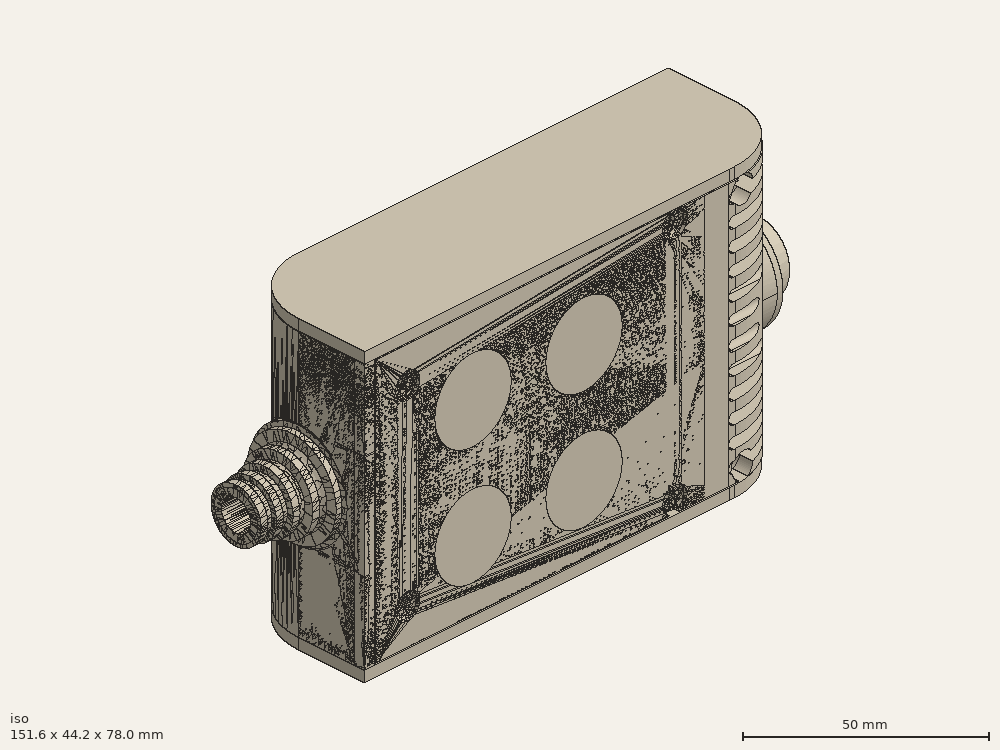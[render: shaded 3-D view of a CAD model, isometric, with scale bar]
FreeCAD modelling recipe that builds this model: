
FCSTD DOCUMENT  (FreeCAD 0.19R0.19.2)
Label: enclosure_197FCStd
License: All rights reserved
LicenseURL: http://en.wikipedia.org/wiki/All_rights_reserved
objects: Part::Revolution×152, Part::MultiFuse×146, Part::Feature×146, Sketcher::SketchObject×84, Part::Cut×70, Part::Cylinder×70, Part::Extrusion×67, Part::Fillet×58, Part::Box×36, App::MeasureDistance×4, PartDesign::Body×2, Image::ImagePlane×1
note: 831 computed .brp shape members not serialized (recipe doc carries the construction recipe); baked Part::Feature solids carry a one-line shape summary decoded from their .brp

FEATURE [Sketcher::SketchObject] Sketch  label="topSketch"
  FullyConstrained = true
  sketch-geometry (20):
    g0: LineSegment StartX=5.21097e-06 StartY=3 StartZ=0 EndX=5.21097e-06 EndY=19 EndZ=0
    g1: ArcOfCircle CenterX=19 CenterY=19 CenterZ=0 NormalX=0 NormalY=0 NormalZ=1 AngleXU=0 Radius=19 StartAngle=1.5708 EndAngle=3.14159
    g2: ArcOfCircle CenterX=19 CenterY=19 CenterZ=0 NormalX=0 NormalY=0 NormalZ=1 AngleXU=0 Radius=16 StartAngle=1.5708 EndAngle=3.14159
    g3: LineSegment StartX=114 StartY=35 StartZ=0 EndX=19 EndY=35 EndZ=0
    g4: LineSegment StartX=5.21097e-06 StartY=3 StartZ=0 EndX=5.21097e-06 EndY=0 EndZ=0
    g5: LineSegment StartX=3 StartY=0 StartZ=0 EndX=5.21097e-06 EndY=0 EndZ=0
    g6: LineSegment StartX=3 StartY=19 StartZ=0 EndX=3 EndY=0 EndZ=0
    g7: LineSegment StartX=19 StartY=38 StartZ=0 EndX=124 EndY=38 EndZ=0
    g8: Circle CenterX=119 CenterY=35 CenterZ=0 NormalX=0 NormalY=0 NormalZ=1 AngleXU=0 Radius=1
    g9: Circle CenterX=121 CenterY=35 CenterZ=0 NormalX=0 NormalY=0 NormalZ=1 AngleXU=0 Radius=1
    g10: Circle CenterX=121 CenterY=33 CenterZ=0 NormalX=0 NormalY=0 NormalZ=1 AngleXU=0 Radius=1
    g11: BSplineCurve PolesCount=3 KnotsCount=2 Degree=2 IsPeriodic=0
    g12: GeomPoint X=119 Y=35 Z=0
    g13: GeomPoint X=121 Y=33 Z=0
    g14: LineSegment StartX=119 StartY=35 StartZ=0 EndX=114 EndY=35 EndZ=0
    g15: ArcOfCircle CenterX=105 CenterY=19 CenterZ=0 NormalX=0 NormalY=0 NormalZ=1 AngleXU=0 Radius=19 StartAngle=5.7297 EndAngle=6.28319
    g16: ArcOfCircle CenterX=105 CenterY=19 CenterZ=0 NormalX=0 NormalY=0 NormalZ=1 AngleXU=0 Radius=16 StartAngle=5.60905 EndAngle=6.28319
    g17: LineSegment StartX=121 StartY=33 StartZ=0 EndX=121 EndY=19 EndZ=0
    g18: LineSegment StartX=124 StartY=38 StartZ=0 EndX=124 EndY=19 EndZ=0
    g19: LineSegment StartX=117.5 StartY=9.01251 StartZ=0 EndX=121.163 EndY=9.0125 EndZ=0
  constraints (46):
    c: Vertical(g0)
    c: Block(g0)
    c: Coincident(g1,g0)
    c: Block(g1)
    c: Coincident(g2,g1)
    c: Block(g2)
    c: Coincident(g3,g2)
    c: Horizontal(g3)
    c: Tangent(g3,g2)
    c: Coincident(g4,g0)
    c: Distance(g4) = 3
    c: Vertical(g4)
    c: Coincident(g5,g4)
    c: Horizontal(g5)
    c: Coincident(g6,g2)
    c: Coincident(g6,g5)
    c: Vertical(g6)
    c: Horizontal(g7)
    c: Distance(g7) = 105
    c: Coincident(g7,g1)
    c: Block(g3)
    c: Weight(g8) = 1
    c: Equal(g8,g9)
    c: Equal(g8,g10)
    c: InternalAlignment(g8,g11)
    c: InternalAlignment(g9,g11)
    c: InternalAlignment(g10,g11)
    c: InternalAlignment(g12,g11)
    c: InternalAlignment(g13,g11)
    c: Block(g11)
    c: Coincident(g14,g11)
    c: Coincident(g14,g3)
    c: Horizontal(g14)
    c: Block(g15)
    c: Coincident(g16,g15)
    c: Block(g16)
    c: Coincident(g17,g11)
    c: Coincident(g17,g16)
    c: Vertical(g17)
    c: Distance(g17) = 14
    c: Coincident(g18,g7)
    c: Coincident(g18,g15)
    c: Vertical(g18)
    c: Distance(g18) = 19
    c: Coincident(g19,g16)
    c: Coincident(g19,g15)
FEATURE [Sketcher::SketchObject] Sketch001  label="bottomSketch"
  FullyConstrained = true
  sketch-geometry (32):
    g0: LineSegment StartX=3.3 StartY=-6.03275e-07 StartZ=0 EndX=98 EndY=-6.03275e-07 EndZ=0
    g1: ArcOfCircle CenterX=98 CenterY=19 CenterZ=0 NormalX=0 NormalY=0 NormalZ=1 AngleXU=0 Radius=19 StartAngle=4.71239 EndAngle=5.71103
    g2: LineSegment StartX=6.3 StartY=8 StartZ=0 EndX=3.3 EndY=8 EndZ=0
    g3: LineSegment StartX=3.3 StartY=8 StartZ=0 EndX=3.3 EndY=-6.03275e-07 EndZ=0
    g4: ArcOfCircle CenterX=8.3 CenterY=5 CenterZ=0 NormalX=0 NormalY=0 NormalZ=1 AngleXU=0 Radius=2 StartAngle=3.14159 EndAngle=4.71239
    g5: LineSegment StartX=6.3 StartY=8 StartZ=0 EndX=6.3 EndY=5 EndZ=0
    g6: ArcOfCircle CenterX=98 CenterY=19 CenterZ=0 NormalX=0 NormalY=0 NormalZ=1 AngleXU=0 Radius=12.7 StartAngle=4.71239 EndAngle=6.28319
    g7: LineSegment StartX=94.7 StartY=3 StartZ=0 EndX=8.3 EndY=3 EndZ=0
    g8-g12: Circle x5 (B-spline internal-alignment scaffolding for g13; pole/knot coordinates omitted)
    g13: BSplineCurve PolesCount=5 KnotsCount=3 Degree=3 IsPeriodic=0
    g14: GeomPoint X=98 Y=6.3 Z=0
    g15: GeomPoint X=96.3938 Y=4.71946 Z=0
    g16: GeomPoint X=94.7 Y=3 Z=0
    g17-g23: Circle x7 (B-spline internal-alignment scaffolding for g24; pole/knot coordinates omitted)
    g24: BSplineCurve PolesCount=7 KnotsCount=5 Degree=3 IsPeriodic=0
    g25-g29: GeomPoint x5 (B-spline internal-alignment scaffolding for g24; pole/knot coordinates omitted)
    g30: ArcOfCircle CenterX=98 CenterY=19 CenterZ=0 NormalX=0 NormalY=0 NormalZ=1 AngleXU=0 Radius=15.7 StartAngle=5.81226 EndAngle=6.28319
    g31: LineSegment StartX=110.7 StartY=19 StartZ=0 EndX=113.7 EndY=19 EndZ=0
  constraints (41):
    c: Horizontal(g0)
    c: Coincident(g1,g0)
    c: Block(g1)
    c: Horizontal(g2)
    c: Distance(g2) = 3
    c: Coincident(g3,g2)
    c: Vertical(g3)
    c: Coincident(g3,g0)
    c: Block(g4)
    c: Block(g2)
    c: Coincident(g5,g2)
    c: Coincident(g5,g4)
    c: Vertical(g5)
    c: Coincident(g6,g1)
    c: Block(g6)
    c: Coincident(g7,g4)
    c: Horizontal(g7)
    c: Block(g0)
    c: Block(g7)
    c: Block(g3)
    c: Coincident(g13,g6)
    c: Weight(g8) = 1
    c: Equal(g8, g9-g12) x4
    c: Coincident(g13,g7)
    c: InternalAlignment(g8-g12 -> g13) x5
    c: InternalAlignment(g14,g13)
    c: InternalAlignment(g15,g13)
    c: InternalAlignment(g16,g13)
    c: Block(g13)
    c: Weight(g17) = 1
    c: Equal(g17, g18-g23) x6
    c: Coincident(g24,g1)
    c: InternalAlignment(g17-g23 -> g24) x7
    c: InternalAlignment(g25-g29 -> g24) x5
    c: Block(g24)
    c: Coincident(g30,g24)
    c: Coincident(g31,g6)
    c: Coincident(g31,g30)
    c: Horizontal(g31)
    c: Block(g31)
    c: Block(g30)
FEATURE [Part::Extrusion] Extrude  label="top"
  Base = -> Sketch
  Dir = (0,0,1)
  DirMode = 2
  FaceMakerClass = Part::FaceMakerBullseye
  LengthFwd = 72
  LengthRev = 0
  Solid = true
  Symmetric = false
FEATURE [Part::Extrusion] Extrude001  label="bottom"
  Base = -> Sketch001
  Dir = (0,0,1)
  DirMode = 2
  FaceMakerClass = Part::FaceMakerBullseye
  LengthFwd = 71.4
  LengthRev = 0
  Placement = pos=(0,0,0.3) rot=(0,0,1;0rad)
  Solid = true
  Symmetric = false
FEATURE [Sketcher::SketchObject] Sketch002  label="topSketch001"
  FullyConstrained = true
  sketch-geometry (8):
    g0: ArcOfCircle CenterX=19 CenterY=19.0975 CenterZ=0 NormalX=0 NormalY=0 NormalZ=1 AngleXU=0 Radius=18.9025 StartAngle=1.5708 EndAngle=3.14674
    g1: LineSegment StartX=0.0977805 StartY=19.0003 StartZ=0 EndX=0.0977805 EndY=0.000251602 EndZ=0
    g2: LineSegment StartX=19 StartY=38 StartZ=0 EndX=124 EndY=38 EndZ=0
    g3: LineSegment StartX=0.0977805 StartY=0.000251602 StartZ=0 EndX=105.098 EndY=0.000251602 EndZ=0
    g4: LineSegment StartX=124 StartY=38 StartZ=0 EndX=125.616 EndY=38 EndZ=0
    g5: LineSegment StartX=105.098 StartY=0.000251602 StartZ=0 EndX=106.713 EndY=0.000251602 EndZ=0
    g6: ArcOfCircle CenterX=106.616 CenterY=19 CenterZ=0 NormalX=0 NormalY=0 NormalZ=1 AngleXU=0 Radius=19 StartAngle=4.71754 EndAngle=6.28319
    g7: LineSegment StartX=125.616 StartY=38 StartZ=0 EndX=125.616 EndY=19 EndZ=0
  constraints (21):
    c: Block(g0)
    c: Coincident(g1,g0)
    c: Vertical(g1)
    c: Horizontal(g2)
    c: Distance(g2) = 105
    c: Coincident(g2,g0)
    c: Distance(g1) = 19
    c: Coincident(g3,g1)
    c: Horizontal(g3)
    c: Distance(g3) = 105
    c: Coincident(g4,g2)
    c: Horizontal(g4)
    c: Distance(g4) = 1.61553
    c: Horizontal(g5)
    c: Equal(g4,g5) = 1.61553
    c: Coincident(g5,g3)
    c: Block(g6)
    c: Coincident(g6,g5)
    c: Coincident(g7,g4)
    c: Coincident(g7,g6)
    c: Vertical(g7)
FEATURE [Part::Extrusion] Extrude002  label="sideA"
  Base = -> Sketch002
  Dir = (0,0,1)
  DirMode = 2
  FaceMakerClass = Part::FaceMakerBullseye
  LengthFwd = 3
  LengthRev = 0
  Placement = pos=(0,0,-3) rot=(0,0,1;0rad)
  Solid = true
  Symmetric = false
FEATURE [Sketcher::SketchObject] Sketch003  label="topSketch002"
  FullyConstrained = true
  sketch-geometry (6):
    g0: LineSegment StartX=19 StartY=38 StartZ=0 EndX=117 EndY=38 EndZ=0
    g1: ArcOfCircle CenterX=19 CenterY=19 CenterZ=0 NormalX=0 NormalY=0 NormalZ=1 AngleXU=0 Radius=19 StartAngle=1.5708 EndAngle=3.14159
    g2: LineSegment StartX=117 StartY=38 StartZ=0 EndX=117 EndY=19 EndZ=0
    g3: LineSegment StartX=98 StartY=1.0161e-12 StartZ=0 EndX=5.22862e-06 EndY=1.0161e-12 EndZ=0
    g4: LineSegment StartX=5.22862e-06 StartY=19 StartZ=0 EndX=5.22862e-06 EndY=1.0161e-12 EndZ=0
    g5: ArcOfCircle CenterX=98 CenterY=19 CenterZ=0 NormalX=0 NormalY=0 NormalZ=1 AngleXU=0 Radius=19 StartAngle=4.71239 EndAngle=6.28319
  constraints (16):
    c: Horizontal(g0)
    c: Distance(g0) = 98
    c: Coincident(g1,g0)
    c: Block(g1)
    c: Coincident(g2,g0)
    c: Vertical(g2)
    c: Distance(g2) = 19
    c: Horizontal(g3)
    c: Coincident(g4,g1)
    c: Vertical(g4)
    c: Coincident(g3,g4)
    c: Block(g3)
    c: Coincident(g5,g2)
    c: Coincident(g5,g3)
    c: Block(g0)
    c: Block(g5)
FEATURE [Sketcher::SketchObject] Sketch004
  FullyConstrained = true
  MapMode = 3
  Placement = pos=(0,0,0) rot=(1,0,0;1.5708rad)
  Support = -> [Extrude]
  sketch-geometry (8):
    g0: Circle CenterX=80.351 CenterY=-67.6202 CenterZ=0 NormalX=0 NormalY=0 NormalZ=1 AngleXU=0 Radius=2
    g1: Circle CenterX=80.351 CenterY=-67.6202 CenterZ=0 NormalX=0 NormalY=0 NormalZ=1 AngleXU=0 Radius=3
    g2: Circle CenterX=80.351 CenterY=-4.92017 CenterZ=0 NormalX=0 NormalY=0 NormalZ=1 AngleXU=0 Radius=2
    g3: Circle CenterX=80.351 CenterY=-4.92017 CenterZ=0 NormalX=0 NormalY=0 NormalZ=1 AngleXU=0 Radius=3
    g4: Circle CenterX=23.851 CenterY=-4.92017 CenterZ=0 NormalX=0 NormalY=0 NormalZ=1 AngleXU=0 Radius=2
    g5: Circle CenterX=23.851 CenterY=-4.92017 CenterZ=0 NormalX=0 NormalY=0 NormalZ=1 AngleXU=0 Radius=3
    g6: Circle CenterX=23.851 CenterY=-67.6202 CenterZ=0 NormalX=0 NormalY=0 NormalZ=1 AngleXU=0 Radius=2
    g7: Circle CenterX=23.851 CenterY=-67.6202 CenterZ=0 NormalX=0 NormalY=0 NormalZ=1 AngleXU=0 Radius=3
  constraints (8):
    c: Block(g3)
    c: Block(g2)
    c: Block(g1)
    c: Block(g0)
    c: Block(g6)
    c: Block(g7)
    c: Block(g4)
    c: Block(g5)
FEATURE [Part::Extrusion] Extrude004
  Base = -> Sketch004
  Dir = (0,-1,2e-16)
  DirMode = 2
  FaceMakerClass = Part::FaceMakerBullseye
  LengthFwd = 6
  LengthRev = 0
  Placement = pos=(0,9,0) rot=(0,0,1;0rad)
  Solid = true
  Symmetric = false
FEATURE [Sketcher::SketchObject] Sketch005
  FullyConstrained = true
  MapMode = 3
  Placement = pos=(0,0,0) rot=(1,0,0;1.5708rad)
  Support = -> [Extrude]
  sketch-geometry (8):
    g0: Circle CenterX=80.351 CenterY=-67.6202 CenterZ=0 NormalX=0 NormalY=0 NormalZ=1 AngleXU=0 Radius=3
    g1: Circle CenterX=80.351 CenterY=-4.92017 CenterZ=0 NormalX=0 NormalY=0 NormalZ=1 AngleXU=0 Radius=3
    g2: Circle CenterX=23.851 CenterY=-4.92017 CenterZ=0 NormalX=0 NormalY=0 NormalZ=1 AngleXU=0 Radius=3
    g3: Circle CenterX=23.851 CenterY=-67.6202 CenterZ=0 NormalX=0 NormalY=0 NormalZ=1 AngleXU=0 Radius=3
    g4: Circle CenterX=23.851 CenterY=-67.6202 CenterZ=0 NormalX=0 NormalY=0 NormalZ=1 AngleXU=0 Radius=5
    g5: Circle CenterX=80.351 CenterY=-67.6202 CenterZ=0 NormalX=0 NormalY=0 NormalZ=1 AngleXU=0 Radius=5
    g6: Circle CenterX=23.851 CenterY=-4.92017 CenterZ=0 NormalX=0 NormalY=0 NormalZ=1 AngleXU=0 Radius=5
    g7: Circle CenterX=80.351 CenterY=-4.92017 CenterZ=0 NormalX=0 NormalY=0 NormalZ=1 AngleXU=0 Radius=5
  constraints (8):
    c: Block(g1)
    c: Block(g0)
    c: Block(g3)
    c: Block(g2)
    c: Block(g5)
    c: Block(g4)
    c: Block(g6)
    c: Block(g7)
FEATURE [Part::Extrusion] Extrude005
  Base = -> Sketch005
  Dir = (0,-1,2e-16)
  DirMode = 2
  FaceMakerClass = Part::FaceMakerBullseye
  LengthFwd = 2
  LengthRev = 0
  Solid = true
  Symmetric = false
FEATURE [Sketcher::SketchObject] Sketch006
  FullyConstrained = true
  MapMode = 3
  Placement = pos=(0,0,0) rot=(1,0,0;1.5708rad)
  sketch-geometry (8):
    g0: Circle CenterX=80.351 CenterY=-67.6202 CenterZ=0 NormalX=0 NormalY=0 NormalZ=1 AngleXU=0 Radius=3
    g1: Circle CenterX=80.351 CenterY=-4.92017 CenterZ=0 NormalX=0 NormalY=0 NormalZ=1 AngleXU=0 Radius=3
    g2: Circle CenterX=23.851 CenterY=-4.92017 CenterZ=0 NormalX=0 NormalY=0 NormalZ=1 AngleXU=0 Radius=3
    g3: Circle CenterX=23.851 CenterY=-67.6202 CenterZ=0 NormalX=0 NormalY=0 NormalZ=1 AngleXU=0 Radius=3
    g4: Circle CenterX=23.851 CenterY=-67.6202 CenterZ=0 NormalX=0 NormalY=0 NormalZ=1 AngleXU=0 Radius=5
    g5: Circle CenterX=80.351 CenterY=-67.6202 CenterZ=0 NormalX=0 NormalY=0 NormalZ=1 AngleXU=0 Radius=5
    g6: Circle CenterX=23.851 CenterY=-4.92017 CenterZ=0 NormalX=0 NormalY=0 NormalZ=1 AngleXU=0 Radius=5
    g7: Circle CenterX=80.351 CenterY=-4.92017 CenterZ=0 NormalX=0 NormalY=0 NormalZ=1 AngleXU=0 Radius=5
  constraints (8):
    c: Block(g1)
    c: Block(g0)
    c: Block(g3)
    c: Block(g2)
    c: Block(g5)
    c: Block(g4)
    c: Block(g6)
    c: Block(g7)
FEATURE [Part::Extrusion] Extrude007
  Base = -> Sketch006
  Dir = (0,-1,2e-16)
  DirMode = 2
  FaceMakerClass = Part::FaceMakerBullseye
  LengthFwd = 2
  LengthRev = 0
  Solid = true
  Symmetric = false
FEATURE [Part::Fillet] Fillet
  Base = -> Extrude007
  Edges = 4 edges r=1.99: [Edge6,Edge12,Edge18,Edge24]
FEATURE [Part::Cut] Cut
  Base = -> Extrude005
  Placement = pos=(0,5,0) rot=(0,0,1;0rad)
  Tool = -> Fillet
FEATURE [Part::MultiFuse] Fusion  label="pCBScrews"
  Placement = pos=(-2.5,0,72.3) rot=(0,0,1;0rad)
  Shapes = -> [Extrude004,Cut]
FEATURE [App::MeasureDistance] Distance  label="Distance: 0.69 mm"
  Distance = 0.685967
  P1 = (24.0138,2.9647,0.3)
  P2 = (23.8901,3,-0.373787)
FEATURE [App::MeasureDistance] Distance001  label="Distance: 0.53 mm"
  Distance = 0.533607
  P1 = (80.2939,3,72.2334)
  P2 = (80.281,2.99661,71.7)
FEATURE [Part::Fillet] Fillet001
  Base = -> Extrude001
  Edges = 1 edges r=2.4: [Edge17]
FEATURE [Part::Fillet] Fillet002  label="bottom001"
  Base = -> Fillet001
  Edges = 1 edges r=2.4: [Edge36]
FEATURE [Part::Fillet] Fillet003  label="top001"
  Base = -> Extrude
  Edges = 1 edges r=2: [Edge1]
FEATURE [Sketcher::SketchObject] Sketch007
  FullyConstrained = true
  sketch-geometry (16):
    g0: LineSegment StartX=4 StartY=0 StartZ=0 EndX=4 EndY=2.4 EndZ=0
    g1: LineSegment StartX=4 StartY=2.4 StartZ=0 EndX=7 EndY=2.4 EndZ=0
    g2: LineSegment StartX=4 StartY=0 StartZ=0 EndX=5.7 EndY=0 EndZ=0
    g3: LineSegment StartX=5.7 StartY=0 StartZ=0 EndX=5.7 EndY=-5.6 EndZ=0
    g4-g8: Circle x5 (B-spline internal-alignment scaffolding for g9; pole/knot coordinates omitted)
    g9: BSplineCurve PolesCount=5 KnotsCount=3 Degree=3 IsPeriodic=0
    g10: GeomPoint X=7 Y=2.4 Z=0
    g11: GeomPoint X=10.4582 Y=-1.55472 Z=0
    g12: GeomPoint X=14 Y=-5.6 Z=0
    g13: LineSegment StartX=14 StartY=-5.6 StartZ=0 EndX=14 EndY=-14.1 EndZ=0
    g14: LineSegment StartX=14 StartY=-14.1 StartZ=0 EndX=6.5 EndY=-14.1 EndZ=0
    g15: LineSegment StartX=5.7 StartY=-5.6 StartZ=0 EndX=6.5 EndY=-14.1 EndZ=0
  constraints (28):
    c: Distance(g0) = 2.4
    c: Vertical(g0)
    c: Block(g0)
    c: Coincident(g1,g0)
    c: Horizontal(g1)
    c: Distance(g1) = 3
    c: Coincident(g2,g0)
    c: Horizontal(g2)
    c: Distance(g2) = 1.7
    c: Coincident(g3,g2)
    c: Vertical(g3)
    c: Distance(g3) = 5.6
    c: Coincident(g9,g1)
    c: Weight(g4) = 1
    c: Equal(g4, g5-g8) x4
    c: InternalAlignment(g4-g8 -> g9) x5
    c: InternalAlignment(g10,g9)
    c: InternalAlignment(g11,g9)
    c: InternalAlignment(g12,g9)
    c: Block(g9)
    c: Coincident(g13,g9)
    c: Vertical(g13)
    c: Distance(g13) = 8.5
    c: Coincident(g14,g13)
    c: Horizontal(g14)
    c: Distance(g14) = 7.5
    c: Coincident(g15,g3)
    c: Coincident(g15,g14)
FEATURE [Part::Feature] Face
  shape: bbox 10 x 16.5 x 2e-07 mm, 1 faces, 0 solids (baked)
FEATURE [Part::Revolution] Revolve  label="plugHousing"
  Angle = 360
  Axis = (0,1,0)
  Base = (0,0,0)
  FaceMakerClass = Part::FaceMakerBullseye
  Placement = pos=(0,0,36.15) rot=(0,0,1;0rad)
  Solid = false
  Source = -> Face
  Symmetric = false
FEATURE [Part::Feature] Face001
  shape: bbox 10 x 16.5 x 2e-07 mm, 1 faces, 0 solids (baked)
FEATURE [Part::Revolution] Revolve001  label="plugHousing001"
  Angle = 360
  Axis = (0,1,0)
  Base = (0,0,0)
  FaceMakerClass = Part::FaceMakerBullseye
  Placement = pos=(0,0,36.15) rot=(0,0,1;0rad)
  Solid = false
  Source = -> Face001
  Symmetric = false
FEATURE [Part::MultiFuse] Fusion001  label="plugHousing002"
  Placement = pos=(0,0,0) rot=(0,0,1;1.5708rad)
  Shapes = -> [Revolve001,Revolve]
FEATURE [Part::Feature] Face002
  shape: bbox 10 x 16.5 x 2e-07 mm, 1 faces, 0 solids (baked)
FEATURE [Part::Revolution] Revolve003  label="plugHousing005"
  Angle = 360
  Axis = (0,1,0)
  Base = (0,0,0)
  FaceMakerClass = Part::FaceMakerBullseye
  Placement = pos=(0,0,36.15) rot=(0,0,1;0rad)
  Solid = false
  Source = -> Face002
  Symmetric = false
FEATURE [Part::Feature] Face003
  shape: bbox 10 x 16.5 x 2e-07 mm, 1 faces, 0 solids (baked)
FEATURE [Part::Revolution] Revolve002  label="plugHousing003"
  Angle = 360
  Axis = (0,1,0)
  Base = (0,0,0)
  FaceMakerClass = Part::FaceMakerBullseye
  Placement = pos=(0,0,36.15) rot=(0,0,1;0rad)
  Solid = false
  Source = -> Face003
  Symmetric = false
FEATURE [Part::MultiFuse] Fusion002  label="plugHousing004"
  Placement = pos=(0,0,0) rot=(0,0,1;1.5708rad)
  Shapes = -> [Revolve002,Revolve003]
FEATURE [Part::MultiFuse] Fusion003  label="plugHousing006"
  Placement = pos=(0,19,0) rot=(0,0,1;3.14159rad)
  Shapes = -> [Fusion002,Fusion001]
FEATURE [Part::Feature] Face004
  shape: bbox 10 x 16.5 x 2e-07 mm, 1 faces, 0 solids (baked)
FEATURE [Part::Revolution] Revolve006  label="plugHousing010"
  Angle = 360
  Axis = (0,1,0)
  Base = (0,0,0)
  FaceMakerClass = Part::FaceMakerBullseye
  Placement = pos=(0,0,36.15) rot=(0,0,1;0rad)
  Solid = false
  Source = -> Face004
  Symmetric = false
FEATURE [Part::Feature] Face005
  shape: bbox 10 x 16.5 x 2e-07 mm, 1 faces, 0 solids (baked)
FEATURE [Part::Revolution] Revolve007  label="plugHousing011"
  Angle = 360
  Axis = (0,1,0)
  Base = (0,0,0)
  FaceMakerClass = Part::FaceMakerBullseye
  Placement = pos=(0,0,36.15) rot=(0,0,1;0rad)
  Solid = false
  Source = -> Face005
  Symmetric = false
FEATURE [Part::Feature] Face006
  shape: bbox 10 x 16.5 x 2e-07 mm, 1 faces, 0 solids (baked)
FEATURE [Part::Revolution] Revolve004  label="plugHousing007"
  Angle = 360
  Axis = (0,1,0)
  Base = (0,0,0)
  FaceMakerClass = Part::FaceMakerBullseye
  Placement = pos=(0,0,36.15) rot=(0,0,1;0rad)
  Solid = false
  Source = -> Face006
  Symmetric = false
FEATURE [Part::MultiFuse] Fusion004  label="plugHousing009"
  Placement = pos=(0,0,0) rot=(0,0,1;1.5708rad)
  Shapes = -> [Revolve004,Revolve007]
FEATURE [Part::Feature] Face007
  shape: bbox 10 x 16.5 x 2e-07 mm, 1 faces, 0 solids (baked)
FEATURE [Part::Revolution] Revolve005  label="plugHousing008"
  Angle = 360
  Axis = (0,1,0)
  Base = (0,0,0)
  FaceMakerClass = Part::FaceMakerBullseye
  Placement = pos=(0,0,36.15) rot=(0,0,1;0rad)
  Solid = false
  Source = -> Face007
  Symmetric = false
FEATURE [Part::MultiFuse] Fusion005  label="plugHousing012"
  Placement = pos=(0,0,0) rot=(0,0,1;1.5708rad)
  Shapes = -> [Revolve006,Revolve005]
FEATURE [Part::MultiFuse] Fusion006  label="plugHousing013"
  Placement = pos=(0,19,0) rot=(0,0,1;3.14159rad)
  Shapes = -> [Fusion005,Fusion004]
FEATURE [Part::MultiFuse] Fusion007  label="plugHousing014"
  Placement = pos=(122.621,0,-0.15) rot=(0,0,1;0rad)
  Shapes = -> [Fusion003,Fusion006]
FEATURE [Part::Cylinder] Cylinder002
  Angle = 360
  AttacherType = Attacher::AttachEngine3D
  Height = 20
  Placement = pos=(0,0,36.15) rot=(0,0,1;0rad)
  Radius = 4
FEATURE [Part::Cylinder] Cylinder003
  Angle = 360
  AttacherType = Attacher::AttachEngine3D
  Height = 10
  Placement = pos=(0,0,36.15) rot=(0,0,1;0rad)
  Radius = 4
FEATURE [Part::MultiFuse] Fusion009  label="removeToCreateHoleForPlugHousing"
  Placement = pos=(70,19,36.15) rot=(0,1,0;1.5708rad)
  Shapes = -> [Cylinder002,Cylinder003]
FEATURE [Part::Cylinder] Cylinder004
  Angle = 360
  AttacherType = Attacher::AttachEngine3D
  Height = 20
  Placement = pos=(0,0,36.15) rot=(0,0,1;0rad)
  Radius = 4
FEATURE [Part::Cylinder] Cylinder005
  Angle = 360
  AttacherType = Attacher::AttachEngine3D
  Height = 10
  Placement = pos=(0,0,36.15) rot=(0,0,1;0rad)
  Radius = 4
FEATURE [Part::MultiFuse] Fusion010  label="removeToCreateHoleForPlugHousing001"
  Placement = pos=(70,19,36.15) rot=(0,1,0;1.5708rad)
  Shapes = -> [Cylinder004,Cylinder005]
FEATURE [Part::Cut] Cut001
  Base = -> Fillet003
  Tool = -> Fusion010
FEATURE [Part::Cut] Cut002  label="Bottom"
  Base = -> Fillet002
  Tool = -> Fusion009
FEATURE [Part::Feature] Face008
  shape: bbox 10 x 16.5 x 2e-07 mm, 1 faces, 0 solids (baked)
FEATURE [Part::Revolution] Revolve011  label="plugHousing021"
  Angle = 360
  Axis = (0,1,0)
  Base = (0,0,0)
  FaceMakerClass = Part::FaceMakerBullseye
  Placement = pos=(0,0,36.15) rot=(0,0,1;0rad)
  Solid = false
  Source = -> Face008
  Symmetric = false
FEATURE [Part::Feature] Face009
  shape: bbox 10 x 16.5 x 2e-07 mm, 1 faces, 0 solids (baked)
FEATURE [Part::Revolution] Revolve012  label="plugHousing022"
  Angle = 360
  Axis = (0,1,0)
  Base = (0,0,0)
  FaceMakerClass = Part::FaceMakerBullseye
  Placement = pos=(0,0,36.15) rot=(0,0,1;0rad)
  Solid = false
  Source = -> Face009
  Symmetric = false
FEATURE [Part::Feature] Face010 .. Face013  x4 (patterned run collapsed; names and placements below)
  shape: bbox 10 x 16.5 x 2e-07 mm, 1 faces, 0 solids (baked)
FEATURE [Part::Revolution] Revolve015  label="plugHousing027"
  Angle = 360
  Axis = (0,1,0)
  Base = (0,0,0)
  FaceMakerClass = Part::FaceMakerBullseye
  Placement = pos=(0,0,36.15) rot=(0,0,1;0rad)
  Solid = false
  Source = -> Face013
  Symmetric = false
FEATURE [Part::Feature] Face014
  shape: bbox 10 x 16.5 x 2e-07 mm, 1 faces, 0 solids (baked)
FEATURE [Part::Feature] Face015
  shape: bbox 10 x 16.5 x 2e-07 mm, 1 faces, 0 solids (baked)
FEATURE [Part::Feature] Face016
  shape: bbox 10 x 16.5 x 2e-07 mm, 1 faces, 0 solids (baked)
FEATURE [Part::Revolution] Revolve019  label="plugHousing033"
  Angle = 360
  Axis = (0,1,0)
  Base = (0,0,0)
  FaceMakerClass = Part::FaceMakerBullseye
  Placement = pos=(0,0,36.15) rot=(0,0,1;0rad)
  Solid = false
  Source = -> Face016
  Symmetric = false
FEATURE [Part::Feature] Face017
  shape: bbox 10 x 16.5 x 2e-07 mm, 1 faces, 0 solids (baked)
FEATURE [Part::Revolution] Revolve020  label="plugHousing034"
  Angle = 360
  Axis = (0,1,0)
  Base = (0,0,0)
  FaceMakerClass = Part::FaceMakerBullseye
  Placement = pos=(0,0,36.15) rot=(0,0,1;0rad)
  Solid = false
  Source = -> Face017
  Symmetric = false
FEATURE [Part::Feature] Face018
  shape: bbox 10 x 16.5 x 2e-07 mm, 1 faces, 0 solids (baked)
FEATURE [Part::Revolution] Revolve016  label="plugHousing030"
  Angle = 360
  Axis = (0,1,0)
  Base = (0,0,0)
  FaceMakerClass = Part::FaceMakerBullseye
  Placement = pos=(0,0,36.15) rot=(0,0,1;0rad)
  Solid = false
  Source = -> Face018
  Symmetric = false
FEATURE [Part::MultiFuse] Fusion020  label="plugHousing038"
  Placement = pos=(0,0,0) rot=(0,0,1;1.5708rad)
  Shapes = -> [Revolve016,Revolve020]
FEATURE [Part::Feature] Face019
  shape: bbox 10 x 16.5 x 2e-07 mm, 1 faces, 0 solids (baked)
FEATURE [Part::Feature] Face020
  shape: bbox 10 x 16.5 x 2e-07 mm, 1 faces, 0 solids (baked)
FEATURE [Part::Revolution] Revolve017  label="plugHousing031"
  Angle = 360
  Axis = (0,1,0)
  Base = (0,0,0)
  FaceMakerClass = Part::FaceMakerBullseye
  Placement = pos=(0,0,36.15) rot=(0,0,1;0rad)
  Solid = false
  Source = -> Face020
  Symmetric = false
FEATURE [Part::MultiFuse] Fusion021  label="plugHousing039"
  Placement = pos=(0,0,0) rot=(0,0,1;1.5708rad)
  Shapes = -> [Revolve019,Revolve017]
FEATURE [Part::MultiFuse] Fusion023  label="plugHousing041"
  Placement = pos=(0,19,0) rot=(0,0,1;3.14159rad)
  Shapes = -> [Fusion021,Fusion020]
FEATURE [Part::Revolution] Revolve022  label="plugHousing043"
  Angle = 360
  Axis = (0,1,0)
  Base = (0,0,0)
  FaceMakerClass = Part::FaceMakerBullseye
  Placement = pos=(0,0,36.15) rot=(0,0,1;0rad)
  Solid = false
  Source = -> Face019
  Symmetric = false
FEATURE [Part::Feature] Face021
  shape: bbox 10 x 16.5 x 2e-07 mm, 1 faces, 0 solids (baked)
FEATURE [Part::Revolution] Revolve023  label="plugHousing044"
  Angle = 360
  Axis = (0,1,0)
  Base = (0,0,0)
  FaceMakerClass = Part::FaceMakerBullseye
  Placement = pos=(0,0,36.15) rot=(0,0,1;0rad)
  Solid = false
  Source = -> Face021
  Symmetric = false
FEATURE [Part::Feature] Face022
  shape: bbox 10 x 16.5 x 2e-07 mm, 1 faces, 0 solids (baked)
FEATURE [Part::Revolution] Revolve018  label="plugHousing032"
  Angle = 360
  Axis = (0,1,0)
  Base = (0,0,0)
  FaceMakerClass = Part::FaceMakerBullseye
  Placement = pos=(0,0,36.15) rot=(0,0,1;0rad)
  Solid = false
  Source = -> Face022
  Symmetric = false
FEATURE [Part::MultiFuse] Fusion022  label="plugHousing040"
  Placement = pos=(0,0,0) rot=(0,0,1;1.5708rad)
  Shapes = -> [Revolve018,Revolve023]
FEATURE [Part::Feature] Face023
  shape: bbox 10 x 16.5 x 2e-07 mm, 1 faces, 0 solids (baked)
FEATURE [Part::Revolution] Revolve021  label="plugHousing035"
  Angle = 360
  Axis = (0,1,0)
  Base = (0,0,0)
  FaceMakerClass = Part::FaceMakerBullseye
  Placement = pos=(0,0,36.15) rot=(0,0,1;0rad)
  Solid = false
  Source = -> Face023
  Symmetric = false
FEATURE [Part::MultiFuse] Fusion018  label="plugHousing036"
  Placement = pos=(0,0,0) rot=(0,0,1;1.5708rad)
  Shapes = -> [Revolve022,Revolve021]
FEATURE [Part::MultiFuse] Fusion019  label="plugHousing037"
  Placement = pos=(0,19,0) rot=(0,0,1;3.14159rad)
  Shapes = -> [Fusion018,Fusion022]
FEATURE [Part::MultiFuse] Fusion024  label="plugHousing042"
  Placement = pos=(122.621,0,-0.15) rot=(0,0,1;0rad)
  Shapes = -> [Fusion023,Fusion019]
FEATURE [Part::Cylinder] Cylinder006
  Angle = 360
  AttacherType = Attacher::AttachEngine3D
  Height = 20
  Placement = pos=(0,0,36.15) rot=(0,0,1;0rad)
  Radius = 14.3
FEATURE [Part::Cylinder] Cylinder007
  Angle = 360
  AttacherType = Attacher::AttachEngine3D
  Height = 10
  Placement = pos=(0,0,36.15) rot=(0,0,1;0rad)
  Radius = 4
FEATURE [Part::MultiFuse] Fusion026  label="removeToCreteHoleForPlugHousing"
  Placement = pos=(70,19,36) rot=(0,1,0;1.5708rad)
  Shapes = -> [Cylinder006,Cylinder007]
FEATURE [Part::Box] Box001  label="Cube001"
  AttacherType = Attacher::AttachEngine3D
  Height = 28
  Length = 3
  Placement = pos=(110.7,19,22) rot=(0,0,1;0rad)
  Width = 15.7
FEATURE [Part::Cut] Cut003  label="top002"
  Base = -> Cut001
  Tool = -> Fusion007
FEATURE [Part::Revolution] Revolve008  label="plugHousing015"
  Angle = 360
  Axis = (0,1,0)
  Base = (0,0,0)
  FaceMakerClass = Part::FaceMakerBullseye
  Placement = pos=(0,0,36.15) rot=(0,0,1;0rad)
  Solid = false
  Source = -> Face010
  Symmetric = false
FEATURE [Part::MultiFuse] Fusion013  label="plugHousing020"
  Placement = pos=(0,0,0) rot=(0,0,1;1.5708rad)
  Shapes = -> [Revolve008,Revolve012]
FEATURE [Part::Cut] Cut004  label="top003"
  Base = -> Cut003
  Placement = pos=(1,0,0) rot=(0,0,1;0rad)
  Tool = -> Fusion026
FEATURE [Part::Cylinder] Cylinder008
  Angle = 360
  AttacherType = Attacher::AttachEngine3D
  Height = 20
  Placement = pos=(0,0,36.15) rot=(0,0,1;0rad)
  Radius = 10.3
FEATURE [Part::Cylinder] Cylinder009
  Angle = 360
  AttacherType = Attacher::AttachEngine3D
  Height = 10
  Placement = pos=(0,0,36.15) rot=(0,0,1;0rad)
  Radius = 4
FEATURE [Part::MultiFuse] Fusion027  label="removeToCreteHoleForPlugHousing001"
  Placement = pos=(70,19,36) rot=(0,1,0;1.5708rad)
  Shapes = -> [Cylinder008,Cylinder009]
FEATURE [Part::Cut] Cut005  label="plugHousingTab"
  Base = -> Box001
  Tool = -> Fusion027
FEATURE [Part::MultiFuse] Fusion028  label="plugHousing045"
  Shapes = -> [Fusion024,Cut005]
FEATURE [Part::Box] Box002  label="Cube002"
  AttacherType = Attacher::AttachEngine3D
  Height = 28.8
  Length = 3
  Placement = pos=(107.3,28,21.6) rot=(0,0,1;0rad)
  Width = 7
FEATURE [Part::Box] Box003  label="Cube003"
  AttacherType = Attacher::AttachEngine3D
  Height = 3
  Length = 6.4
  Placement = pos=(107.3,28,18.6) rot=(0,0,1;0rad)
  Width = 7
FEATURE [Part::Box] Box004  label="Cube004"
  AttacherType = Attacher::AttachEngine3D
  Height = 3
  Length = 6.4
  Placement = pos=(107.3,28,50.4) rot=(0,0,1;0rad)
  Width = 7
FEATURE [Part::MultiFuse] Fusion029  label="plugHousingBracketHolder"
  Shapes = -> [Box004,Box002,Box003]
FEATURE [Part::Cylinder] Cylinder010
  Angle = 360
  AttacherType = Attacher::AttachEngine3D
  Height = 20
  Placement = pos=(0,0,36.15) rot=(0,0,1;0rad)
  Radius = 14.3
FEATURE [Part::Cylinder] Cylinder011
  Angle = 360
  AttacherType = Attacher::AttachEngine3D
  Height = 10
  Placement = pos=(0,0,36.15) rot=(0,0,1;0rad)
  Radius = 4
FEATURE [Part::MultiFuse] Fusion030  label="removeToCreteHoleForPlugHousing002"
  Placement = pos=(70,19,36) rot=(0,1,0;1.5708rad)
  Shapes = -> [Cylinder010,Cylinder011]
FEATURE [Part::Cut] Cut006  label="plugHousingBracketHolder001"
  Base = -> Fusion029
  Tool = -> Fusion030
FEATURE [Part::Cylinder] Cylinder012
  Angle = 360
  AttacherType = Attacher::AttachEngine3D
  Height = 20
  Placement = pos=(0,0,36.15) rot=(0,0,1;0rad)
  Radius = 7
FEATURE [Part::Cylinder] Cylinder013
  Angle = 360
  AttacherType = Attacher::AttachEngine3D
  Height = 10
  Placement = pos=(0,0,36.15) rot=(0,0,1;0rad)
  Radius = 4
FEATURE [Part::MultiFuse] Fusion032  label="removeToCreteHoleForPlugHousing003"
  Placement = pos=(70,19,36) rot=(0,1,0;1.5708rad)
  Shapes = -> [Cylinder012,Cylinder013]
FEATURE [Part::Cut] Cut007  label="bottom002"
  Base = -> Cut002
  Tool = -> Fusion032
FEATURE [Sketcher::SketchObject] Sketch008
  FullyConstrained = true
  sketch-geometry (54):
    g0: LineSegment StartX=-4.2 StartY=0 StartZ=0 EndX=-6.2 EndY=0 EndZ=0
    g1: LineSegment StartX=-14 StartY=-18 StartZ=0 EndX=-14 EndY=-26.5 EndZ=0
    g2: LineSegment StartX=-4.2 StartY=0 StartZ=0 EndX=-4.2 EndY=-13.4877 EndZ=0
    g3: Circle CenterX=-4.2 CenterY=-13.4877 CenterZ=0 NormalX=0 NormalY=0 NormalZ=1 AngleXU=0 Radius=1
    g4: Circle CenterX=-4.2 CenterY=-26.5 CenterZ=0 NormalX=0 NormalY=0 NormalZ=1 AngleXU=0 Radius=1
    g5: Circle CenterX=-8.2 CenterY=-26.5 CenterZ=0 NormalX=0 NormalY=0 NormalZ=1 AngleXU=0 Radius=1
    g6: BSplineCurve PolesCount=3 KnotsCount=2 Degree=2 IsPeriodic=0
    g7: GeomPoint X=-4.2 Y=-13.4877 Z=0
    g8: GeomPoint X=-8.2 Y=-26.5 Z=0
    g9: LineSegment StartX=-14 StartY=-26.5 StartZ=0 EndX=-8.2 EndY=-26.5 EndZ=0
    g10: LineSegment StartX=-10.15 StartY=-12 StartZ=0 EndX=-10.15 EndY=-14 EndZ=0
    g11: LineSegment StartX=-12.8401 StartY=-16 StartZ=0 EndX=-10.1571 EndY=-16 EndZ=0
    g12: LineSegment StartX=-10.15 StartY=-14 StartZ=0 EndX=-8.70761 EndY=-14 EndZ=0
    g13: LineSegment StartX=-12.8401 StartY=-16 StartZ=0 EndX=-12.8401 EndY=-17.6958 EndZ=0
    g14: LineSegment StartX=-10.15 StartY=-12 StartZ=0 EndX=-7.79258 EndY=-12 EndZ=0
    g15: Circle CenterX=-6.2215 CenterY=-2 CenterZ=0 NormalX=0 NormalY=0 NormalZ=1 AngleXU=0 Radius=1
    g16: Circle CenterX=-6.22762 CenterY=-2.58724 CenterZ=0 NormalX=0 NormalY=0 NormalZ=1 AngleXU=0 Radius=1
    g17: Circle CenterX=-6.32538 CenterY=-4 CenterZ=0 NormalX=0 NormalY=0 NormalZ=1 AngleXU=0 Radius=1
    g18: BSplineCurve PolesCount=3 KnotsCount=2 Degree=2 IsPeriodic=0
    g19: GeomPoint X=-6.2215 Y=-2 Z=0
    g20: GeomPoint X=-6.32538 Y=-4 Z=0
    g21: Circle CenterX=-6.48644 CenterY=-5.99526 CenterZ=0 NormalX=0 NormalY=0 NormalZ=1 AngleXU=0 Radius=1
    g22: Circle CenterX=-6.58486 CenterY=-6.99526 CenterZ=0 NormalX=0 NormalY=0 NormalZ=1 AngleXU=0 Radius=1
    g23: Circle CenterX=-6.77343 CenterY=-8 CenterZ=0 NormalX=0 NormalY=0 NormalZ=1 AngleXU=0 Radius=1
    g24: BSplineCurve PolesCount=3 KnotsCount=2 Degree=2 IsPeriodic=0
    g25: GeomPoint X=-6.48644 Y=-5.99526 Z=0
    g26: GeomPoint X=-6.77343 Y=-8 Z=0
    g27: Circle CenterX=-7.19003 CenterY=-10 CenterZ=0 NormalX=0 NormalY=0 NormalZ=1 AngleXU=0 Radius=1
    g28: Circle CenterX=-7.44407 CenterY=-11.0915 CenterZ=0 NormalX=0 NormalY=0 NormalZ=1 AngleXU=0 Radius=1
    g29: Circle CenterX=-7.79258 CenterY=-12 CenterZ=0 NormalX=0 NormalY=0 NormalZ=1 AngleXU=0 Radius=1
    g30: BSplineCurve PolesCount=3 KnotsCount=2 Degree=2 IsPeriodic=0
    g31: GeomPoint X=-7.19003 Y=-10 Z=0
    g32: GeomPoint X=-7.79258 Y=-12 Z=0
    g33: Circle CenterX=-8.70761 CenterY=-14 CenterZ=0 NormalX=0 NormalY=0 NormalZ=1 AngleXU=0 Radius=1
    g34: Circle CenterX=-9.33087 CenterY=-15.1837 CenterZ=0 NormalX=0 NormalY=0 NormalZ=1 AngleXU=0 Radius=1
    g35: Circle CenterX=-10.1571 CenterY=-16 CenterZ=0 NormalX=0 NormalY=0 NormalZ=1 AngleXU=0 Radius=1
    g36: BSplineCurve PolesCount=3 KnotsCount=2 Degree=2 IsPeriodic=0
    g37: GeomPoint X=-8.70761 Y=-14 Z=0
    g38: GeomPoint X=-10.1571 Y=-16 Z=0
    g39: Circle CenterX=-12.8401 CenterY=-17.6958 CenterZ=0 NormalX=0 NormalY=0 NormalZ=1 AngleXU=0 Radius=1
    g40: Circle CenterX=-13.3521 CenterY=-17.9027 CenterZ=0 NormalX=0 NormalY=0 NormalZ=1 AngleXU=0 Radius=1
    g41: Circle CenterX=-14 CenterY=-18 CenterZ=0 NormalX=0 NormalY=0 NormalZ=1 AngleXU=0 Radius=1
    g42: BSplineCurve PolesCount=3 KnotsCount=2 Degree=2 IsPeriodic=0
    g43: GeomPoint X=-12.8401 Y=-17.6958 Z=0
    g44: GeomPoint X=-14 Y=-18 Z=0
    g45: LineSegment StartX=-6.2 StartY=0 StartZ=0 EndX=-7.2 EndY=0 EndZ=0
    g46: LineSegment StartX=-7.2 StartY=0 StartZ=0 EndX=-7.2 EndY=-2 EndZ=0
    g47: LineSegment StartX=-7.2 StartY=-2 StartZ=0 EndX=-6.2215 EndY=-2 EndZ=0
    g48: LineSegment StartX=-6.32538 StartY=-4 StartZ=0 EndX=-7.65538 EndY=-4 EndZ=0
    g49: LineSegment StartX=-7.65538 StartY=-4 StartZ=0 EndX=-7.65538 EndY=-5.99526 EndZ=0
    g50: LineSegment StartX=-7.65538 StartY=-5.99526 StartZ=0 EndX=-6.48644 EndY=-5.99526 EndZ=0
    g51: LineSegment StartX=-6.77343 StartY=-8 StartZ=0 EndX=-8.43343 EndY=-8 EndZ=0
    g52: LineSegment StartX=-8.43343 StartY=-8 StartZ=0 EndX=-8.43343 EndY=-10 EndZ=0
    g53: LineSegment StartX=-8.43343 StartY=-10 StartZ=0 EndX=-7.19003 EndY=-10 EndZ=0
  constraints (112):
    c: Horizontal(g0)
    c: Distance(g0) = 2
    c: Block(g0)
    c: Vertical(g1)
    c: Coincident(g2,g0)
    c: Vertical(g2)
    c: Block(g2)
    c: Coincident(g6,g2)
    c: Weight(g3) = 1
    c: Equal(g3,g4)
    c: Equal(g3,g5)
    c: InternalAlignment(g3,g6)
    c: InternalAlignment(g4,g6)
    c: InternalAlignment(g5,g6)
    c: InternalAlignment(g7,g6)
    c: InternalAlignment(g8,g6)
    c: Block(g6)
    c: Coincident(g9,g1)
    c: Coincident(g9,g6)
    c: Horizontal(g9)
    c: Vertical(g10)
    c: Block(g10)
    c: Horizontal(g11)
    c: Block(g11)
    c: Coincident(g12,g10)
    c: Horizontal(g12)
    c: Block(g12)
    c: Coincident(g13,g11)
    c: Vertical(g13)
    c: Block(g13)
    c: Coincident(g14,g10)
    c: Horizontal(g14)
    c: Block(g14)
    c: Block(g9)
    c: Block(g1)
    c: Weight(g15) = 1
    c: Equal(g15,g16)
    c: Equal(g15,g17)
    c: InternalAlignment(g15,g18)
    c: InternalAlignment(g16,g18)
    c: InternalAlignment(g17,g18)
    c: InternalAlignment(g19,g18)
    c: InternalAlignment(g20,g18)
    c: Weight(g21) = 1
    c: Equal(g21,g22)
    c: Equal(g21,g23)
    c: InternalAlignment(g21,g24)
    c: InternalAlignment(g22,g24)
    c: InternalAlignment(g23,g24)
    c: InternalAlignment(g25,g24)
    c: InternalAlignment(g26,g24)
    c: Weight(g27) = 1
    c: Equal(g27,g28)
    c: Equal(g27,g29)
    c: Coincident(g30,g14)
    c: InternalAlignment(g27,g30)
    c: InternalAlignment(g28,g30)
    c: InternalAlignment(g29,g30)
    c: InternalAlignment(g31,g30)
    c: InternalAlignment(g32,g30)
    c: Coincident(g36,g12)
    c: Weight(g33) = 1
    c: Equal(g33,g34)
    c: Equal(g33,g35)
    c: Coincident(g36,g11)
    c: InternalAlignment(g33,g36)
    c: InternalAlignment(g34,g36)
    c: InternalAlignment(g35,g36)
    c: InternalAlignment(g37,g36)
    c: InternalAlignment(g38,g36)
    c: Coincident(g42,g13)
    c: Weight(g39) = 1
    c: Equal(g39,g40)
    c: Equal(g39,g41)
    c: Coincident(g42,g1)
    c: InternalAlignment(g39,g42)
    c: InternalAlignment(g40,g42)
    c: InternalAlignment(g41,g42)
    c: InternalAlignment(g43,g42)
    c: InternalAlignment(g44,g42)
    c: Block(g18)
    c: Block(g24)
    c: Block(g30)
    c: Block(g36)
    c: Block(g42)
    c: Horizontal(g45)
    c: Coincident(g45,g0)
    c: Vertical(g46)
    c: Coincident(g46,g45)
    c: Coincident(g47,g46)
    c: Coincident(g47,g18)
    c: Horizontal(g47)
    c: Block(g46)
    c: Coincident(g48,g18)
    c: Horizontal(g48)
    c: Distance(g48) = 1.33
    c: Vertical(g49)
    c: Coincident(g49,g48)
    c: Coincident(g50,g49)
    c: Coincident(g50,g24)
    c: Horizontal(g50)
    c: Tangent(g50,g22)
    c: Horizontal(g51)
    c: Coincident(g51,g24)
    c: Block(g51)
    c: Vertical(g52)
    c: Block(g52)
    c: Coincident(g52,g51)
    c: Coincident(g53,g52)
    c: Coincident(g53,g30)
    c: Horizontal(g53)
    c: Distance(g1) = 8.5
FEATURE [Part::Feature] Face024
  shape: bbox 9.8 x 26.5 x 2e-07 mm, 1 faces, 0 solids (baked)
FEATURE [Part::Revolution] Revolve024
  Angle = 360
  Axis = (0,1,0)
  Base = (0,0,0)
  FaceMakerClass = Part::FaceMakerBullseye
  Placement = pos=(0,0,0) rot=(0,0,1;1.5708rad)
  Solid = false
  Source = -> Face024
  Symmetric = false
FEATURE [Part::Feature] Face025
  shape: bbox 9.8 x 26.5 x 2e-07 mm, 1 faces, 0 solids (baked)
FEATURE [Part::Revolution] Revolve025
  Angle = 360
  Axis = (0,1,0)
  Base = (0,0,0)
  FaceMakerClass = Part::FaceMakerBullseye
  Placement = pos=(0,0,0) rot=(0,0,1;1.5708rad)
  Solid = false
  Source = -> Face025
  Symmetric = false
FEATURE [Part::MultiFuse] Fusion033
  Placement = pos=(-18,19,36) rot=(0,0,1;0rad)
  Shapes = -> [Revolve025,Revolve024]
FEATURE [Part::Cylinder] Cylinder014
  Angle = 360
  AttacherType = Attacher::AttachEngine3D
  Height = 20
  Placement = pos=(0,0,36.15) rot=(0,0,1;0rad)
  Radius = 14.3
FEATURE [Part::Cylinder] Cylinder015
  Angle = 360
  AttacherType = Attacher::AttachEngine3D
  Height = 10
  Placement = pos=(0,0,36.15) rot=(0,0,1;0rad)
  Radius = 4
FEATURE [Part::MultiFuse] Fusion034  label="removeToCreteHoleForPlugHousing004"
  Placement = pos=(-42,19,36) rot=(0,1,0;1.5708rad)
  Shapes = -> [Cylinder014,Cylinder015]
FEATURE [Part::Cut] Cut008  label="top004"
  Base = -> Cut004
  Placement = pos=(-1,0,0) rot=(0,0,1;0rad)
  Tool = -> Fusion034
FEATURE [Part::Box] Box005  label="Cube005"
  AttacherType = Attacher::AttachEngine3D
  Height = 28
  Length = 3
  Placement = pos=(110.7,19,22) rot=(0,0,1;0rad)
  Width = 15.7
FEATURE [Part::Cylinder] Cylinder016
  Angle = 360
  AttacherType = Attacher::AttachEngine3D
  Height = 10
  Placement = pos=(0,0,36.15) rot=(0,0,1;0rad)
  Radius = 4
FEATURE [Part::Cylinder] Cylinder017
  Angle = 360
  AttacherType = Attacher::AttachEngine3D
  Height = 20
  Placement = pos=(0,0,36.15) rot=(0,0,1;0rad)
  Radius = 10.3
FEATURE [Part::MultiFuse] Fusion035  label="removeToCreteHoleForPlugHousing005"
  Placement = pos=(70,19,36) rot=(0,1,0;1.5708rad)
  Shapes = -> [Cylinder017,Cylinder016]
FEATURE [Part::Cut] Cut009  label="plugHousingTab001"
  Base = -> Box005
  Placement = pos=(-107.4,-14,0) rot=(0,0,1;0rad)
  Tool = -> Fusion035
FEATURE [Part::Box] Box006  label="Cube006"
  AttacherType = Attacher::AttachEngine3D
  Height = 28
  Length = 3
  Placement = pos=(110.7,19,22) rot=(0,0,1;0rad)
  Width = 15.7
FEATURE [Part::Cylinder] Cylinder018
  Angle = 360
  AttacherType = Attacher::AttachEngine3D
  Height = 10
  Placement = pos=(0,0,36.15) rot=(0,0,1;0rad)
  Radius = 4
FEATURE [Part::Cylinder] Cylinder019
  Angle = 360
  AttacherType = Attacher::AttachEngine3D
  Height = 20
  Placement = pos=(0,0,36.15) rot=(0,0,1;0rad)
  Radius = 10.3
FEATURE [Part::MultiFuse] Fusion036  label="removeToCreteHoleForPlugHousing006"
  Placement = pos=(70,19,36) rot=(0,1,0;1.5708rad)
  Shapes = -> [Cylinder019,Cylinder018]
FEATURE [Part::Cut] Cut010  label="plugHousingTab002"
  Base = -> Box006
  Placement = pos=(-107.4,-14,0) rot=(0,0,1;0rad)
  Tool = -> Fusion036
FEATURE [Part::MultiFuse] Fusion037
  Placement = pos=(9.6,23,0) rot=(0,0,1;3.14159rad)
  Shapes = -> [Cut009,Cut010]
FEATURE [Part::Box] Box  label="Cube"
  AttacherType = Attacher::AttachEngine3D
  Height = 10
  Length = 3
  Placement = pos=(3.3,4,12) rot=(0,0,1;0rad)
  Width = 10
FEATURE [Part::Fillet] Fillet004
  Base = -> Fusion028
  Edges = 1 edges r=2: [Edge25]
FEATURE [Part::Fillet] Fillet005  label="plugHousing046"
  Base = -> Fillet004
  Edges = 1 edges r=2: [Edge8]
FEATURE [Part::Fillet] Fillet006
  Base = -> Box
  Edges = 1 edges r=2: [Edge11]
FEATURE [Part::Box] Box007  label="Cube007"
  AttacherType = Attacher::AttachEngine3D
  Height = 10
  Length = 3
  Placement = pos=(3.3,4,50) rot=(0,0,1;0rad)
  Width = 10
FEATURE [Part::Fillet] Fillet007
  Base = -> Box007
  Edges = 1 edges r=2: [Edge12]
FEATURE [Part::Box] Box008  label="Cube008"
  AttacherType = Attacher::AttachEngine3D
  Height = 28
  Length = 4
  Placement = pos=(5,0,22) rot=(0,0,1;0rad)
  Width = 10
FEATURE [Part::Fillet] Fillet008
  Base = -> Box008
  Edges = 1 edges r=1: [Edge7]
FEATURE [Part::Fillet] Fillet009
  Base = -> Fillet008
  Edges = 1 edges r=2: [Edge5]
FEATURE [Part::Fillet] Fillet010
  Base = -> Fillet009
  Edges = 1 edges r=2: [Edge2]
FEATURE [Sketcher::SketchObject] Sketch009  label="topSketch003"
  FullyConstrained = true
  sketch-geometry (4):
    g0: LineSegment StartX=16.8446 StartY=31.512 StartZ=0 EndX=16.3251 EndY=34.4666 EndZ=0
    g1: ArcOfCircle CenterX=19 CenterY=19.2524 CenterZ=0 NormalX=0 NormalY=0 NormalZ=1 AngleXU=0 Radius=15.4476 StartAngle=1.74483 EndAngle=2.72717
    g2: ArcOfCircle CenterX=19 CenterY=19.2524 CenterZ=0 NormalX=0 NormalY=0 NormalZ=1 AngleXU=0 Radius=12.4476 StartAngle=1.74483 EndAngle=2.73189
    g3: LineSegment StartX=4.86004 StartY=25.4725 StartZ=0 EndX=7.58253 EndY=24.2107 EndZ=0
  constraints (7):
    c: Block(g0)
    c: Coincident(g1,g0)
    c: Coincident(g2,g0)
    c: Coincident(g3,g1)
    c: Coincident(g3,g2)
    c: Block(g1)
    c: Block(g2)
FEATURE [Part::Extrusion] Extrude008
  Base = -> Sketch009
  Dir = (0,0,1)
  DirMode = 2
  FaceMakerClass = Part::FaceMakerBullseye
  LengthFwd = 10
  LengthRev = 0
  Placement = pos=(0,0,31) rot=(0,0,1;0rad)
  Solid = true
  Symmetric = false
FEATURE [Part::Cylinder] Cylinder020
  Angle = 360
  AttacherType = Attacher::AttachEngine3D
  Height = 20
  Placement = pos=(0,0,36.15) rot=(0,0,1;0rad)
  Radius = 8.2
FEATURE [Part::Cylinder] Cylinder021
  Angle = 360
  AttacherType = Attacher::AttachEngine3D
  Height = 10
  Placement = pos=(0,0,36.15) rot=(0,0,1;0rad)
  Radius = 4
FEATURE [Part::MultiFuse] Fusion038  label="removeToCreteHoleForPlugHousing007"
  Placement = pos=(-42,19,36) rot=(0,1,0;1.5708rad)
  Shapes = -> [Cylinder020,Cylinder021]
FEATURE [Part::Cut] Cut011
  Base = -> Extrude008
  Tool = -> Fusion038
FEATURE [Part::Fillet] Fillet011
  Base = -> Cut011
  Edges = 1 edges r=2: [Edge1]
FEATURE [Part::Fillet] Fillet012
  Base = -> Fillet011
  Edges = 1 edges r=2.5: [Edge1]
FEATURE [Part::Fillet] Fillet013
  Base = -> Fillet012
  Edges = 1 edges r=2.5: [Edge2]
FEATURE [Part::Box] Box010  label="Cube010"
  AttacherType = Attacher::AttachEngine3D
  Height = 16
  Length = 8
  Placement = pos=(12.7,31.52,28) rot=(0,0,1;0rad)
  Width = 4
FEATURE [Sketcher::SketchObject] Sketch010  label="topSketch004"
  FullyConstrained = true
  sketch-geometry (4):
    g0: LineSegment StartX=16.8446 StartY=31.512 StartZ=0 EndX=16.3251 EndY=34.4666 EndZ=0
    g1: ArcOfCircle CenterX=19 CenterY=19.2524 CenterZ=0 NormalX=0 NormalY=0 NormalZ=1 AngleXU=0 Radius=15.4476 StartAngle=1.74483 EndAngle=2.72717
    g2: ArcOfCircle CenterX=19 CenterY=19.2524 CenterZ=0 NormalX=0 NormalY=0 NormalZ=1 AngleXU=0 Radius=12.4476 StartAngle=1.74483 EndAngle=2.73189
    g3: LineSegment StartX=4.86004 StartY=25.4725 StartZ=0 EndX=7.58253 EndY=24.2107 EndZ=0
  constraints (7):
    c: Block(g0)
    c: Coincident(g1,g0)
    c: Coincident(g2,g0)
    c: Coincident(g3,g1)
    c: Coincident(g3,g2)
    c: Block(g1)
    c: Block(g2)
FEATURE [Part::Cylinder] Cylinder022
  Angle = 360
  AttacherType = Attacher::AttachEngine3D
  Height = 10
  Placement = pos=(0,0,36.15) rot=(0,0,1;0rad)
  Radius = 4
FEATURE [Sketcher::SketchObject] Sketch011  label="topSketch005"
  FullyConstrained = true
  sketch-geometry (4):
    g0: LineSegment StartX=16.8446 StartY=31.512 StartZ=0 EndX=16.3251 EndY=34.4666 EndZ=0
    g1: ArcOfCircle CenterX=19 CenterY=19.2524 CenterZ=0 NormalX=0 NormalY=0 NormalZ=1 AngleXU=0 Radius=15.4476 StartAngle=1.74483 EndAngle=2.72717
    g2: ArcOfCircle CenterX=19 CenterY=19.2524 CenterZ=0 NormalX=0 NormalY=0 NormalZ=1 AngleXU=0 Radius=12.4476 StartAngle=1.74483 EndAngle=2.73189
    g3: LineSegment StartX=4.86004 StartY=25.4725 StartZ=0 EndX=7.58253 EndY=24.2107 EndZ=0
  constraints (7):
    c: Block(g0)
    c: Coincident(g1,g0)
    c: Coincident(g2,g0)
    c: Coincident(g3,g1)
    c: Coincident(g3,g2)
    c: Block(g1)
    c: Block(g2)
FEATURE [Part::Extrusion] Extrude010
  Base = -> Sketch011
  Dir = (0,0,1)
  DirMode = 2
  FaceMakerClass = Part::FaceMakerBullseye
  LengthFwd = 10.6
  LengthRev = 0
  Placement = pos=(0,0,31) rot=(0,0,1;0rad)
  Solid = true
  Symmetric = false
FEATURE [Part::Cylinder] Cylinder023
  Angle = 360
  AttacherType = Attacher::AttachEngine3D
  Height = 20
  Placement = pos=(0,0,36.15) rot=(0,0,1;0rad)
  Radius = 8.2
FEATURE [Part::MultiFuse] Fusion039  label="removeToCreteHoleForPlugHousing008"
  Placement = pos=(-42,19,36) rot=(0,1,0;1.5708rad)
  Shapes = -> [Cylinder023,Cylinder022]
FEATURE [Part::Cut] Cut012
  Base = -> Extrude010
  Placement = pos=(0,0,-0.3) rot=(0,0,1;0rad)
  Tool = -> Fusion039
FEATURE [Part::Cut] Cut013
  Base = -> Box010
  Tool = -> Cut012
FEATURE [Part::Fillet] Fillet014
  Base = -> Cut013
  Edges = 1 edges r=0.7: [Edge13]
FEATURE [Part::Fillet] Fillet015
  Base = -> Fillet014
  Edges = 1 edges r=0.7: [Edge13]
FEATURE [Part::Fillet] Fillet016
  Base = -> Fillet015
  Edges = 1 edges r=0.7: [Edge16]
FEATURE [Part::Fillet] Fillet017
  Base = -> Fillet016
  Edges = 1 edges r=0.7: [Edge11]
FEATURE [Part::Fillet] Fillet018
  Base = -> Fillet017
  Edges = 1 edges r=0.7: [Edge10]
FEATURE [Part::Fillet] Fillet019
  Base = -> Fillet018
  Edges = 1 edges r=1.2: [Edge5]
FEATURE [Part::Fillet] Fillet020
  Base = -> Fillet019
  Edges = 1 edges r=1.2: [Edge12]
FEATURE [Part::Fillet] Fillet021
  Base = -> Fillet020
  Edges = 1 edges r=2: [Edge1]
  Placement = pos=(0.3,0,0) rot=(0,0,1;0rad)
FEATURE [Part::MultiFuse] Fusion040  label="top005"
  Shapes = -> [Cut008,Fillet021]
FEATURE [Part::MultiFuse] Fusion041  label="wireHolder"
  Shapes = -> [Fusion033,Fillet013]
FEATURE [Part::MultiFuse] Fusion042
  Shapes = -> [Fillet007,Fusion041]
FEATURE [Part::MultiFuse] Fusion043  label="wireHolder001"
  Shapes = -> [Fusion042,Fillet010]
FEATURE [Part::MultiFuse] Fusion044  label="wireHolder002"
  Shapes = -> [Fillet006,Fusion037,Fusion043]
FEATURE [Part::Feature] Face026
  shape: bbox 11 x 6 x 2e-07 mm, 1 faces, 0 solids (baked)
FEATURE [Part::Revolution] Revolve026
  Angle = 360
  Axis = (0,1,0)
  Base = (0,0,0)
  FaceMakerClass = Part::FaceMakerBullseye
  Placement = pos=(30.3,-1,19.7) rot=(0,0,1;0rad)
  Solid = false
  Source = -> Face026
  Symmetric = false
FEATURE [Sketcher::SketchObject] Sketch013  label="topSketch006"
  FullyConstrained = true
  sketch-geometry (13):
    g0: LineSegment StartX=117 StartY=19 StartZ=0 EndX=117 EndY=38 EndZ=0
    g1: ArcOfCircle CenterX=98 CenterY=19 CenterZ=0 NormalX=0 NormalY=0 NormalZ=1 AngleXU=0 Radius=19 StartAngle=5.7297 EndAngle=6.28319
    g2: LineSegment StartX=0 StartY=3 StartZ=0 EndX=0 EndY=19 EndZ=0
    g3: LineSegment StartX=19 StartY=38 StartZ=0 EndX=117 EndY=38 EndZ=0
    g4: ArcOfCircle CenterX=19 CenterY=19 CenterZ=0 NormalX=0 NormalY=0 NormalZ=1 AngleXU=0 Radius=19 StartAngle=1.5708 EndAngle=3.14159
    g5: ArcOfCircle CenterX=19 CenterY=19 CenterZ=0 NormalX=0 NormalY=0 NormalZ=1 AngleXU=0 Radius=16 StartAngle=1.5708 EndAngle=3.14159
    g6: ArcOfCircle CenterX=98 CenterY=19 CenterZ=0 NormalX=0 NormalY=0 NormalZ=1 AngleXU=0 Radius=16 StartAngle=5.60905 EndAngle=6.28319
    g7: LineSegment StartX=114 StartY=19 StartZ=0 EndX=114 EndY=35 EndZ=0
    g8: LineSegment StartX=110.5 StartY=9.01251 StartZ=0 EndX=114.163 EndY=9.01251 EndZ=0
    g9: LineSegment StartX=114 StartY=35 StartZ=0 EndX=19 EndY=35 EndZ=0
    g10: LineSegment StartX=0 StartY=3 StartZ=0 EndX=0 EndY=0 EndZ=0
    g11: LineSegment StartX=3 StartY=0 StartZ=0 EndX=0 EndY=0 EndZ=0
    g12: LineSegment StartX=3 StartY=19 StartZ=0 EndX=3 EndY=0 EndZ=0
  constraints (33):
    c: Vertical(g0)
    c: Distance(g0) = 19
    c: Block(g0)
    c: Coincident(g1,g0)
    c: Block(g1)
    c: Vertical(g2)
    c: Block(g2)
    c: Coincident(g3,g0)
    c: Horizontal(g3)
    c: Distance(g3) = 98
    c: Coincident(g4,g3)
    c: Coincident(g4,g2)
    c: Block(g4)
    c: Coincident(g5,g4)
    c: Coincident(g6,g1)
    c: Block(g6)
    c: Block(g5)
    c: Coincident(g7,g6)
    c: Vertical(g7)
    c: Coincident(g8,g6)
    c: Coincident(g8,g1)
    c: Coincident(g9,g7)
    c: Coincident(g9,g5)
    c: Horizontal(g9)
    c: Tangent(g9,g5)
    c: Coincident(g10,g2)
    c: Distance(g10) = 3
    c: Vertical(g10)
    c: Coincident(g11,g10)
    c: Horizontal(g11)
    c: Coincident(g12,g5)
    c: Coincident(g12,g11)
    c: Vertical(g12)
FEATURE [Part::Extrusion] Extrude011  label="top006"
  Base = -> Sketch013
  Dir = (0,0,1)
  DirMode = 2
  FaceMakerClass = Part::FaceMakerBullseye
  LengthFwd = 72
  LengthRev = 0
  Solid = true
  Symmetric = false
FEATURE [Sketcher::SketchObject] Sketch014
  FullyConstrained = true
  MapMode = 3
  Placement = pos=(0,0,0) rot=(1,0,0;1.5708rad)
  Support = -> [Extrude011]
  sketch-geometry (8):
    g0: Circle CenterX=80.351 CenterY=-67.6202 CenterZ=0 NormalX=0 NormalY=0 NormalZ=1 AngleXU=0 Radius=2
    g1: Circle CenterX=80.351 CenterY=-67.6202 CenterZ=0 NormalX=0 NormalY=0 NormalZ=1 AngleXU=0 Radius=3
    g2: Circle CenterX=80.351 CenterY=-4.92017 CenterZ=0 NormalX=0 NormalY=0 NormalZ=1 AngleXU=0 Radius=2
    g3: Circle CenterX=80.351 CenterY=-4.92017 CenterZ=0 NormalX=0 NormalY=0 NormalZ=1 AngleXU=0 Radius=3
    g4: Circle CenterX=23.851 CenterY=-4.92017 CenterZ=0 NormalX=0 NormalY=0 NormalZ=1 AngleXU=0 Radius=2
    g5: Circle CenterX=23.851 CenterY=-4.92017 CenterZ=0 NormalX=0 NormalY=0 NormalZ=1 AngleXU=0 Radius=3
    g6: Circle CenterX=23.851 CenterY=-67.6202 CenterZ=0 NormalX=0 NormalY=0 NormalZ=1 AngleXU=0 Radius=2
    g7: Circle CenterX=23.851 CenterY=-67.6202 CenterZ=0 NormalX=0 NormalY=0 NormalZ=1 AngleXU=0 Radius=3
  constraints (8):
    c: Block(g3)
    c: Block(g2)
    c: Block(g1)
    c: Block(g0)
    c: Block(g6)
    c: Block(g7)
    c: Block(g4)
    c: Block(g5)
FEATURE [Part::Feature] Face027
  shape: bbox 11 x 6 x 2e-07 mm, 1 faces, 0 solids (baked)
FEATURE [Part::Revolution] Revolve027
  Angle = 360
  Axis = (0,1,0)
  Base = (0,0,0)
  FaceMakerClass = Part::FaceMakerBullseye
  Placement = pos=(30.3,-1,51.7) rot=(0,0,1;0rad)
  Solid = false
  Source = -> Face027
  Symmetric = false
FEATURE [Part::Feature] Face028
  shape: bbox 11 x 6 x 2e-07 mm, 1 faces, 0 solids (baked)
FEATURE [Part::Revolution] Revolve028
  Angle = 360
  Axis = (0,1,0)
  Base = (0,0,0)
  FaceMakerClass = Part::FaceMakerBullseye
  Placement = pos=(62.3,-1,19.7) rot=(0,0,1;0rad)
  Solid = false
  Source = -> Face028
  Symmetric = false
FEATURE [Part::Feature] Face029
  shape: bbox 11 x 6 x 2e-07 mm, 1 faces, 0 solids (baked)
FEATURE [Part::Revolution] Revolve029
  Angle = 360
  Axis = (0,1,0)
  Base = (0,0,0)
  FaceMakerClass = Part::FaceMakerBullseye
  Placement = pos=(62.3,-1,51.7) rot=(0,0,1;0rad)
  Solid = false
  Source = -> Face029
  Symmetric = false
FEATURE [Part::Feature] Wire
  shape: bbox 11 x 5.2 x 2e-07 mm, 0 faces, 0 solids (baked)
FEATURE [Part::Revolution] Revolve030
  Angle = 360
  Axis = (0,1,0)
  Base = (0,0,0)
  FaceMakerClass = Part::FaceMakerBullseye
  Placement = pos=(30.3,38,19.7) rot=(0,0,1;0rad)
  Solid = true
  Source = -> Wire
  Symmetric = false
FEATURE [Part::Feature] Wire001
  shape: bbox 11 x 5.2 x 2e-07 mm, 0 faces, 0 solids (baked)
FEATURE [Part::Revolution] Revolve031
  Angle = 360
  Axis = (0,1,0)
  Base = (0,0,0)
  FaceMakerClass = Part::FaceMakerBullseye
  Placement = pos=(30.3,38,51.7) rot=(0,0,1;0rad)
  Solid = true
  Source = -> Wire001
  Symmetric = false
FEATURE [Part::Feature] Wire002
  shape: bbox 11 x 5.2 x 2e-07 mm, 0 faces, 0 solids (baked)
FEATURE [Part::Revolution] Revolve032
  Angle = 360
  Axis = (0,1,0)
  Base = (0,0,0)
  FaceMakerClass = Part::FaceMakerBullseye
  Placement = pos=(62.3,38,51.7) rot=(0,0,1;0rad)
  Solid = true
  Source = -> Wire002
  Symmetric = false
FEATURE [Part::Feature] Wire003
  shape: bbox 11 x 5.2 x 2e-07 mm, 0 faces, 0 solids (baked)
FEATURE [Part::Revolution] Revolve033
  Angle = 360
  Axis = (0,1,0)
  Base = (0,0,0)
  FaceMakerClass = Part::FaceMakerBullseye
  Placement = pos=(62.3,38,19.7) rot=(0,0,1;0rad)
  Solid = true
  Source = -> Wire003
  Symmetric = false
FEATURE [Part::MultiFuse] Fusion045  label="altRandScrewHousing"
  Shapes = -> [Revolve029,Revolve027,Revolve028,Revolve026]
FEATURE [Part::MultiFuse] Fusion046  label="fanScrewHousing"
  Shapes = -> [Revolve033,Revolve032,Revolve031,Revolve030]
FEATURE [Sketcher::SketchObject] Sketch015
  FullyConstrained = true
  sketch-geometry (17):
    g0: Circle CenterX=-3.5 CenterY=23.5 CenterZ=0 NormalX=0 NormalY=0 NormalZ=1 AngleXU=0 Radius=1
    g1: Circle CenterX=-1 CenterY=15.25 CenterZ=0 NormalX=0 NormalY=0 NormalZ=1 AngleXU=0 Radius=1
    g2: Circle CenterX=-3.5 CenterY=7 CenterZ=0 NormalX=0 NormalY=0 NormalZ=1 AngleXU=0 Radius=1
    g3: BSplineCurve PolesCount=3 KnotsCount=2 Degree=2 IsPeriodic=0
    g4: GeomPoint X=-3.5 Y=23.5 Z=0
    g5: GeomPoint X=-3.5 Y=7 Z=0
    g6: Circle CenterX=-4.8 CenterY=30.5 CenterZ=0 NormalX=0 NormalY=0 NormalZ=1 AngleXU=0 Radius=1
    g7: Circle CenterX=-3.5 CenterY=30.5 CenterZ=0 NormalX=0 NormalY=0 NormalZ=1 AngleXU=0 Radius=1
    g8: Circle CenterX=-3.5 CenterY=29.2 CenterZ=0 NormalX=0 NormalY=0 NormalZ=1 AngleXU=0 Radius=1
    g9: BSplineCurve PolesCount=3 KnotsCount=2 Degree=2 IsPeriodic=0
    g10: GeomPoint X=-4.8 Y=30.5 Z=0
    g11: GeomPoint X=-3.5 Y=29.2 Z=0
    g12: LineSegment StartX=-3.5 StartY=29.2 StartZ=0 EndX=-3.5 EndY=23.5 EndZ=0
    g13: LineSegment StartX=-4.8 StartY=30.5 StartZ=0 EndX=0 EndY=30.5 EndZ=0
    g14: LineSegment StartX=-3.5 StartY=0.3 StartZ=0 EndX=0 EndY=0.3 EndZ=0
    g15: LineSegment StartX=-3.5 StartY=0.3 StartZ=0 EndX=-3.5 EndY=7 EndZ=0
    g16: LineSegment StartX=0 StartY=0.3 StartZ=0 EndX=0 EndY=30.5 EndZ=0
  constraints (33):
    c: Weight(g0) = 1
    c: Equal(g0,g1)
    c: Equal(g0,g2)
    c: InternalAlignment(g0,g3)
    c: InternalAlignment(g1,g3)
    c: InternalAlignment(g2,g3)
    c: InternalAlignment(g4,g3)
    c: InternalAlignment(g5,g3)
    c: Block(g3)
    c: Weight(g6) = 1
    c: Equal(g6,g7)
    c: Equal(g6,g8)
    c: InternalAlignment(g6,g9)
    c: InternalAlignment(g7,g9)
    c: InternalAlignment(g8,g9)
    c: InternalAlignment(g10,g9)
    c: InternalAlignment(g11,g9)
    c: Block(g9)
    c: Coincident(g12,g9)
    c: Coincident(g12,g3)
    c: Vertical(g12)
    c: Coincident(g13,g9)
    c: Horizontal(g13)
    c: Distance(g13) = 4.8
    c: Horizontal(g14)
    c: Block(g14)
    c: Coincident(g15,g14)
    c: Coincident(g15,g3)
    c: Vertical(g15)
    c: Coincident(g16,g14)
    c: Coincident(g16,g13)
    c: Vertical(g16)
    c: Tangent(g16,g1)
FEATURE [Sketcher::SketchObject] Sketch016
  FullyConstrained = true
  sketch-geometry (16):
    g0: Circle CenterX=-3.5 CenterY=23.5 CenterZ=0 NormalX=0 NormalY=0 NormalZ=1 AngleXU=0 Radius=1
    g1: Circle CenterX=-1 CenterY=15.25 CenterZ=0 NormalX=0 NormalY=0 NormalZ=1 AngleXU=0 Radius=1
    g2: Circle CenterX=-3.5 CenterY=7 CenterZ=0 NormalX=0 NormalY=0 NormalZ=1 AngleXU=0 Radius=1
    g3: BSplineCurve PolesCount=3 KnotsCount=2 Degree=2 IsPeriodic=0
    g4: GeomPoint X=-3.5 Y=23.5 Z=0
    g5: GeomPoint X=-3.5 Y=7 Z=0
    g6: LineSegment StartX=-3.5 StartY=28.2 StartZ=0 EndX=-3.5 EndY=23.5 EndZ=0
    g7: LineSegment StartX=0 StartY=29.5 StartZ=0 EndX=0 EndY=30 EndZ=0
    g8: LineSegment StartX=-3.5 StartY=28.2 StartZ=0 EndX=-3.5 EndY=30 EndZ=0
    g9: LineSegment StartX=0 StartY=30 StartZ=0 EndX=0 EndY=30.5 EndZ=0
    g10: LineSegment StartX=0 StartY=30.5 StartZ=0 EndX=-3.5 EndY=30.5 EndZ=0
    g11: LineSegment StartX=-3.5 StartY=30.5 StartZ=0 EndX=-3.5 EndY=30 EndZ=0
    g12: LineSegment StartX=0 StartY=29.5 StartZ=0 EndX=0 EndY=5 EndZ=0
    g13: LineSegment StartX=-3.5 StartY=0.3 StartZ=0 EndX=-3.5 EndY=7 EndZ=0
    g14: LineSegment StartX=-3.5 StartY=0.3 StartZ=0 EndX=0 EndY=0.3 EndZ=0
    g15: LineSegment StartX=0 StartY=5 StartZ=0 EndX=0 EndY=0.3 EndZ=0
  constraints (39):
    c: Weight(g0) = 1
    c: Equal(g0,g1)
    c: Equal(g0,g2)
    c: InternalAlignment(g0,g3)
    c: InternalAlignment(g1,g3)
    c: InternalAlignment(g2,g3)
    c: InternalAlignment(g4,g3)
    c: InternalAlignment(g5,g3)
    c: Block(g3)
    c: Coincident(g6,g3)
    c: Vertical(g6)
    c: Vertical(g7)
    c: Distance(g7) = 0.5
    c: Coincident(g8,g6)
    c: Vertical(g8)
    c: Block(g6)
    c: Block(g7)
    c: Vertical(g9)
    c: Equal(g7,g9) = 0.5
    c: Block(g9)
    c: Coincident(g9,g7)
    c: Horizontal(g10)
    c: Coincident(g10,g9)
    c: Coincident(g11,g10)
    c: Coincident(g11,g8)
    c: Vertical(g11)
    c: Block(g11)
    c: Coincident(g12,g7)
    c: Vertical(g12)
    c: Coincident(g13,g3)
    c: Vertical(g13)
    c: Distance(g13) = 6.7
    c: Coincident(g14,g13)
    c: Horizontal(g14)
    c: Block(g14)
    c: Coincident(g15,g12)
    c: Coincident(g15,g14)
    c: Vertical(g15)
    c: Block(g15)
FEATURE [Sketcher::SketchObject] Sketch017
  FullyConstrained = true
  sketch-geometry (11):
    g0: LineSegment StartX=-3.5 StartY=1e-16 StartZ=0 EndX=-1.6 EndY=1e-16 EndZ=0
    g1: LineSegment StartX=-1.6 StartY=1e-16 StartZ=0 EndX=-1.6 EndY=1.5 EndZ=0
    g2: LineSegment StartX=-3.5 StartY=1.5 StartZ=0 EndX=-1.6 EndY=1.5 EndZ=0
    g3: LineSegment StartX=-3.5 StartY=1e-16 StartZ=0 EndX=-4.8 EndY=1e-16 EndZ=0
    g4: Circle CenterX=-3.5 CenterY=1.3 CenterZ=0 NormalX=0 NormalY=0 NormalZ=1 AngleXU=0 Radius=1
    g5: Circle CenterX=-3.5 CenterY=1e-16 CenterZ=0 NormalX=0 NormalY=0 NormalZ=1 AngleXU=0 Radius=1
    g6: Circle CenterX=-4.8 CenterY=1e-16 CenterZ=0 NormalX=0 NormalY=0 NormalZ=1 AngleXU=0 Radius=1
    g7: BSplineCurve PolesCount=3 KnotsCount=2 Degree=2 IsPeriodic=0
    g8: GeomPoint X=-3.5 Y=1.3 Z=0
    g9: GeomPoint X=-4.8 Y=1e-16 Z=0
    g10: LineSegment StartX=-3.5 StartY=1.3 StartZ=0 EndX=-3.5 EndY=1.5 EndZ=0
  constraints (24):
    c: Horizontal(g0)
    c: Distance(g0) = 1.9
    c: Block(g0)
    c: Coincident(g1,g0)
    c: Vertical(g1)
    c: Coincident(g2,g1)
    c: Horizontal(g2)
    c: Coincident(g3,g0)
    c: Horizontal(g3)
    c: Distance(g3) = 1.3
    c: Weight(g4) = 1
    c: Equal(g4,g5)
    c: Coincident(g5,g0)
    c: Equal(g4,g6)
    c: Coincident(g7,g3)
    c: InternalAlignment(g4,g7)
    c: InternalAlignment(g5,g7)
    c: InternalAlignment(g6,g7)
    c: InternalAlignment(g8,g7)
    c: InternalAlignment(g9,g7)
    c: Coincident(g10,g7)
    c: Coincident(g10,g2)
    c: Vertical(g10)
    c: Block(g10)
FEATURE [Part::Feature] Face035
  shape: bbox 3.2 x 1.5 x 2e-07 mm, 1 faces, 0 solids (baked)
FEATURE [Part::Revolution] Revolve039  label="backCaseScrewRetainer"
  Angle = 360
  Axis = (0,1,0)
  Base = (0,0,0)
  FaceMakerClass = Part::FaceMakerBullseye
  Placement = pos=(12.5,3,62) rot=(0,0,1;0rad)
  Solid = false
  Source = -> Face035
  Symmetric = false
FEATURE [Part::Feature] Face036
  shape: bbox 3.2 x 1.5 x 2e-07 mm, 1 faces, 0 solids (baked)
FEATURE [Part::Feature] Face039
  shape: bbox 4.8 x 30.2 x 2e-07 mm, 1 faces, 0 solids (baked)
FEATURE [Part::Revolution] Revolve043  label="frontCaseScrewPost002"
  Angle = 360
  Axis = (0,1,0)
  Base = (0,0,0)
  FaceMakerClass = Part::FaceMakerBullseye
  Placement = pos=(89.5,4.5,3.5) rot=(0,0,1;0rad)
  Solid = false
  Source = -> Face039
  Symmetric = false
FEATURE [Part::Feature] Face042
  shape: bbox 4.8 x 30.2 x 2e-07 mm, 1 faces, 0 solids (baked)
FEATURE [Part::Revolution] Revolve046  label="frontCaseScrewPost003"
  Angle = 360
  Axis = (0,1,0)
  Base = (0,0,0)
  FaceMakerClass = Part::FaceMakerBullseye
  Placement = pos=(89.5,4.5,68.5) rot=(0,0,1;0rad)
  Solid = false
  Source = -> Face042
  Symmetric = false
FEATURE [Part::Feature] Face043
  shape: bbox 3.2 x 1.5 x 2e-07 mm, 1 faces, 0 solids (baked)
FEATURE [Part::Revolution] Revolve047  label="frontCaseScrewRetainer002"
  Angle = 360
  Axis = (0,1,0)
  Base = (0,0,0)
  FaceMakerClass = Part::FaceMakerBullseye
  Placement = pos=(89.5,3,68.5) rot=(0,0,1;0rad)
  Solid = false
  Source = -> Face043
  Symmetric = false
FEATURE [Part::Feature] Face044
  shape: bbox 3.2 x 1.5 x 2e-07 mm, 1 faces, 0 solids (baked)
FEATURE [Part::Revolution] Revolve048  label="frontCaseScrewRetainer003"
  Angle = 360
  Axis = (0,1,0)
  Base = (0,0,0)
  FaceMakerClass = Part::FaceMakerBullseye
  Placement = pos=(89.5,3,3.5) rot=(0,0,1;0rad)
  Solid = false
  Source = -> Face044
  Symmetric = false
FEATURE [App::MeasureDistance] Distance002  label="Distance: 1.67 mm"
  Distance = 1.66921
  P1 = (99.2361,4.7524,71.7)
  P2 = (99.2347,6.42161,71.7)
FEATURE [Sketcher::SketchObject] Sketch018
  FullyConstrained = true
  sketch-geometry (7):
    g0: LineSegment StartX=0 StartY=0 StartZ=0 EndX=0 EndY=6 EndZ=0
    g1: Circle CenterX=0 CenterY=0 CenterZ=0 NormalX=0 NormalY=0 NormalZ=1 AngleXU=0 Radius=1
    g2: Circle CenterX=8 CenterY=6 CenterZ=0 NormalX=0 NormalY=0 NormalZ=1 AngleXU=0 Radius=1
    g3: BSplineCurve PolesCount=3 KnotsCount=2 Degree=2 IsPeriodic=0
    g4: GeomPoint X=0 Y=0 Z=0
    g5: GeomPoint X=8 Y=6 Z=0
    g6: LineSegment StartX=0 StartY=6 StartZ=0 EndX=8 EndY=6 EndZ=0
  constraints (14):
    c: Coincident(g0,g-1)
    c: Distance(g0) = 6
    c: Vertical(g0)
    c: Coincident(g3,g0)
    c: Weight(g1) = 1
    c: Equal(g1,g2)
    c: InternalAlignment(g1,g3)
    c: InternalAlignment(g2,g3)
    c: InternalAlignment(g4,g3)
    c: InternalAlignment(g5,g3)
    c: Block(g3)
    c: Coincident(g6,g0)
    c: Coincident(g6,g3)
    c: Horizontal(g6)
FEATURE [Part::Extrusion] Extrude012  label="caseScrewPillarBracket"
  Base = -> Sketch018
  Dir = (0,0,1)
  DirMode = 2
  FaceMakerClass = Part::FaceMakerBullseye
  LengthFwd = 2.4
  LengthRev = 0
  Placement = pos=(15.76,29,8.8) rot=(0,1,0;0rad)
  Solid = true
  Symmetric = false
FEATURE [Sketcher::SketchObject] Sketch019
  FullyConstrained = true
  sketch-geometry (7):
    g0: LineSegment StartX=0 StartY=0 StartZ=0 EndX=0 EndY=6 EndZ=0
    g1: Circle CenterX=0 CenterY=0 CenterZ=0 NormalX=0 NormalY=0 NormalZ=1 AngleXU=0 Radius=1
    g2: Circle CenterX=8 CenterY=6 CenterZ=0 NormalX=0 NormalY=0 NormalZ=1 AngleXU=0 Radius=1
    g3: BSplineCurve PolesCount=3 KnotsCount=2 Degree=2 IsPeriodic=0
    g4: GeomPoint X=0 Y=0 Z=0
    g5: GeomPoint X=8 Y=6 Z=0
    g6: LineSegment StartX=0 StartY=6 StartZ=0 EndX=8 EndY=6 EndZ=0
  constraints (14):
    c: Coincident(g0,g-1)
    c: Distance(g0) = 6
    c: Vertical(g0)
    c: Coincident(g3,g0)
    c: Weight(g1) = 1
    c: Equal(g1,g2)
    c: InternalAlignment(g1,g3)
    c: InternalAlignment(g2,g3)
    c: InternalAlignment(g4,g3)
    c: InternalAlignment(g5,g3)
    c: Block(g3)
    c: Coincident(g6,g0)
    c: Coincident(g6,g3)
    c: Horizontal(g6)
FEATURE [Part::Extrusion] Extrude013  label="caseScrewPillarBracket001"
  Base = -> Sketch019
  Dir = (0,0,1)
  DirMode = 2
  FaceMakerClass = Part::FaceMakerBullseye
  LengthFwd = 2.4
  LengthRev = 0
  Placement = pos=(15.76,29,60.8) rot=(0,0,1;0rad)
  Solid = true
  Symmetric = false
FEATURE [Sketcher::SketchObject] Sketch020
  FullyConstrained = true
  sketch-geometry (7):
    g0: LineSegment StartX=0 StartY=0 StartZ=0 EndX=0 EndY=6 EndZ=0
    g1: Circle CenterX=0 CenterY=0 CenterZ=0 NormalX=0 NormalY=0 NormalZ=1 AngleXU=0 Radius=1
    g2: Circle CenterX=8 CenterY=6 CenterZ=0 NormalX=0 NormalY=0 NormalZ=1 AngleXU=0 Radius=1
    g3: BSplineCurve PolesCount=3 KnotsCount=2 Degree=2 IsPeriodic=0
    g4: GeomPoint X=0 Y=0 Z=0
    g5: GeomPoint X=8 Y=6 Z=0
    g6: LineSegment StartX=0 StartY=6 StartZ=0 EndX=8 EndY=6 EndZ=0
  constraints (14):
    c: Coincident(g0,g-1)
    c: Distance(g0) = 6
    c: Vertical(g0)
    c: Coincident(g3,g0)
    c: Weight(g1) = 1
    c: Equal(g1,g2)
    c: InternalAlignment(g1,g3)
    c: InternalAlignment(g2,g3)
    c: InternalAlignment(g4,g3)
    c: InternalAlignment(g5,g3)
    c: Block(g3)
    c: Coincident(g6,g0)
    c: Coincident(g6,g3)
    c: Horizontal(g6)
FEATURE [Part::Extrusion] Extrude014  label="caseScrewPillarBracket002"
  Base = -> Sketch020
  Dir = (0,0,1)
  DirMode = 2
  FaceMakerClass = Part::FaceMakerBullseye
  LengthFwd = 2.4
  LengthRev = 0
  Placement = pos=(13.7,29,13.26) rot=(0,-1,0;1.5708rad)
  Solid = true
  Symmetric = false
FEATURE [Sketcher::SketchObject] Sketch021
  FullyConstrained = true
  sketch-geometry (7):
    g0: LineSegment StartX=0 StartY=0 StartZ=0 EndX=0 EndY=6 EndZ=0
    g1: Circle CenterX=0 CenterY=0 CenterZ=0 NormalX=0 NormalY=0 NormalZ=1 AngleXU=0 Radius=1
    g2: Circle CenterX=8 CenterY=6 CenterZ=0 NormalX=0 NormalY=0 NormalZ=1 AngleXU=0 Radius=1
    g3: BSplineCurve PolesCount=3 KnotsCount=2 Degree=2 IsPeriodic=0
    g4: GeomPoint X=0 Y=0 Z=0
    g5: GeomPoint X=8 Y=6 Z=0
    g6: LineSegment StartX=0 StartY=6 StartZ=0 EndX=8 EndY=6 EndZ=0
  constraints (14):
    c: Coincident(g0,g-1)
    c: Distance(g0) = 6
    c: Vertical(g0)
    c: Coincident(g3,g0)
    c: Weight(g1) = 1
    c: Equal(g1,g2)
    c: InternalAlignment(g1,g3)
    c: InternalAlignment(g2,g3)
    c: InternalAlignment(g4,g3)
    c: InternalAlignment(g5,g3)
    c: Block(g3)
    c: Coincident(g6,g0)
    c: Coincident(g6,g3)
    c: Horizontal(g6)
FEATURE [Part::Extrusion] Extrude015  label="caseScrewPillarBracket003"
  Base = -> Sketch021
  Dir = (0,0,1)
  DirMode = 2
  FaceMakerClass = Part::FaceMakerBullseye
  LengthFwd = 2.4
  LengthRev = 0
  Placement = pos=(11.3,29,58.74) rot=(0,1,0;1.5708rad)
  Solid = true
  Symmetric = false
FEATURE [Sketcher::SketchObject] Sketch022
  FullyConstrained = true
  sketch-geometry (7):
    g0: LineSegment StartX=0 StartY=0 StartZ=0 EndX=0 EndY=6 EndZ=0
    g1: Circle CenterX=0 CenterY=0 CenterZ=0 NormalX=0 NormalY=0 NormalZ=1 AngleXU=0 Radius=1
    g2: Circle CenterX=8 CenterY=6 CenterZ=0 NormalX=0 NormalY=0 NormalZ=1 AngleXU=0 Radius=1
    g3: BSplineCurve PolesCount=3 KnotsCount=2 Degree=2 IsPeriodic=0
    g4: GeomPoint X=0 Y=0 Z=0
    g5: GeomPoint X=8 Y=6 Z=0
    g6: LineSegment StartX=0 StartY=6 StartZ=0 EndX=8 EndY=6 EndZ=0
  constraints (14):
    c: Coincident(g0,g-1)
    c: Distance(g0) = 6
    c: Vertical(g0)
    c: Coincident(g3,g0)
    c: Weight(g1) = 1
    c: Equal(g1,g2)
    c: InternalAlignment(g1,g3)
    c: InternalAlignment(g2,g3)
    c: InternalAlignment(g4,g3)
    c: InternalAlignment(g5,g3)
    c: Block(g3)
    c: Coincident(g6,g0)
    c: Coincident(g6,g3)
    c: Horizontal(g6)
FEATURE [Part::Extrusion] Extrude016  label="caseScrewPillarBracket004"
  Base = -> Sketch022
  Dir = (0,0,1)
  DirMode = 2
  FaceMakerClass = Part::FaceMakerBullseye
  LengthFwd = 2.4
  LengthRev = 0
  Placement = pos=(88.3,29,65.23) rot=(0,1,0;1.5708rad)
  Solid = true
  Symmetric = false
FEATURE [Sketcher::SketchObject] Sketch023
  FullyConstrained = true
  sketch-geometry (7):
    g0: LineSegment StartX=0 StartY=0 StartZ=0 EndX=0 EndY=6 EndZ=0
    g1: Circle CenterX=0 CenterY=0 CenterZ=0 NormalX=0 NormalY=0 NormalZ=1 AngleXU=0 Radius=1
    g2: Circle CenterX=8 CenterY=6 CenterZ=0 NormalX=0 NormalY=0 NormalZ=1 AngleXU=0 Radius=1
    g3: BSplineCurve PolesCount=3 KnotsCount=2 Degree=2 IsPeriodic=0
    g4: GeomPoint X=0 Y=0 Z=0
    g5: GeomPoint X=8 Y=6 Z=0
    g6: LineSegment StartX=0 StartY=6 StartZ=0 EndX=8 EndY=6 EndZ=0
  constraints (14):
    c: Coincident(g0,g-1)
    c: Distance(g0) = 6
    c: Vertical(g0)
    c: Coincident(g3,g0)
    c: Weight(g1) = 1
    c: Equal(g1,g2)
    c: InternalAlignment(g1,g3)
    c: InternalAlignment(g2,g3)
    c: InternalAlignment(g4,g3)
    c: InternalAlignment(g5,g3)
    c: Block(g3)
    c: Coincident(g6,g0)
    c: Coincident(g6,g3)
    c: Horizontal(g6)
FEATURE [Part::Extrusion] Extrude017  label="caseScrewPillarBracket005"
  Base = -> Sketch023
  Dir = (0,0,1)
  DirMode = 2
  FaceMakerClass = Part::FaceMakerBullseye
  LengthFwd = 2.4
  LengthRev = 0
  Placement = pos=(90.7,29,6.77) rot=(0,-1,0;1.5708rad)
  Solid = true
  Symmetric = false
FEATURE [Sketcher::SketchObject] Sketch024
  FullyConstrained = true
  sketch-geometry (7):
    g0: LineSegment StartX=0 StartY=0 StartZ=0 EndX=0 EndY=6 EndZ=0
    g1: Circle CenterX=0 CenterY=0 CenterZ=0 NormalX=0 NormalY=0 NormalZ=1 AngleXU=0 Radius=1
    g2: Circle CenterX=8 CenterY=6 CenterZ=0 NormalX=0 NormalY=0 NormalZ=1 AngleXU=0 Radius=1
    g3: BSplineCurve PolesCount=3 KnotsCount=2 Degree=2 IsPeriodic=0
    g4: GeomPoint X=0 Y=0 Z=0
    g5: GeomPoint X=8 Y=6 Z=0
    g6: LineSegment StartX=0 StartY=6 StartZ=0 EndX=8 EndY=6 EndZ=0
  constraints (14):
    c: Coincident(g0,g-1)
    c: Distance(g0) = 6
    c: Vertical(g0)
    c: Coincident(g3,g0)
    c: Weight(g1) = 1
    c: Equal(g1,g2)
    c: InternalAlignment(g1,g3)
    c: InternalAlignment(g2,g3)
    c: InternalAlignment(g4,g3)
    c: InternalAlignment(g5,g3)
    c: Block(g3)
    c: Coincident(g6,g0)
    c: Coincident(g6,g3)
    c: Horizontal(g6)
FEATURE [Part::Extrusion] Extrude018  label="caseScrewPillarBracket006"
  Base = -> Sketch024
  Dir = (0,0,1)
  DirMode = 2
  FaceMakerClass = Part::FaceMakerBullseye
  LengthFwd = 2.4
  LengthRev = 0
  Placement = pos=(103.7,29,6.77) rot=(0,-1,0;1.5708rad)
  Solid = true
  Symmetric = false
FEATURE [Sketcher::SketchObject] Sketch025
  FullyConstrained = true
  sketch-geometry (7):
    g0: LineSegment StartX=0 StartY=0 StartZ=0 EndX=0 EndY=6 EndZ=0
    g1: Circle CenterX=0 CenterY=0 CenterZ=0 NormalX=0 NormalY=0 NormalZ=1 AngleXU=0 Radius=1
    g2: Circle CenterX=8 CenterY=6 CenterZ=0 NormalX=0 NormalY=0 NormalZ=1 AngleXU=0 Radius=1
    g3: BSplineCurve PolesCount=3 KnotsCount=2 Degree=2 IsPeriodic=0
    g4: GeomPoint X=0 Y=0 Z=0
    g5: GeomPoint X=8 Y=6 Z=0
    g6: LineSegment StartX=0 StartY=6 StartZ=0 EndX=8 EndY=6 EndZ=0
  constraints (14):
    c: Coincident(g0,g-1)
    c: Distance(g0) = 6
    c: Vertical(g0)
    c: Coincident(g3,g0)
    c: Weight(g1) = 1
    c: Equal(g1,g2)
    c: InternalAlignment(g1,g3)
    c: InternalAlignment(g2,g3)
    c: InternalAlignment(g4,g3)
    c: InternalAlignment(g5,g3)
    c: Block(g3)
    c: Coincident(g6,g0)
    c: Coincident(g6,g3)
    c: Horizontal(g6)
FEATURE [Part::Extrusion] Extrude019  label="caseScrewPillarBracket007"
  Base = -> Sketch025
  Dir = (0,0,1)
  DirMode = 2
  FaceMakerClass = Part::FaceMakerBullseye
  LengthFwd = 2.4
  LengthRev = 0
  Placement = pos=(101.3,29,65.23) rot=(0,1,0;1.5708rad)
  Solid = true
  Symmetric = false
FEATURE [Part::Box] Box011  label="frontCaseScrewPillarBracket"
  AttacherType = Attacher::AttachEngine3D
  Height = 2.4
  Length = 16
  Placement = pos=(87,28,2.3) rot=(0,0,1;0rad)
  Width = 7
FEATURE [Part::Box] Box012  label="frontCaseScrewPillarBracket001"
  AttacherType = Attacher::AttachEngine3D
  Height = 2.4
  Length = 16
  Placement = pos=(87,28,67.3) rot=(0,0,1;0rad)
  Width = 7
FEATURE [Sketcher::SketchObject] Sketch026
  FullyConstrained = true
  sketch-geometry (17):
    g0: Circle CenterX=-3.5 CenterY=23.5 CenterZ=0 NormalX=0 NormalY=0 NormalZ=1 AngleXU=0 Radius=1
    g1: Circle CenterX=-1 CenterY=15.25 CenterZ=0 NormalX=0 NormalY=0 NormalZ=1 AngleXU=0 Radius=1
    g2: Circle CenterX=-3.5 CenterY=7 CenterZ=0 NormalX=0 NormalY=0 NormalZ=1 AngleXU=0 Radius=1
    g3: BSplineCurve PolesCount=3 KnotsCount=2 Degree=2 IsPeriodic=0
    g4: GeomPoint X=-3.5 Y=23.5 Z=0
    g5: GeomPoint X=-3.5 Y=7 Z=0
    g6: Circle CenterX=-4.8 CenterY=30.5 CenterZ=0 NormalX=0 NormalY=0 NormalZ=1 AngleXU=0 Radius=1
    g7: Circle CenterX=-3.5 CenterY=30.5 CenterZ=0 NormalX=0 NormalY=0 NormalZ=1 AngleXU=0 Radius=1
    g8: Circle CenterX=-3.5 CenterY=29.2 CenterZ=0 NormalX=0 NormalY=0 NormalZ=1 AngleXU=0 Radius=1
    g9: BSplineCurve PolesCount=3 KnotsCount=2 Degree=2 IsPeriodic=0
    g10: GeomPoint X=-4.8 Y=30.5 Z=0
    g11: GeomPoint X=-3.5 Y=29.2 Z=0
    g12: LineSegment StartX=-3.5 StartY=29.2 StartZ=0 EndX=-3.5 EndY=23.5 EndZ=0
    g13: LineSegment StartX=-4.8 StartY=30.5 StartZ=0 EndX=0 EndY=30.5 EndZ=0
    g14: LineSegment StartX=-3.5 StartY=5 StartZ=0 EndX=-3.5 EndY=7 EndZ=0
    g15: LineSegment StartX=0 StartY=5 StartZ=0 EndX=0 EndY=30.5 EndZ=0
    g16: LineSegment StartX=-3.5 StartY=5 StartZ=0 EndX=0 EndY=5 EndZ=0
  constraints (33):
    c: Weight(g0) = 1
    c: Equal(g0,g1)
    c: Equal(g0,g2)
    c: InternalAlignment(g0,g3)
    c: InternalAlignment(g1,g3)
    c: InternalAlignment(g2,g3)
    c: InternalAlignment(g4,g3)
    c: InternalAlignment(g5,g3)
    c: Block(g3)
    c: Weight(g6) = 1
    c: Equal(g6,g7)
    c: Equal(g6,g8)
    c: InternalAlignment(g6,g9)
    c: InternalAlignment(g7,g9)
    c: InternalAlignment(g8,g9)
    c: InternalAlignment(g10,g9)
    c: InternalAlignment(g11,g9)
    c: Block(g9)
    c: Coincident(g12,g9)
    c: Coincident(g12,g3)
    c: Vertical(g12)
    c: Coincident(g13,g9)
    c: Horizontal(g13)
    c: Distance(g13) = 4.8
    c: Coincident(g14,g3)
    c: Vertical(g14)
    c: Coincident(g15,g13)
    c: Vertical(g15)
    c: Tangent(g15,g1)
    c: Distance(g14) = 2
    c: Coincident(g16,g14)
    c: Horizontal(g16)
    c: Coincident(g15,g16)
FEATURE [Part::Feature] Face050
  shape: bbox 4.8 x 25.5 x 2e-07 mm, 1 faces, 0 solids (baked)
FEATURE [Part::Revolution] Revolve054  label="moreFrontCaseScrewPost001"
  Angle = 360
  Axis = (0,1,0)
  Base = (0,0,0)
  FaceMakerClass = Part::FaceMakerBullseye
  Placement = pos=(102.5,4.5,3.5) rot=(0,0,1;0rad)
  Solid = false
  Source = -> Face050
  Symmetric = false
FEATURE [Part::Feature] Face051
  shape: bbox 4.8 x 25.5 x 2e-07 mm, 1 faces, 0 solids (baked)
FEATURE [Part::Revolution] Revolve055  label="moreFrontCaseScrewPost002"
  Angle = 360
  Axis = (0,1,0)
  Base = (0,0,0)
  FaceMakerClass = Part::FaceMakerBullseye
  Placement = pos=(102.5,4.5,68.5) rot=(0,0,1;0rad)
  Solid = false
  Source = -> Face051
  Symmetric = false
FEATURE [Sketcher::SketchObject] Sketch027
  FullyConstrained = true
  sketch-geometry (10):
    g0: LineSegment StartX=-1.6 StartY=4.7 StartZ=0 EndX=-1.6 EndY=1.7 EndZ=0
    g1: LineSegment StartX=-3.5 StartY=4.7 StartZ=0 EndX=-1.6 EndY=4.7 EndZ=0
    g2: LineSegment StartX=-1.6 StartY=1.7 StartZ=0 EndX=-1.6 EndY=1.5 EndZ=0
    g3: LineSegment StartX=-1.6 StartY=1.5 StartZ=0 EndX=-5.2 EndY=1.5 EndZ=0
    g4: Circle CenterX=-3.5 CenterY=4.7 CenterZ=0 NormalX=0 NormalY=0 NormalZ=1 AngleXU=0 Radius=1
    g5: Circle CenterX=-3.59627 CenterY=2.99743 CenterZ=0 NormalX=0 NormalY=0 NormalZ=1 AngleXU=0 Radius=1
    g6: Circle CenterX=-5.2 CenterY=1.5 CenterZ=0 NormalX=0 NormalY=0 NormalZ=1 AngleXU=0 Radius=1
    g7: BSplineCurve PolesCount=3 KnotsCount=2 Degree=2 IsPeriodic=0
    g8: GeomPoint X=-3.5 Y=4.7 Z=0
    g9: GeomPoint X=-5.2 Y=1.5 Z=0
  constraints (23):
    c: Vertical(g0)
    c: Distance(g0) = 3
    c: Coincident(g1,g0)
    c: Horizontal(g1)
    c: Block(g0)
    c: Block(g1)
    c: Coincident(g2,g0)
    c: Vertical(g2)
    c: Distance(g2) = 0.2
    c: Coincident(g3,g2)
    c: Horizontal(g3)
    c: Block(g3)
    c: Coincident(g7,g1)
    c: Weight(g4) = 1
    c: Equal(g4,g5)
    c: Equal(g4,g6)
    c: Coincident(g7,g3)
    c: InternalAlignment(g4,g7)
    c: InternalAlignment(g5,g7)
    c: InternalAlignment(g6,g7)
    c: InternalAlignment(g8,g7)
    c: InternalAlignment(g9,g7)
    c: Block(g7)
FEATURE [Sketcher::SketchObject] Sketch028
  FullyConstrained = true
  sketch-geometry (18):
    g0: LineSegment StartX=0 StartY=3e-16 StartZ=0 EndX=0 EndY=1.7 EndZ=0
    g1: LineSegment StartX=-3.5 StartY=0 StartZ=0 EndX=-3.5 EndY=0.9 EndZ=0
    g2: Circle CenterX=-2.7 CenterY=1.7 CenterZ=0 NormalX=0 NormalY=0 NormalZ=1 AngleXU=0 Radius=1
    g3: Circle CenterX=-3.5 CenterY=1.7 CenterZ=0 NormalX=0 NormalY=0 NormalZ=1 AngleXU=0 Radius=1
    g4: Circle CenterX=-3.5 CenterY=0.9 CenterZ=0 NormalX=0 NormalY=0 NormalZ=1 AngleXU=0 Radius=1
    g5: BSplineCurve PolesCount=3 KnotsCount=2 Degree=2 IsPeriodic=0
    g6: GeomPoint X=-2.7 Y=1.7 Z=0
    g7: GeomPoint X=-3.5 Y=0.9 Z=0
    g8: LineSegment StartX=-3.5 StartY=0 StartZ=0 EndX=-3.5 EndY=-7 EndZ=0
    g9: LineSegment StartX=0 StartY=3e-16 StartZ=0 EndX=0 EndY=-7 EndZ=0
    g10: LineSegment StartX=-3.5 StartY=-7 StartZ=0 EndX=0 EndY=-7 EndZ=0
    g11: LineSegment StartX=-2.7 StartY=1.7 StartZ=0 EndX=-1.6 EndY=1.7 EndZ=0
    g12: LineSegment StartX=0 StartY=1.7 StartZ=0 EndX=0 EndY=4.5 EndZ=0
    g13: LineSegment StartX=0 StartY=4.5 StartZ=0 EndX=0 EndY=10.8 EndZ=0
    g14: LineSegment StartX=0 StartY=10.8 StartZ=0 EndX=-2 EndY=10.8 EndZ=0
    g15: LineSegment StartX=-1.6 StartY=4.7 StartZ=0 EndX=-1.6 EndY=1.7 EndZ=0
    g16: LineSegment StartX=-1.6 StartY=4.7 StartZ=0 EndX=-2 EndY=4.7 EndZ=0
    g17: LineSegment StartX=-2 StartY=4.7 StartZ=0 EndX=-2 EndY=10.8 EndZ=0
  constraints (44):
    c: Vertical(g0)
    c: Vertical(g1)
    c: Distance(g1) = 0.9
    c: Block(g0)
    c: Distance(g0) = 1.7
    c: Weight(g2) = 1
    c: Equal(g2,g3)
    c: Equal(g2,g4)
    c: Coincident(g5,g1)
    c: InternalAlignment(g2,g5)
    c: InternalAlignment(g3,g5)
    c: InternalAlignment(g4,g5)
    c: InternalAlignment(g6,g5)
    c: InternalAlignment(g7,g5)
    c: Block(g5)
    c: Coincident(g8,g1)
    c: Vertical(g8)
    c: Distance(g8) = 7
    c: Vertical(g9)
    c: Equal(g8,g9) = 7
    c: Coincident(g9,g0)
    c: Coincident(g10,g8)
    c: Coincident(g10,g9)
    c: Horizontal(g10)
    c: Coincident(g11,g5)
    c: Horizontal(g11)
    c: Coincident(g12,g0)
    c: Vertical(g12)
    c: Distance(g12) = 2.8
    c: Coincident(g13,g12)
    c: Vertical(g13)
    c: Distance(g13) = 6.3
    c: Coincident(g14,g13)
    c: Horizontal(g14)
    c: Distance(g14) = 2
    c: Vertical(g15)
    c: Distance(g15) = 3
    c: Block(g11)
    c: Coincident(g15,g11)
    c: Coincident(g16,g15)
    c: Horizontal(g16)
    c: Coincident(g17,g16)
    c: Coincident(g17,g14)
    c: Vertical(g17)
FEATURE [Part::Revolution] Revolve040  label="backCaseScrewRetainer001"
  Angle = 360
  Axis = (0,1,0)
  Base = (0,0,0)
  FaceMakerClass = Part::FaceMakerBullseye
  Placement = pos=(12.5,3,10) rot=(0,0,1;0rad)
  Solid = false
  Source = -> Face036
  Symmetric = false
FEATURE [Part::Feature] Face055
  shape: bbox 3.5 x 30.2 x 2e-07 mm, 1 faces, 0 solids (baked)
FEATURE [Part::Revolution] Revolve059  label="backCaseScrewPost"
  Angle = 360
  Axis = (0,1,0)
  Base = (0,0,0)
  FaceMakerClass = Part::FaceMakerBullseye
  Placement = pos=(12.5,4.5,10) rot=(0,0,1;0rad)
  Solid = false
  Source = -> Face055
  Symmetric = false
FEATURE [Part::Feature] Face056
  shape: bbox 3.5 x 30.2 x 2e-07 mm, 1 faces, 0 solids (baked)
FEATURE [Part::Revolution] Revolve060  label="backCaseScrewPost001"
  Angle = 360
  Axis = (0,1,0)
  Base = (0,0,0)
  FaceMakerClass = Part::FaceMakerBullseye
  Placement = pos=(12.5,4.5,62) rot=(0,0,1;0rad)
  Solid = false
  Source = -> Face056
  Symmetric = false
FEATURE [Part::Feature] Face057
  shape: bbox 3.5 x 17.8 x 2e-07 mm, 1 faces, 0 solids (baked)
FEATURE [Part::Revolution] Revolve061  label="removeToCreateScrewAndThreadedInsertHole"
  Angle = 360
  Axis = (0,1,0)
  Base = (0,0,0)
  FaceMakerClass = Part::FaceMakerBullseye
  Placement = pos=(12.5,0,10) rot=(0,0,1;0rad)
  Solid = false
  Source = -> Face057
  Symmetric = false
FEATURE [Part::Feature] Face058
  shape: bbox 3.5 x 17.8 x 2e-07 mm, 1 faces, 0 solids (baked)
FEATURE [Part::Revolution] Revolve062  label="removeToCreateScrewAndThreadedInsertHole001"
  Angle = 360
  Axis = (0,1,0)
  Base = (0,0,0)
  FaceMakerClass = Part::FaceMakerBullseye
  Placement = pos=(12.5,0,62) rot=(0,0,1;0rad)
  Solid = false
  Source = -> Face058
  Symmetric = false
FEATURE [Part::Feature] Face059
  shape: bbox 3.5 x 17.8 x 2e-07 mm, 1 faces, 0 solids (baked)
FEATURE [Part::Revolution] Revolve063  label="removeToCreateScrewAndThreadedInsertHole002"
  Angle = 360
  Axis = (0,1,0)
  Base = (0,0,0)
  FaceMakerClass = Part::FaceMakerBullseye
  Placement = pos=(89.5,0,68.5) rot=(0,0,1;0rad)
  Solid = false
  Source = -> Face059
  Symmetric = false
FEATURE [Part::Feature] Face060
  shape: bbox 3.5 x 17.8 x 2e-07 mm, 1 faces, 0 solids (baked)
FEATURE [Part::Revolution] Revolve064  label="removeToCreateScrewAndThreadedInsertHole003"
  Angle = 360
  Axis = (0,1,0)
  Base = (0,0,0)
  FaceMakerClass = Part::FaceMakerBullseye
  Placement = pos=(89.5,0,3.5) rot=(0,0,1;0rad)
  Solid = false
  Source = -> Face060
  Symmetric = false
FEATURE [Part::Feature] Face061
  shape: bbox 3.5 x 17.8 x 2e-07 mm, 1 faces, 0 solids (baked)
FEATURE [Part::Revolution] Revolve065  label="removeToCreateScrewAndThreadedInsertHole004"
  Angle = 360
  Axis = (0,1,0)
  Base = (0,0,0)
  FaceMakerClass = Part::FaceMakerBullseye
  Placement = pos=(102.5,4.7,3.5) rot=(0,0,1;0rad)
  Solid = false
  Source = -> Face061
  Symmetric = false
FEATURE [Part::Feature] Face062
  shape: bbox 3.5 x 17.8 x 2e-07 mm, 1 faces, 0 solids (baked)
FEATURE [Part::Revolution] Revolve066  label="removeToCreateScrewAndThreadedInsertHole005"
  Angle = 360
  Axis = (0,1,0)
  Base = (0,0,0)
  FaceMakerClass = Part::FaceMakerBullseye
  Placement = pos=(102.5,4.7,68.5) rot=(0,0,1;0rad)
  Solid = false
  Source = -> Face062
  Symmetric = false
FEATURE [Part::MultiFuse] Fusion047  label="makeHoles"
  Shapes = -> [Revolve066,Revolve065,Revolve064,Revolve063,Revolve062,Revolve061]
FEATURE [Part::Feature] Face063
  shape: bbox 3.6 x 3.2 x 2e-07 mm, 1 faces, 0 solids (baked)
FEATURE [Part::Revolution] Revolve067  label="moreFrontCaseScrewRetainer002"
  Angle = 360
  Axis = (0,1,0)
  Base = (0,0,0)
  FaceMakerClass = Part::FaceMakerBullseye
  Placement = pos=(102.5,4.5,68.5) rot=(0,0,1;0rad)
  Solid = false
  Source = -> Face063
  Symmetric = false
FEATURE [Part::Feature] Face064
  shape: bbox 3.6 x 3.2 x 2e-07 mm, 1 faces, 0 solids (baked)
FEATURE [Part::Revolution] Revolve068  label="moreFrontCaseScrewRetainer003"
  Angle = 360
  Axis = (0,1,0)
  Base = (0,0,0)
  FaceMakerClass = Part::FaceMakerBullseye
  Placement = pos=(102.5,4.5,3.5) rot=(0,0,1;0rad)
  Solid = false
  Source = -> Face064
  Symmetric = false
FEATURE [Part::Feature] Face065
  shape: bbox 3.5 x 17.8 x 2e-07 mm, 1 faces, 0 solids (baked)
FEATURE [Part::Revolution] Revolve069  label="removeToCreateScrewAndThreadedInsertHole006"
  Angle = 360
  Axis = (0,1,0)
  Base = (0,0,0)
  FaceMakerClass = Part::FaceMakerBullseye
  Placement = pos=(12.5,0,10) rot=(0,0,1;0rad)
  Solid = false
  Source = -> Face065
  Symmetric = false
FEATURE [Part::Feature] Face066
  shape: bbox 3.5 x 17.8 x 2e-07 mm, 1 faces, 0 solids (baked)
FEATURE [Part::Revolution] Revolve070  label="removeToCreateScrewAndThreadedInsertHole007"
  Angle = 360
  Axis = (0,1,0)
  Base = (0,0,0)
  FaceMakerClass = Part::FaceMakerBullseye
  Placement = pos=(12.5,0,62) rot=(0,0,1;0rad)
  Solid = false
  Source = -> Face066
  Symmetric = false
FEATURE [Part::Feature] Face067
  shape: bbox 3.5 x 17.8 x 2e-07 mm, 1 faces, 0 solids (baked)
FEATURE [Part::Revolution] Revolve071  label="removeToCreateScrewAndThreadedInsertHole008"
  Angle = 360
  Axis = (0,1,0)
  Base = (0,0,0)
  FaceMakerClass = Part::FaceMakerBullseye
  Placement = pos=(89.5,0,68.5) rot=(0,0,1;0rad)
  Solid = false
  Source = -> Face067
  Symmetric = false
FEATURE [Part::Feature] Face068
  shape: bbox 3.5 x 17.8 x 2e-07 mm, 1 faces, 0 solids (baked)
FEATURE [Part::Revolution] Revolve072  label="removeToCreateScrewAndThreadedInsertHole009"
  Angle = 360
  Axis = (0,1,0)
  Base = (0,0,0)
  FaceMakerClass = Part::FaceMakerBullseye
  Placement = pos=(89.5,0,3.5) rot=(0,0,1;0rad)
  Solid = false
  Source = -> Face068
  Symmetric = false
FEATURE [Part::Feature] Face069
  shape: bbox 3.5 x 17.8 x 2e-07 mm, 1 faces, 0 solids (baked)
FEATURE [Part::Feature] Face070
  shape: bbox 3.5 x 17.8 x 2e-07 mm, 1 faces, 0 solids (baked)
FEATURE [Part::Revolution] Revolve073  label="removeToCreateScrewAndThreadedInsertHole010"
  Angle = 360
  Axis = (0,1,0)
  Base = (0,0,0)
  FaceMakerClass = Part::FaceMakerBullseye
  Placement = pos=(102.5,4.7,3.5) rot=(0,0,1;0rad)
  Solid = false
  Source = -> Face069
  Symmetric = false
FEATURE [Part::Revolution] Revolve074  label="removeToCreateScrewAndThreadedInsertHole011"
  Angle = 360
  Axis = (0,1,0)
  Base = (0,0,0)
  FaceMakerClass = Part::FaceMakerBullseye
  Placement = pos=(102.5,4.7,68.5) rot=(0,0,1;0rad)
  Solid = false
  Source = -> Face070
  Symmetric = false
FEATURE [Part::MultiFuse] Fusion048  label="makeHoles001"
  Shapes = -> [Revolve074,Revolve073,Revolve072,Revolve071,Revolve070,Revolve069]
FEATURE [Part::MultiFuse] Fusion049  label="caseScrewRetainers"
  Shapes = -> [Revolve067,Revolve068,Revolve048,Revolve047,Revolve039,Revolve040]
FEATURE [Part::Cut] Cut015  label="caseScrewRetainers001"
  Base = -> Fusion049
  Tool = -> Fusion048
FEATURE [Part::MultiFuse] Fusion050  label="casePillars"
  Shapes = -> [Revolve055,Revolve054,Revolve043,Revolve046,Revolve059,Revolve060]
FEATURE [Part::Feature] Face071 .. Face076  x6 (patterned run collapsed; names and placements below)
  shape: bbox 3.5 x 17.8 x 2e-07 mm, 1 faces, 0 solids (baked)
FEATURE [Part::Revolution] Revolve075  label="removeToCreateScrewAndThreadedInsertHole012"
  Angle = 360
  Axis = (0,1,0)
  Base = (0,0,0)
  FaceMakerClass = Part::FaceMakerBullseye
  Placement = pos=(12.5,0,10) rot=(0,0,1;0rad)
  Solid = false
  Source = -> Face071
  Symmetric = false
FEATURE [Part::Revolution] Revolve076  label="removeToCreateScrewAndThreadedInsertHole013"
  Angle = 360
  Axis = (0,1,0)
  Base = (0,0,0)
  FaceMakerClass = Part::FaceMakerBullseye
  Placement = pos=(12.5,0,62) rot=(0,0,1;0rad)
  Solid = false
  Source = -> Face072
  Symmetric = false
FEATURE [Part::Revolution] Revolve077  label="removeToCreateScrewAndThreadedInsertHole014"
  Angle = 360
  Axis = (0,1,0)
  Base = (0,0,0)
  FaceMakerClass = Part::FaceMakerBullseye
  Placement = pos=(89.5,0,68.5) rot=(0,0,1;0rad)
  Solid = false
  Source = -> Face073
  Symmetric = false
FEATURE [Part::Revolution] Revolve078  label="removeToCreateScrewAndThreadedInsertHole015"
  Angle = 360
  Axis = (0,1,0)
  Base = (0,0,0)
  FaceMakerClass = Part::FaceMakerBullseye
  Placement = pos=(89.5,0,3.5) rot=(0,0,1;0rad)
  Solid = false
  Source = -> Face074
  Symmetric = false
FEATURE [Part::Revolution] Revolve079  label="removeToCreateScrewAndThreadedInsertHole016"
  Angle = 360
  Axis = (0,1,0)
  Base = (0,0,0)
  FaceMakerClass = Part::FaceMakerBullseye
  Placement = pos=(102.5,4.7,3.5) rot=(0,0,1;0rad)
  Solid = false
  Source = -> Face075
  Symmetric = false
FEATURE [Part::Revolution] Revolve080  label="removeToCreateScrewAndThreadedInsertHole017"
  Angle = 360
  Axis = (0,1,0)
  Base = (0,0,0)
  FaceMakerClass = Part::FaceMakerBullseye
  Placement = pos=(102.5,4.7,68.5) rot=(0,0,1;0rad)
  Solid = false
  Source = -> Face076
  Symmetric = false
FEATURE [Part::MultiFuse] Fusion051  label="makeHoles002"
  Shapes = -> [Revolve080,Revolve079,Revolve078,Revolve077,Revolve076,Revolve075]
FEATURE [Part::Cut] Cut016  label="caesPillars"
  Base = -> Fusion050
  Tool = -> Fusion051
FEATURE [Part::Revolution] Revolve009  label="plugHousing016"
  Angle = 360
  Axis = (0,1,0)
  Base = (0,0,0)
  FaceMakerClass = Part::FaceMakerBullseye
  Placement = pos=(0,0,36.15) rot=(0,0,1;0rad)
  Solid = false
  Source = -> Face012
  Symmetric = false
FEATURE [Part::MultiFuse] Fusion014  label="plugHousing023"
  Placement = pos=(0,0,0) rot=(0,0,1;1.5708rad)
  Shapes = -> [Revolve011,Revolve009]
FEATURE [Part::Revolution] Revolve010  label="plugHousing017"
  Angle = 360
  Axis = (0,1,0)
  Base = (0,0,0)
  FaceMakerClass = Part::FaceMakerBullseye
  Placement = pos=(0,0,36.15) rot=(0,0,1;0rad)
  Solid = false
  Source = -> Face014
  Symmetric = false
FEATURE [Part::MultiFuse] Fusion015  label="plugHousing024"
  Placement = pos=(0,0,0) rot=(0,0,1;1.5708rad)
  Shapes = -> [Revolve010,Revolve015]
FEATURE [Part::Revolution] Revolve014  label="plugHousing026"
  Angle = 360
  Axis = (0,1,0)
  Base = (0,0,0)
  FaceMakerClass = Part::FaceMakerBullseye
  Placement = pos=(0,0,36.15) rot=(0,0,1;0rad)
  Solid = false
  Source = -> Face011
  Symmetric = false
FEATURE [Part::Revolution] Revolve013  label="plugHousing025"
  Angle = 360
  Axis = (0,1,0)
  Base = (0,0,0)
  FaceMakerClass = Part::FaceMakerBullseye
  Placement = pos=(0,0,36.15) rot=(0,0,1;0rad)
  Solid = false
  Source = -> Face015
  Symmetric = false
FEATURE [Part::MultiFuse] Fusion016  label="plugHousing028"
  Placement = pos=(0,19,0) rot=(0,0,1;3.14159rad)
  Shapes = -> [Fusion014,Fusion013]
FEATURE [Part::MultiFuse] Fusion011  label="plugHousing018"
  Placement = pos=(0,0,0) rot=(0,0,1;1.5708rad)
  Shapes = -> [Revolve014,Revolve013]
FEATURE [Part::MultiFuse] Fusion012  label="plugHousing019"
  Placement = pos=(0,19,0) rot=(0,0,1;3.14159rad)
  Shapes = -> [Fusion011,Fusion015]
FEATURE [Part::MultiFuse] Fusion017  label="plugHousing029"
  Placement = pos=(122.621,0,-0.15) rot=(0,0,1;0rad)
  Shapes = -> [Fusion016,Fusion012]
FEATURE [Part::MultiFuse] Fusion052  label="casePillarRetainers"
  Shapes = -> [Extrude012,Extrude013,Extrude014,Extrude015,Extrude016,Extrude017,Extrude018,Extrude019,Box011,Box012]
FEATURE [Part::Feature] Face077
  shape: bbox 3.5 x 17.8 x 2e-07 mm, 1 faces, 0 solids (baked)
FEATURE [Part::Revolution] Revolve081  label="removeToCreateScrewAndThreadedInsertHole018"
  Angle = 360
  Axis = (0,1,0)
  Base = (0,0,0)
  FaceMakerClass = Part::FaceMakerBullseye
  Placement = pos=(62.3,30.3,19.7) rot=(0,0,1;0rad)
  Solid = false
  Source = -> Face077
  Symmetric = false
FEATURE [Part::Feature] Face078
  shape: bbox 3.5 x 17.8 x 2e-07 mm, 1 faces, 0 solids (baked)
FEATURE [Part::Revolution] Revolve082  label="removeToCreateScrewAndThreadedInsertHole019"
  Angle = 360
  Axis = (0,1,0)
  Base = (0,0,0)
  FaceMakerClass = Part::FaceMakerBullseye
  Placement = pos=(62.3,30.3,51.7) rot=(0,0,1;0rad)
  Solid = false
  Source = -> Face078
  Symmetric = false
FEATURE [Part::Feature] Face079
  shape: bbox 3.5 x 17.8 x 2e-07 mm, 1 faces, 0 solids (baked)
FEATURE [Part::Revolution] Revolve083  label="removeToCreateScrewAndThreadedInsertHole020"
  Angle = 360
  Axis = (0,1,0)
  Base = (0,0,0)
  FaceMakerClass = Part::FaceMakerBullseye
  Placement = pos=(30.3,30.3,19.7) rot=(0,0,1;0rad)
  Solid = false
  Source = -> Face079
  Symmetric = false
FEATURE [Part::Feature] Face080
  shape: bbox 3.5 x 17.8 x 2e-07 mm, 1 faces, 0 solids (baked)
FEATURE [Part::Revolution] Revolve084  label="removeToCreateScrewAndThreadedInsertHole021"
  Angle = 360
  Axis = (0,1,0)
  Base = (0,0,0)
  FaceMakerClass = Part::FaceMakerBullseye
  Placement = pos=(30.3,30.3,51.7) rot=(0,0,1;0rad)
  Solid = false
  Source = -> Face080
  Symmetric = false
FEATURE [Part::MultiFuse] Fusion053  label="createThreadedInsertHolesForFan"
  Shapes = -> [Revolve081,Revolve082,Revolve083,Revolve084]
FEATURE [Part::Cut] Cut017  label="fanScrewHousing001"
  Base = -> Fusion046
  Tool = -> Fusion053
FEATURE [Part::Feature] Face081
  shape: bbox 3.5 x 17.8 x 2e-07 mm, 1 faces, 0 solids (baked)
FEATURE [Part::Revolution] Revolve085  label="removeToCreateScrewAndThreadedInsertHole022"
  Angle = 360
  Axis = (0,1,0)
  Base = (0,0,0)
  FaceMakerClass = Part::FaceMakerBullseye
  Placement = pos=(62.3,30.3,19.7) rot=(0,0,1;0rad)
  Solid = false
  Source = -> Face081
  Symmetric = false
FEATURE [Part::Feature] Face082
  shape: bbox 3.5 x 17.8 x 2e-07 mm, 1 faces, 0 solids (baked)
FEATURE [Part::Revolution] Revolve086  label="removeToCreateScrewAndThreadedInsertHole023"
  Angle = 360
  Axis = (0,1,0)
  Base = (0,0,0)
  FaceMakerClass = Part::FaceMakerBullseye
  Placement = pos=(62.3,30.3,51.7) rot=(0,0,1;0rad)
  Solid = false
  Source = -> Face082
  Symmetric = false
FEATURE [Part::Feature] Face083
  shape: bbox 3.5 x 17.8 x 2e-07 mm, 1 faces, 0 solids (baked)
FEATURE [Part::Revolution] Revolve087  label="removeToCreateScrewAndThreadedInsertHole024"
  Angle = 360
  Axis = (0,1,0)
  Base = (0,0,0)
  FaceMakerClass = Part::FaceMakerBullseye
  Placement = pos=(30.3,30.3,19.7) rot=(0,0,1;0rad)
  Solid = false
  Source = -> Face083
  Symmetric = false
FEATURE [Part::Feature] Face084
  shape: bbox 3.5 x 17.8 x 2e-07 mm, 1 faces, 0 solids (baked)
FEATURE [Part::Revolution] Revolve088  label="removeToCreateScrewAndThreadedInsertHole025"
  Angle = 360
  Axis = (0,1,0)
  Base = (0,0,0)
  FaceMakerClass = Part::FaceMakerBullseye
  Placement = pos=(30.3,30.3,51.7) rot=(0,0,1;0rad)
  Solid = false
  Source = -> Face084
  Symmetric = false
FEATURE [Part::MultiFuse] Fusion054  label="createThreadedInsertHolesForFan001"
  Shapes = -> [Revolve085,Revolve086,Revolve087,Revolve088]
FEATURE [Part::Cut] Cut018  label="top007"
  Base = -> Fusion040
  Tool = -> Fusion054
FEATURE [Sketcher::SketchObject] Sketch029
  FullyConstrained = false
  Placement = pos=(0,0,0) rot=(1,0,0;1.5708rad)
  sketch-geometry (24):
    g0: ArcOfCircle CenterX=-4 CenterY=-10.5 CenterZ=0 NormalX=0 NormalY=0 NormalZ=1 AngleXU=0 Radius=1.5 StartAngle=6e-16 EndAngle=3.14159
    g1: ArcOfCircle CenterX=-34.2 CenterY=-10.5 CenterZ=0 NormalX=0 NormalY=0 NormalZ=1 AngleXU=0 Radius=1.5 StartAngle=0 EndAngle=3.14159
    g2: ArcOfCircle CenterX=-34.2 CenterY=-27.7 CenterZ=0 NormalX=0 NormalY=0 NormalZ=1 AngleXU=0 Radius=1.5 StartAngle=3.14159 EndAngle=6.28319
    g3: ArcOfCircle CenterX=-4 CenterY=-27.7 CenterZ=0 NormalX=0 NormalY=0 NormalZ=1 AngleXU=0 Radius=1.5 StartAngle=3.1416 EndAngle=6.28319
    g4: ArcOfCircle CenterX=-10 CenterY=-4.3 CenterZ=0 NormalX=0 NormalY=0 NormalZ=1 AngleXU=0 Radius=1.5 StartAngle=2e-16 EndAngle=3.14159
    g5: ArcOfCircle CenterX=-16.1 CenterY=-1.8 CenterZ=0 NormalX=0 NormalY=0 NormalZ=1 AngleXU=0 Radius=1.5 StartAngle=5e-16 EndAngle=3.14159
    g6: ArcOfCircle CenterX=-22.1 CenterY=-1.8 CenterZ=0 NormalX=0 NormalY=0 NormalZ=1 AngleXU=0 Radius=1.5 StartAngle=5e-16 EndAngle=3.14159
    g7: ArcOfCircle CenterX=-28.2 CenterY=-4.3 CenterZ=0 NormalX=0 NormalY=0 NormalZ=1 AngleXU=0 Radius=1.5 StartAngle=2e-16 EndAngle=3.14159
    g8: ArcOfCircle CenterX=-10 CenterY=-33.9 CenterZ=0 NormalX=0 NormalY=0 NormalZ=1 AngleXU=0 Radius=1.5 StartAngle=3.14159 EndAngle=6.28319
    g9: ArcOfCircle CenterX=-16.1 CenterY=-36.4 CenterZ=0 NormalX=0 NormalY=0 NormalZ=1 AngleXU=0 Radius=1.5 StartAngle=3.14159 EndAngle=6.28319
    g10: ArcOfCircle CenterX=-22.1 CenterY=-36.4 CenterZ=0 NormalX=0 NormalY=0 NormalZ=1 AngleXU=0 Radius=1.5 StartAngle=3.14159 EndAngle=6.28319
    g11: ArcOfCircle CenterX=-28.2 CenterY=-33.9 CenterZ=0 NormalX=0 NormalY=0 NormalZ=1 AngleXU=0 Radius=1.5 StartAngle=3.14159 EndAngle=6.28319
    g12: LineSegment StartX=-35.7 StartY=-10.5 StartZ=0 EndX=-35.7 EndY=-27.7 EndZ=0
    g13: LineSegment StartX=-32.7 StartY=-10.5 StartZ=0 EndX=-32.7 EndY=-27.7 EndZ=0
    g14: LineSegment StartX=-29.7 StartY=-33.9 StartZ=0 EndX=-29.7 EndY=-4.3 EndZ=0
    g15: LineSegment StartX=-26.7 StartY=-33.9 StartZ=0 EndX=-26.7 EndY=-4.3 EndZ=0
    g16: LineSegment StartX=-2.5 StartY=-10.5 StartZ=0 EndX=-2.5 EndY=-27.7 EndZ=0
    g17: LineSegment StartX=-8.5 StartY=-4.3 StartZ=0 EndX=-8.5 EndY=-33.9 EndZ=0
    g18: LineSegment StartX=-5.5 StartY=-10.5 StartZ=0 EndX=-5.5 EndY=-27.7 EndZ=0
    g19: LineSegment StartX=-11.5 StartY=-4.3 StartZ=0 EndX=-11.5 EndY=-33.9 EndZ=0
    g20: LineSegment StartX=-14.6 StartY=-1.8 StartZ=0 EndX=-14.6 EndY=-36.4 EndZ=0
    g21: LineSegment StartX=-17.6 StartY=-1.8 StartZ=0 EndX=-17.6 EndY=-36.4 EndZ=0
    g22: LineSegment StartX=-20.6 StartY=-36.4 StartZ=0 EndX=-20.6 EndY=-1.8 EndZ=0
    g23: LineSegment StartX=-23.6 StartY=-1.8 StartZ=0 EndX=-23.6 EndY=-36.4 EndZ=0
  constraints (48):
    c: Block(g0)
    c: Block(g1)
    c: Block(g2)
    c: Block(g3)
    c: Block(g4)
    c: Block(g5)
    c: Block(g6)
    c: Block(g7)
    c: Block(g8)
    c: Block(g9)
    c: Block(g10)
    c: Block(g11)
    c: Coincident(g12,g1)
    c: Coincident(g12,g2)
    c: Vertical(g12)
    c: Coincident(g13,g1)
    c: Coincident(g13,g2)
    c: Vertical(g13)
    c: Coincident(g14,g11)
    c: Coincident(g14,g7)
    c: Vertical(g14)
    c: Coincident(g15,g11)
    c: Coincident(g15,g7)
    c: Vertical(g15)
    c: Coincident(g16,g0)
    c: Coincident(g16,g3)
    c: Vertical(g16)
    c: Coincident(g17,g4)
    c: Coincident(g17,g8)
    c: Vertical(g17)
    c: Coincident(g18,g0)
    c: Coincident(g18,g3)
    c: Vertical(g18)
    c: Coincident(g19,g4)
    c: Coincident(g19,g8)
    c: Vertical(g19)
    c: Coincident(g20,g5)
    c: Coincident(g20,g9)
    c: Vertical(g20)
    c: Coincident(g21,g5)
    c: Coincident(g21,g9)
    c: Vertical(g21)
    c: Coincident(g22,g10)
    c: Coincident(g22,g6)
    c: Vertical(g22)
    c: Coincident(g23,g6)
    c: Coincident(g23,g10)
    c: Vertical(g23)
FEATURE [Part::Extrusion] Extrude020  label="removeToCreateFanGrillHoles"
  Base = -> Sketch029
  Dir = (0,-1,6e-16)
  DirMode = 2
  FaceMakerClass = Part::FaceMakerBullseye
  LengthFwd = 10
  LengthRev = 0
  Placement = pos=(65.4,44,54.82) rot=(0,0,1;0rad)
  Solid = true
  Symmetric = false
FEATURE [Part::MultiFuse] Fusion055  label="top008"
  Shapes = -> [Cut017,Cut018]
FEATURE [Part::Cut] Cut019  label="top009"
  Base = -> Fusion055
  Tool = -> Extrude020
FEATURE [App::MeasureDistance] Distance003  label="Distance: 71.95 mm"
  Distance = 71.9513
  P1 = (117,38,72)
  P2 = (117,38,0.0487319)
FEATURE [Sketcher::SketchObject] Sketch030
  FullyConstrained = true
  Placement = pos=(117,19,0) rot=(0.57735,0.57735,0.57735;2.0944rad)
  sketch-geometry (48):
    g0: LineSegment StartX=-49.19 StartY=69.25 StartZ=0 EndX=-49.19 EndY=66.25 EndZ=0
    g1: LineSegment StartX=-49.19 StartY=63.5 StartZ=0 EndX=-49.19 EndY=60.5 EndZ=0
    g2: LineSegment StartX=-49.19 StartY=57.75 StartZ=0 EndX=-49.19 EndY=54.75 EndZ=0
    g3: LineSegment StartX=-49.19 StartY=52 StartZ=0 EndX=-49.19 EndY=49 EndZ=0
    g4: LineSegment StartX=-49.19 StartY=46.25 StartZ=0 EndX=-49.19 EndY=43.25 EndZ=0
    g5: LineSegment StartX=-49.19 StartY=40.5 StartZ=0 EndX=-49.19 EndY=37.5 EndZ=0
    g6: LineSegment StartX=-49.19 StartY=34.5 StartZ=0 EndX=-49.19 EndY=31.5 EndZ=0
    g7: LineSegment StartX=-49.19 StartY=28.75 StartZ=0 EndX=-49.19 EndY=25.75 EndZ=0
    g8: LineSegment StartX=-49.19 StartY=23 StartZ=0 EndX=-49.19 EndY=20 EndZ=0
    g9: LineSegment StartX=-49.19 StartY=17.25 StartZ=0 EndX=-49.19 EndY=14.25 EndZ=0
    g10: LineSegment StartX=-49.19 StartY=11.5 StartZ=0 EndX=-49.19 EndY=8.5 EndZ=0
    g11: LineSegment StartX=-49.19 StartY=5.75 StartZ=0 EndX=-49.19 EndY=2.75 EndZ=0
    g12: ArcOfCircle CenterX=-1.5 CenterY=67.75 CenterZ=0 NormalX=0 NormalY=0 NormalZ=1 AngleXU=0 Radius=1.5 StartAngle=4.71239 EndAngle=7.85398
    g13: ArcOfCircle CenterX=-1.5 CenterY=62 CenterZ=0 NormalX=0 NormalY=0 NormalZ=1 AngleXU=0 Radius=1.5 StartAngle=4.71239 EndAngle=7.85398
    g14: ArcOfCircle CenterX=-1.5 CenterY=56.25 CenterZ=0 NormalX=0 NormalY=0 NormalZ=1 AngleXU=0 Radius=1.5 StartAngle=4.71239 EndAngle=7.85398
    g15: ArcOfCircle CenterX=-11.49 CenterY=50.5 CenterZ=0 NormalX=0 NormalY=0 NormalZ=1 AngleXU=0 Radius=1.5 StartAngle=4.71239 EndAngle=7.85398
    g16: ArcOfCircle CenterX=-16.28 CenterY=44.75 CenterZ=0 NormalX=0 NormalY=0 NormalZ=1 AngleXU=0 Radius=1.5 StartAngle=4.71239 EndAngle=7.85398
    g17: ArcOfCircle CenterX=-18.2337 CenterY=39 CenterZ=0 NormalX=0 NormalY=0 NormalZ=1 AngleXU=0 Radius=1.5 StartAngle=4.71485 EndAngle=7.85398
    g18: ArcOfCircle CenterX=-16.2837 CenterY=27.25 CenterZ=0 NormalX=0 NormalY=0 NormalZ=1 AngleXU=0 Radius=1.5 StartAngle=4.71485 EndAngle=7.85398
    g19: ArcOfCircle CenterX=-18.2337 CenterY=33 CenterZ=0 NormalX=0 NormalY=0 NormalZ=1 AngleXU=0 Radius=1.5 StartAngle=4.71485 EndAngle=7.85398
    g20: ArcOfCircle CenterX=-11.49 CenterY=21.5 CenterZ=0 NormalX=0 NormalY=0 NormalZ=1 AngleXU=0 Radius=1.5 StartAngle=4.71239 EndAngle=7.85398
    g21: ArcOfCircle CenterX=-1.5 CenterY=4.25 CenterZ=0 NormalX=0 NormalY=0 NormalZ=1 AngleXU=0 Radius=1.5 StartAngle=4.71239 EndAngle=7.85398
    g22: ArcOfCircle CenterX=-1.5 CenterY=10 CenterZ=0 NormalX=0 NormalY=0 NormalZ=1 AngleXU=0 Radius=1.5 StartAngle=4.71239 EndAngle=7.85398
    g23: ArcOfCircle CenterX=-1.5 CenterY=15.75 CenterZ=0 NormalX=0 NormalY=0 NormalZ=1 AngleXU=0 Radius=1.5 StartAngle=4.71239 EndAngle=7.85398
    g24: LineSegment StartX=-49.19 StartY=69.25 StartZ=0 EndX=-1.5 EndY=69.25 EndZ=0
    g25: LineSegment StartX=-49.19 StartY=66.25 StartZ=0 EndX=-1.5 EndY=66.25 EndZ=0
    g26: LineSegment StartX=-49.19 StartY=63.5 StartZ=0 EndX=-1.5 EndY=63.5 EndZ=0
    g27: LineSegment StartX=-49.19 StartY=60.5 StartZ=0 EndX=-1.5 EndY=60.5 EndZ=0
    g28: LineSegment StartX=-49.19 StartY=57.75 StartZ=0 EndX=-1.5 EndY=57.75 EndZ=0
    g29: LineSegment StartX=-49.19 StartY=54.75 StartZ=0 EndX=-1.5 EndY=54.75 EndZ=0
    g30: LineSegment StartX=-49.19 StartY=52 StartZ=0 EndX=-11.49 EndY=52 EndZ=0
    g31: LineSegment StartX=-49.19 StartY=49 StartZ=0 EndX=-11.49 EndY=49 EndZ=0
    g32: LineSegment StartX=-49.19 StartY=46.25 StartZ=0 EndX=-16.28 EndY=46.25 EndZ=0
    g33: LineSegment StartX=-49.19 StartY=43.25 StartZ=0 EndX=-16.28 EndY=43.25 EndZ=0
    g34: LineSegment StartX=-49.19 StartY=40.5 StartZ=0 EndX=-18.2337 EndY=40.5 EndZ=0
    g35: LineSegment StartX=-49.19 StartY=37.5 StartZ=0 EndX=-18.23 EndY=37.5 EndZ=0
    g36: LineSegment StartX=-49.19 StartY=34.5 StartZ=0 EndX=-18.2337 EndY=34.5 EndZ=0
    g37: LineSegment StartX=-49.19 StartY=31.5 StartZ=0 EndX=-18.23 EndY=31.5 EndZ=0
    g38: LineSegment StartX=-49.19 StartY=28.75 StartZ=0 EndX=-16.2837 EndY=28.75 EndZ=0
    g39: LineSegment StartX=-49.19 StartY=25.75 StartZ=0 EndX=-16.28 EndY=25.75 EndZ=0
    g40: LineSegment StartX=-49.19 StartY=23 StartZ=0 EndX=-11.49 EndY=23 EndZ=0
    g41: LineSegment StartX=-49.19 StartY=20 StartZ=0 EndX=-11.49 EndY=20 EndZ=0
    g42: LineSegment StartX=-49.19 StartY=17.25 StartZ=0 EndX=-1.5 EndY=17.25 EndZ=0
    g43: LineSegment StartX=-49.19 StartY=14.25 StartZ=0 EndX=-1.5 EndY=14.25 EndZ=0
    g44: LineSegment StartX=-49.19 StartY=11.5 StartZ=0 EndX=-1.5 EndY=11.5 EndZ=0
    g45: LineSegment StartX=-49.19 StartY=8.5 StartZ=0 EndX=-1.5 EndY=8.5 EndZ=0
    g46: LineSegment StartX=-49.19 StartY=5.75 StartZ=0 EndX=-1.5 EndY=5.75 EndZ=0
    g47: LineSegment StartX=-49.19 StartY=2.75 StartZ=0 EndX=-1.5 EndY=2.75 EndZ=0
  constraints (120):
    c: Vertical(g0)
    c: Distance(g0) = 3
    c: Block(g0)
    c: Vertical(g1)
    c: Distance(g1) = 3
    c: Vertical(g2)
    c: Equal(g0,g2) = 3
    c: Block(g2)
    c: Vertical(g3)
    c: Equal(g1,g3) = 3
    c: Vertical(g4)
    c: Equal(g0,g4) = 3
    c: Block(g4)
    c: Vertical(g5)
    c: Equal(g1,g5) = 3
    c: Vertical(g6)
    c: Equal(g0,g6) = 3
    c: Block(g6)
    c: Vertical(g7)
    c: Equal(g1,g7) = 3
    c: Vertical(g8)
    c: Equal(g0,g8) = 3
    c: Block(g8)
    c: Vertical(g9)
    c: Equal(g1,g9) = 3
    c: Vertical(g10)
    c: Equal(g0,g10) = 3
    c: Block(g10)
    c: Vertical(g11)
    c: Equal(g1,g11) = 3
    c: Block(g12)
    c: Block(g13)
    c: Block(g14)
    c: Block(g15)
    c: Block(g16)
    c: Block(g17)
    c: Block(g18)
    c: Block(g19)
    c: Block(g20)
    c: Block(g21)
    c: Block(g22)
    c: Block(g23)
    c: Block(g11)
    c: Block(g9)
    c: Block(g7)
    c: Block(g5)
    c: Block(g3)
    c: Block(g1)
    c: Coincident(g24,g0)
    c: Coincident(g24,g12)
    c: Horizontal(g24)
    c: Coincident(g25,g0)
    c: Coincident(g25,g12)
    c: Horizontal(g25)
    c: Coincident(g26,g1)
    c: Coincident(g26,g13)
    c: Horizontal(g26)
    c: Coincident(g27,g1)
    c: Coincident(g27,g13)
    c: Horizontal(g27)
    c: Coincident(g28,g2)
    c: Coincident(g28,g14)
    c: Horizontal(g28)
    c: Coincident(g29,g2)
    c: Coincident(g29,g14)
    c: Horizontal(g29)
    c: Coincident(g30,g3)
    c: Coincident(g30,g15)
    c: Horizontal(g30)
    c: Coincident(g31,g3)
    c: Coincident(g31,g15)
    c: Horizontal(g31)
    c: Coincident(g32,g4)
    c: Coincident(g32,g16)
    c: Horizontal(g32)
    c: Coincident(g33,g4)
    c: Coincident(g33,g16)
    c: Horizontal(g33)
    c: Coincident(g34,g5)
    c: Coincident(g34,g17)
    c: Horizontal(g34)
    c: Coincident(g35,g5)
    c: Coincident(g35,g17)
    c: Horizontal(g35)
    c: Coincident(g36,g6)
    c: Coincident(g36,g19)
    c: Horizontal(g36)
    c: Coincident(g37,g6)
    c: Coincident(g37,g19)
    c: Horizontal(g37)
    c: Coincident(g38,g7)
    c: Coincident(g38,g18)
    c: Horizontal(g38)
    c: Coincident(g39,g7)
    c: Coincident(g39,g18)
    c: Horizontal(g39)
    c: Coincident(g40,g8)
    c: Coincident(g40,g20)
    c: Horizontal(g40)
    c: Coincident(g41,g8)
    c: Coincident(g41,g20)
    c: Horizontal(g41)
    c: Coincident(g42,g9)
    c: Coincident(g42,g23)
    c: Horizontal(g42)
    c: Coincident(g43,g9)
    c: Coincident(g43,g23)
    c: Horizontal(g43)
    c: Coincident(g44,g10)
    c: Coincident(g44,g22)
    c: Horizontal(g44)
    c: Coincident(g45,g10)
    c: Coincident(g45,g22)
    c: Horizontal(g45)
    c: Coincident(g46,g11)
    c: Coincident(g46,g21)
    c: Horizontal(g46)
    c: Coincident(g47,g11)
    c: Coincident(g47,g21)
    c: Horizontal(g47)
FEATURE [Sketcher::SketchObject] Sketch031
  FullyConstrained = true
  Placement = pos=(117,19,0) rot=(0.57735,0.57735,0.57735;2.0944rad)
  sketch-geometry (24):
    g0: ArcOfCircle CenterX=-49.19 CenterY=67.75 CenterZ=0 NormalX=0 NormalY=0 NormalZ=1 AngleXU=0 Radius=1.5 StartAngle=1.5708 EndAngle=4.71239
    g1: ArcOfCircle CenterX=-49.19 CenterY=62 CenterZ=0 NormalX=0 NormalY=0 NormalZ=1 AngleXU=0 Radius=1.5 StartAngle=1.5708 EndAngle=4.71239
    g2: ArcOfCircle CenterX=-49.19 CenterY=56.25 CenterZ=0 NormalX=0 NormalY=0 NormalZ=1 AngleXU=0 Radius=1.5 StartAngle=1.5708 EndAngle=4.71239
    g3: ArcOfCircle CenterX=-49.19 CenterY=50.5 CenterZ=0 NormalX=0 NormalY=0 NormalZ=1 AngleXU=0 Radius=1.5 StartAngle=1.5708 EndAngle=4.71239
    g4: ArcOfCircle CenterX=-49.19 CenterY=44.75 CenterZ=0 NormalX=0 NormalY=0 NormalZ=1 AngleXU=0 Radius=1.5 StartAngle=1.5708 EndAngle=4.71239
    g5: ArcOfCircle CenterX=-49.19 CenterY=39 CenterZ=0 NormalX=0 NormalY=0 NormalZ=1 AngleXU=0 Radius=1.5 StartAngle=1.5708 EndAngle=4.71239
    g6: ArcOfCircle CenterX=-49.19 CenterY=33 CenterZ=0 NormalX=0 NormalY=0 NormalZ=1 AngleXU=0 Radius=1.5 StartAngle=1.5708 EndAngle=4.71239
    g7: ArcOfCircle CenterX=-49.19 CenterY=27.25 CenterZ=0 NormalX=0 NormalY=0 NormalZ=1 AngleXU=0 Radius=1.5 StartAngle=1.5708 EndAngle=4.71239
    g8: ArcOfCircle CenterX=-49.19 CenterY=21.5 CenterZ=0 NormalX=0 NormalY=0 NormalZ=1 AngleXU=0 Radius=1.5 StartAngle=1.5708 EndAngle=4.71239
    g9: ArcOfCircle CenterX=-49.19 CenterY=15.75 CenterZ=0 NormalX=0 NormalY=0 NormalZ=1 AngleXU=0 Radius=1.5 StartAngle=1.5708 EndAngle=4.71239
    g10: ArcOfCircle CenterX=-49.19 CenterY=10 CenterZ=0 NormalX=0 NormalY=0 NormalZ=1 AngleXU=0 Radius=1.5 StartAngle=1.5708 EndAngle=4.71239
    g11: ArcOfCircle CenterX=-49.19 CenterY=4.25 CenterZ=0 NormalX=0 NormalY=0 NormalZ=1 AngleXU=0 Radius=1.5 StartAngle=1.5708 EndAngle=4.71239
    g12: LineSegment StartX=-49.19 StartY=69.25 StartZ=0 EndX=-49.19 EndY=66.25 EndZ=0
    g13: LineSegment StartX=-49.19 StartY=63.5 StartZ=0 EndX=-49.19 EndY=60.5 EndZ=0
    g14: LineSegment StartX=-49.19 StartY=57.75 StartZ=0 EndX=-49.19 EndY=54.75 EndZ=0
    g15: LineSegment StartX=-49.19 StartY=52 StartZ=0 EndX=-49.19 EndY=49 EndZ=0
    g16: LineSegment StartX=-49.19 StartY=46.25 StartZ=0 EndX=-49.19 EndY=43.25 EndZ=0
    g17: LineSegment StartX=-49.19 StartY=40.5 StartZ=0 EndX=-49.19 EndY=37.5 EndZ=0
    g18: LineSegment StartX=-49.19 StartY=34.5 StartZ=0 EndX=-49.19 EndY=31.5 EndZ=0
    g19: LineSegment StartX=-49.19 StartY=28.75 StartZ=0 EndX=-49.19 EndY=25.75 EndZ=0
    g20: LineSegment StartX=-49.19 StartY=23 StartZ=0 EndX=-49.19 EndY=20 EndZ=0
    g21: LineSegment StartX=-49.19 StartY=17.25 StartZ=0 EndX=-49.19 EndY=14.25 EndZ=0
    g22: LineSegment StartX=-49.19 StartY=11.5 StartZ=0 EndX=-49.19 EndY=8.5 EndZ=0
    g23: LineSegment StartX=-49.19 StartY=5.75 StartZ=0 EndX=-49.19 EndY=2.75 EndZ=0
  constraints (48):
    c: Block(g0)
    c: Block(g1)
    c: Block(g2)
    c: Block(g3)
    c: Block(g4)
    c: Block(g5)
    c: Block(g6)
    c: Block(g7)
    c: Block(g8)
    c: Block(g9)
    c: Block(g10)
    c: Block(g11)
    c: Coincident(g12,g0)
    c: Coincident(g12,g0)
    c: Vertical(g12)
    c: Vertical(g13)
    c: Coincident(g13,g1)
    c: Vertical(g14)
    c: Coincident(g14,g2)
    c: Vertical(g15)
    c: Coincident(g15,g3)
    c: Vertical(g16)
    c: Coincident(g16,g4)
    c: Vertical(g17)
    c: Coincident(g17,g5)
    c: Vertical(g18)
    c: Coincident(g18,g6)
    c: Vertical(g19)
    c: Coincident(g19,g7)
    c: Vertical(g20)
    c: Coincident(g20,g8)
    c: Vertical(g21)
    c: Coincident(g21,g9)
    c: Vertical(g22)
    c: Coincident(g22,g10)
    c: Vertical(g23)
    c: Coincident(g23,g11)
    c: Block(g23)
    c: Block(g22)
    c: Block(g21)
    c: Block(g20)
    c: Block(g13)
    c: Block(g14)
    c: Block(g15)
    c: Block(g16)
    c: Block(g17)
    c: Block(g18)
    c: Block(g19)
FEATURE [Part::Extrusion] Extrude022
  Base = -> Sketch030
  Dir = (1,-2e-16,2e-16)
  DirMode = 2
  FaceMakerClass = Part::FaceMakerBullseye
  LengthFwd = 19
  LengthRev = 0
  Placement = pos=(-19,0,0) rot=(0,0,1;0rad)
  Solid = true
  Symmetric = false
FEATURE [Part::Fillet] Fillet022
  Base = -> Extrude022
  Edges = 24 edges r=1.49: [Edge6,Edge11,Edge18,Edge23,Edge30,Edge35,Edge42,Edge47,Edge54,Edge59,Edge66,Edge71,Edge78,Edge83,Edge90,Edge95,Edge102,Edge107,Edge114,Edge119,Edge126,Edge131,Edge138,Edge143]
FEATURE [Part::Cut] Cut020  label="top010"
  Base = -> Cut019
  Tool = -> Fillet022
FEATURE [Sketcher::SketchObject] Sketch032
  FullyConstrained = true
  Placement = pos=(117,19,0) rot=(0.57735,0.57735,0.57735;2.0944rad)
  sketch-geometry (48):
    g0: LineSegment StartX=-49.19 StartY=69.25 StartZ=0 EndX=-49.19 EndY=66.25 EndZ=0
    g1: LineSegment StartX=-49.19 StartY=63.5 StartZ=0 EndX=-49.19 EndY=60.5 EndZ=0
    g2: LineSegment StartX=-49.19 StartY=57.75 StartZ=0 EndX=-49.19 EndY=54.75 EndZ=0
    g3: LineSegment StartX=-49.19 StartY=52 StartZ=0 EndX=-49.19 EndY=49 EndZ=0
    g4: LineSegment StartX=-49.19 StartY=46.25 StartZ=0 EndX=-49.19 EndY=43.25 EndZ=0
    g5: LineSegment StartX=-49.19 StartY=40.5 StartZ=0 EndX=-49.19 EndY=37.5 EndZ=0
    g6: LineSegment StartX=-49.19 StartY=34.5 StartZ=0 EndX=-49.19 EndY=31.5 EndZ=0
    g7: LineSegment StartX=-49.19 StartY=28.75 StartZ=0 EndX=-49.19 EndY=25.75 EndZ=0
    g8: LineSegment StartX=-49.19 StartY=23 StartZ=0 EndX=-49.19 EndY=20 EndZ=0
    g9: LineSegment StartX=-49.19 StartY=17.25 StartZ=0 EndX=-49.19 EndY=14.25 EndZ=0
    g10: LineSegment StartX=-49.19 StartY=11.5 StartZ=0 EndX=-49.19 EndY=8.5 EndZ=0
    g11: LineSegment StartX=-49.19 StartY=5.75 StartZ=0 EndX=-49.19 EndY=2.75 EndZ=0
    g12: ArcOfCircle CenterX=-1.5 CenterY=67.75 CenterZ=0 NormalX=0 NormalY=0 NormalZ=1 AngleXU=0 Radius=1.5 StartAngle=4.71239 EndAngle=7.85398
    g13: ArcOfCircle CenterX=-1.5 CenterY=62 CenterZ=0 NormalX=0 NormalY=0 NormalZ=1 AngleXU=0 Radius=1.5 StartAngle=4.71239 EndAngle=7.85398
    g14: ArcOfCircle CenterX=-1.5 CenterY=56.25 CenterZ=0 NormalX=0 NormalY=0 NormalZ=1 AngleXU=0 Radius=1.5 StartAngle=4.71239 EndAngle=7.85398
    g15: ArcOfCircle CenterX=-11.49 CenterY=50.5 CenterZ=0 NormalX=0 NormalY=0 NormalZ=1 AngleXU=0 Radius=1.5 StartAngle=4.71239 EndAngle=7.85398
    g16: ArcOfCircle CenterX=-16.28 CenterY=44.75 CenterZ=0 NormalX=0 NormalY=0 NormalZ=1 AngleXU=0 Radius=1.5 StartAngle=4.71239 EndAngle=7.85398
    g17: ArcOfCircle CenterX=-18.2337 CenterY=39 CenterZ=0 NormalX=0 NormalY=0 NormalZ=1 AngleXU=0 Radius=1.5 StartAngle=4.71485 EndAngle=7.85398
    g18: ArcOfCircle CenterX=-16.2837 CenterY=27.25 CenterZ=0 NormalX=0 NormalY=0 NormalZ=1 AngleXU=0 Radius=1.5 StartAngle=4.71485 EndAngle=7.85398
    g19: ArcOfCircle CenterX=-18.2337 CenterY=33 CenterZ=0 NormalX=0 NormalY=0 NormalZ=1 AngleXU=0 Radius=1.5 StartAngle=4.71485 EndAngle=7.85398
    g20: ArcOfCircle CenterX=-11.49 CenterY=21.5 CenterZ=0 NormalX=0 NormalY=0 NormalZ=1 AngleXU=0 Radius=1.5 StartAngle=4.71239 EndAngle=7.85398
    g21: ArcOfCircle CenterX=-1.5 CenterY=4.25 CenterZ=0 NormalX=0 NormalY=0 NormalZ=1 AngleXU=0 Radius=1.5 StartAngle=4.71239 EndAngle=7.85398
    g22: ArcOfCircle CenterX=-1.5 CenterY=10 CenterZ=0 NormalX=0 NormalY=0 NormalZ=1 AngleXU=0 Radius=1.5 StartAngle=4.71239 EndAngle=7.85398
    g23: ArcOfCircle CenterX=-1.5 CenterY=15.75 CenterZ=0 NormalX=0 NormalY=0 NormalZ=1 AngleXU=0 Radius=1.5 StartAngle=4.71239 EndAngle=7.85398
    g24: LineSegment StartX=-49.19 StartY=69.25 StartZ=0 EndX=-1.5 EndY=69.25 EndZ=0
    g25: LineSegment StartX=-49.19 StartY=66.25 StartZ=0 EndX=-1.5 EndY=66.25 EndZ=0
    g26: LineSegment StartX=-49.19 StartY=63.5 StartZ=0 EndX=-1.5 EndY=63.5 EndZ=0
    g27: LineSegment StartX=-49.19 StartY=60.5 StartZ=0 EndX=-1.5 EndY=60.5 EndZ=0
    g28: LineSegment StartX=-49.19 StartY=57.75 StartZ=0 EndX=-1.5 EndY=57.75 EndZ=0
    g29: LineSegment StartX=-49.19 StartY=54.75 StartZ=0 EndX=-1.5 EndY=54.75 EndZ=0
    g30: LineSegment StartX=-49.19 StartY=52 StartZ=0 EndX=-11.49 EndY=52 EndZ=0
    g31: LineSegment StartX=-49.19 StartY=49 StartZ=0 EndX=-11.49 EndY=49 EndZ=0
    g32: LineSegment StartX=-49.19 StartY=46.25 StartZ=0 EndX=-16.28 EndY=46.25 EndZ=0
    g33: LineSegment StartX=-49.19 StartY=43.25 StartZ=0 EndX=-16.28 EndY=43.25 EndZ=0
    g34: LineSegment StartX=-49.19 StartY=40.5 StartZ=0 EndX=-18.2337 EndY=40.5 EndZ=0
    g35: LineSegment StartX=-49.19 StartY=37.5 StartZ=0 EndX=-18.23 EndY=37.5 EndZ=0
    g36: LineSegment StartX=-49.19 StartY=34.5 StartZ=0 EndX=-18.2337 EndY=34.5 EndZ=0
    g37: LineSegment StartX=-49.19 StartY=31.5 StartZ=0 EndX=-18.23 EndY=31.5 EndZ=0
    g38: LineSegment StartX=-49.19 StartY=28.75 StartZ=0 EndX=-16.2837 EndY=28.75 EndZ=0
    g39: LineSegment StartX=-49.19 StartY=25.75 StartZ=0 EndX=-16.28 EndY=25.75 EndZ=0
    g40: LineSegment StartX=-49.19 StartY=23 StartZ=0 EndX=-11.49 EndY=23 EndZ=0
    g41: LineSegment StartX=-49.19 StartY=20 StartZ=0 EndX=-11.49 EndY=20 EndZ=0
    g42: LineSegment StartX=-49.19 StartY=17.25 StartZ=0 EndX=-1.5 EndY=17.25 EndZ=0
    g43: LineSegment StartX=-49.19 StartY=14.25 StartZ=0 EndX=-1.5 EndY=14.25 EndZ=0
    g44: LineSegment StartX=-49.19 StartY=11.5 StartZ=0 EndX=-1.5 EndY=11.5 EndZ=0
    g45: LineSegment StartX=-49.19 StartY=8.5 StartZ=0 EndX=-1.5 EndY=8.5 EndZ=0
    g46: LineSegment StartX=-49.19 StartY=5.75 StartZ=0 EndX=-1.5 EndY=5.75 EndZ=0
    g47: LineSegment StartX=-49.19 StartY=2.75 StartZ=0 EndX=-1.5 EndY=2.75 EndZ=0
  constraints (120):
    c: Vertical(g0)
    c: Distance(g0) = 3
    c: Block(g0)
    c: Vertical(g1)
    c: Distance(g1) = 3
    c: Vertical(g2)
    c: Equal(g0,g2) = 3
    c: Block(g2)
    c: Vertical(g3)
    c: Equal(g1,g3) = 3
    c: Vertical(g4)
    c: Equal(g0,g4) = 3
    c: Block(g4)
    c: Vertical(g5)
    c: Equal(g1,g5) = 3
    c: Vertical(g6)
    c: Equal(g0,g6) = 3
    c: Block(g6)
    c: Vertical(g7)
    c: Equal(g1,g7) = 3
    c: Vertical(g8)
    c: Equal(g0,g8) = 3
    c: Block(g8)
    c: Vertical(g9)
    c: Equal(g1,g9) = 3
    c: Vertical(g10)
    c: Equal(g0,g10) = 3
    c: Block(g10)
    c: Vertical(g11)
    c: Equal(g1,g11) = 3
    c: Block(g12)
    c: Block(g13)
    c: Block(g14)
    c: Block(g15)
    c: Block(g16)
    c: Block(g17)
    c: Block(g18)
    c: Block(g19)
    c: Block(g20)
    c: Block(g21)
    c: Block(g22)
    c: Block(g23)
    c: Block(g11)
    c: Block(g9)
    c: Block(g7)
    c: Block(g5)
    c: Block(g3)
    c: Block(g1)
    c: Coincident(g24,g0)
    c: Coincident(g24,g12)
    c: Horizontal(g24)
    c: Coincident(g25,g0)
    c: Coincident(g25,g12)
    c: Horizontal(g25)
    c: Coincident(g26,g1)
    c: Coincident(g26,g13)
    c: Horizontal(g26)
    c: Coincident(g27,g1)
    c: Coincident(g27,g13)
    c: Horizontal(g27)
    c: Coincident(g28,g2)
    c: Coincident(g28,g14)
    c: Horizontal(g28)
    c: Coincident(g29,g2)
    c: Coincident(g29,g14)
    c: Horizontal(g29)
    c: Coincident(g30,g3)
    c: Coincident(g30,g15)
    c: Horizontal(g30)
    c: Coincident(g31,g3)
    c: Coincident(g31,g15)
    c: Horizontal(g31)
    c: Coincident(g32,g4)
    c: Coincident(g32,g16)
    c: Horizontal(g32)
    c: Coincident(g33,g4)
    c: Coincident(g33,g16)
    c: Horizontal(g33)
    c: Coincident(g34,g5)
    c: Coincident(g34,g17)
    c: Horizontal(g34)
    c: Coincident(g35,g5)
    c: Coincident(g35,g17)
    c: Horizontal(g35)
    c: Coincident(g36,g6)
    c: Coincident(g36,g19)
    c: Horizontal(g36)
    c: Coincident(g37,g6)
    c: Coincident(g37,g19)
    c: Horizontal(g37)
    c: Coincident(g38,g7)
    c: Coincident(g38,g18)
    c: Horizontal(g38)
    c: Coincident(g39,g7)
    c: Coincident(g39,g18)
    c: Horizontal(g39)
    c: Coincident(g40,g8)
    c: Coincident(g40,g20)
    c: Horizontal(g40)
    c: Coincident(g41,g8)
    c: Coincident(g41,g20)
    c: Horizontal(g41)
    c: Coincident(g42,g9)
    c: Coincident(g42,g23)
    c: Horizontal(g42)
    c: Coincident(g43,g9)
    c: Coincident(g43,g23)
    c: Horizontal(g43)
    c: Coincident(g44,g10)
    c: Coincident(g44,g22)
    c: Horizontal(g44)
    c: Coincident(g45,g10)
    c: Coincident(g45,g22)
    c: Horizontal(g45)
    c: Coincident(g46,g11)
    c: Coincident(g46,g21)
    c: Horizontal(g46)
    c: Coincident(g47,g11)
    c: Coincident(g47,g21)
    c: Horizontal(g47)
FEATURE [Part::Extrusion] Extrude023
  Base = -> Sketch032
  Dir = (1,-2e-16,2e-16)
  DirMode = 2
  FaceMakerClass = Part::FaceMakerBullseye
  LengthFwd = 19
  LengthRev = 0
  Placement = pos=(-19,0,0) rot=(0,0,1;0rad)
  Solid = true
  Symmetric = false
FEATURE [Part::Fillet] Fillet023
  Base = -> Extrude023
  Edges = <same value as first occurrence — deduplicated (x6 in doc)>
  Placement = pos=(0,0.05,0) rot=(0,0,1;0rad)
FEATURE [Part::Cut] Cut014  label="bottom003"
  Base = -> Cut007
  Tool = -> Fusion047
FEATURE [Part::Cut] Cut021  label="bottom004"
  Base = -> Cut014
  Tool = -> Fillet023
FEATURE [Sketcher::SketchObject] Sketch033
  FullyConstrained = true
  Placement = pos=(117,19,0) rot=(0.57735,0.57735,0.57735;2.0944rad)
  sketch-geometry (8):
    g0: LineSegment StartX=-49.19 StartY=69.25 StartZ=0 EndX=-49.19 EndY=66.25 EndZ=0
    g1: LineSegment StartX=-49.19 StartY=5.75 StartZ=0 EndX=-49.19 EndY=2.75 EndZ=0
    g2: ArcOfCircle CenterX=-1.5 CenterY=67.75 CenterZ=0 NormalX=0 NormalY=0 NormalZ=1 AngleXU=0 Radius=1.5 StartAngle=4.71239 EndAngle=7.85398
    g3: ArcOfCircle CenterX=-1.5 CenterY=4.25 CenterZ=0 NormalX=0 NormalY=0 NormalZ=1 AngleXU=0 Radius=1.5 StartAngle=4.71239 EndAngle=7.85398
    g4: LineSegment StartX=-49.19 StartY=69.25 StartZ=0 EndX=-1.5 EndY=69.25 EndZ=0
    g5: LineSegment StartX=-49.19 StartY=66.25 StartZ=0 EndX=-1.5 EndY=66.25 EndZ=0
    g6: LineSegment StartX=-49.19 StartY=5.75 StartZ=0 EndX=-1.5 EndY=5.75 EndZ=0
    g7: LineSegment StartX=-49.19 StartY=2.75 StartZ=0 EndX=-1.5 EndY=2.75 EndZ=0
  constraints (19):
    c: Vertical(g0)
    c: Distance(g0) = 3
    c: Block(g0)
    c: Vertical(g1)
    c: Block(g2)
    c: Block(g3)
    c: Block(g1)
    c: Coincident(g4,g0)
    c: Coincident(g4,g2)
    c: Horizontal(g4)
    c: Coincident(g5,g0)
    c: Coincident(g5,g2)
    c: Horizontal(g5)
    c: Coincident(g6,g1)
    c: Coincident(g6,g3)
    c: Horizontal(g6)
    c: Coincident(g7,g1)
    c: Coincident(g7,g3)
    c: Horizontal(g7)
FEATURE [Sketcher::SketchObject] Sketch034
  FullyConstrained = true
  Placement = pos=(117,19,0) rot=(0.57735,0.57735,0.57735;2.0944rad)
  sketch-geometry (8):
    g0: LineSegment StartX=-49.19 StartY=63.5 StartZ=0 EndX=-49.19 EndY=60.5 EndZ=0
    g1: LineSegment StartX=-49.19 StartY=11.5 StartZ=0 EndX=-49.19 EndY=8.5 EndZ=0
    g2: ArcOfCircle CenterX=-1.5 CenterY=62 CenterZ=0 NormalX=0 NormalY=0 NormalZ=1 AngleXU=0 Radius=1.5 StartAngle=4.71239 EndAngle=7.85398
    g3: ArcOfCircle CenterX=-1.5 CenterY=10 CenterZ=0 NormalX=0 NormalY=0 NormalZ=1 AngleXU=0 Radius=1.5 StartAngle=4.71239 EndAngle=7.85398
    g4: LineSegment StartX=-49.19 StartY=63.5 StartZ=0 EndX=-1.5 EndY=63.5 EndZ=0
    g5: LineSegment StartX=-49.19 StartY=60.5 StartZ=0 EndX=-1.5 EndY=60.5 EndZ=0
    g6: LineSegment StartX=-49.19 StartY=11.5 StartZ=0 EndX=-1.5 EndY=11.5 EndZ=0
    g7: LineSegment StartX=-49.19 StartY=8.5 StartZ=0 EndX=-1.5 EndY=8.5 EndZ=0
  constraints (19):
    c: Vertical(g0)
    c: Distance(g0) = 3
    c: Vertical(g1)
    c: Block(g1)
    c: Block(g2)
    c: Block(g3)
    c: Block(g0)
    c: Coincident(g4,g0)
    c: Coincident(g4,g2)
    c: Horizontal(g4)
    c: Coincident(g5,g0)
    c: Coincident(g5,g2)
    c: Horizontal(g5)
    c: Coincident(g6,g1)
    c: Coincident(g6,g3)
    c: Horizontal(g6)
    c: Coincident(g7,g1)
    c: Coincident(g7,g3)
    c: Horizontal(g7)
FEATURE [Part::Extrusion] Extrude024
  Base = -> Sketch033
  Dir = (1,0,0)
  DirMode = 2
  FaceMakerClass = Part::FaceMakerBullseye
  LengthFwd = 10
  LengthRev = 0
  Solid = true
  Symmetric = false
FEATURE [Part::Extrusion] Extrude025
  Base = -> Sketch034
  Dir = (1,0,0)
  DirMode = 2
  FaceMakerClass = Part::FaceMakerBullseye
  LengthFwd = 10
  LengthRev = 0
  Solid = true
  Symmetric = false
FEATURE [Part::Fillet] Fillet024  label="removeFromtMoreFrontCaseScrewRetainers"
  Base = -> Extrude024
  Edges = 4 edges r=1.49: [Edge6,Edge11,Edge18,Edge23]
  Placement = pos=(-11,0,0) rot=(0,0,1;0rad)
FEATURE [Part::Fillet] Fillet025  label="removeFromtMoreFrontCaseScrewRetainers001"
  Base = -> Extrude025
  Edges = 4 edges r=1.49: [Edge6,Edge11,Edge18,Edge23]
  Placement = pos=(-19,0,0) rot=(0,0,1;0rad)
FEATURE [Part::Cut] Cut022
  Base = -> Cut015
  Tool = -> Fillet025
FEATURE [Part::Cut] Cut023  label="screwRetainers"
  Base = -> Cut022
  Tool = -> Fillet024
FEATURE [Part::MultiFuse] Fusion056  label="bottom005"
  Shapes = -> [Fusion044,Cut021]
FEATURE [Part::MultiFuse] Fusion057  label="casePillars001"
  Shapes = -> [Cut016,Fusion052]
FEATURE [Part::MultiFuse] Fusion058  label="bottom006"
  Shapes = -> [Fusion056,Cut023]
FEATURE [Part::MultiFuse] Fusion059  label="bottom007"
  Shapes = -> [Fusion058,Fillet005]
FEATURE [Part::MultiFuse] Fusion060  label="bottom008"
  Shapes = -> [Fusion059,Fusion]
FEATURE [Part::MultiFuse] Fusion061  label="top011"
  Shapes = -> [Cut006,Cut020]
FEATURE [Part::MultiFuse] Fusion062  label="top012"
  Shapes = -> [Fusion057,Fusion061]
FEATURE [Sketcher::SketchObject] Sketch035  label="topSketch007"
  FullyConstrained = true
  sketch-geometry (6):
    g0: LineSegment StartX=19 StartY=38 StartZ=0 EndX=117 EndY=38 EndZ=0
    g1: ArcOfCircle CenterX=19 CenterY=19 CenterZ=0 NormalX=0 NormalY=0 NormalZ=1 AngleXU=0 Radius=19 StartAngle=1.5708 EndAngle=3.14159
    g2: LineSegment StartX=117 StartY=38 StartZ=0 EndX=117 EndY=19 EndZ=0
    g3: LineSegment StartX=98 StartY=1.0161e-12 StartZ=0 EndX=5.22862e-06 EndY=1.0161e-12 EndZ=0
    g4: LineSegment StartX=5.22862e-06 StartY=19 StartZ=0 EndX=5.22862e-06 EndY=1.0161e-12 EndZ=0
    g5: ArcOfCircle CenterX=98 CenterY=19 CenterZ=0 NormalX=0 NormalY=0 NormalZ=1 AngleXU=0 Radius=19 StartAngle=4.71239 EndAngle=6.28319
  constraints (16):
    c: Horizontal(g0)
    c: Distance(g0) = 98
    c: Coincident(g1,g0)
    c: Block(g1)
    c: Coincident(g2,g0)
    c: Vertical(g2)
    c: Distance(g2) = 19
    c: Horizontal(g3)
    c: Coincident(g4,g1)
    c: Vertical(g4)
    c: Coincident(g3,g4)
    c: Block(g3)
    c: Coincident(g5,g2)
    c: Coincident(g5,g3)
    c: Block(g0)
    c: Block(g5)
FEATURE [Part::Extrusion] Extrude026  label="sideA001"
  Base = -> Sketch035
  Dir = (0,0,1)
  DirMode = 2
  FaceMakerClass = Part::FaceMakerBullseye
  LengthFwd = 3
  LengthRev = 0
  Placement = pos=(0,0,-2.7) rot=(0,0,1;0rad)
  Solid = true
  Symmetric = false
FEATURE [Sketcher::SketchObject] Sketch036  label="topSketch008"
  FullyConstrained = true
  sketch-geometry (6):
    g0: LineSegment StartX=19 StartY=38 StartZ=0 EndX=117 EndY=38 EndZ=0
    g1: ArcOfCircle CenterX=19 CenterY=19 CenterZ=0 NormalX=0 NormalY=0 NormalZ=1 AngleXU=0 Radius=19 StartAngle=1.5708 EndAngle=3.14159
    g2: LineSegment StartX=117 StartY=38 StartZ=0 EndX=117 EndY=19 EndZ=0
    g3: LineSegment StartX=98 StartY=1.0161e-12 StartZ=0 EndX=5.22862e-06 EndY=1.0161e-12 EndZ=0
    g4: LineSegment StartX=5.22862e-06 StartY=19 StartZ=0 EndX=5.22862e-06 EndY=1.0161e-12 EndZ=0
    g5: ArcOfCircle CenterX=98 CenterY=19 CenterZ=0 NormalX=0 NormalY=0 NormalZ=1 AngleXU=0 Radius=19 StartAngle=4.71239 EndAngle=6.28319
  constraints (16):
    c: Horizontal(g0)
    c: Distance(g0) = 98
    c: Coincident(g1,g0)
    c: Block(g1)
    c: Coincident(g2,g0)
    c: Vertical(g2)
    c: Distance(g2) = 19
    c: Horizontal(g3)
    c: Coincident(g4,g1)
    c: Vertical(g4)
    c: Coincident(g3,g4)
    c: Block(g3)
    c: Coincident(g5,g2)
    c: Coincident(g5,g3)
    c: Block(g0)
    c: Block(g5)
FEATURE [Part::Extrusion] Extrude027  label="sideB001"
  Base = -> Sketch036
  Dir = (0,0,1)
  DirMode = 2
  FaceMakerClass = Part::FaceMakerBullseye
  LengthFwd = 3
  LengthRev = 0
  Placement = pos=(0,0,71.7) rot=(0,0,1;0rad)
  Solid = true
  Symmetric = false
FEATURE [Part::MultiFuse] Fusion064  label="removeFromBottom"
  Shapes = -> [Extrude026,Extrude027]
FEATURE [Part::Cut] Cut024  label="bottom009"
  Base = -> Fusion060
  Tool = -> Fusion064
FEATURE [Sketcher::SketchObject] Sketch037  label="topSketch009"
  FullyConstrained = true
  sketch-geometry (8):
    g0: ArcOfCircle CenterX=19 CenterY=19.1201 CenterZ=0 NormalX=0 NormalY=0 NormalZ=1 AngleXU=0 Radius=18.8799 StartAngle=1.5708 EndAngle=3.14793
    g1: LineSegment StartX=0.120501 StartY=19.0004 StartZ=0 EndX=0.120501 EndY=0.000382114 EndZ=0
    g2: LineSegment StartX=19 StartY=38 StartZ=0 EndX=124 EndY=38 EndZ=0
    g3: LineSegment StartX=0.120501 StartY=0.000382114 StartZ=0 EndX=105.121 EndY=0.000382114 EndZ=0
    g4: LineSegment StartX=124 StartY=38 StartZ=0 EndX=125.616 EndY=38 EndZ=0
    g5: LineSegment StartX=105.121 StartY=0.000382114 StartZ=0 EndX=106.736 EndY=0.000382114 EndZ=0
    g6: ArcOfCircle CenterX=106.616 CenterY=19 CenterZ=0 NormalX=0 NormalY=0 NormalZ=1 AngleXU=0 Radius=19 StartAngle=4.71873 EndAngle=6.28319
    g7: LineSegment StartX=125.616 StartY=38 StartZ=0 EndX=125.616 EndY=19 EndZ=0
  constraints (21):
    c: Block(g0)
    c: Coincident(g1,g0)
    c: Vertical(g1)
    c: Horizontal(g2)
    c: Distance(g2) = 105
    c: Coincident(g2,g0)
    c: Distance(g1) = 19
    c: Coincident(g3,g1)
    c: Horizontal(g3)
    c: Distance(g3) = 105
    c: Coincident(g4,g2)
    c: Horizontal(g4)
    c: Distance(g4) = 1.61553
    c: Horizontal(g5)
    c: Equal(g4,g5) = 1.61553
    c: Coincident(g5,g3)
    c: Block(g6)
    c: Coincident(g6,g5)
    c: Coincident(g7,g4)
    c: Coincident(g7,g6)
    c: Vertical(g7)
FEATURE [Part::Extrusion] Extrude028  label="sideB"
  Base = -> Sketch037
  Dir = (0,0,1)
  DirMode = 2
  FaceMakerClass = Part::FaceMakerBullseye
  LengthFwd = 3
  LengthRev = 0
  Placement = pos=(0,0,72) rot=(0,0,1;0rad)
  Solid = true
  Symmetric = false
FEATURE [Sketcher::SketchObject] Sketch038  label="topSketch010"
  FullyConstrained = true
  sketch-geometry (22):
    g0: LineSegment StartX=5.21097e-06 StartY=3 StartZ=0 EndX=5.21097e-06 EndY=19 EndZ=0
    g1: ArcOfCircle CenterX=19 CenterY=19 CenterZ=0 NormalX=0 NormalY=0 NormalZ=1 AngleXU=0 Radius=19 StartAngle=1.5708 EndAngle=3.14159
    g2: ArcOfCircle CenterX=19 CenterY=19 CenterZ=0 NormalX=0 NormalY=0 NormalZ=1 AngleXU=0 Radius=16 StartAngle=1.5708 EndAngle=3.14159
    g3: LineSegment StartX=114 StartY=35 StartZ=0 EndX=19 EndY=35 EndZ=0
    g4: LineSegment StartX=5.21097e-06 StartY=3 StartZ=0 EndX=5.21097e-06 EndY=0 EndZ=0
    g5: LineSegment StartX=3 StartY=0 StartZ=0 EndX=5.21097e-06 EndY=0 EndZ=0
    g6: LineSegment StartX=3 StartY=19 StartZ=0 EndX=3 EndY=0 EndZ=0
    g7: LineSegment StartX=19 StartY=38 StartZ=0 EndX=124 EndY=38 EndZ=0
    g8: Circle CenterX=119 CenterY=35 CenterZ=0 NormalX=0 NormalY=0 NormalZ=1 AngleXU=0 Radius=1
    g9: Circle CenterX=121 CenterY=35 CenterZ=0 NormalX=0 NormalY=0 NormalZ=1 AngleXU=0 Radius=1
    g10: Circle CenterX=121 CenterY=33 CenterZ=0 NormalX=0 NormalY=0 NormalZ=1 AngleXU=0 Radius=1
    g11: BSplineCurve PolesCount=3 KnotsCount=2 Degree=2 IsPeriodic=0
    g12: GeomPoint X=119 Y=35 Z=0
    g13: GeomPoint X=121 Y=33 Z=0
    g14: LineSegment StartX=119 StartY=35 StartZ=0 EndX=114 EndY=35 EndZ=0
    g15: ArcOfCircle CenterX=105 CenterY=19 CenterZ=0 NormalX=0 NormalY=0 NormalZ=1 AngleXU=0 Radius=16 StartAngle=5.60905 EndAngle=6.28319
    g16: LineSegment StartX=121 StartY=33 StartZ=0 EndX=121 EndY=19 EndZ=0
    g17: LineSegment StartX=117.5 StartY=9.01251 StartZ=0 EndX=121.163 EndY=9.0125 EndZ=0
    g18: ArcOfCircle CenterX=105 CenterY=19 CenterZ=0 NormalX=0 NormalY=0 NormalZ=1 AngleXU=0 Radius=20.6155 StartAngle=5.7297 EndAngle=6.28319
    g19: LineSegment StartX=121.163 StartY=9.0125 StartZ=0 EndX=122.538 EndY=8.16329 EndZ=0
    g20: LineSegment StartX=124 StartY=38 StartZ=0 EndX=125.616 EndY=38 EndZ=0
    g21: LineSegment StartX=125.616 StartY=19 StartZ=0 EndX=125.616 EndY=38 EndZ=0
  constraints (49):
    c: Vertical(g0)
    c: Block(g0)
    c: Coincident(g1,g0)
    c: Block(g1)
    c: Coincident(g2,g1)
    c: Block(g2)
    c: Coincident(g3,g2)
    c: Horizontal(g3)
    c: Tangent(g3,g2)
    c: Coincident(g4,g0)
    c: Distance(g4) = 3
    c: Vertical(g4)
    c: Coincident(g5,g4)
    c: Horizontal(g5)
    c: Coincident(g6,g2)
    c: Coincident(g6,g5)
    c: Vertical(g6)
    c: Horizontal(g7)
    c: Distance(g7) = 105
    c: Coincident(g7,g1)
    c: Block(g3)
    c: Weight(g8) = 1
    c: Equal(g8,g9)
    c: Equal(g8,g10)
    c: InternalAlignment(g8,g11)
    c: InternalAlignment(g9,g11)
    c: InternalAlignment(g10,g11)
    c: InternalAlignment(g12,g11)
    c: InternalAlignment(g13,g11)
    c: Block(g11)
    c: Coincident(g14,g11)
    c: Coincident(g14,g3)
    c: Horizontal(g14)
    c: Block(g15)
    c: Coincident(g16,g11)
    c: Coincident(g16,g15)
    c: Vertical(g16)
    c: Distance(g16) = 14
    c: Coincident(g17,g15)
    c: Block(g18)
    c: Coincident(g19,g18)
    c: Coincident(g20,g7)
    c: Horizontal(g20)
    c: Vertical(g21)
    c: Coincident(g20,g21)
    c: Block(g20)
    c: Block(g21)
    c: Block(g19)
    c: Block(g17)
FEATURE [Part::Extrusion] Extrude029
  Base = -> Sketch038
  Dir = (0,0,1)
  DirMode = 2
  FaceMakerClass = Part::FaceMakerBullseye
  LengthFwd = 72
  LengthRev = 0
  Solid = true
  Symmetric = false
FEATURE [Part::Feature] Face085
  shape: bbox 4.8 x 25.5 x 2e-07 mm, 1 faces, 0 solids (baked)
FEATURE [Part::Revolution] Revolve089  label="moreFrontCaseScrewPost003"
  Angle = 360
  Axis = (0,1,0)
  Base = (0,0,0)
  FaceMakerClass = Part::FaceMakerBullseye
  Placement = pos=(109.5,4.5,3.5) rot=(0,0,1;0rad)
  Solid = false
  Source = -> Face085
  Symmetric = false
FEATURE [Part::Feature] Face086
  shape: bbox 4.8 x 25.5 x 2e-07 mm, 1 faces, 0 solids (baked)
FEATURE [Part::Revolution] Revolve090  label="moreFrontCaseScrewPost004"
  Angle = 360
  Axis = (0,1,0)
  Base = (0,0,0)
  FaceMakerClass = Part::FaceMakerBullseye
  Placement = pos=(109.5,4.5,68.5) rot=(0,0,1;0rad)
  Solid = false
  Source = -> Face086
  Symmetric = false
FEATURE [Part::Fillet] Fillet026  label="top013"
  Base = -> Extrude029
  Edges = 1 edges r=2: [Edge35]
FEATURE [Sketcher::SketchObject] Sketch039
  FullyConstrained = true
  sketch-geometry (7):
    g0: LineSegment StartX=0 StartY=0 StartZ=0 EndX=0 EndY=6 EndZ=0
    g1: Circle CenterX=0 CenterY=0 CenterZ=0 NormalX=0 NormalY=0 NormalZ=1 AngleXU=0 Radius=1
    g2: Circle CenterX=8 CenterY=6 CenterZ=0 NormalX=0 NormalY=0 NormalZ=1 AngleXU=0 Radius=1
    g3: BSplineCurve PolesCount=3 KnotsCount=2 Degree=2 IsPeriodic=0
    g4: GeomPoint X=0 Y=0 Z=0
    g5: GeomPoint X=8 Y=6 Z=0
    g6: LineSegment StartX=0 StartY=6 StartZ=0 EndX=8 EndY=6 EndZ=0
  constraints (14):
    c: Coincident(g0,g-1)
    c: Distance(g0) = 6
    c: Vertical(g0)
    c: Coincident(g3,g0)
    c: Weight(g1) = 1
    c: Equal(g1,g2)
    c: InternalAlignment(g1,g3)
    c: InternalAlignment(g2,g3)
    c: InternalAlignment(g4,g3)
    c: InternalAlignment(g5,g3)
    c: Block(g3)
    c: Coincident(g6,g0)
    c: Coincident(g6,g3)
    c: Horizontal(g6)
FEATURE [Sketcher::SketchObject] Sketch040
  FullyConstrained = true
  sketch-geometry (7):
    g0: LineSegment StartX=0 StartY=0 StartZ=0 EndX=0 EndY=6 EndZ=0
    g1: Circle CenterX=0 CenterY=0 CenterZ=0 NormalX=0 NormalY=0 NormalZ=1 AngleXU=0 Radius=1
    g2: Circle CenterX=8 CenterY=6 CenterZ=0 NormalX=0 NormalY=0 NormalZ=1 AngleXU=0 Radius=1
    g3: BSplineCurve PolesCount=3 KnotsCount=2 Degree=2 IsPeriodic=0
    g4: GeomPoint X=0 Y=0 Z=0
    g5: GeomPoint X=8 Y=6 Z=0
    g6: LineSegment StartX=0 StartY=6 StartZ=0 EndX=8 EndY=6 EndZ=0
  constraints (14):
    c: Coincident(g0,g-1)
    c: Distance(g0) = 6
    c: Vertical(g0)
    c: Coincident(g3,g0)
    c: Weight(g1) = 1
    c: Equal(g1,g2)
    c: InternalAlignment(g1,g3)
    c: InternalAlignment(g2,g3)
    c: InternalAlignment(g4,g3)
    c: InternalAlignment(g5,g3)
    c: Block(g3)
    c: Coincident(g6,g0)
    c: Coincident(g6,g3)
    c: Horizontal(g6)
FEATURE [Sketcher::SketchObject] Sketch041
  FullyConstrained = true
  sketch-geometry (7):
    g0: LineSegment StartX=0 StartY=0 StartZ=0 EndX=0 EndY=6 EndZ=0
    g1: Circle CenterX=0 CenterY=0 CenterZ=0 NormalX=0 NormalY=0 NormalZ=1 AngleXU=0 Radius=1
    g2: Circle CenterX=8 CenterY=6 CenterZ=0 NormalX=0 NormalY=0 NormalZ=1 AngleXU=0 Radius=1
    g3: BSplineCurve PolesCount=3 KnotsCount=2 Degree=2 IsPeriodic=0
    g4: GeomPoint X=0 Y=0 Z=0
    g5: GeomPoint X=8 Y=6 Z=0
    g6: LineSegment StartX=0 StartY=6 StartZ=0 EndX=8 EndY=6 EndZ=0
  constraints (14):
    c: Coincident(g0,g-1)
    c: Distance(g0) = 6
    c: Vertical(g0)
    c: Coincident(g3,g0)
    c: Weight(g1) = 1
    c: Equal(g1,g2)
    c: InternalAlignment(g1,g3)
    c: InternalAlignment(g2,g3)
    c: InternalAlignment(g4,g3)
    c: InternalAlignment(g5,g3)
    c: Block(g3)
    c: Coincident(g6,g0)
    c: Coincident(g6,g3)
    c: Horizontal(g6)
FEATURE [Sketcher::SketchObject] Sketch042
  FullyConstrained = true
  sketch-geometry (7):
    g0: LineSegment StartX=0 StartY=0 StartZ=0 EndX=0 EndY=6 EndZ=0
    g1: Circle CenterX=0 CenterY=0 CenterZ=0 NormalX=0 NormalY=0 NormalZ=1 AngleXU=0 Radius=1
    g2: Circle CenterX=8 CenterY=6 CenterZ=0 NormalX=0 NormalY=0 NormalZ=1 AngleXU=0 Radius=1
    g3: BSplineCurve PolesCount=3 KnotsCount=2 Degree=2 IsPeriodic=0
    g4: GeomPoint X=0 Y=0 Z=0
    g5: GeomPoint X=8 Y=6 Z=0
    g6: LineSegment StartX=0 StartY=6 StartZ=0 EndX=8 EndY=6 EndZ=0
  constraints (14):
    c: Coincident(g0,g-1)
    c: Distance(g0) = 6
    c: Vertical(g0)
    c: Coincident(g3,g0)
    c: Weight(g1) = 1
    c: Equal(g1,g2)
    c: InternalAlignment(g1,g3)
    c: InternalAlignment(g2,g3)
    c: InternalAlignment(g4,g3)
    c: InternalAlignment(g5,g3)
    c: Block(g3)
    c: Coincident(g6,g0)
    c: Coincident(g6,g3)
    c: Horizontal(g6)
FEATURE [Part::Extrusion] Extrude030  label="caseScrewPillarBracket008"
  Base = -> Sketch039
  Dir = (0,0,1)
  DirMode = 2
  FaceMakerClass = Part::FaceMakerBullseye
  LengthFwd = 2.4
  LengthRev = 0
  Placement = pos=(15.76,29,8.8) rot=(0,1,0;0rad)
  Solid = true
  Symmetric = false
FEATURE [Part::Extrusion] Extrude031  label="caseScrewPillarBracket009"
  Base = -> Sketch040
  Dir = (0,0,1)
  DirMode = 2
  FaceMakerClass = Part::FaceMakerBullseye
  LengthFwd = 2.4
  LengthRev = 0
  Placement = pos=(15.76,29,60.8) rot=(0,0,1;0rad)
  Solid = true
  Symmetric = false
FEATURE [Part::Extrusion] Extrude032  label="caseScrewPillarBracket010"
  Base = -> Sketch041
  Dir = (0,0,1)
  DirMode = 2
  FaceMakerClass = Part::FaceMakerBullseye
  LengthFwd = 2.4
  LengthRev = 0
  Placement = pos=(13.7,29,13.26) rot=(0,-1,0;1.5708rad)
  Solid = true
  Symmetric = false
FEATURE [Part::Extrusion] Extrude033  label="caseScrewPillarBracket011"
  Base = -> Sketch042
  Dir = (0,0,1)
  DirMode = 2
  FaceMakerClass = Part::FaceMakerBullseye
  LengthFwd = 2.4
  LengthRev = 0
  Placement = pos=(11.3,29,58.74) rot=(0,1,0;1.5708rad)
  Solid = true
  Symmetric = false
FEATURE [Sketcher::SketchObject] Sketch043
  FullyConstrained = true
  sketch-geometry (7):
    g0: LineSegment StartX=0 StartY=0 StartZ=0 EndX=0 EndY=6 EndZ=0
    g1: Circle CenterX=0 CenterY=0 CenterZ=0 NormalX=0 NormalY=0 NormalZ=1 AngleXU=0 Radius=1
    g2: Circle CenterX=8 CenterY=6 CenterZ=0 NormalX=0 NormalY=0 NormalZ=1 AngleXU=0 Radius=1
    g3: BSplineCurve PolesCount=3 KnotsCount=2 Degree=2 IsPeriodic=0
    g4: GeomPoint X=0 Y=0 Z=0
    g5: GeomPoint X=8 Y=6 Z=0
    g6: LineSegment StartX=0 StartY=6 StartZ=0 EndX=8 EndY=6 EndZ=0
  constraints (14):
    c: Coincident(g0,g-1)
    c: Distance(g0) = 6
    c: Vertical(g0)
    c: Coincident(g3,g0)
    c: Weight(g1) = 1
    c: Equal(g1,g2)
    c: InternalAlignment(g1,g3)
    c: InternalAlignment(g2,g3)
    c: InternalAlignment(g4,g3)
    c: InternalAlignment(g5,g3)
    c: Block(g3)
    c: Coincident(g6,g0)
    c: Coincident(g6,g3)
    c: Horizontal(g6)
FEATURE [Part::Extrusion] Extrude034  label="caseScrewPillarBracket012"
  Base = -> Sketch043
  Dir = (0,0,1)
  DirMode = 2
  FaceMakerClass = Part::FaceMakerBullseye
  LengthFwd = 2.4
  LengthRev = 0
  Placement = pos=(88.3,29,65.23) rot=(0,1,0;1.5708rad)
  Solid = true
  Symmetric = false
FEATURE [Sketcher::SketchObject] Sketch044
  FullyConstrained = true
  sketch-geometry (7):
    g0: LineSegment StartX=0 StartY=0 StartZ=0 EndX=0 EndY=6 EndZ=0
    g1: Circle CenterX=0 CenterY=0 CenterZ=0 NormalX=0 NormalY=0 NormalZ=1 AngleXU=0 Radius=1
    g2: Circle CenterX=8 CenterY=6 CenterZ=0 NormalX=0 NormalY=0 NormalZ=1 AngleXU=0 Radius=1
    g3: BSplineCurve PolesCount=3 KnotsCount=2 Degree=2 IsPeriodic=0
    g4: GeomPoint X=0 Y=0 Z=0
    g5: GeomPoint X=8 Y=6 Z=0
    g6: LineSegment StartX=0 StartY=6 StartZ=0 EndX=8 EndY=6 EndZ=0
  constraints (14):
    c: Coincident(g0,g-1)
    c: Distance(g0) = 6
    c: Vertical(g0)
    c: Coincident(g3,g0)
    c: Weight(g1) = 1
    c: Equal(g1,g2)
    c: InternalAlignment(g1,g3)
    c: InternalAlignment(g2,g3)
    c: InternalAlignment(g4,g3)
    c: InternalAlignment(g5,g3)
    c: Block(g3)
    c: Coincident(g6,g0)
    c: Coincident(g6,g3)
    c: Horizontal(g6)
FEATURE [Part::Extrusion] Extrude035  label="caseScrewPillarBracket013"
  Base = -> Sketch044
  Dir = (0,0,1)
  DirMode = 2
  FaceMakerClass = Part::FaceMakerBullseye
  LengthFwd = 2.4
  LengthRev = 0
  Placement = pos=(90.7,29,6.77) rot=(0,-1,0;1.5708rad)
  Solid = true
  Symmetric = false
FEATURE [Sketcher::SketchObject] Sketch045
  FullyConstrained = true
  sketch-geometry (7):
    g0: LineSegment StartX=0 StartY=0 StartZ=0 EndX=0 EndY=6 EndZ=0
    g1: Circle CenterX=0 CenterY=0 CenterZ=0 NormalX=0 NormalY=0 NormalZ=1 AngleXU=0 Radius=1
    g2: Circle CenterX=8 CenterY=6 CenterZ=0 NormalX=0 NormalY=0 NormalZ=1 AngleXU=0 Radius=1
    g3: BSplineCurve PolesCount=3 KnotsCount=2 Degree=2 IsPeriodic=0
    g4: GeomPoint X=0 Y=0 Z=0
    g5: GeomPoint X=8 Y=6 Z=0
    g6: LineSegment StartX=0 StartY=6 StartZ=0 EndX=8 EndY=6 EndZ=0
  constraints (14):
    c: Coincident(g0,g-1)
    c: Distance(g0) = 6
    c: Vertical(g0)
    c: Coincident(g3,g0)
    c: Weight(g1) = 1
    c: Equal(g1,g2)
    c: InternalAlignment(g1,g3)
    c: InternalAlignment(g2,g3)
    c: InternalAlignment(g4,g3)
    c: InternalAlignment(g5,g3)
    c: Block(g3)
    c: Coincident(g6,g0)
    c: Coincident(g6,g3)
    c: Horizontal(g6)
FEATURE [Sketcher::SketchObject] Sketch046
  FullyConstrained = true
  sketch-geometry (7):
    g0: LineSegment StartX=0 StartY=0 StartZ=0 EndX=0 EndY=6 EndZ=0
    g1: Circle CenterX=0 CenterY=0 CenterZ=0 NormalX=0 NormalY=0 NormalZ=1 AngleXU=0 Radius=1
    g2: Circle CenterX=8 CenterY=6 CenterZ=0 NormalX=0 NormalY=0 NormalZ=1 AngleXU=0 Radius=1
    g3: BSplineCurve PolesCount=3 KnotsCount=2 Degree=2 IsPeriodic=0
    g4: GeomPoint X=0 Y=0 Z=0
    g5: GeomPoint X=8 Y=6 Z=0
    g6: LineSegment StartX=0 StartY=6 StartZ=0 EndX=8 EndY=6 EndZ=0
  constraints (14):
    c: Coincident(g0,g-1)
    c: Distance(g0) = 6
    c: Vertical(g0)
    c: Coincident(g3,g0)
    c: Weight(g1) = 1
    c: Equal(g1,g2)
    c: InternalAlignment(g1,g3)
    c: InternalAlignment(g2,g3)
    c: InternalAlignment(g4,g3)
    c: InternalAlignment(g5,g3)
    c: Block(g3)
    c: Coincident(g6,g0)
    c: Coincident(g6,g3)
    c: Horizontal(g6)
FEATURE [Part::Extrusion] Extrude036  label="caseScrewPillarBracket014"
  Base = -> Sketch045
  Dir = (0,0,1)
  DirMode = 2
  FaceMakerClass = Part::FaceMakerBullseye
  LengthFwd = 2.4
  LengthRev = 0
  Placement = pos=(110.7,29,6.77) rot=(0,-1,0;1.5708rad)
  Solid = true
  Symmetric = false
FEATURE [Part::Extrusion] Extrude037  label="caseScrewPillarBracket015"
  Base = -> Sketch046
  Dir = (0,0,1)
  DirMode = 2
  FaceMakerClass = Part::FaceMakerBullseye
  LengthFwd = 2.4
  LengthRev = 0
  Placement = pos=(108.3,29,65.23) rot=(0,1,0;1.5708rad)
  Solid = true
  Symmetric = false
FEATURE [Part::Box] Box013  label="frontCaseScrewPillarBracket002"
  AttacherType = Attacher::AttachEngine3D
  Height = 2.4
  Length = 22
  Placement = pos=(87,28,2.3) rot=(0,0,1;0rad)
  Width = 7
FEATURE [Part::Box] Box014  label="frontCaseScrewPillarBracket003"
  AttacherType = Attacher::AttachEngine3D
  Height = 2.4
  Length = 22
  Placement = pos=(87,28,67.3) rot=(0,0,1;0rad)
  Width = 7
FEATURE [Part::Feature] Face087
  shape: bbox 4.8 x 30.2 x 2e-07 mm, 1 faces, 0 solids (baked)
FEATURE [Part::Revolution] Revolve091  label="frontCaseScrewPost004"
  Angle = 360
  Axis = (0,1,0)
  Base = (0,0,0)
  FaceMakerClass = Part::FaceMakerBullseye
  Placement = pos=(89.5,4.5,3.5) rot=(0,0,1;0rad)
  Solid = false
  Source = -> Face087
  Symmetric = false
FEATURE [Part::Feature] Face088
  shape: bbox 4.8 x 30.2 x 2e-07 mm, 1 faces, 0 solids (baked)
FEATURE [Part::Revolution] Revolve092  label="frontCaseScrewPost005"
  Angle = 360
  Axis = (0,1,0)
  Base = (0,0,0)
  FaceMakerClass = Part::FaceMakerBullseye
  Placement = pos=(89.5,4.5,68.5) rot=(0,0,1;0rad)
  Solid = false
  Source = -> Face088
  Symmetric = false
FEATURE [Part::Feature] Face089
  shape: bbox 3.5 x 30.2 x 2e-07 mm, 1 faces, 0 solids (baked)
FEATURE [Part::Revolution] Revolve093  label="backCaseScrewPost002"
  Angle = 360
  Axis = (0,1,0)
  Base = (0,0,0)
  FaceMakerClass = Part::FaceMakerBullseye
  Placement = pos=(12.5,4.5,10) rot=(0,0,1;0rad)
  Solid = false
  Source = -> Face089
  Symmetric = false
FEATURE [Part::Feature] Face090
  shape: bbox 3.5 x 30.2 x 2e-07 mm, 1 faces, 0 solids (baked)
FEATURE [Part::Revolution] Revolve094  label="backCaseScrewPost003"
  Angle = 360
  Axis = (0,1,0)
  Base = (0,0,0)
  FaceMakerClass = Part::FaceMakerBullseye
  Placement = pos=(12.5,4.5,62) rot=(0,0,1;0rad)
  Solid = false
  Source = -> Face090
  Symmetric = false
FEATURE [Part::Box] Box015  label="Cube011"
  AttacherType = Attacher::AttachEngine3D
  Height = 28.8
  Length = 3
  Placement = pos=(107.3,28,21.6) rot=(0,0,1;0rad)
  Width = 7
FEATURE [Part::Box] Box016  label="Cube012"
  AttacherType = Attacher::AttachEngine3D
  Height = 3
  Length = 7.4
  Placement = pos=(107.3,28,18.6) rot=(0,0,1;0rad)
  Width = 7
FEATURE [Part::Box] Box017  label="Cube013"
  AttacherType = Attacher::AttachEngine3D
  Height = 3
  Length = 7.4
  Placement = pos=(107.3,28,50.4) rot=(0,0,1;0rad)
  Width = 7
FEATURE [Part::Cylinder] Cylinder024
  Angle = 360
  AttacherType = Attacher::AttachEngine3D
  Height = 20
  Placement = pos=(0,0,36.15) rot=(0,0,1;0rad)
  Radius = 14.3
FEATURE [Part::Cylinder] Cylinder025
  Angle = 360
  AttacherType = Attacher::AttachEngine3D
  Height = 10
  Placement = pos=(0,0,36.15) rot=(0,0,1;0rad)
  Radius = 4
FEATURE [Part::MultiFuse] Fusion066  label="removeToCreteHoleForPlugHousing009"
  Placement = pos=(70,19,36) rot=(0,1,0;1.5708rad)
  Shapes = -> [Cylinder024,Cylinder025]
FEATURE [Part::MultiFuse] Fusion065  label="plugHousingBracketHolder002"
  Shapes = -> [Box017,Box015,Box016]
FEATURE [Part::Cut] Cut025  label="plugHousingBracketHolder003"
  Base = -> Fusion065
  Placement = pos=(7,0,0) rot=(0,0,1;0rad)
  Tool = -> Fusion066
FEATURE [Sketcher::SketchObject] Sketch047
  FullyConstrained = false
  Placement = pos=(0,0,0) rot=(1,0,0;1.5708rad)
  sketch-geometry (24):
    g0: ArcOfCircle CenterX=-4 CenterY=-10.5 CenterZ=0 NormalX=0 NormalY=0 NormalZ=1 AngleXU=0 Radius=1.5 StartAngle=6e-16 EndAngle=3.14159
    g1: ArcOfCircle CenterX=-34.2 CenterY=-10.5 CenterZ=0 NormalX=0 NormalY=0 NormalZ=1 AngleXU=0 Radius=1.5 StartAngle=0 EndAngle=3.14159
    g2: ArcOfCircle CenterX=-34.2 CenterY=-27.7 CenterZ=0 NormalX=0 NormalY=0 NormalZ=1 AngleXU=0 Radius=1.5 StartAngle=3.14159 EndAngle=6.28319
    g3: ArcOfCircle CenterX=-4 CenterY=-27.7 CenterZ=0 NormalX=0 NormalY=0 NormalZ=1 AngleXU=0 Radius=1.5 StartAngle=3.1416 EndAngle=6.28319
    g4: ArcOfCircle CenterX=-10 CenterY=-4.3 CenterZ=0 NormalX=0 NormalY=0 NormalZ=1 AngleXU=0 Radius=1.5 StartAngle=2e-16 EndAngle=3.14159
    g5: ArcOfCircle CenterX=-16.1 CenterY=-1.8 CenterZ=0 NormalX=0 NormalY=0 NormalZ=1 AngleXU=0 Radius=1.5 StartAngle=5e-16 EndAngle=3.14159
    g6: ArcOfCircle CenterX=-22.1 CenterY=-1.8 CenterZ=0 NormalX=0 NormalY=0 NormalZ=1 AngleXU=0 Radius=1.5 StartAngle=5e-16 EndAngle=3.14159
    g7: ArcOfCircle CenterX=-28.2 CenterY=-4.3 CenterZ=0 NormalX=0 NormalY=0 NormalZ=1 AngleXU=0 Radius=1.5 StartAngle=2e-16 EndAngle=3.14159
    g8: ArcOfCircle CenterX=-10 CenterY=-33.9 CenterZ=0 NormalX=0 NormalY=0 NormalZ=1 AngleXU=0 Radius=1.5 StartAngle=3.14159 EndAngle=6.28319
    g9: ArcOfCircle CenterX=-16.1 CenterY=-36.4 CenterZ=0 NormalX=0 NormalY=0 NormalZ=1 AngleXU=0 Radius=1.5 StartAngle=3.14159 EndAngle=6.28319
    g10: ArcOfCircle CenterX=-22.1 CenterY=-36.4 CenterZ=0 NormalX=0 NormalY=0 NormalZ=1 AngleXU=0 Radius=1.5 StartAngle=3.14159 EndAngle=6.28319
    g11: ArcOfCircle CenterX=-28.2 CenterY=-33.9 CenterZ=0 NormalX=0 NormalY=0 NormalZ=1 AngleXU=0 Radius=1.5 StartAngle=3.14159 EndAngle=6.28319
    g12: LineSegment StartX=-35.7 StartY=-10.5 StartZ=0 EndX=-35.7 EndY=-27.7 EndZ=0
    g13: LineSegment StartX=-32.7 StartY=-10.5 StartZ=0 EndX=-32.7 EndY=-27.7 EndZ=0
    g14: LineSegment StartX=-29.7 StartY=-33.9 StartZ=0 EndX=-29.7 EndY=-4.3 EndZ=0
    g15: LineSegment StartX=-26.7 StartY=-33.9 StartZ=0 EndX=-26.7 EndY=-4.3 EndZ=0
    g16: LineSegment StartX=-2.5 StartY=-10.5 StartZ=0 EndX=-2.5 EndY=-27.7 EndZ=0
    g17: LineSegment StartX=-8.5 StartY=-4.3 StartZ=0 EndX=-8.5 EndY=-33.9 EndZ=0
    g18: LineSegment StartX=-5.5 StartY=-10.5 StartZ=0 EndX=-5.5 EndY=-27.7 EndZ=0
    g19: LineSegment StartX=-11.5 StartY=-4.3 StartZ=0 EndX=-11.5 EndY=-33.9 EndZ=0
    g20: LineSegment StartX=-14.6 StartY=-1.8 StartZ=0 EndX=-14.6 EndY=-36.4 EndZ=0
    g21: LineSegment StartX=-17.6 StartY=-1.8 StartZ=0 EndX=-17.6 EndY=-36.4 EndZ=0
    g22: LineSegment StartX=-20.6 StartY=-36.4 StartZ=0 EndX=-20.6 EndY=-1.8 EndZ=0
    g23: LineSegment StartX=-23.6 StartY=-1.8 StartZ=0 EndX=-23.6 EndY=-36.4 EndZ=0
  constraints (48):
    c: Block(g0)
    c: Block(g1)
    c: Block(g2)
    c: Block(g3)
    c: Block(g4)
    c: Block(g5)
    c: Block(g6)
    c: Block(g7)
    c: Block(g8)
    c: Block(g9)
    c: Block(g10)
    c: Block(g11)
    c: Coincident(g12,g1)
    c: Coincident(g12,g2)
    c: Vertical(g12)
    c: Coincident(g13,g1)
    c: Coincident(g13,g2)
    c: Vertical(g13)
    c: Coincident(g14,g11)
    c: Coincident(g14,g7)
    c: Vertical(g14)
    c: Coincident(g15,g11)
    c: Coincident(g15,g7)
    c: Vertical(g15)
    c: Coincident(g16,g0)
    c: Coincident(g16,g3)
    c: Vertical(g16)
    c: Coincident(g17,g4)
    c: Coincident(g17,g8)
    c: Vertical(g17)
    c: Coincident(g18,g0)
    c: Coincident(g18,g3)
    c: Vertical(g18)
    c: Coincident(g19,g4)
    c: Coincident(g19,g8)
    c: Vertical(g19)
    c: Coincident(g20,g5)
    c: Coincident(g20,g9)
    c: Vertical(g20)
    c: Coincident(g21,g5)
    c: Coincident(g21,g9)
    c: Vertical(g21)
    c: Coincident(g22,g10)
    c: Coincident(g22,g6)
    c: Vertical(g22)
    c: Coincident(g23,g6)
    c: Coincident(g23,g10)
    c: Vertical(g23)
FEATURE [Part::Extrusion] Extrude038  label="removeToCreateFanGrillHoles001"
  Base = -> Sketch047
  Dir = (0,-1,6e-16)
  DirMode = 2
  FaceMakerClass = Part::FaceMakerBullseye
  LengthFwd = 10
  LengthRev = 0
  Placement = pos=(65.4,44,54.82) rot=(0,0,1;0rad)
  Solid = true
  Symmetric = false
FEATURE [Part::Feature] Wire004
  shape: bbox 11 x 5.2 x 2e-07 mm, 0 faces, 0 solids (baked)
FEATURE [Part::Revolution] Revolve095
  Angle = 360
  Axis = (0,1,0)
  Base = (0,0,0)
  FaceMakerClass = Part::FaceMakerBullseye
  Placement = pos=(30.3,38,19.7) rot=(0,0,1;0rad)
  Solid = true
  Source = -> Wire004
  Symmetric = false
FEATURE [Part::Feature] Wire005
  shape: bbox 11 x 5.2 x 2e-07 mm, 0 faces, 0 solids (baked)
FEATURE [Part::Revolution] Revolve096
  Angle = 360
  Axis = (0,1,0)
  Base = (0,0,0)
  FaceMakerClass = Part::FaceMakerBullseye
  Placement = pos=(30.3,38,51.7) rot=(0,0,1;0rad)
  Solid = true
  Source = -> Wire005
  Symmetric = false
FEATURE [Part::Feature] Wire006
  shape: bbox 11 x 5.2 x 2e-07 mm, 0 faces, 0 solids (baked)
FEATURE [Part::Revolution] Revolve097
  Angle = 360
  Axis = (0,1,0)
  Base = (0,0,0)
  FaceMakerClass = Part::FaceMakerBullseye
  Placement = pos=(62.3,38,51.7) rot=(0,0,1;0rad)
  Solid = true
  Source = -> Wire006
  Symmetric = false
FEATURE [Part::Feature] Wire007
  shape: bbox 11 x 5.2 x 2e-07 mm, 0 faces, 0 solids (baked)
FEATURE [Part::Revolution] Revolve098
  Angle = 360
  Axis = (0,1,0)
  Base = (0,0,0)
  FaceMakerClass = Part::FaceMakerBullseye
  Placement = pos=(62.3,38,19.7) rot=(0,0,1;0rad)
  Solid = true
  Source = -> Wire007
  Symmetric = false
FEATURE [Part::MultiFuse] Fusion067  label="fanScrewHousing002"
  Shapes = -> [Revolve098,Revolve097,Revolve096,Revolve095]
FEATURE [Part::Feature] Face091 .. Face094  x4 (patterned run collapsed; names and placements below)
  shape: bbox 3.5 x 17.8 x 2e-07 mm, 1 faces, 0 solids (baked)
FEATURE [Part::Revolution] Revolve099  label="removeToCreateScrewAndThreadedInsertHole026"
  Angle = 360
  Axis = (0,1,0)
  Base = (0,0,0)
  FaceMakerClass = Part::FaceMakerBullseye
  Placement = pos=(62.3,30.3,19.7) rot=(0,0,1;0rad)
  Solid = false
  Source = -> Face091
  Symmetric = false
FEATURE [Part::Revolution] Revolve100  label="removeToCreateScrewAndThreadedInsertHole027"
  Angle = 360
  Axis = (0,1,0)
  Base = (0,0,0)
  FaceMakerClass = Part::FaceMakerBullseye
  Placement = pos=(62.3,30.3,51.7) rot=(0,0,1;0rad)
  Solid = false
  Source = -> Face092
  Symmetric = false
FEATURE [Part::Revolution] Revolve101  label="removeToCreateScrewAndThreadedInsertHole028"
  Angle = 360
  Axis = (0,1,0)
  Base = (0,0,0)
  FaceMakerClass = Part::FaceMakerBullseye
  Placement = pos=(30.3,30.3,19.7) rot=(0,0,1;0rad)
  Solid = false
  Source = -> Face093
  Symmetric = false
FEATURE [Part::Revolution] Revolve102  label="removeToCreateScrewAndThreadedInsertHole029"
  Angle = 360
  Axis = (0,1,0)
  Base = (0,0,0)
  FaceMakerClass = Part::FaceMakerBullseye
  Placement = pos=(30.3,30.3,51.7) rot=(0,0,1;0rad)
  Solid = false
  Source = -> Face094
  Symmetric = false
FEATURE [Part::MultiFuse] Fusion068  label="createThreadedInsertHolesForFan002"
  Shapes = -> [Revolve099,Revolve100,Revolve101,Revolve102]
FEATURE [Part::Cut] Cut026  label="fanScrewHousing003"
  Base = -> Fusion067
  Tool = -> Fusion068
FEATURE [Sketcher::SketchObject] Sketch048
  FullyConstrained = false
  Placement = pos=(0,0,0) rot=(1,0,0;1.5708rad)
  sketch-geometry (24):
    g0: ArcOfCircle CenterX=-4 CenterY=-10.5 CenterZ=0 NormalX=0 NormalY=0 NormalZ=1 AngleXU=0 Radius=1.5 StartAngle=6e-16 EndAngle=3.14159
    g1: ArcOfCircle CenterX=-34.2 CenterY=-10.5 CenterZ=0 NormalX=0 NormalY=0 NormalZ=1 AngleXU=0 Radius=1.5 StartAngle=0 EndAngle=3.14159
    g2: ArcOfCircle CenterX=-34.2 CenterY=-27.7 CenterZ=0 NormalX=0 NormalY=0 NormalZ=1 AngleXU=0 Radius=1.5 StartAngle=3.14159 EndAngle=6.28319
    g3: ArcOfCircle CenterX=-4 CenterY=-27.7 CenterZ=0 NormalX=0 NormalY=0 NormalZ=1 AngleXU=0 Radius=1.5 StartAngle=3.1416 EndAngle=6.28319
    g4: ArcOfCircle CenterX=-10 CenterY=-4.3 CenterZ=0 NormalX=0 NormalY=0 NormalZ=1 AngleXU=0 Radius=1.5 StartAngle=2e-16 EndAngle=3.14159
    g5: ArcOfCircle CenterX=-16.1 CenterY=-1.8 CenterZ=0 NormalX=0 NormalY=0 NormalZ=1 AngleXU=0 Radius=1.5 StartAngle=5e-16 EndAngle=3.14159
    g6: ArcOfCircle CenterX=-22.1 CenterY=-1.8 CenterZ=0 NormalX=0 NormalY=0 NormalZ=1 AngleXU=0 Radius=1.5 StartAngle=5e-16 EndAngle=3.14159
    g7: ArcOfCircle CenterX=-28.2 CenterY=-4.3 CenterZ=0 NormalX=0 NormalY=0 NormalZ=1 AngleXU=0 Radius=1.5 StartAngle=2e-16 EndAngle=3.14159
    g8: ArcOfCircle CenterX=-10 CenterY=-33.9 CenterZ=0 NormalX=0 NormalY=0 NormalZ=1 AngleXU=0 Radius=1.5 StartAngle=3.14159 EndAngle=6.28319
    g9: ArcOfCircle CenterX=-16.1 CenterY=-36.4 CenterZ=0 NormalX=0 NormalY=0 NormalZ=1 AngleXU=0 Radius=1.5 StartAngle=3.14159 EndAngle=6.28319
    g10: ArcOfCircle CenterX=-22.1 CenterY=-36.4 CenterZ=0 NormalX=0 NormalY=0 NormalZ=1 AngleXU=0 Radius=1.5 StartAngle=3.14159 EndAngle=6.28319
    g11: ArcOfCircle CenterX=-28.2 CenterY=-33.9 CenterZ=0 NormalX=0 NormalY=0 NormalZ=1 AngleXU=0 Radius=1.5 StartAngle=3.14159 EndAngle=6.28319
    g12: LineSegment StartX=-35.7 StartY=-10.5 StartZ=0 EndX=-35.7 EndY=-27.7 EndZ=0
    g13: LineSegment StartX=-32.7 StartY=-10.5 StartZ=0 EndX=-32.7 EndY=-27.7 EndZ=0
    g14: LineSegment StartX=-29.7 StartY=-33.9 StartZ=0 EndX=-29.7 EndY=-4.3 EndZ=0
    g15: LineSegment StartX=-26.7 StartY=-33.9 StartZ=0 EndX=-26.7 EndY=-4.3 EndZ=0
    g16: LineSegment StartX=-2.5 StartY=-10.5 StartZ=0 EndX=-2.5 EndY=-27.7 EndZ=0
    g17: LineSegment StartX=-8.5 StartY=-4.3 StartZ=0 EndX=-8.5 EndY=-33.9 EndZ=0
    g18: LineSegment StartX=-5.5 StartY=-10.5 StartZ=0 EndX=-5.5 EndY=-27.7 EndZ=0
    g19: LineSegment StartX=-11.5 StartY=-4.3 StartZ=0 EndX=-11.5 EndY=-33.9 EndZ=0
    g20: LineSegment StartX=-14.6 StartY=-1.8 StartZ=0 EndX=-14.6 EndY=-36.4 EndZ=0
    g21: LineSegment StartX=-17.6 StartY=-1.8 StartZ=0 EndX=-17.6 EndY=-36.4 EndZ=0
    g22: LineSegment StartX=-20.6 StartY=-36.4 StartZ=0 EndX=-20.6 EndY=-1.8 EndZ=0
    g23: LineSegment StartX=-23.6 StartY=-1.8 StartZ=0 EndX=-23.6 EndY=-36.4 EndZ=0
  constraints (48):
    c: Block(g0)
    c: Block(g1)
    c: Block(g2)
    c: Block(g3)
    c: Block(g4)
    c: Block(g5)
    c: Block(g6)
    c: Block(g7)
    c: Block(g8)
    c: Block(g9)
    c: Block(g10)
    c: Block(g11)
    c: Coincident(g12,g1)
    c: Coincident(g12,g2)
    c: Vertical(g12)
    c: Coincident(g13,g1)
    c: Coincident(g13,g2)
    c: Vertical(g13)
    c: Coincident(g14,g11)
    c: Coincident(g14,g7)
    c: Vertical(g14)
    c: Coincident(g15,g11)
    c: Coincident(g15,g7)
    c: Vertical(g15)
    c: Coincident(g16,g0)
    c: Coincident(g16,g3)
    c: Vertical(g16)
    c: Coincident(g17,g4)
    c: Coincident(g17,g8)
    c: Vertical(g17)
    c: Coincident(g18,g0)
    c: Coincident(g18,g3)
    c: Vertical(g18)
    c: Coincident(g19,g4)
    c: Coincident(g19,g8)
    c: Vertical(g19)
    c: Coincident(g20,g5)
    c: Coincident(g20,g9)
    c: Vertical(g20)
    c: Coincident(g21,g5)
    c: Coincident(g21,g9)
    c: Vertical(g21)
    c: Coincident(g22,g10)
    c: Coincident(g22,g6)
    c: Vertical(g22)
    c: Coincident(g23,g6)
    c: Coincident(g23,g10)
    c: Vertical(g23)
FEATURE [Part::Extrusion] Extrude039  label="removeToCreateFanGrillHoles002"
  Base = -> Sketch048
  Dir = (0,-1,6e-16)
  DirMode = 2
  FaceMakerClass = Part::FaceMakerBullseye
  LengthFwd = 10
  LengthRev = 0
  Placement = pos=(65.4,44,54.82) rot=(0,0,1;0rad)
  Solid = true
  Symmetric = false
FEATURE [Part::Cut] Cut027  label="fanScrewHousing004"
  Base = -> Cut026
  Tool = -> Extrude038
FEATURE [Part::Cut] Cut028  label="top014"
  Base = -> Fillet026
  Tool = -> Extrude039
FEATURE [Part::Feature] Face095 .. Face098  x4 (patterned run collapsed; names and placements below)
  shape: bbox 3.5 x 17.8 x 2e-07 mm, 1 faces, 0 solids (baked)
FEATURE [Part::Revolution] Revolve103  label="removeToCreateScrewAndThreadedInsertHole030"
  Angle = 360
  Axis = (0,1,0)
  Base = (0,0,0)
  FaceMakerClass = Part::FaceMakerBullseye
  Placement = pos=(62.3,30.3,19.7) rot=(0,0,1;0rad)
  Solid = false
  Source = -> Face095
  Symmetric = false
FEATURE [Part::Revolution] Revolve104  label="removeToCreateScrewAndThreadedInsertHole031"
  Angle = 360
  Axis = (0,1,0)
  Base = (0,0,0)
  FaceMakerClass = Part::FaceMakerBullseye
  Placement = pos=(62.3,30.3,51.7) rot=(0,0,1;0rad)
  Solid = false
  Source = -> Face096
  Symmetric = false
FEATURE [Part::Revolution] Revolve105  label="removeToCreateScrewAndThreadedInsertHole032"
  Angle = 360
  Axis = (0,1,0)
  Base = (0,0,0)
  FaceMakerClass = Part::FaceMakerBullseye
  Placement = pos=(30.3,30.3,19.7) rot=(0,0,1;0rad)
  Solid = false
  Source = -> Face097
  Symmetric = false
FEATURE [Part::Revolution] Revolve106  label="removeToCreateScrewAndThreadedInsertHole033"
  Angle = 360
  Axis = (0,1,0)
  Base = (0,0,0)
  FaceMakerClass = Part::FaceMakerBullseye
  Placement = pos=(30.3,30.3,51.7) rot=(0,0,1;0rad)
  Solid = false
  Source = -> Face098
  Symmetric = false
FEATURE [Part::MultiFuse] Fusion069  label="createThreadedInsertHolesForFan003"
  Shapes = -> [Revolve103,Revolve104,Revolve105,Revolve106]
FEATURE [Part::Cut] Cut029  label="top015"
  Base = -> Cut028
  Tool = -> Fusion054
FEATURE [Part::Cut] Cut030  label="fanScrewHousing005"
  Base = -> Cut027
  Tool = -> Fusion069
FEATURE [Part::Cylinder] Cylinder026  label="removeToCreteHoleForPlugHousing010"
  Angle = 360
  AttacherType = Attacher::AttachEngine3D
  Height = 20
  Placement = pos=(-2,19,36) rot=(0,1,0;1.5708rad)
  Radius = 14.3
FEATURE [Part::Box] Box018  label="removeToCreteHoleForPlugHousing011"
  AttacherType = Attacher::AttachEngine3D
  Height = 28.6
  Length = 10
  Placement = pos=(-2,0,21.7) rot=(0,0,1;0rad)
  Width = 19
FEATURE [Part::Box] Box019  label="wireHolderBottomCaseBit"
  AttacherType = Attacher::AttachEngine3D
  Height = 28
  Length = 3
  Placement = pos=(0,0,22) rot=(0,0,1;0rad)
  Width = 21
FEATURE [Part::Cylinder] Cylinder027  label="removeToCreteHoleForPlugHousing012"
  Angle = 360
  AttacherType = Attacher::AttachEngine3D
  Height = 20
  Placement = pos=(-2,19,36) rot=(0,1,0;1.5708rad)
  Radius = 14.3
FEATURE [Part::Cut] Cut031  label="wireHolderBottomCaseBit001"
  Base = -> Box019
  Tool = -> Cylinder027
FEATURE [Part::MultiFuse] Fusion070  label="removeToCreteHoleForPlugHousing013"
  Shapes = -> [Box018,Cylinder026]
FEATURE [Part::Cut] Cut032  label="top016"
  Base = -> Cut029
  Tool = -> Fusion070
FEATURE [Part::Cylinder] Cylinder028
  Angle = 360
  AttacherType = Attacher::AttachEngine3D
  Height = 20
  Placement = pos=(0,0,36.15) rot=(0,0,1;0rad)
  Radius = 14.3
FEATURE [Part::Cylinder] Cylinder029
  Angle = 360
  AttacherType = Attacher::AttachEngine3D
  Height = 10
  Placement = pos=(0,0,36.15) rot=(0,0,1;0rad)
  Radius = 4
FEATURE [Part::MultiFuse] Fusion071  label="removeToCreteHoleForPlugHousing014"
  Placement = pos=(70,19,36) rot=(0,1,0;1.5708rad)
  Shapes = -> [Cylinder028,Cylinder029]
FEATURE [Sketcher::SketchObject] Sketch049  label="topSketch011"
  FullyConstrained = true
  sketch-geometry (4):
    g0: ArcOfCircle CenterX=105 CenterY=19 CenterZ=0 NormalX=0 NormalY=0 NormalZ=1 AngleXU=0 Radius=20.6155 StartAngle=5.54125 EndAngle=6.28319
    g1: ArcOfCircle CenterX=105 CenterY=19 CenterZ=0 NormalX=0 NormalY=0 NormalZ=1 AngleXU=0 Radius=13 StartAngle=5.54125 EndAngle=6.28319
    g2: LineSegment StartX=118 StartY=19 StartZ=0 EndX=125.616 EndY=19 EndZ=0
    g3: LineSegment StartX=114.583 StartY=10.2157 StartZ=0 EndX=120.197 EndY=5.06982 EndZ=0
  constraints (7):
    c: Block(g0)
    c: Block(g1)
    c: Coincident(g2,g1)
    c: Coincident(g2,g0)
    c: Horizontal(g2)
    c: Coincident(g3,g1)
    c: Coincident(g3,g0)
FEATURE [Part::Box] Box020  label="removeToCreteHoleForPlugHousing015"
  AttacherType = Attacher::AttachEngine3D
  Height = 28.6
  Length = 20
  Placement = pos=(106.15,0,21.7) rot=(0,0,1;0rad)
  Width = 19
FEATURE [Part::MultiFuse] Fusion072  label="removeToCreteHoleForPlugHousing016"
  Shapes = -> [Box020,Fusion071]
FEATURE [Part::Cut] Cut033  label="removeToCreteHoleForPlugHousing017"
  Base = -> Cut032
  Tool = -> Fusion072
FEATURE [Part::Cylinder] Cylinder030
  Angle = 360
  AttacherType = Attacher::AttachEngine3D
  Height = 20
  Placement = pos=(0,0,36.15) rot=(0,0,1;0rad)
  Radius = 14.3
FEATURE [Part::Cylinder] Cylinder031
  Angle = 360
  AttacherType = Attacher::AttachEngine3D
  Height = 10
  Placement = pos=(0,0,36.15) rot=(0,0,1;0rad)
  Radius = 4
FEATURE [Part::Box] Box021  label="removeToCreteHoleForPlugHousing019"
  AttacherType = Attacher::AttachEngine3D
  Height = 28.6
  Length = 20
  Placement = pos=(106.15,0,21.7) rot=(0,0,1;0rad)
  Width = 19
FEATURE [Part::MultiFuse] Fusion074  label="removeToCreteHoleForPlugHousing020"
  Placement = pos=(70,19,36) rot=(0,1,0;1.5708rad)
  Shapes = -> [Cylinder030,Cylinder031]
FEATURE [Part::MultiFuse] Fusion073  label="removeToCreteHoleForPlugHousing018"
  Placement = pos=(0,0,28.3) rot=(0,0,1;0rad)
  Shapes = -> [Box021,Fusion074]
FEATURE [Part::Cylinder] Cylinder032
  Angle = 360
  AttacherType = Attacher::AttachEngine3D
  Height = 20
  Placement = pos=(0,0,36.15) rot=(0,0,1;0rad)
  Radius = 14.3
FEATURE [Part::Cylinder] Cylinder033
  Angle = 360
  AttacherType = Attacher::AttachEngine3D
  Height = 10
  Placement = pos=(0,0,36.15) rot=(0,0,1;0rad)
  Radius = 4
FEATURE [Part::Box] Box022  label="removeToCreteHoleForPlugHousing021"
  AttacherType = Attacher::AttachEngine3D
  Height = 28.6
  Length = 20
  Placement = pos=(106.15,0,21.7) rot=(0,0,1;0rad)
  Width = 19
FEATURE [Part::MultiFuse] Fusion076  label="removeToCreteHoleForPlugHousing023"
  Placement = pos=(70,19,36) rot=(0,1,0;1.5708rad)
  Shapes = -> [Cylinder032,Cylinder033]
FEATURE [Part::MultiFuse] Fusion075  label="removeToCreteHoleForPlugHousing022"
  Placement = pos=(0,0,-28.3) rot=(0,0,1;0rad)
  Shapes = -> [Box022,Fusion076]
FEATURE [Part::MultiFuse] Fusion077  label="removeToCreatePlugHousingBottomBit"
  Shapes = -> [Fusion075,Fusion073]
FEATURE [Part::Cylinder] Cylinder034
  Angle = 360
  AttacherType = Attacher::AttachEngine3D
  Height = 20
  Placement = pos=(0,0,36.15) rot=(0,0,1;0rad)
  Radius = 14
FEATURE [Part::Cylinder] Cylinder035
  Angle = 360
  AttacherType = Attacher::AttachEngine3D
  Height = 10
  Placement = pos=(0,0,36.15) rot=(0,0,1;0rad)
  Radius = 4
FEATURE [Part::MultiFuse] Fusion078  label="removeToCreteHoleForPlugHousing024"
  Placement = pos=(70,19,36) rot=(0,1,0;1.5708rad)
  Shapes = -> [Cylinder034,Cylinder035]
FEATURE [Part::MultiFuse] Fusion079  label="removeToCreatePlugHousingBottomBit001"
  Shapes = -> [Fusion078,Fusion077]
FEATURE [Part::Extrusion] Extrude040  label="bottomPlugHousingBit"
  Base = -> Sketch049
  Dir = (0,0,1)
  DirMode = 2
  FaceMakerClass = Part::FaceMakerBullseye
  LengthFwd = 72
  LengthRev = 0
  Solid = true
  Symmetric = false
FEATURE [Part::Cut] Cut034  label="bottomPlugHousingBit001"
  Base = -> Extrude040
  Placement = pos=(-0.09,0,0) rot=(0,0,1;0rad)
  Tool = -> Fusion079
FEATURE [Part::Box] Box023  label="Cube014"
  AttacherType = Attacher::AttachEngine3D
  Height = 16
  Length = 8
  Placement = pos=(12.7,31.52,28) rot=(0,0,1;0rad)
  Width = 4
FEATURE [Part::Cylinder] Cylinder036
  Angle = 360
  AttacherType = Attacher::AttachEngine3D
  Height = 10
  Placement = pos=(0,0,36.15) rot=(0,0,1;0rad)
  Radius = 4
FEATURE [Part::Cylinder] Cylinder037
  Angle = 360
  AttacherType = Attacher::AttachEngine3D
  Height = 20
  Placement = pos=(0,0,36.15) rot=(0,0,1;0rad)
  Radius = 8.2
FEATURE [Part::MultiFuse] Fusion080  label="removeToCreteHoleForPlugHousing025"
  Placement = pos=(-42,19,36) rot=(0,1,0;1.5708rad)
  Shapes = -> [Cylinder037,Cylinder036]
FEATURE [Sketcher::SketchObject] Sketch050  label="topSketch012"
  FullyConstrained = true
  sketch-geometry (4):
    g0: LineSegment StartX=16.8446 StartY=31.512 StartZ=0 EndX=16.3251 EndY=34.4666 EndZ=0
    g1: ArcOfCircle CenterX=19 CenterY=19.2524 CenterZ=0 NormalX=0 NormalY=0 NormalZ=1 AngleXU=0 Radius=15.4476 StartAngle=1.74483 EndAngle=2.72717
    g2: ArcOfCircle CenterX=19 CenterY=19.2524 CenterZ=0 NormalX=0 NormalY=0 NormalZ=1 AngleXU=0 Radius=12.4476 StartAngle=1.74483 EndAngle=2.73189
    g3: LineSegment StartX=4.86004 StartY=25.4725 StartZ=0 EndX=7.58253 EndY=24.2107 EndZ=0
  constraints (7):
    c: Block(g0)
    c: Coincident(g1,g0)
    c: Coincident(g2,g0)
    c: Coincident(g3,g1)
    c: Coincident(g3,g2)
    c: Block(g1)
    c: Block(g2)
FEATURE [Part::Extrusion] Extrude041
  Base = -> Sketch050
  Dir = (0,0,1)
  DirMode = 2
  FaceMakerClass = Part::FaceMakerBullseye
  LengthFwd = 10.6
  LengthRev = 0
  Placement = pos=(0,0,31) rot=(0,0,1;0rad)
  Solid = true
  Symmetric = false
FEATURE [Part::Cut] Cut035
  Base = -> Extrude041
  Placement = pos=(0,0,-0.3) rot=(0,0,1;0rad)
  Tool = -> Fusion080
FEATURE [Part::Cut] Cut036
  Base = -> Box023
  Tool = -> Cut035
FEATURE [Part::Fillet] Fillet027
  Base = -> Cut036
  Edges = 1 edges r=0.7: [Edge13]
FEATURE [Part::Fillet] Fillet028
  Base = -> Fillet027
  Edges = 1 edges r=0.7: [Edge13]
FEATURE [Part::Fillet] Fillet029
  Base = -> Fillet028
  Edges = 1 edges r=0.7: [Edge16]
FEATURE [Part::Fillet] Fillet030
  Base = -> Fillet029
  Edges = 1 edges r=0.7: [Edge11]
FEATURE [Part::Fillet] Fillet031
  Base = -> Fillet030
  Edges = 1 edges r=0.7: [Edge10]
FEATURE [Part::Fillet] Fillet032
  Base = -> Fillet031
  Edges = 1 edges r=1.2: [Edge5]
FEATURE [Part::Fillet] Fillet033
  Base = -> Fillet032
  Edges = 1 edges r=1.2: [Edge12]
FEATURE [Part::Fillet] Fillet034  label="wireHousingRetainer"
  Base = -> Fillet033
  Edges = 1 edges r=2: [Edge1]
  Placement = pos=(0.3,0,0) rot=(0,0,1;0rad)
FEATURE [Part::Feature] Face099
  shape: bbox 3.5 x 17.8 x 2e-07 mm, 1 faces, 0 solids (baked)
FEATURE [Part::Revolution] Revolve107  label="removeToCreateScrewAndThreadedInsertHole034"
  Angle = 360
  Axis = (0,1,0)
  Base = (0,0,0)
  FaceMakerClass = Part::FaceMakerBullseye
  Placement = pos=(12.5,0,10) rot=(0,0,1;0rad)
  Solid = false
  Source = -> Face099
  Symmetric = false
FEATURE [Part::Feature] Face100
  shape: bbox 3.5 x 17.8 x 2e-07 mm, 1 faces, 0 solids (baked)
FEATURE [Part::Revolution] Revolve108  label="removeToCreateScrewAndThreadedInsertHole035"
  Angle = 360
  Axis = (0,1,0)
  Base = (0,0,0)
  FaceMakerClass = Part::FaceMakerBullseye
  Placement = pos=(12.5,0,62) rot=(0,0,1;0rad)
  Solid = false
  Source = -> Face100
  Symmetric = false
FEATURE [Part::Feature] Face101
  shape: bbox 3.5 x 17.8 x 2e-07 mm, 1 faces, 0 solids (baked)
FEATURE [Part::Revolution] Revolve109  label="removeToCreateScrewAndThreadedInsertHole036"
  Angle = 360
  Axis = (0,1,0)
  Base = (0,0,0)
  FaceMakerClass = Part::FaceMakerBullseye
  Placement = pos=(89.5,0,68.5) rot=(0,0,1;0rad)
  Solid = false
  Source = -> Face101
  Symmetric = false
FEATURE [Part::Feature] Face102
  shape: bbox 3.5 x 17.8 x 2e-07 mm, 1 faces, 0 solids (baked)
FEATURE [Part::Revolution] Revolve110  label="removeToCreateScrewAndThreadedInsertHole037"
  Angle = 360
  Axis = (0,1,0)
  Base = (0,0,0)
  FaceMakerClass = Part::FaceMakerBullseye
  Placement = pos=(89.5,0,3.5) rot=(0,0,1;0rad)
  Solid = false
  Source = -> Face102
  Symmetric = false
FEATURE [Part::Feature] Face103
  shape: bbox 3.5 x 17.8 x 2e-07 mm, 1 faces, 0 solids (baked)
FEATURE [Part::Revolution] Revolve111  label="removeToCreateScrewAndThreadedInsertHole038"
  Angle = 360
  Axis = (0,1,0)
  Base = (0,0,0)
  FaceMakerClass = Part::FaceMakerBullseye
  Placement = pos=(109.5,4.7,3.5) rot=(0,0,1;0rad)
  Solid = false
  Source = -> Face103
  Symmetric = false
FEATURE [Part::Feature] Face104
  shape: bbox 3.5 x 17.8 x 2e-07 mm, 1 faces, 0 solids (baked)
FEATURE [Part::Revolution] Revolve112  label="removeToCreateScrewAndThreadedInsertHole039"
  Angle = 360
  Axis = (0,1,0)
  Base = (0,0,0)
  FaceMakerClass = Part::FaceMakerBullseye
  Placement = pos=(109.5,4.7,68.5) rot=(0,0,1;0rad)
  Solid = false
  Source = -> Face104
  Symmetric = false
FEATURE [Part::MultiFuse] Fusion081  label="removeToCreateScrewAndThreadedInsertHole040"
  Shapes = -> [Revolve107,Revolve108,Revolve109,Revolve110,Revolve111,Revolve112]
FEATURE [Part::MultiFuse] Fusion082  label="casePillars002"
  Shapes = -> [Revolve094,Revolve092,Revolve090,Revolve089,Revolve091,Revolve093]
FEATURE [Part::Cut] Cut037  label="casePillars003"
  Base = -> Fusion082
  Tool = -> Fusion081
FEATURE [Sketcher::SketchObject] Sketch051
  FullyConstrained = true
  Placement = pos=(117,19,0) rot=(0.57735,0.57735,0.57735;2.0944rad)
  sketch-geometry (48):
    g0: LineSegment StartX=-49.19 StartY=69.25 StartZ=0 EndX=-49.19 EndY=66.25 EndZ=0
    g1: LineSegment StartX=-49.19 StartY=63.5 StartZ=0 EndX=-49.19 EndY=60.5 EndZ=0
    g2: LineSegment StartX=-49.19 StartY=57.75 StartZ=0 EndX=-49.19 EndY=54.75 EndZ=0
    g3: LineSegment StartX=-49.19 StartY=52 StartZ=0 EndX=-49.19 EndY=49 EndZ=0
    g4: LineSegment StartX=-49.19 StartY=46.25 StartZ=0 EndX=-49.19 EndY=43.25 EndZ=0
    g5: LineSegment StartX=-49.19 StartY=40.5 StartZ=0 EndX=-49.19 EndY=37.5 EndZ=0
    g6: LineSegment StartX=-49.19 StartY=34.5 StartZ=0 EndX=-49.19 EndY=31.5 EndZ=0
    g7: LineSegment StartX=-49.19 StartY=28.75 StartZ=0 EndX=-49.19 EndY=25.75 EndZ=0
    g8: LineSegment StartX=-49.19 StartY=23 StartZ=0 EndX=-49.19 EndY=20 EndZ=0
    g9: LineSegment StartX=-49.19 StartY=17.25 StartZ=0 EndX=-49.19 EndY=14.25 EndZ=0
    g10: LineSegment StartX=-49.19 StartY=11.5 StartZ=0 EndX=-49.19 EndY=8.5 EndZ=0
    g11: LineSegment StartX=-49.19 StartY=5.75 StartZ=0 EndX=-49.19 EndY=2.75 EndZ=0
    g12: ArcOfCircle CenterX=-1.5 CenterY=67.75 CenterZ=0 NormalX=0 NormalY=0 NormalZ=1 AngleXU=0 Radius=1.5 StartAngle=4.71239 EndAngle=7.85398
    g13: ArcOfCircle CenterX=-1.5 CenterY=62 CenterZ=0 NormalX=0 NormalY=0 NormalZ=1 AngleXU=0 Radius=1.5 StartAngle=4.71239 EndAngle=7.85398
    g14: ArcOfCircle CenterX=-1.5 CenterY=56.25 CenterZ=0 NormalX=0 NormalY=0 NormalZ=1 AngleXU=0 Radius=1.5 StartAngle=4.71239 EndAngle=7.85398
    g15: ArcOfCircle CenterX=-11.49 CenterY=50.5 CenterZ=0 NormalX=0 NormalY=0 NormalZ=1 AngleXU=0 Radius=1.5 StartAngle=4.71239 EndAngle=7.85398
    g16: ArcOfCircle CenterX=-16.28 CenterY=44.75 CenterZ=0 NormalX=0 NormalY=0 NormalZ=1 AngleXU=0 Radius=1.5 StartAngle=4.71239 EndAngle=7.85398
    g17: ArcOfCircle CenterX=-18.2337 CenterY=39 CenterZ=0 NormalX=0 NormalY=0 NormalZ=1 AngleXU=0 Radius=1.5 StartAngle=4.71485 EndAngle=7.85398
    g18: ArcOfCircle CenterX=-16.2837 CenterY=27.25 CenterZ=0 NormalX=0 NormalY=0 NormalZ=1 AngleXU=0 Radius=1.5 StartAngle=4.71485 EndAngle=7.85398
    g19: ArcOfCircle CenterX=-18.2337 CenterY=33 CenterZ=0 NormalX=0 NormalY=0 NormalZ=1 AngleXU=0 Radius=1.5 StartAngle=4.71485 EndAngle=7.85398
    g20: ArcOfCircle CenterX=-11.49 CenterY=21.5 CenterZ=0 NormalX=0 NormalY=0 NormalZ=1 AngleXU=0 Radius=1.5 StartAngle=4.71239 EndAngle=7.85398
    g21: ArcOfCircle CenterX=-1.5 CenterY=4.25 CenterZ=0 NormalX=0 NormalY=0 NormalZ=1 AngleXU=0 Radius=1.5 StartAngle=4.71239 EndAngle=7.85398
    g22: ArcOfCircle CenterX=-1.5 CenterY=10 CenterZ=0 NormalX=0 NormalY=0 NormalZ=1 AngleXU=0 Radius=1.5 StartAngle=4.71239 EndAngle=7.85398
    g23: ArcOfCircle CenterX=-1.5 CenterY=15.75 CenterZ=0 NormalX=0 NormalY=0 NormalZ=1 AngleXU=0 Radius=1.5 StartAngle=4.71239 EndAngle=7.85398
    g24: LineSegment StartX=-49.19 StartY=69.25 StartZ=0 EndX=-1.5 EndY=69.25 EndZ=0
    g25: LineSegment StartX=-49.19 StartY=66.25 StartZ=0 EndX=-1.5 EndY=66.25 EndZ=0
    g26: LineSegment StartX=-49.19 StartY=63.5 StartZ=0 EndX=-1.5 EndY=63.5 EndZ=0
    g27: LineSegment StartX=-49.19 StartY=60.5 StartZ=0 EndX=-1.5 EndY=60.5 EndZ=0
    g28: LineSegment StartX=-49.19 StartY=57.75 StartZ=0 EndX=-1.5 EndY=57.75 EndZ=0
    g29: LineSegment StartX=-49.19 StartY=54.75 StartZ=0 EndX=-1.5 EndY=54.75 EndZ=0
    g30: LineSegment StartX=-49.19 StartY=52 StartZ=0 EndX=-11.49 EndY=52 EndZ=0
    g31: LineSegment StartX=-49.19 StartY=49 StartZ=0 EndX=-11.49 EndY=49 EndZ=0
    g32: LineSegment StartX=-49.19 StartY=46.25 StartZ=0 EndX=-16.28 EndY=46.25 EndZ=0
    g33: LineSegment StartX=-49.19 StartY=43.25 StartZ=0 EndX=-16.28 EndY=43.25 EndZ=0
    g34: LineSegment StartX=-49.19 StartY=40.5 StartZ=0 EndX=-18.2337 EndY=40.5 EndZ=0
    g35: LineSegment StartX=-49.19 StartY=37.5 StartZ=0 EndX=-18.23 EndY=37.5 EndZ=0
    g36: LineSegment StartX=-49.19 StartY=34.5 StartZ=0 EndX=-18.2337 EndY=34.5 EndZ=0
    g37: LineSegment StartX=-49.19 StartY=31.5 StartZ=0 EndX=-18.23 EndY=31.5 EndZ=0
    g38: LineSegment StartX=-49.19 StartY=28.75 StartZ=0 EndX=-16.2837 EndY=28.75 EndZ=0
    g39: LineSegment StartX=-49.19 StartY=25.75 StartZ=0 EndX=-16.28 EndY=25.75 EndZ=0
    g40: LineSegment StartX=-49.19 StartY=23 StartZ=0 EndX=-11.49 EndY=23 EndZ=0
    g41: LineSegment StartX=-49.19 StartY=20 StartZ=0 EndX=-11.49 EndY=20 EndZ=0
    g42: LineSegment StartX=-49.19 StartY=17.25 StartZ=0 EndX=-1.5 EndY=17.25 EndZ=0
    g43: LineSegment StartX=-49.19 StartY=14.25 StartZ=0 EndX=-1.5 EndY=14.25 EndZ=0
    g44: LineSegment StartX=-49.19 StartY=11.5 StartZ=0 EndX=-1.5 EndY=11.5 EndZ=0
    g45: LineSegment StartX=-49.19 StartY=8.5 StartZ=0 EndX=-1.5 EndY=8.5 EndZ=0
    g46: LineSegment StartX=-49.19 StartY=5.75 StartZ=0 EndX=-1.5 EndY=5.75 EndZ=0
    g47: LineSegment StartX=-49.19 StartY=2.75 StartZ=0 EndX=-1.5 EndY=2.75 EndZ=0
  constraints (120):
    c: Vertical(g0)
    c: Distance(g0) = 3
    c: Block(g0)
    c: Vertical(g1)
    c: Distance(g1) = 3
    c: Vertical(g2)
    c: Equal(g0,g2) = 3
    c: Block(g2)
    c: Vertical(g3)
    c: Equal(g1,g3) = 3
    c: Vertical(g4)
    c: Equal(g0,g4) = 3
    c: Block(g4)
    c: Vertical(g5)
    c: Equal(g1,g5) = 3
    c: Vertical(g6)
    c: Equal(g0,g6) = 3
    c: Block(g6)
    c: Vertical(g7)
    c: Equal(g1,g7) = 3
    c: Vertical(g8)
    c: Equal(g0,g8) = 3
    c: Block(g8)
    c: Vertical(g9)
    c: Equal(g1,g9) = 3
    c: Vertical(g10)
    c: Equal(g0,g10) = 3
    c: Block(g10)
    c: Vertical(g11)
    c: Equal(g1,g11) = 3
    c: Block(g12)
    c: Block(g13)
    c: Block(g14)
    c: Block(g15)
    c: Block(g16)
    c: Block(g17)
    c: Block(g18)
    c: Block(g19)
    c: Block(g20)
    c: Block(g21)
    c: Block(g22)
    c: Block(g23)
    c: Block(g11)
    c: Block(g9)
    c: Block(g7)
    c: Block(g5)
    c: Block(g3)
    c: Block(g1)
    c: Coincident(g24,g0)
    c: Coincident(g24,g12)
    c: Horizontal(g24)
    c: Coincident(g25,g0)
    c: Coincident(g25,g12)
    c: Horizontal(g25)
    c: Coincident(g26,g1)
    c: Coincident(g26,g13)
    c: Horizontal(g26)
    c: Coincident(g27,g1)
    c: Coincident(g27,g13)
    c: Horizontal(g27)
    c: Coincident(g28,g2)
    c: Coincident(g28,g14)
    c: Horizontal(g28)
    c: Coincident(g29,g2)
    c: Coincident(g29,g14)
    c: Horizontal(g29)
    c: Coincident(g30,g3)
    c: Coincident(g30,g15)
    c: Horizontal(g30)
    c: Coincident(g31,g3)
    c: Coincident(g31,g15)
    c: Horizontal(g31)
    c: Coincident(g32,g4)
    c: Coincident(g32,g16)
    c: Horizontal(g32)
    c: Coincident(g33,g4)
    c: Coincident(g33,g16)
    c: Horizontal(g33)
    c: Coincident(g34,g5)
    c: Coincident(g34,g17)
    c: Horizontal(g34)
    c: Coincident(g35,g5)
    c: Coincident(g35,g17)
    c: Horizontal(g35)
    c: Coincident(g36,g6)
    c: Coincident(g36,g19)
    c: Horizontal(g36)
    c: Coincident(g37,g6)
    c: Coincident(g37,g19)
    c: Horizontal(g37)
    c: Coincident(g38,g7)
    c: Coincident(g38,g18)
    c: Horizontal(g38)
    c: Coincident(g39,g7)
    c: Coincident(g39,g18)
    c: Horizontal(g39)
    c: Coincident(g40,g8)
    c: Coincident(g40,g20)
    c: Horizontal(g40)
    c: Coincident(g41,g8)
    c: Coincident(g41,g20)
    c: Horizontal(g41)
    c: Coincident(g42,g9)
    c: Coincident(g42,g23)
    c: Horizontal(g42)
    c: Coincident(g43,g9)
    c: Coincident(g43,g23)
    c: Horizontal(g43)
    c: Coincident(g44,g10)
    c: Coincident(g44,g22)
    c: Horizontal(g44)
    c: Coincident(g45,g10)
    c: Coincident(g45,g22)
    c: Horizontal(g45)
    c: Coincident(g46,g11)
    c: Coincident(g46,g21)
    c: Horizontal(g46)
    c: Coincident(g47,g11)
    c: Coincident(g47,g21)
    c: Horizontal(g47)
FEATURE [Part::Extrusion] Extrude042
  Base = -> Sketch051
  Dir = (1,-2e-16,2e-16)
  DirMode = 2
  FaceMakerClass = Part::FaceMakerBullseye
  LengthFwd = 19
  LengthRev = 0
  Placement = pos=(-19,0,0) rot=(0,0,1;0rad)
  Solid = true
  Symmetric = false
FEATURE [Part::Fillet] Fillet035  label="removeToCreateVentalationHoles"
  Base = -> Extrude042
  Edges = <same value as first occurrence — deduplicated (x6 in doc)>
  Placement = pos=(7,0,0) rot=(0,0,1;0rad)
FEATURE [Part::Cut] Cut038  label="top017"
  Base = -> Cut033
  Tool = -> Fillet035
FEATURE [Sketcher::SketchObject] Sketch052  label="bottomSketch001"
  FullyConstrained = true
  sketch-geometry (45):
    g0: LineSegment StartX=6.29999 StartY=8 StartZ=0 EndX=3.29999 EndY=8 EndZ=0
    g1: LineSegment StartX=3.29999 StartY=8 StartZ=0 EndX=3.29999 EndY=-6.03275e-07 EndZ=0
    g2: ArcOfCircle CenterX=8.29999 CenterY=5 CenterZ=0 NormalX=0 NormalY=0 NormalZ=1 AngleXU=0 Radius=2 StartAngle=3.14159 EndAngle=4.71239
    g3: LineSegment StartX=6.29999 StartY=8 StartZ=0 EndX=6.29999 EndY=5 EndZ=0
    g4: ArcOfCircle CenterX=105 CenterY=19 CenterZ=0 NormalX=0 NormalY=0 NormalZ=1 AngleXU=0 Radius=12.7 StartAngle=4.71239 EndAngle=5.94289
    g5-g11: Circle x7 (B-spline internal-alignment scaffolding for g12; pole/knot coordinates omitted)
    g12: BSplineCurve PolesCount=7 KnotsCount=5 Degree=3 IsPeriodic=0
    g13-g17: GeomPoint x5 (B-spline internal-alignment scaffolding for g12; pole/knot coordinates omitted)
    g18: ArcOfCircle CenterX=105 CenterY=19 CenterZ=0 NormalX=0 NormalY=0 NormalZ=1 AngleXU=0 Radius=15.7 StartAngle=5.81226 EndAngle=6.28319
    g19: BSplineCurve PolesCount=5 KnotsCount=3 Degree=3 IsPeriodic=0
    g20: LineSegment StartX=8.29999 StartY=3 StartZ=0 EndX=101.7 EndY=3 EndZ=0
    g21: LineSegment StartX=3.29999 StartY=-6.03275e-07 StartZ=0 EndX=105 EndY=-6.03275e-07 EndZ=0
    g22: LineSegment StartX=120.974 StartY=8.71251 StartZ=0 EndX=122.332 EndY=7.83778 EndZ=0
    g23: LineSegment StartX=105 StartY=-6.03274e-07 StartZ=0 EndX=113 EndY=-6.03274e-07 EndZ=0
    g24: ArcOfCircle CenterX=105 CenterY=19 CenterZ=0 NormalX=0 NormalY=0 NormalZ=1 AngleXU=0 Radius=20.6155 StartAngle=5.11091 EndAngle=5.71103
    g25: ArcOfCircle CenterX=117.7 CenterY=19 CenterZ=0 NormalX=0 NormalY=0 NormalZ=1 AngleXU=0 Radius=3 StartAngle=1.2e-15 EndAngle=2.10468
    g26: Circle CenterX=116.345 CenterY=16.3232 CenterZ=0 NormalX=0 NormalY=0 NormalZ=1 AngleXU=0 Radius=1
    g27: Circle CenterX=117.24 CenterY=15.7584 CenterZ=0 NormalX=0 NormalY=0 NormalZ=1 AngleXU=0 Radius=1
    g28: Circle CenterX=116.972 CenterY=14.7612 CenterZ=0 NormalX=0 NormalY=0 NormalZ=1 AngleXU=0 Radius=1
    g29: BSplineCurve PolesCount=3 KnotsCount=2 Degree=2 IsPeriodic=0
    g30: GeomPoint X=116.345 Y=16.3232 Z=0
    g31: GeomPoint X=116.972 Y=14.7612 Z=0
    g32: Circle CenterX=115.828 CenterY=17.157 CenterZ=0 NormalX=0 NormalY=0 NormalZ=1 AngleXU=0 Radius=1
    g33: Circle CenterX=115.841 CenterY=16.639 CenterZ=0 NormalX=0 NormalY=0 NormalZ=1 AngleXU=0 Radius=1
    g34: Circle CenterX=116.345 CenterY=16.3232 CenterZ=0 NormalX=0 NormalY=0 NormalZ=1 AngleXU=0 Radius=1
    g35: BSplineCurve PolesCount=3 KnotsCount=2 Degree=2 IsPeriodic=0
    g36: GeomPoint X=115.828 Y=17.157 Z=0
    g37: GeomPoint X=116.345 Y=16.3232 Z=0
    g38: LineSegment StartX=115.828 StartY=17.157 StartZ=0 EndX=115.828 EndY=20.8307 EndZ=0
    g39: Circle CenterX=115.828 CenterY=20.8307 CenterZ=0 NormalX=0 NormalY=0 NormalZ=1 AngleXU=0 Radius=1
    g40: Circle CenterX=115.831 CenterY=21.3396 CenterZ=0 NormalX=0 NormalY=0 NormalZ=1 AngleXU=0 Radius=1
    g41: Circle CenterX=116.173 CenterY=21.5825 CenterZ=0 NormalX=0 NormalY=0 NormalZ=1 AngleXU=0 Radius=1
    g42: BSplineCurve PolesCount=3 KnotsCount=2 Degree=2 IsPeriodic=0
    g43: GeomPoint X=115.828 Y=20.8307 Z=0
    g44: GeomPoint X=116.173 Y=21.5825 Z=0
  constraints (70):
    c: Horizontal(g0)
    c: Distance(g0) = 3
    c: Coincident(g1,g0)
    c: Vertical(g1)
    c: Block(g2)
    c: Block(g0)
    c: Coincident(g3,g0)
    c: Coincident(g3,g2)
    c: Vertical(g3)
    c: Block(g1)
    c: Block(g4)
    c: Coincident(g19,g4)
    c: Block(g19)
    c: Equal(g5, g6-g11) x6
    c: InternalAlignment(g5-g11 -> g12) x7
    c: InternalAlignment(g13-g17 -> g12) x5
    c: Block(g12)
    c: Coincident(g18,g12)
    c: Block(g18)
    c: Coincident(g20,g2)
    c: Coincident(g20,g19)
    c: Horizontal(g20)
    c: Distance(g20) = 93.4
    c: Coincident(g21,g1)
    c: Horizontal(g21)
    c: Distance(g21) = 101.7
    c: Horizontal(g23)
    c: Distance(g23) = 8
    c: Coincident(g24,g23)
    c: Block(g23)
    c: Coincident(g22,g24)
    c: Block(g24)
    c: Block(g22)
    c: Distance(g22) = 1.61553
    c: Coincident(g25,g18)
    c: Block(g25)
    c: Weight(g26) = 1
    c: Equal(g26,g27)
    c: Equal(g26,g28)
    c: Coincident(g29,g4)
    c: InternalAlignment(g26,g29)
    c: InternalAlignment(g27,g29)
    c: InternalAlignment(g28,g29)
    c: InternalAlignment(g30,g29)
    c: InternalAlignment(g31,g29)
    c: Block(g29)
    c: Weight(g32) = 1
    c: Equal(g32,g33)
    c: Equal(g32,g34)
    c: Coincident(g35,g29)
    c: InternalAlignment(g32,g35)
    c: InternalAlignment(g33,g35)
    c: InternalAlignment(g34,g35)
    c: InternalAlignment(g36,g35)
    c: InternalAlignment(g37,g35)
    c: Block(g35)
    c: Coincident(g38,g35)
    c: Vertical(g38)
    c: Block(g38)
    c: Coincident(g42,g38)
    c: Weight(g39) = 1
    c: Equal(g39,g40)
    c: Equal(g39,g41)
    c: Coincident(g42,g25)
    c: InternalAlignment(g39,g42)
    c: InternalAlignment(g40,g42)
    c: InternalAlignment(g41,g42)
    c: InternalAlignment(g43,g42)
    c: InternalAlignment(g44,g42)
    c: Block(g42)
FEATURE [Part::Extrusion] Extrude043  label="bottom010"
  Base = -> Sketch052
  Dir = (0,0,1)
  DirMode = 2
  FaceMakerClass = Part::FaceMakerBullseye
  LengthFwd = 71.4
  LengthRev = 0
  Placement = pos=(0,0,0.3) rot=(0,0,1;0rad)
  Solid = true
  Symmetric = false
FEATURE [Sketcher::SketchObject] Sketch053  label="topSketch013"
  FullyConstrained = true
  sketch-geometry (22):
    g0: LineSegment StartX=5.21097e-06 StartY=3 StartZ=0 EndX=5.21097e-06 EndY=19 EndZ=0
    g1: ArcOfCircle CenterX=19 CenterY=19 CenterZ=0 NormalX=0 NormalY=0 NormalZ=1 AngleXU=0 Radius=19 StartAngle=1.5708 EndAngle=3.14159
    g2: ArcOfCircle CenterX=19 CenterY=19 CenterZ=0 NormalX=0 NormalY=0 NormalZ=1 AngleXU=0 Radius=16 StartAngle=1.5708 EndAngle=3.14159
    g3: LineSegment StartX=114 StartY=35 StartZ=0 EndX=19 EndY=35 EndZ=0
    g4: LineSegment StartX=5.21097e-06 StartY=3 StartZ=0 EndX=5.21097e-06 EndY=0 EndZ=0
    g5: LineSegment StartX=3 StartY=0 StartZ=0 EndX=5.21097e-06 EndY=0 EndZ=0
    g6: LineSegment StartX=3 StartY=19 StartZ=0 EndX=3 EndY=0 EndZ=0
    g7: LineSegment StartX=19 StartY=38 StartZ=0 EndX=124 EndY=38 EndZ=0
    g8: Circle CenterX=119 CenterY=35 CenterZ=0 NormalX=0 NormalY=0 NormalZ=1 AngleXU=0 Radius=1
    g9: Circle CenterX=121 CenterY=35 CenterZ=0 NormalX=0 NormalY=0 NormalZ=1 AngleXU=0 Radius=1
    g10: Circle CenterX=121 CenterY=33 CenterZ=0 NormalX=0 NormalY=0 NormalZ=1 AngleXU=0 Radius=1
    g11: BSplineCurve PolesCount=3 KnotsCount=2 Degree=2 IsPeriodic=0
    g12: GeomPoint X=119 Y=35 Z=0
    g13: GeomPoint X=121 Y=33 Z=0
    g14: LineSegment StartX=119 StartY=35 StartZ=0 EndX=114 EndY=35 EndZ=0
    g15: ArcOfCircle CenterX=105 CenterY=19 CenterZ=0 NormalX=0 NormalY=0 NormalZ=1 AngleXU=0 Radius=16 StartAngle=5.60905 EndAngle=6.28319
    g16: LineSegment StartX=121 StartY=33 StartZ=0 EndX=121 EndY=19 EndZ=0
    g17: LineSegment StartX=117.5 StartY=9.01251 StartZ=0 EndX=121.163 EndY=9.0125 EndZ=0
    g18: ArcOfCircle CenterX=105 CenterY=19 CenterZ=0 NormalX=0 NormalY=0 NormalZ=1 AngleXU=0 Radius=20.6155 StartAngle=5.7297 EndAngle=6.28319
    g19: LineSegment StartX=121.163 StartY=9.0125 StartZ=0 EndX=122.538 EndY=8.16329 EndZ=0
    g20: LineSegment StartX=124 StartY=38 StartZ=0 EndX=125.616 EndY=38 EndZ=0
    g21: LineSegment StartX=125.616 StartY=19 StartZ=0 EndX=125.616 EndY=38 EndZ=0
  constraints (50):
    c: Vertical(g0)
    c: Block(g0)
    c: Coincident(g1,g0)
    c: Block(g1)
    c: Coincident(g2,g1)
    c: Block(g2)
    c: Coincident(g3,g2)
    c: Horizontal(g3)
    c: Tangent(g3,g2)
    c: Coincident(g4,g0)
    c: Distance(g4) = 3
    c: Vertical(g4)
    c: Coincident(g5,g4)
    c: Horizontal(g5)
    c: Coincident(g6,g2)
    c: Coincident(g6,g5)
    c: Vertical(g6)
    c: Horizontal(g7)
    c: Distance(g7) = 105
    c: Coincident(g7,g1)
    c: Block(g3)
    c: Weight(g8) = 1
    c: Equal(g8,g9)
    c: Equal(g8,g10)
    c: InternalAlignment(g8,g11)
    c: InternalAlignment(g9,g11)
    c: InternalAlignment(g10,g11)
    c: InternalAlignment(g12,g11)
    c: InternalAlignment(g13,g11)
    c: Block(g11)
    c: Coincident(g14,g11)
    c: Coincident(g14,g3)
    c: Horizontal(g14)
    c: Block(g15)
    c: Coincident(g16,g11)
    c: Coincident(g16,g15)
    c: Vertical(g16)
    c: Distance(g16) = 14
    c: Coincident(g17,g15)
    c: Block(g18)
    c: Coincident(g19,g18)
    c: Coincident(g20,g7)
    c: Horizontal(g20)
    c: Vertical(g21)
    c: Coincident(g20,g21)
    c: Block(g20)
    c: Block(g21)
    c: Block(g19)
    c: Block(g17)
    c: Distance(g20) = 1.61553
FEATURE [Part::Extrusion] Extrude044
  Base = -> Sketch053
  Dir = (0,0,1)
  DirMode = 2
  FaceMakerClass = Part::FaceMakerBullseye
  LengthFwd = 72
  LengthRev = 0
  Solid = true
  Symmetric = false
FEATURE [Part::Fillet] Fillet036  label="top018"
  Base = -> Extrude044
  Edges = 1 edges r=2: [Edge41]
FEATURE [Sketcher::SketchObject] Sketch054
  FullyConstrained = false
  Placement = pos=(0,0,0) rot=(1,0,0;1.5708rad)
  sketch-geometry (24):
    g0: ArcOfCircle CenterX=-4 CenterY=-10.5 CenterZ=0 NormalX=0 NormalY=0 NormalZ=1 AngleXU=0 Radius=1.5 StartAngle=6e-16 EndAngle=3.14159
    g1: ArcOfCircle CenterX=-34.2 CenterY=-10.5 CenterZ=0 NormalX=0 NormalY=0 NormalZ=1 AngleXU=0 Radius=1.5 StartAngle=0 EndAngle=3.14159
    g2: ArcOfCircle CenterX=-34.2 CenterY=-27.7 CenterZ=0 NormalX=0 NormalY=0 NormalZ=1 AngleXU=0 Radius=1.5 StartAngle=3.14159 EndAngle=6.28319
    g3: ArcOfCircle CenterX=-4 CenterY=-27.7 CenterZ=0 NormalX=0 NormalY=0 NormalZ=1 AngleXU=0 Radius=1.5 StartAngle=3.1416 EndAngle=6.28319
    g4: ArcOfCircle CenterX=-10 CenterY=-4.3 CenterZ=0 NormalX=0 NormalY=0 NormalZ=1 AngleXU=0 Radius=1.5 StartAngle=2e-16 EndAngle=3.14159
    g5: ArcOfCircle CenterX=-16.1 CenterY=-1.8 CenterZ=0 NormalX=0 NormalY=0 NormalZ=1 AngleXU=0 Radius=1.5 StartAngle=5e-16 EndAngle=3.14159
    g6: ArcOfCircle CenterX=-22.1 CenterY=-1.8 CenterZ=0 NormalX=0 NormalY=0 NormalZ=1 AngleXU=0 Radius=1.5 StartAngle=5e-16 EndAngle=3.14159
    g7: ArcOfCircle CenterX=-28.2 CenterY=-4.3 CenterZ=0 NormalX=0 NormalY=0 NormalZ=1 AngleXU=0 Radius=1.5 StartAngle=2e-16 EndAngle=3.14159
    g8: ArcOfCircle CenterX=-10 CenterY=-33.9 CenterZ=0 NormalX=0 NormalY=0 NormalZ=1 AngleXU=0 Radius=1.5 StartAngle=3.14159 EndAngle=6.28319
    g9: ArcOfCircle CenterX=-16.1 CenterY=-36.4 CenterZ=0 NormalX=0 NormalY=0 NormalZ=1 AngleXU=0 Radius=1.5 StartAngle=3.14159 EndAngle=6.28319
    g10: ArcOfCircle CenterX=-22.1 CenterY=-36.4 CenterZ=0 NormalX=0 NormalY=0 NormalZ=1 AngleXU=0 Radius=1.5 StartAngle=3.14159 EndAngle=6.28319
    g11: ArcOfCircle CenterX=-28.2 CenterY=-33.9 CenterZ=0 NormalX=0 NormalY=0 NormalZ=1 AngleXU=0 Radius=1.5 StartAngle=3.14159 EndAngle=6.28319
    g12: LineSegment StartX=-35.7 StartY=-10.5 StartZ=0 EndX=-35.7 EndY=-27.7 EndZ=0
    g13: LineSegment StartX=-32.7 StartY=-10.5 StartZ=0 EndX=-32.7 EndY=-27.7 EndZ=0
    g14: LineSegment StartX=-29.7 StartY=-33.9 StartZ=0 EndX=-29.7 EndY=-4.3 EndZ=0
    g15: LineSegment StartX=-26.7 StartY=-33.9 StartZ=0 EndX=-26.7 EndY=-4.3 EndZ=0
    g16: LineSegment StartX=-2.5 StartY=-10.5 StartZ=0 EndX=-2.5 EndY=-27.7 EndZ=0
    g17: LineSegment StartX=-8.5 StartY=-4.3 StartZ=0 EndX=-8.5 EndY=-33.9 EndZ=0
    g18: LineSegment StartX=-5.5 StartY=-10.5 StartZ=0 EndX=-5.5 EndY=-27.7 EndZ=0
    g19: LineSegment StartX=-11.5 StartY=-4.3 StartZ=0 EndX=-11.5 EndY=-33.9 EndZ=0
    g20: LineSegment StartX=-14.6 StartY=-1.8 StartZ=0 EndX=-14.6 EndY=-36.4 EndZ=0
    g21: LineSegment StartX=-17.6 StartY=-1.8 StartZ=0 EndX=-17.6 EndY=-36.4 EndZ=0
    g22: LineSegment StartX=-20.6 StartY=-36.4 StartZ=0 EndX=-20.6 EndY=-1.8 EndZ=0
    g23: LineSegment StartX=-23.6 StartY=-1.8 StartZ=0 EndX=-23.6 EndY=-36.4 EndZ=0
  constraints (48):
    c: Block(g0)
    c: Block(g1)
    c: Block(g2)
    c: Block(g3)
    c: Block(g4)
    c: Block(g5)
    c: Block(g6)
    c: Block(g7)
    c: Block(g8)
    c: Block(g9)
    c: Block(g10)
    c: Block(g11)
    c: Coincident(g12,g1)
    c: Coincident(g12,g2)
    c: Vertical(g12)
    c: Coincident(g13,g1)
    c: Coincident(g13,g2)
    c: Vertical(g13)
    c: Coincident(g14,g11)
    c: Coincident(g14,g7)
    c: Vertical(g14)
    c: Coincident(g15,g11)
    c: Coincident(g15,g7)
    c: Vertical(g15)
    c: Coincident(g16,g0)
    c: Coincident(g16,g3)
    c: Vertical(g16)
    c: Coincident(g17,g4)
    c: Coincident(g17,g8)
    c: Vertical(g17)
    c: Coincident(g18,g0)
    c: Coincident(g18,g3)
    c: Vertical(g18)
    c: Coincident(g19,g4)
    c: Coincident(g19,g8)
    c: Vertical(g19)
    c: Coincident(g20,g5)
    c: Coincident(g20,g9)
    c: Vertical(g20)
    c: Coincident(g21,g5)
    c: Coincident(g21,g9)
    c: Vertical(g21)
    c: Coincident(g22,g10)
    c: Coincident(g22,g6)
    c: Vertical(g22)
    c: Coincident(g23,g6)
    c: Coincident(g23,g10)
    c: Vertical(g23)
FEATURE [Part::Extrusion] Extrude045  label="removeToCreateFanGrillHoles003"
  Base = -> Sketch054
  Dir = (0,-1,6e-16)
  DirMode = 2
  FaceMakerClass = Part::FaceMakerBullseye
  LengthFwd = 10
  LengthRev = 0
  Placement = pos=(65.4,44,54.82) rot=(0,0,1;0rad)
  Solid = true
  Symmetric = false
FEATURE [Part::Feature] Face105 .. Face108  x4 (patterned run collapsed; names and placements below)
  shape: bbox 3.5 x 17.8 x 2e-07 mm, 1 faces, 0 solids (baked)
FEATURE [Part::Revolution] Revolve113  label="removeToCreateScrewAndThreadedInsertHole041"
  Angle = 360
  Axis = (0,1,0)
  Base = (0,0,0)
  FaceMakerClass = Part::FaceMakerBullseye
  Placement = pos=(62.3,30.3,19.7) rot=(0,0,1;0rad)
  Solid = false
  Source = -> Face105
  Symmetric = false
FEATURE [Part::Revolution] Revolve114  label="removeToCreateScrewAndThreadedInsertHole042"
  Angle = 360
  Axis = (0,1,0)
  Base = (0,0,0)
  FaceMakerClass = Part::FaceMakerBullseye
  Placement = pos=(62.3,30.3,51.7) rot=(0,0,1;0rad)
  Solid = false
  Source = -> Face106
  Symmetric = false
FEATURE [Part::Revolution] Revolve115  label="removeToCreateScrewAndThreadedInsertHole043"
  Angle = 360
  Axis = (0,1,0)
  Base = (0,0,0)
  FaceMakerClass = Part::FaceMakerBullseye
  Placement = pos=(30.3,30.3,19.7) rot=(0,0,1;0rad)
  Solid = false
  Source = -> Face107
  Symmetric = false
FEATURE [Part::Revolution] Revolve116  label="removeToCreateScrewAndThreadedInsertHole044"
  Angle = 360
  Axis = (0,1,0)
  Base = (0,0,0)
  FaceMakerClass = Part::FaceMakerBullseye
  Placement = pos=(30.3,30.3,51.7) rot=(0,0,1;0rad)
  Solid = false
  Source = -> Face108
  Symmetric = false
FEATURE [Part::MultiFuse] Fusion083  label="createThreadedInsertHolesForFan004"
  Shapes = -> [Revolve113,Revolve114,Revolve115,Revolve116]
FEATURE [Part::Box] Box024  label="removeToCreteHoleForPlugHousing026"
  AttacherType = Attacher::AttachEngine3D
  Height = 28.6
  Length = 10
  Placement = pos=(-2,0,21.7) rot=(0,0,1;0rad)
  Width = 19
FEATURE [Part::Cylinder] Cylinder038  label="removeToCreteHoleForPlugHousing027"
  Angle = 360
  AttacherType = Attacher::AttachEngine3D
  Height = 20
  Placement = pos=(-2,19,36) rot=(0,1,0;1.5708rad)
  Radius = 14.3
FEATURE [Part::MultiFuse] Fusion084  label="removeToCreteHoleForPlugHousing028"
  Shapes = -> [Box024,Cylinder038]
FEATURE [Part::Cylinder] Cylinder039
  Angle = 360
  AttacherType = Attacher::AttachEngine3D
  Height = 20
  Placement = pos=(0,0,36.15) rot=(0,0,1;0rad)
  Radius = 14.3
FEATURE [Part::Cylinder] Cylinder040
  Angle = 360
  AttacherType = Attacher::AttachEngine3D
  Height = 10
  Placement = pos=(0,0,36.15) rot=(0,0,1;0rad)
  Radius = 4
FEATURE [Part::Box] Box025  label="removeToCreteHoleForPlugHousing030"
  AttacherType = Attacher::AttachEngine3D
  Height = 28.6
  Length = 20
  Placement = pos=(106.15,0,21.7) rot=(0,0,1;0rad)
  Width = 19
FEATURE [Part::MultiFuse] Fusion086  label="removeToCreteHoleForPlugHousing031"
  Placement = pos=(70,19,36) rot=(0,1,0;1.5708rad)
  Shapes = -> [Cylinder039,Cylinder040]
FEATURE [Part::MultiFuse] Fusion085  label="removeToCreteHoleForPlugHousing029"
  Shapes = -> [Box025,Fusion086]
FEATURE [Sketcher::SketchObject] Sketch055
  FullyConstrained = true
  Placement = pos=(117,19,0) rot=(0.57735,0.57735,0.57735;2.0944rad)
  sketch-geometry (48):
    g0: LineSegment StartX=-49.19 StartY=69.25 StartZ=0 EndX=-49.19 EndY=66.25 EndZ=0
    g1: LineSegment StartX=-49.19 StartY=63.5 StartZ=0 EndX=-49.19 EndY=60.5 EndZ=0
    g2: LineSegment StartX=-49.19 StartY=57.75 StartZ=0 EndX=-49.19 EndY=54.75 EndZ=0
    g3: LineSegment StartX=-49.19 StartY=52 StartZ=0 EndX=-49.19 EndY=49 EndZ=0
    g4: LineSegment StartX=-49.19 StartY=46.25 StartZ=0 EndX=-49.19 EndY=43.25 EndZ=0
    g5: LineSegment StartX=-49.19 StartY=40.5 StartZ=0 EndX=-49.19 EndY=37.5 EndZ=0
    g6: LineSegment StartX=-49.19 StartY=34.5 StartZ=0 EndX=-49.19 EndY=31.5 EndZ=0
    g7: LineSegment StartX=-49.19 StartY=28.75 StartZ=0 EndX=-49.19 EndY=25.75 EndZ=0
    g8: LineSegment StartX=-49.19 StartY=23 StartZ=0 EndX=-49.19 EndY=20 EndZ=0
    g9: LineSegment StartX=-49.19 StartY=17.25 StartZ=0 EndX=-49.19 EndY=14.25 EndZ=0
    g10: LineSegment StartX=-49.19 StartY=11.5 StartZ=0 EndX=-49.19 EndY=8.5 EndZ=0
    g11: LineSegment StartX=-49.19 StartY=5.75 StartZ=0 EndX=-49.19 EndY=2.75 EndZ=0
    g12: ArcOfCircle CenterX=-1.5 CenterY=67.75 CenterZ=0 NormalX=0 NormalY=0 NormalZ=1 AngleXU=0 Radius=1.5 StartAngle=4.71239 EndAngle=7.85398
    g13: ArcOfCircle CenterX=-1.5 CenterY=62 CenterZ=0 NormalX=0 NormalY=0 NormalZ=1 AngleXU=0 Radius=1.5 StartAngle=4.71239 EndAngle=7.85398
    g14: ArcOfCircle CenterX=-1.5 CenterY=56.25 CenterZ=0 NormalX=0 NormalY=0 NormalZ=1 AngleXU=0 Radius=1.5 StartAngle=4.71239 EndAngle=7.85398
    g15: ArcOfCircle CenterX=-11.49 CenterY=50.5 CenterZ=0 NormalX=0 NormalY=0 NormalZ=1 AngleXU=0 Radius=1.5 StartAngle=4.71239 EndAngle=7.85398
    g16: ArcOfCircle CenterX=-16.28 CenterY=44.75 CenterZ=0 NormalX=0 NormalY=0 NormalZ=1 AngleXU=0 Radius=1.5 StartAngle=4.71239 EndAngle=7.85398
    g17: ArcOfCircle CenterX=-18.2337 CenterY=39 CenterZ=0 NormalX=0 NormalY=0 NormalZ=1 AngleXU=0 Radius=1.5 StartAngle=4.71485 EndAngle=7.85398
    g18: ArcOfCircle CenterX=-16.2837 CenterY=27.25 CenterZ=0 NormalX=0 NormalY=0 NormalZ=1 AngleXU=0 Radius=1.5 StartAngle=4.71485 EndAngle=7.85398
    g19: ArcOfCircle CenterX=-18.2337 CenterY=33 CenterZ=0 NormalX=0 NormalY=0 NormalZ=1 AngleXU=0 Radius=1.5 StartAngle=4.71485 EndAngle=7.85398
    g20: ArcOfCircle CenterX=-11.49 CenterY=21.5 CenterZ=0 NormalX=0 NormalY=0 NormalZ=1 AngleXU=0 Radius=1.5 StartAngle=4.71239 EndAngle=7.85398
    g21: ArcOfCircle CenterX=-1.5 CenterY=4.25 CenterZ=0 NormalX=0 NormalY=0 NormalZ=1 AngleXU=0 Radius=1.5 StartAngle=4.71239 EndAngle=7.85398
    g22: ArcOfCircle CenterX=-1.5 CenterY=10 CenterZ=0 NormalX=0 NormalY=0 NormalZ=1 AngleXU=0 Radius=1.5 StartAngle=4.71239 EndAngle=7.85398
    g23: ArcOfCircle CenterX=-1.5 CenterY=15.75 CenterZ=0 NormalX=0 NormalY=0 NormalZ=1 AngleXU=0 Radius=1.5 StartAngle=4.71239 EndAngle=7.85398
    g24: LineSegment StartX=-49.19 StartY=69.25 StartZ=0 EndX=-1.5 EndY=69.25 EndZ=0
    g25: LineSegment StartX=-49.19 StartY=66.25 StartZ=0 EndX=-1.5 EndY=66.25 EndZ=0
    g26: LineSegment StartX=-49.19 StartY=63.5 StartZ=0 EndX=-1.5 EndY=63.5 EndZ=0
    g27: LineSegment StartX=-49.19 StartY=60.5 StartZ=0 EndX=-1.5 EndY=60.5 EndZ=0
    g28: LineSegment StartX=-49.19 StartY=57.75 StartZ=0 EndX=-1.5 EndY=57.75 EndZ=0
    g29: LineSegment StartX=-49.19 StartY=54.75 StartZ=0 EndX=-1.5 EndY=54.75 EndZ=0
    g30: LineSegment StartX=-49.19 StartY=52 StartZ=0 EndX=-11.49 EndY=52 EndZ=0
    g31: LineSegment StartX=-49.19 StartY=49 StartZ=0 EndX=-11.49 EndY=49 EndZ=0
    g32: LineSegment StartX=-49.19 StartY=46.25 StartZ=0 EndX=-16.28 EndY=46.25 EndZ=0
    g33: LineSegment StartX=-49.19 StartY=43.25 StartZ=0 EndX=-16.28 EndY=43.25 EndZ=0
    g34: LineSegment StartX=-49.19 StartY=40.5 StartZ=0 EndX=-18.2337 EndY=40.5 EndZ=0
    g35: LineSegment StartX=-49.19 StartY=37.5 StartZ=0 EndX=-18.23 EndY=37.5 EndZ=0
    g36: LineSegment StartX=-49.19 StartY=34.5 StartZ=0 EndX=-18.2337 EndY=34.5 EndZ=0
    g37: LineSegment StartX=-49.19 StartY=31.5 StartZ=0 EndX=-18.23 EndY=31.5 EndZ=0
    g38: LineSegment StartX=-49.19 StartY=28.75 StartZ=0 EndX=-16.2837 EndY=28.75 EndZ=0
    g39: LineSegment StartX=-49.19 StartY=25.75 StartZ=0 EndX=-16.28 EndY=25.75 EndZ=0
    g40: LineSegment StartX=-49.19 StartY=23 StartZ=0 EndX=-11.49 EndY=23 EndZ=0
    g41: LineSegment StartX=-49.19 StartY=20 StartZ=0 EndX=-11.49 EndY=20 EndZ=0
    g42: LineSegment StartX=-49.19 StartY=17.25 StartZ=0 EndX=-1.5 EndY=17.25 EndZ=0
    g43: LineSegment StartX=-49.19 StartY=14.25 StartZ=0 EndX=-1.5 EndY=14.25 EndZ=0
    g44: LineSegment StartX=-49.19 StartY=11.5 StartZ=0 EndX=-1.5 EndY=11.5 EndZ=0
    g45: LineSegment StartX=-49.19 StartY=8.5 StartZ=0 EndX=-1.5 EndY=8.5 EndZ=0
    g46: LineSegment StartX=-49.19 StartY=5.75 StartZ=0 EndX=-1.5 EndY=5.75 EndZ=0
    g47: LineSegment StartX=-49.19 StartY=2.75 StartZ=0 EndX=-1.5 EndY=2.75 EndZ=0
  constraints (120):
    c: Vertical(g0)
    c: Distance(g0) = 3
    c: Block(g0)
    c: Vertical(g1)
    c: Distance(g1) = 3
    c: Vertical(g2)
    c: Equal(g0,g2) = 3
    c: Block(g2)
    c: Vertical(g3)
    c: Equal(g1,g3) = 3
    c: Vertical(g4)
    c: Equal(g0,g4) = 3
    c: Block(g4)
    c: Vertical(g5)
    c: Equal(g1,g5) = 3
    c: Vertical(g6)
    c: Equal(g0,g6) = 3
    c: Block(g6)
    c: Vertical(g7)
    c: Equal(g1,g7) = 3
    c: Vertical(g8)
    c: Equal(g0,g8) = 3
    c: Block(g8)
    c: Vertical(g9)
    c: Equal(g1,g9) = 3
    c: Vertical(g10)
    c: Equal(g0,g10) = 3
    c: Block(g10)
    c: Vertical(g11)
    c: Equal(g1,g11) = 3
    c: Block(g12)
    c: Block(g13)
    c: Block(g14)
    c: Block(g15)
    c: Block(g16)
    c: Block(g17)
    c: Block(g18)
    c: Block(g19)
    c: Block(g20)
    c: Block(g21)
    c: Block(g22)
    c: Block(g23)
    c: Block(g11)
    c: Block(g9)
    c: Block(g7)
    c: Block(g5)
    c: Block(g3)
    c: Block(g1)
    c: Coincident(g24,g0)
    c: Coincident(g24,g12)
    c: Horizontal(g24)
    c: Coincident(g25,g0)
    c: Coincident(g25,g12)
    c: Horizontal(g25)
    c: Coincident(g26,g1)
    c: Coincident(g26,g13)
    c: Horizontal(g26)
    c: Coincident(g27,g1)
    c: Coincident(g27,g13)
    c: Horizontal(g27)
    c: Coincident(g28,g2)
    c: Coincident(g28,g14)
    c: Horizontal(g28)
    c: Coincident(g29,g2)
    c: Coincident(g29,g14)
    c: Horizontal(g29)
    c: Coincident(g30,g3)
    c: Coincident(g30,g15)
    c: Horizontal(g30)
    c: Coincident(g31,g3)
    c: Coincident(g31,g15)
    c: Horizontal(g31)
    c: Coincident(g32,g4)
    c: Coincident(g32,g16)
    c: Horizontal(g32)
    c: Coincident(g33,g4)
    c: Coincident(g33,g16)
    c: Horizontal(g33)
    c: Coincident(g34,g5)
    c: Coincident(g34,g17)
    c: Horizontal(g34)
    c: Coincident(g35,g5)
    c: Coincident(g35,g17)
    c: Horizontal(g35)
    c: Coincident(g36,g6)
    c: Coincident(g36,g19)
    c: Horizontal(g36)
    c: Coincident(g37,g6)
    c: Coincident(g37,g19)
    c: Horizontal(g37)
    c: Coincident(g38,g7)
    c: Coincident(g38,g18)
    c: Horizontal(g38)
    c: Coincident(g39,g7)
    c: Coincident(g39,g18)
    c: Horizontal(g39)
    c: Coincident(g40,g8)
    c: Coincident(g40,g20)
    c: Horizontal(g40)
    c: Coincident(g41,g8)
    c: Coincident(g41,g20)
    c: Horizontal(g41)
    c: Coincident(g42,g9)
    c: Coincident(g42,g23)
    c: Horizontal(g42)
    c: Coincident(g43,g9)
    c: Coincident(g43,g23)
    c: Horizontal(g43)
    c: Coincident(g44,g10)
    c: Coincident(g44,g22)
    c: Horizontal(g44)
    c: Coincident(g45,g10)
    c: Coincident(g45,g22)
    c: Horizontal(g45)
    c: Coincident(g46,g11)
    c: Coincident(g46,g21)
    c: Horizontal(g46)
    c: Coincident(g47,g11)
    c: Coincident(g47,g21)
    c: Horizontal(g47)
FEATURE [Part::Extrusion] Extrude046
  Base = -> Sketch055
  Dir = (1,0,0)
  DirMode = 2
  FaceMakerClass = Part::FaceMakerBullseye
  LengthFwd = 23
  LengthRev = 0
  Placement = pos=(-19,0,0) rot=(0,0,1;0rad)
  Solid = true
  Symmetric = false
FEATURE [Part::Fillet] Fillet038  label="removeToCreateVentalationHoles001"
  Base = -> Extrude046
  Edges = <same value as first occurrence — deduplicated (x6 in doc)>
  Placement = pos=(7,0,0) rot=(0,0,1;0rad)
FEATURE [Sketcher::SketchObject] Sketch056  label="topSketch014"
  FullyConstrained = true
  sketch-geometry (22):
    g0: LineSegment StartX=5.21097e-06 StartY=3 StartZ=0 EndX=5.21097e-06 EndY=19 EndZ=0
    g1: ArcOfCircle CenterX=19 CenterY=19 CenterZ=0 NormalX=0 NormalY=0 NormalZ=1 AngleXU=0 Radius=19 StartAngle=1.5708 EndAngle=3.14159
    g2: ArcOfCircle CenterX=19 CenterY=19 CenterZ=0 NormalX=0 NormalY=0 NormalZ=1 AngleXU=0 Radius=16 StartAngle=1.5708 EndAngle=3.14159
    g3: LineSegment StartX=114 StartY=35 StartZ=0 EndX=19 EndY=35 EndZ=0
    g4: LineSegment StartX=5.21097e-06 StartY=3 StartZ=0 EndX=5.21097e-06 EndY=0 EndZ=0
    g5: LineSegment StartX=3 StartY=0 StartZ=0 EndX=5.21097e-06 EndY=0 EndZ=0
    g6: LineSegment StartX=3 StartY=19 StartZ=0 EndX=3 EndY=0 EndZ=0
    g7: LineSegment StartX=19 StartY=38 StartZ=0 EndX=124 EndY=38 EndZ=0
    g8: Circle CenterX=119 CenterY=35 CenterZ=0 NormalX=0 NormalY=0 NormalZ=1 AngleXU=0 Radius=1
    g9: Circle CenterX=121 CenterY=35 CenterZ=0 NormalX=0 NormalY=0 NormalZ=1 AngleXU=0 Radius=1
    g10: Circle CenterX=121 CenterY=33 CenterZ=0 NormalX=0 NormalY=0 NormalZ=1 AngleXU=0 Radius=1
    g11: BSplineCurve PolesCount=3 KnotsCount=2 Degree=2 IsPeriodic=0
    g12: GeomPoint X=119 Y=35 Z=0
    g13: GeomPoint X=121 Y=33 Z=0
    g14: LineSegment StartX=119 StartY=35 StartZ=0 EndX=114 EndY=35 EndZ=0
    g15: ArcOfCircle CenterX=105 CenterY=19 CenterZ=0 NormalX=0 NormalY=0 NormalZ=1 AngleXU=0 Radius=16 StartAngle=5.60905 EndAngle=6.28319
    g16: LineSegment StartX=121 StartY=33 StartZ=0 EndX=121 EndY=19 EndZ=0
    g17: LineSegment StartX=117.5 StartY=9.01251 StartZ=0 EndX=121.163 EndY=9.0125 EndZ=0
    g18: ArcOfCircle CenterX=105 CenterY=19 CenterZ=0 NormalX=0 NormalY=0 NormalZ=1 AngleXU=0 Radius=20.6155 StartAngle=5.7297 EndAngle=6.28319
    g19: LineSegment StartX=121.163 StartY=9.0125 StartZ=0 EndX=122.538 EndY=8.16329 EndZ=0
    g20: LineSegment StartX=124 StartY=38 StartZ=0 EndX=125.616 EndY=38 EndZ=0
    g21: LineSegment StartX=125.616 StartY=19 StartZ=0 EndX=125.616 EndY=38 EndZ=0
  constraints (49):
    c: Vertical(g0)
    c: Block(g0)
    c: Coincident(g1,g0)
    c: Block(g1)
    c: Coincident(g2,g1)
    c: Block(g2)
    c: Coincident(g3,g2)
    c: Horizontal(g3)
    c: Tangent(g3,g2)
    c: Coincident(g4,g0)
    c: Distance(g4) = 3
    c: Vertical(g4)
    c: Coincident(g5,g4)
    c: Horizontal(g5)
    c: Coincident(g6,g2)
    c: Coincident(g6,g5)
    c: Vertical(g6)
    c: Horizontal(g7)
    c: Distance(g7) = 105
    c: Coincident(g7,g1)
    c: Block(g3)
    c: Weight(g8) = 1
    c: Equal(g8,g9)
    c: Equal(g8,g10)
    c: InternalAlignment(g8,g11)
    c: InternalAlignment(g9,g11)
    c: InternalAlignment(g10,g11)
    c: InternalAlignment(g12,g11)
    c: InternalAlignment(g13,g11)
    c: Block(g11)
    c: Coincident(g14,g11)
    c: Coincident(g14,g3)
    c: Horizontal(g14)
    c: Block(g15)
    c: Coincident(g16,g11)
    c: Coincident(g16,g15)
    c: Vertical(g16)
    c: Distance(g16) = 14
    c: Coincident(g17,g15)
    c: Block(g18)
    c: Coincident(g19,g18)
    c: Coincident(g20,g7)
    c: Horizontal(g20)
    c: Vertical(g21)
    c: Coincident(g20,g21)
    c: Block(g20)
    c: Block(g21)
    c: Block(g19)
    c: Block(g17)
FEATURE [Part::Box] Box026  label="removeToCreteHoleForPlugHousing032"
  AttacherType = Attacher::AttachEngine3D
  Height = 28.6
  Length = 10
  Placement = pos=(-2,0,21.7) rot=(0,0,1;0rad)
  Width = 19
FEATURE [Part::Feature] Face109 .. Face112  x4 (patterned run collapsed; names and placements below)
  shape: bbox 3.5 x 17.8 x 2e-07 mm, 1 faces, 0 solids (baked)
FEATURE [Part::Revolution] Revolve117  label="removeToCreateScrewAndThreadedInsertHole045"
  Angle = 360
  Axis = (0,1,0)
  Base = (0,0,0)
  FaceMakerClass = Part::FaceMakerBullseye
  Placement = pos=(62.3,30.3,19.7) rot=(0,0,1;0rad)
  Solid = false
  Source = -> Face109
  Symmetric = false
FEATURE [Part::Revolution] Revolve118  label="removeToCreateScrewAndThreadedInsertHole046"
  Angle = 360
  Axis = (0,1,0)
  Base = (0,0,0)
  FaceMakerClass = Part::FaceMakerBullseye
  Placement = pos=(62.3,30.3,51.7) rot=(0,0,1;0rad)
  Solid = false
  Source = -> Face110
  Symmetric = false
FEATURE [Part::Revolution] Revolve119  label="removeToCreateScrewAndThreadedInsertHole047"
  Angle = 360
  Axis = (0,1,0)
  Base = (0,0,0)
  FaceMakerClass = Part::FaceMakerBullseye
  Placement = pos=(30.3,30.3,19.7) rot=(0,0,1;0rad)
  Solid = false
  Source = -> Face111
  Symmetric = false
FEATURE [Part::Revolution] Revolve120  label="removeToCreateScrewAndThreadedInsertHole048"
  Angle = 360
  Axis = (0,1,0)
  Base = (0,0,0)
  FaceMakerClass = Part::FaceMakerBullseye
  Placement = pos=(30.3,30.3,51.7) rot=(0,0,1;0rad)
  Solid = false
  Source = -> Face112
  Symmetric = false
FEATURE [Part::MultiFuse] Fusion087  label="createThreadedInsertHolesForFan005"
  Shapes = -> [Revolve117,Revolve118,Revolve119,Revolve120]
FEATURE [Part::Extrusion] Extrude047
  Base = -> Sketch056
  Dir = (0,0,1)
  DirMode = 2
  FaceMakerClass = Part::FaceMakerBullseye
  LengthFwd = 72
  LengthRev = 0
  Solid = true
  Symmetric = false
FEATURE [Part::Fillet] Fillet039  label="top019"
  Base = -> Extrude047
  Edges = 1 edges r=2: [Edge35]
FEATURE [Sketcher::SketchObject] Sketch057
  FullyConstrained = false
  Placement = pos=(0,0,0) rot=(1,0,0;1.5708rad)
  sketch-geometry (24):
    g0: ArcOfCircle CenterX=-4 CenterY=-10.5 CenterZ=0 NormalX=0 NormalY=0 NormalZ=1 AngleXU=0 Radius=1.5 StartAngle=6e-16 EndAngle=3.14159
    g1: ArcOfCircle CenterX=-34.2 CenterY=-10.5 CenterZ=0 NormalX=0 NormalY=0 NormalZ=1 AngleXU=0 Radius=1.5 StartAngle=0 EndAngle=3.14159
    g2: ArcOfCircle CenterX=-34.2 CenterY=-27.7 CenterZ=0 NormalX=0 NormalY=0 NormalZ=1 AngleXU=0 Radius=1.5 StartAngle=3.14159 EndAngle=6.28319
    g3: ArcOfCircle CenterX=-4 CenterY=-27.7 CenterZ=0 NormalX=0 NormalY=0 NormalZ=1 AngleXU=0 Radius=1.5 StartAngle=3.1416 EndAngle=6.28319
    g4: ArcOfCircle CenterX=-10 CenterY=-4.3 CenterZ=0 NormalX=0 NormalY=0 NormalZ=1 AngleXU=0 Radius=1.5 StartAngle=2e-16 EndAngle=3.14159
    g5: ArcOfCircle CenterX=-16.1 CenterY=-1.8 CenterZ=0 NormalX=0 NormalY=0 NormalZ=1 AngleXU=0 Radius=1.5 StartAngle=5e-16 EndAngle=3.14159
    g6: ArcOfCircle CenterX=-22.1 CenterY=-1.8 CenterZ=0 NormalX=0 NormalY=0 NormalZ=1 AngleXU=0 Radius=1.5 StartAngle=5e-16 EndAngle=3.14159
    g7: ArcOfCircle CenterX=-28.2 CenterY=-4.3 CenterZ=0 NormalX=0 NormalY=0 NormalZ=1 AngleXU=0 Radius=1.5 StartAngle=2e-16 EndAngle=3.14159
    g8: ArcOfCircle CenterX=-10 CenterY=-33.9 CenterZ=0 NormalX=0 NormalY=0 NormalZ=1 AngleXU=0 Radius=1.5 StartAngle=3.14159 EndAngle=6.28319
    g9: ArcOfCircle CenterX=-16.1 CenterY=-36.4 CenterZ=0 NormalX=0 NormalY=0 NormalZ=1 AngleXU=0 Radius=1.5 StartAngle=3.14159 EndAngle=6.28319
    g10: ArcOfCircle CenterX=-22.1 CenterY=-36.4 CenterZ=0 NormalX=0 NormalY=0 NormalZ=1 AngleXU=0 Radius=1.5 StartAngle=3.14159 EndAngle=6.28319
    g11: ArcOfCircle CenterX=-28.2 CenterY=-33.9 CenterZ=0 NormalX=0 NormalY=0 NormalZ=1 AngleXU=0 Radius=1.5 StartAngle=3.14159 EndAngle=6.28319
    g12: LineSegment StartX=-35.7 StartY=-10.5 StartZ=0 EndX=-35.7 EndY=-27.7 EndZ=0
    g13: LineSegment StartX=-32.7 StartY=-10.5 StartZ=0 EndX=-32.7 EndY=-27.7 EndZ=0
    g14: LineSegment StartX=-29.7 StartY=-33.9 StartZ=0 EndX=-29.7 EndY=-4.3 EndZ=0
    g15: LineSegment StartX=-26.7 StartY=-33.9 StartZ=0 EndX=-26.7 EndY=-4.3 EndZ=0
    g16: LineSegment StartX=-2.5 StartY=-10.5 StartZ=0 EndX=-2.5 EndY=-27.7 EndZ=0
    g17: LineSegment StartX=-8.5 StartY=-4.3 StartZ=0 EndX=-8.5 EndY=-33.9 EndZ=0
    g18: LineSegment StartX=-5.5 StartY=-10.5 StartZ=0 EndX=-5.5 EndY=-27.7 EndZ=0
    g19: LineSegment StartX=-11.5 StartY=-4.3 StartZ=0 EndX=-11.5 EndY=-33.9 EndZ=0
    g20: LineSegment StartX=-14.6 StartY=-1.8 StartZ=0 EndX=-14.6 EndY=-36.4 EndZ=0
    g21: LineSegment StartX=-17.6 StartY=-1.8 StartZ=0 EndX=-17.6 EndY=-36.4 EndZ=0
    g22: LineSegment StartX=-20.6 StartY=-36.4 StartZ=0 EndX=-20.6 EndY=-1.8 EndZ=0
    g23: LineSegment StartX=-23.6 StartY=-1.8 StartZ=0 EndX=-23.6 EndY=-36.4 EndZ=0
  constraints (48):
    c: Block(g0)
    c: Block(g1)
    c: Block(g2)
    c: Block(g3)
    c: Block(g4)
    c: Block(g5)
    c: Block(g6)
    c: Block(g7)
    c: Block(g8)
    c: Block(g9)
    c: Block(g10)
    c: Block(g11)
    c: Coincident(g12,g1)
    c: Coincident(g12,g2)
    c: Vertical(g12)
    c: Coincident(g13,g1)
    c: Coincident(g13,g2)
    c: Vertical(g13)
    c: Coincident(g14,g11)
    c: Coincident(g14,g7)
    c: Vertical(g14)
    c: Coincident(g15,g11)
    c: Coincident(g15,g7)
    c: Vertical(g15)
    c: Coincident(g16,g0)
    c: Coincident(g16,g3)
    c: Vertical(g16)
    c: Coincident(g17,g4)
    c: Coincident(g17,g8)
    c: Vertical(g17)
    c: Coincident(g18,g0)
    c: Coincident(g18,g3)
    c: Vertical(g18)
    c: Coincident(g19,g4)
    c: Coincident(g19,g8)
    c: Vertical(g19)
    c: Coincident(g20,g5)
    c: Coincident(g20,g9)
    c: Vertical(g20)
    c: Coincident(g21,g5)
    c: Coincident(g21,g9)
    c: Vertical(g21)
    c: Coincident(g22,g10)
    c: Coincident(g22,g6)
    c: Vertical(g22)
    c: Coincident(g23,g6)
    c: Coincident(g23,g10)
    c: Vertical(g23)
FEATURE [Part::Extrusion] Extrude048  label="removeToCreateFanGrillHoles004"
  Base = -> Sketch057
  Dir = (0,-1,6e-16)
  DirMode = 2
  FaceMakerClass = Part::FaceMakerBullseye
  LengthFwd = 10
  LengthRev = 0
  Placement = pos=(65.4,44,54.82) rot=(0,0,1;0rad)
  Solid = true
  Symmetric = false
FEATURE [Part::Cut] Cut040  label="top021"
  Base = -> Fillet039
  Tool = -> Extrude048
FEATURE [Part::Cylinder] Cylinder041  label="removeToCreteHoleForPlugHousing034"
  Angle = 360
  AttacherType = Attacher::AttachEngine3D
  Height = 20
  Placement = pos=(-2,19,36) rot=(0,1,0;1.5708rad)
  Radius = 14.3
FEATURE [Part::MultiFuse] Fusion089  label="removeToCreteHoleForPlugHousing035"
  Shapes = -> [Box026,Cylinder041]
FEATURE [Part::Cylinder] Cylinder042
  Angle = 360
  AttacherType = Attacher::AttachEngine3D
  Height = 20
  Placement = pos=(0,0,36.15) rot=(0,0,1;0rad)
  Radius = 14.3
FEATURE [Part::Cylinder] Cylinder043
  Angle = 360
  AttacherType = Attacher::AttachEngine3D
  Height = 10
  Placement = pos=(0,0,36.15) rot=(0,0,1;0rad)
  Radius = 4
FEATURE [Part::Box] Box027  label="removeToCreteHoleForPlugHousing036"
  AttacherType = Attacher::AttachEngine3D
  Height = 28.6
  Length = 20
  Placement = pos=(106.15,0,21.7) rot=(0,0,1;0rad)
  Width = 19
FEATURE [Part::Cut] Cut041  label="top022"
  Base = -> Cut040
  Tool = -> Fusion087
FEATURE [Part::Cut] Cut039  label="top020"
  Base = -> Cut041
  Tool = -> Fusion089
FEATURE [Part::MultiFuse] Fusion090  label="removeToCreteHoleForPlugHousing037"
  Placement = pos=(70,19,36) rot=(0,1,0;1.5708rad)
  Shapes = -> [Cylinder042,Cylinder043]
FEATURE [Part::MultiFuse] Fusion088  label="removeToCreteHoleForPlugHousing033"
  Shapes = -> [Box027,Fusion090]
FEATURE [Part::Cut] Cut042  label="removeToCreteHoleForPlugHousing038"
  Base = -> Cut039
  Tool = -> Fusion088
FEATURE [Part::MultiFuse] Fusion091  label="removeFromTop"
  Shapes = -> [Fillet038,Fusion085,Fusion084,Fusion083,Extrude045]
FEATURE [Part::Cut] Cut043  label="REAL TOP ====="
  Base = -> Fillet036
  Tool = -> Fusion091
FEATURE [Part::MultiFuse] Fusion092  label="caseScrewPillarBracket016"
  Shapes = -> [Extrude030,Extrude031,Extrude032,Extrude033,Extrude034,Extrude035,Extrude036,Extrude037,Box013,Box014]
FEATURE [Sketcher::SketchObject] Sketch058  label="topSketch015"
  FullyConstrained = true
  sketch-geometry (20):
    g0: LineSegment StartX=5.21097e-06 StartY=3 StartZ=0 EndX=5.21097e-06 EndY=19 EndZ=0
    g1: ArcOfCircle CenterX=19 CenterY=19 CenterZ=0 NormalX=0 NormalY=0 NormalZ=1 AngleXU=0 Radius=19 StartAngle=1.5708 EndAngle=3.14159
    g2: ArcOfCircle CenterX=19 CenterY=19 CenterZ=0 NormalX=0 NormalY=0 NormalZ=1 AngleXU=0 Radius=16 StartAngle=1.5708 EndAngle=3.14159
    g3: LineSegment StartX=114 StartY=35 StartZ=0 EndX=19 EndY=35 EndZ=0
    g4: LineSegment StartX=5.21097e-06 StartY=3 StartZ=0 EndX=5.21097e-06 EndY=0 EndZ=0
    g5: LineSegment StartX=3 StartY=0 StartZ=0 EndX=5.21097e-06 EndY=0 EndZ=0
    g6: LineSegment StartX=3 StartY=19 StartZ=0 EndX=3 EndY=0 EndZ=0
    g7: LineSegment StartX=19 StartY=38 StartZ=0 EndX=124 EndY=38 EndZ=0
    g8: Circle CenterX=119 CenterY=35 CenterZ=0 NormalX=0 NormalY=0 NormalZ=1 AngleXU=0 Radius=1
    g9: Circle CenterX=121 CenterY=35 CenterZ=0 NormalX=0 NormalY=0 NormalZ=1 AngleXU=0 Radius=1
    g10: Circle CenterX=121 CenterY=33 CenterZ=0 NormalX=0 NormalY=0 NormalZ=1 AngleXU=0 Radius=1
    g11: BSplineCurve PolesCount=3 KnotsCount=2 Degree=2 IsPeriodic=0
    g12: GeomPoint X=119 Y=35 Z=0
    g13: GeomPoint X=121 Y=33 Z=0
    g14: LineSegment StartX=119 StartY=35 StartZ=0 EndX=114 EndY=35 EndZ=0
    g15: ArcOfCircle CenterX=105 CenterY=19 CenterZ=0 NormalX=0 NormalY=0 NormalZ=1 AngleXU=0 Radius=19 StartAngle=5.7297 EndAngle=6.28319
    g16: ArcOfCircle CenterX=105 CenterY=19 CenterZ=0 NormalX=0 NormalY=0 NormalZ=1 AngleXU=0 Radius=16 StartAngle=5.60905 EndAngle=6.28319
    g17: LineSegment StartX=121 StartY=33 StartZ=0 EndX=121 EndY=19 EndZ=0
    g18: LineSegment StartX=124 StartY=38 StartZ=0 EndX=124 EndY=19 EndZ=0
    g19: LineSegment StartX=117.5 StartY=9.01251 StartZ=0 EndX=121.163 EndY=9.0125 EndZ=0
  constraints (46):
    c: Vertical(g0)
    c: Block(g0)
    c: Coincident(g1,g0)
    c: Block(g1)
    c: Coincident(g2,g1)
    c: Block(g2)
    c: Coincident(g3,g2)
    c: Horizontal(g3)
    c: Tangent(g3,g2)
    c: Coincident(g4,g0)
    c: Distance(g4) = 3
    c: Vertical(g4)
    c: Coincident(g5,g4)
    c: Horizontal(g5)
    c: Coincident(g6,g2)
    c: Coincident(g6,g5)
    c: Vertical(g6)
    c: Horizontal(g7)
    c: Distance(g7) = 105
    c: Coincident(g7,g1)
    c: Block(g3)
    c: Weight(g8) = 1
    c: Equal(g8,g9)
    c: Equal(g8,g10)
    c: InternalAlignment(g8,g11)
    c: InternalAlignment(g9,g11)
    c: InternalAlignment(g10,g11)
    c: InternalAlignment(g12,g11)
    c: InternalAlignment(g13,g11)
    c: Block(g11)
    c: Coincident(g14,g11)
    c: Coincident(g14,g3)
    c: Horizontal(g14)
    c: Block(g15)
    c: Coincident(g16,g15)
    c: Block(g16)
    c: Coincident(g17,g11)
    c: Coincident(g17,g16)
    c: Vertical(g17)
    c: Distance(g17) = 14
    c: Coincident(g18,g7)
    c: Coincident(g18,g15)
    c: Vertical(g18)
    c: Distance(g18) = 19
    c: Coincident(g19,g16)
    c: Coincident(g19,g15)
FEATURE [Part::Extrusion] Extrude049  label="top023"
  Base = -> Sketch058
  Dir = (0,0,1)
  DirMode = 2
  FaceMakerClass = Part::FaceMakerBullseye
  LengthFwd = 72
  LengthRev = 0
  Solid = true
  Symmetric = false
FEATURE [Sketcher::SketchObject] Sketch059
  FullyConstrained = true
  MapMode = 3
  Placement = pos=(0,0,0) rot=(1,0,0;1.5708rad)
  Support = -> [Extrude049]
  sketch-geometry (8):
    g0: Circle CenterX=80.351 CenterY=-67.6202 CenterZ=0 NormalX=0 NormalY=0 NormalZ=1 AngleXU=0 Radius=2
    g1: Circle CenterX=80.351 CenterY=-67.6202 CenterZ=0 NormalX=0 NormalY=0 NormalZ=1 AngleXU=0 Radius=3
    g2: Circle CenterX=80.351 CenterY=-4.92017 CenterZ=0 NormalX=0 NormalY=0 NormalZ=1 AngleXU=0 Radius=2
    g3: Circle CenterX=80.351 CenterY=-4.92017 CenterZ=0 NormalX=0 NormalY=0 NormalZ=1 AngleXU=0 Radius=3
    g4: Circle CenterX=23.851 CenterY=-4.92017 CenterZ=0 NormalX=0 NormalY=0 NormalZ=1 AngleXU=0 Radius=2
    g5: Circle CenterX=23.851 CenterY=-4.92017 CenterZ=0 NormalX=0 NormalY=0 NormalZ=1 AngleXU=0 Radius=3
    g6: Circle CenterX=23.851 CenterY=-67.6202 CenterZ=0 NormalX=0 NormalY=0 NormalZ=1 AngleXU=0 Radius=2
    g7: Circle CenterX=23.851 CenterY=-67.6202 CenterZ=0 NormalX=0 NormalY=0 NormalZ=1 AngleXU=0 Radius=3
  constraints (8):
    c: Block(g3)
    c: Block(g2)
    c: Block(g1)
    c: Block(g0)
    c: Block(g6)
    c: Block(g7)
    c: Block(g4)
    c: Block(g5)
FEATURE [Sketcher::SketchObject] Sketch060
  FullyConstrained = true
  MapMode = 3
  Placement = pos=(0,0,0) rot=(1,0,0;1.5708rad)
  Support = -> [Extrude049]
  sketch-geometry (8):
    g0: Circle CenterX=80.351 CenterY=-67.6202 CenterZ=0 NormalX=0 NormalY=0 NormalZ=1 AngleXU=0 Radius=3
    g1: Circle CenterX=80.351 CenterY=-4.92017 CenterZ=0 NormalX=0 NormalY=0 NormalZ=1 AngleXU=0 Radius=3
    g2: Circle CenterX=23.851 CenterY=-4.92017 CenterZ=0 NormalX=0 NormalY=0 NormalZ=1 AngleXU=0 Radius=3
    g3: Circle CenterX=23.851 CenterY=-67.6202 CenterZ=0 NormalX=0 NormalY=0 NormalZ=1 AngleXU=0 Radius=3
    g4: Circle CenterX=23.851 CenterY=-67.6202 CenterZ=0 NormalX=0 NormalY=0 NormalZ=1 AngleXU=0 Radius=5
    g5: Circle CenterX=80.351 CenterY=-67.6202 CenterZ=0 NormalX=0 NormalY=0 NormalZ=1 AngleXU=0 Radius=5
    g6: Circle CenterX=23.851 CenterY=-4.92017 CenterZ=0 NormalX=0 NormalY=0 NormalZ=1 AngleXU=0 Radius=5
    g7: Circle CenterX=80.351 CenterY=-4.92017 CenterZ=0 NormalX=0 NormalY=0 NormalZ=1 AngleXU=0 Radius=5
  constraints (8):
    c: Block(g1)
    c: Block(g0)
    c: Block(g3)
    c: Block(g2)
    c: Block(g5)
    c: Block(g4)
    c: Block(g6)
    c: Block(g7)
FEATURE [Sketcher::SketchObject] Sketch061
  FullyConstrained = true
  MapMode = 3
  Placement = pos=(0,0,0) rot=(1,0,0;1.5708rad)
  sketch-geometry (8):
    g0: Circle CenterX=80.351 CenterY=-67.6202 CenterZ=0 NormalX=0 NormalY=0 NormalZ=1 AngleXU=0 Radius=3
    g1: Circle CenterX=80.351 CenterY=-4.92017 CenterZ=0 NormalX=0 NormalY=0 NormalZ=1 AngleXU=0 Radius=3
    g2: Circle CenterX=23.851 CenterY=-4.92017 CenterZ=0 NormalX=0 NormalY=0 NormalZ=1 AngleXU=0 Radius=3
    g3: Circle CenterX=23.851 CenterY=-67.6202 CenterZ=0 NormalX=0 NormalY=0 NormalZ=1 AngleXU=0 Radius=3
    g4: Circle CenterX=23.851 CenterY=-67.6202 CenterZ=0 NormalX=0 NormalY=0 NormalZ=1 AngleXU=0 Radius=5
    g5: Circle CenterX=80.351 CenterY=-67.6202 CenterZ=0 NormalX=0 NormalY=0 NormalZ=1 AngleXU=0 Radius=5
    g6: Circle CenterX=23.851 CenterY=-4.92017 CenterZ=0 NormalX=0 NormalY=0 NormalZ=1 AngleXU=0 Radius=5
    g7: Circle CenterX=80.351 CenterY=-4.92017 CenterZ=0 NormalX=0 NormalY=0 NormalZ=1 AngleXU=0 Radius=5
  constraints (8):
    c: Block(g1)
    c: Block(g0)
    c: Block(g3)
    c: Block(g2)
    c: Block(g5)
    c: Block(g4)
    c: Block(g6)
    c: Block(g7)
FEATURE [Sketcher::SketchObject] Sketch062  label="topSketch016"
  FullyConstrained = true
  sketch-geometry (20):
    g0: LineSegment StartX=5.21097e-06 StartY=3 StartZ=0 EndX=5.21097e-06 EndY=19 EndZ=0
    g1: ArcOfCircle CenterX=19 CenterY=19 CenterZ=0 NormalX=0 NormalY=0 NormalZ=1 AngleXU=0 Radius=19 StartAngle=1.5708 EndAngle=3.14159
    g2: ArcOfCircle CenterX=19 CenterY=19 CenterZ=0 NormalX=0 NormalY=0 NormalZ=1 AngleXU=0 Radius=16 StartAngle=1.5708 EndAngle=3.14159
    g3: LineSegment StartX=114 StartY=35 StartZ=0 EndX=19 EndY=35 EndZ=0
    g4: LineSegment StartX=5.21097e-06 StartY=3 StartZ=0 EndX=5.21097e-06 EndY=0 EndZ=0
    g5: LineSegment StartX=3 StartY=0 StartZ=0 EndX=5.21097e-06 EndY=0 EndZ=0
    g6: LineSegment StartX=3 StartY=19 StartZ=0 EndX=3 EndY=0 EndZ=0
    g7: LineSegment StartX=19 StartY=38 StartZ=0 EndX=124 EndY=38 EndZ=0
    g8: Circle CenterX=119 CenterY=35 CenterZ=0 NormalX=0 NormalY=0 NormalZ=1 AngleXU=0 Radius=1
    g9: Circle CenterX=121 CenterY=35 CenterZ=0 NormalX=0 NormalY=0 NormalZ=1 AngleXU=0 Radius=1
    g10: Circle CenterX=121 CenterY=33 CenterZ=0 NormalX=0 NormalY=0 NormalZ=1 AngleXU=0 Radius=1
    g11: BSplineCurve PolesCount=3 KnotsCount=2 Degree=2 IsPeriodic=0
    g12: GeomPoint X=119 Y=35 Z=0
    g13: GeomPoint X=121 Y=33 Z=0
    g14: LineSegment StartX=119 StartY=35 StartZ=0 EndX=114 EndY=35 EndZ=0
    g15: ArcOfCircle CenterX=105 CenterY=19 CenterZ=0 NormalX=0 NormalY=0 NormalZ=1 AngleXU=0 Radius=19 StartAngle=5.7297 EndAngle=6.28319
    g16: ArcOfCircle CenterX=105 CenterY=19 CenterZ=0 NormalX=0 NormalY=0 NormalZ=1 AngleXU=0 Radius=16 StartAngle=5.60905 EndAngle=6.28319
    g17: LineSegment StartX=121 StartY=33 StartZ=0 EndX=121 EndY=19 EndZ=0
    g18: LineSegment StartX=124 StartY=38 StartZ=0 EndX=124 EndY=19 EndZ=0
    g19: LineSegment StartX=117.5 StartY=9.01251 StartZ=0 EndX=121.163 EndY=9.0125 EndZ=0
  constraints (46):
    c: Vertical(g0)
    c: Block(g0)
    c: Coincident(g1,g0)
    c: Block(g1)
    c: Coincident(g2,g1)
    c: Block(g2)
    c: Coincident(g3,g2)
    c: Horizontal(g3)
    c: Tangent(g3,g2)
    c: Coincident(g4,g0)
    c: Distance(g4) = 3
    c: Vertical(g4)
    c: Coincident(g5,g4)
    c: Horizontal(g5)
    c: Coincident(g6,g2)
    c: Coincident(g6,g5)
    c: Vertical(g6)
    c: Horizontal(g7)
    c: Distance(g7) = 105
    c: Coincident(g7,g1)
    c: Block(g3)
    c: Weight(g8) = 1
    c: Equal(g8,g9)
    c: Equal(g8,g10)
    c: InternalAlignment(g8,g11)
    c: InternalAlignment(g9,g11)
    c: InternalAlignment(g10,g11)
    c: InternalAlignment(g12,g11)
    c: InternalAlignment(g13,g11)
    c: Block(g11)
    c: Coincident(g14,g11)
    c: Coincident(g14,g3)
    c: Horizontal(g14)
    c: Block(g15)
    c: Coincident(g16,g15)
    c: Block(g16)
    c: Coincident(g17,g11)
    c: Coincident(g17,g16)
    c: Vertical(g17)
    c: Distance(g17) = 14
    c: Coincident(g18,g7)
    c: Coincident(g18,g15)
    c: Vertical(g18)
    c: Distance(g18) = 19
    c: Coincident(g19,g16)
    c: Coincident(g19,g15)
FEATURE [Part::Extrusion] Extrude053  label="top024"
  Base = -> Sketch062
  Dir = (0,0,1)
  DirMode = 2
  FaceMakerClass = Part::FaceMakerBullseye
  LengthFwd = 72
  LengthRev = 0
  Solid = true
  Symmetric = false
FEATURE [Sketcher::SketchObject] Sketch063
  FullyConstrained = true
  MapMode = 3
  Placement = pos=(0,0,0) rot=(1,0,0;1.5708rad)
  Support = -> [Extrude053]
  sketch-geometry (8):
    g0: Circle CenterX=80.351 CenterY=-67.6202 CenterZ=0 NormalX=0 NormalY=0 NormalZ=1 AngleXU=0 Radius=2
    g1: Circle CenterX=80.351 CenterY=-67.6202 CenterZ=0 NormalX=0 NormalY=0 NormalZ=1 AngleXU=0 Radius=3
    g2: Circle CenterX=80.351 CenterY=-4.92017 CenterZ=0 NormalX=0 NormalY=0 NormalZ=1 AngleXU=0 Radius=2
    g3: Circle CenterX=80.351 CenterY=-4.92017 CenterZ=0 NormalX=0 NormalY=0 NormalZ=1 AngleXU=0 Radius=3
    g4: Circle CenterX=23.851 CenterY=-4.92017 CenterZ=0 NormalX=0 NormalY=0 NormalZ=1 AngleXU=0 Radius=2
    g5: Circle CenterX=23.851 CenterY=-4.92017 CenterZ=0 NormalX=0 NormalY=0 NormalZ=1 AngleXU=0 Radius=3
    g6: Circle CenterX=23.851 CenterY=-67.6202 CenterZ=0 NormalX=0 NormalY=0 NormalZ=1 AngleXU=0 Radius=2
    g7: Circle CenterX=23.851 CenterY=-67.6202 CenterZ=0 NormalX=0 NormalY=0 NormalZ=1 AngleXU=0 Radius=3
  constraints (8):
    c: Block(g3)
    c: Block(g2)
    c: Block(g1)
    c: Block(g0)
    c: Block(g6)
    c: Block(g7)
    c: Block(g4)
    c: Block(g5)
FEATURE [Part::Extrusion] Extrude054
  Base = -> Sketch063
  Dir = (0,-1,2e-16)
  DirMode = 2
  FaceMakerClass = Part::FaceMakerBullseye
  LengthFwd = 6
  LengthRev = 0
  Placement = pos=(0,9,0) rot=(0,0,1;0rad)
  Solid = true
  Symmetric = false
FEATURE [Sketcher::SketchObject] Sketch064  label="topSketch017"
  FullyConstrained = true
  sketch-geometry (20):
    g0: LineSegment StartX=5.21097e-06 StartY=3 StartZ=0 EndX=5.21097e-06 EndY=19 EndZ=0
    g1: ArcOfCircle CenterX=19 CenterY=19 CenterZ=0 NormalX=0 NormalY=0 NormalZ=1 AngleXU=0 Radius=19 StartAngle=1.5708 EndAngle=3.14159
    g2: ArcOfCircle CenterX=19 CenterY=19 CenterZ=0 NormalX=0 NormalY=0 NormalZ=1 AngleXU=0 Radius=16 StartAngle=1.5708 EndAngle=3.14159
    g3: LineSegment StartX=114 StartY=35 StartZ=0 EndX=19 EndY=35 EndZ=0
    g4: LineSegment StartX=5.21097e-06 StartY=3 StartZ=0 EndX=5.21097e-06 EndY=0 EndZ=0
    g5: LineSegment StartX=3 StartY=0 StartZ=0 EndX=5.21097e-06 EndY=0 EndZ=0
    g6: LineSegment StartX=3 StartY=19 StartZ=0 EndX=3 EndY=0 EndZ=0
    g7: LineSegment StartX=19 StartY=38 StartZ=0 EndX=124 EndY=38 EndZ=0
    g8: Circle CenterX=119 CenterY=35 CenterZ=0 NormalX=0 NormalY=0 NormalZ=1 AngleXU=0 Radius=1
    g9: Circle CenterX=121 CenterY=35 CenterZ=0 NormalX=0 NormalY=0 NormalZ=1 AngleXU=0 Radius=1
    g10: Circle CenterX=121 CenterY=33 CenterZ=0 NormalX=0 NormalY=0 NormalZ=1 AngleXU=0 Radius=1
    g11: BSplineCurve PolesCount=3 KnotsCount=2 Degree=2 IsPeriodic=0
    g12: GeomPoint X=119 Y=35 Z=0
    g13: GeomPoint X=121 Y=33 Z=0
    g14: LineSegment StartX=119 StartY=35 StartZ=0 EndX=114 EndY=35 EndZ=0
    g15: ArcOfCircle CenterX=105 CenterY=19 CenterZ=0 NormalX=0 NormalY=0 NormalZ=1 AngleXU=0 Radius=19 StartAngle=5.7297 EndAngle=6.28319
    g16: ArcOfCircle CenterX=105 CenterY=19 CenterZ=0 NormalX=0 NormalY=0 NormalZ=1 AngleXU=0 Radius=16 StartAngle=5.60905 EndAngle=6.28319
    g17: LineSegment StartX=121 StartY=33 StartZ=0 EndX=121 EndY=19 EndZ=0
    g18: LineSegment StartX=124 StartY=38 StartZ=0 EndX=124 EndY=19 EndZ=0
    g19: LineSegment StartX=117.5 StartY=9.01251 StartZ=0 EndX=121.163 EndY=9.0125 EndZ=0
  constraints (46):
    c: Vertical(g0)
    c: Block(g0)
    c: Coincident(g1,g0)
    c: Block(g1)
    c: Coincident(g2,g1)
    c: Block(g2)
    c: Coincident(g3,g2)
    c: Horizontal(g3)
    c: Tangent(g3,g2)
    c: Coincident(g4,g0)
    c: Distance(g4) = 3
    c: Vertical(g4)
    c: Coincident(g5,g4)
    c: Horizontal(g5)
    c: Coincident(g6,g2)
    c: Coincident(g6,g5)
    c: Vertical(g6)
    c: Horizontal(g7)
    c: Distance(g7) = 105
    c: Coincident(g7,g1)
    c: Block(g3)
    c: Weight(g8) = 1
    c: Equal(g8,g9)
    c: Equal(g8,g10)
    c: InternalAlignment(g8,g11)
    c: InternalAlignment(g9,g11)
    c: InternalAlignment(g10,g11)
    c: InternalAlignment(g12,g11)
    c: InternalAlignment(g13,g11)
    c: Block(g11)
    c: Coincident(g14,g11)
    c: Coincident(g14,g3)
    c: Horizontal(g14)
    c: Block(g15)
    c: Coincident(g16,g15)
    c: Block(g16)
    c: Coincident(g17,g11)
    c: Coincident(g17,g16)
    c: Vertical(g17)
    c: Distance(g17) = 14
    c: Coincident(g18,g7)
    c: Coincident(g18,g15)
    c: Vertical(g18)
    c: Distance(g18) = 19
    c: Coincident(g19,g16)
    c: Coincident(g19,g15)
FEATURE [Sketcher::SketchObject] Sketch065
  FullyConstrained = true
  MapMode = 3
  Placement = pos=(0,0,0) rot=(1,0,0;1.5708rad)
  sketch-geometry (8):
    g0: Circle CenterX=80.351 CenterY=-67.6202 CenterZ=0 NormalX=0 NormalY=0 NormalZ=1 AngleXU=0 Radius=3
    g1: Circle CenterX=80.351 CenterY=-4.92017 CenterZ=0 NormalX=0 NormalY=0 NormalZ=1 AngleXU=0 Radius=3
    g2: Circle CenterX=23.851 CenterY=-4.92017 CenterZ=0 NormalX=0 NormalY=0 NormalZ=1 AngleXU=0 Radius=3
    g3: Circle CenterX=23.851 CenterY=-67.6202 CenterZ=0 NormalX=0 NormalY=0 NormalZ=1 AngleXU=0 Radius=3
    g4: Circle CenterX=23.851 CenterY=-67.6202 CenterZ=0 NormalX=0 NormalY=0 NormalZ=1 AngleXU=0 Radius=5
    g5: Circle CenterX=80.351 CenterY=-67.6202 CenterZ=0 NormalX=0 NormalY=0 NormalZ=1 AngleXU=0 Radius=5
    g6: Circle CenterX=23.851 CenterY=-4.92017 CenterZ=0 NormalX=0 NormalY=0 NormalZ=1 AngleXU=0 Radius=5
    g7: Circle CenterX=80.351 CenterY=-4.92017 CenterZ=0 NormalX=0 NormalY=0 NormalZ=1 AngleXU=0 Radius=5
  constraints (8):
    c: Block(g1)
    c: Block(g0)
    c: Block(g3)
    c: Block(g2)
    c: Block(g5)
    c: Block(g4)
    c: Block(g6)
    c: Block(g7)
FEATURE [Part::Extrusion] Extrude056
  Base = -> Sketch065
  Dir = (0,-1,2e-16)
  DirMode = 2
  FaceMakerClass = Part::FaceMakerBullseye
  LengthFwd = 2
  LengthRev = 0
  Solid = true
  Symmetric = false
FEATURE [Part::Extrusion] Extrude057  label="top025"
  Base = -> Sketch064
  Dir = (0,0,1)
  DirMode = 2
  FaceMakerClass = Part::FaceMakerBullseye
  LengthFwd = 72
  LengthRev = 0
  Solid = true
  Symmetric = false
FEATURE [Sketcher::SketchObject] Sketch066
  FullyConstrained = true
  MapMode = 3
  Placement = pos=(0,0,0) rot=(1,0,0;1.5708rad)
  Support = -> [Extrude057]
  sketch-geometry (8):
    g0: Circle CenterX=80.351 CenterY=-67.6202 CenterZ=0 NormalX=0 NormalY=0 NormalZ=1 AngleXU=0 Radius=3
    g1: Circle CenterX=80.351 CenterY=-4.92017 CenterZ=0 NormalX=0 NormalY=0 NormalZ=1 AngleXU=0 Radius=3
    g2: Circle CenterX=23.851 CenterY=-4.92017 CenterZ=0 NormalX=0 NormalY=0 NormalZ=1 AngleXU=0 Radius=3
    g3: Circle CenterX=23.851 CenterY=-67.6202 CenterZ=0 NormalX=0 NormalY=0 NormalZ=1 AngleXU=0 Radius=3
    g4: Circle CenterX=23.851 CenterY=-67.6202 CenterZ=0 NormalX=0 NormalY=0 NormalZ=1 AngleXU=0 Radius=5
    g5: Circle CenterX=80.351 CenterY=-67.6202 CenterZ=0 NormalX=0 NormalY=0 NormalZ=1 AngleXU=0 Radius=5
    g6: Circle CenterX=23.851 CenterY=-4.92017 CenterZ=0 NormalX=0 NormalY=0 NormalZ=1 AngleXU=0 Radius=5
    g7: Circle CenterX=80.351 CenterY=-4.92017 CenterZ=0 NormalX=0 NormalY=0 NormalZ=1 AngleXU=0 Radius=5
  constraints (8):
    c: Block(g1)
    c: Block(g0)
    c: Block(g3)
    c: Block(g2)
    c: Block(g5)
    c: Block(g4)
    c: Block(g6)
    c: Block(g7)
FEATURE [Part::Extrusion] Extrude055
  Base = -> Sketch066
  Dir = (0,-1,2e-16)
  DirMode = 2
  FaceMakerClass = Part::FaceMakerBullseye
  LengthFwd = 2
  LengthRev = 0
  Solid = true
  Symmetric = false
FEATURE [Part::Fillet] Fillet041
  Base = -> Extrude056
  Edges = 4 edges r=1.99: [Edge6,Edge12,Edge18,Edge24]
FEATURE [Part::Cut] Cut045
  Base = -> Extrude055
  Placement = pos=(0,6,0) rot=(0,0,1;0rad)
  Tool = -> Fillet041
FEATURE [Part::MultiFuse] Fusion095  label="pcbScrewPillars"
  Placement = pos=(-3.2,-1,72.3) rot=(0,0,1;0rad)
  Shapes = -> [Cut045,Extrude054]
FEATURE [Part::Feature] Face113
  shape: bbox 3.2 x 1.5 x 2e-07 mm, 1 faces, 0 solids (baked)
FEATURE [Part::Revolution] Revolve121  label="backCaseScrewRetainer002"
  Angle = 360
  Axis = (0,1,0)
  Base = (0,0,0)
  FaceMakerClass = Part::FaceMakerBullseye
  Placement = pos=(12.5,3,62) rot=(0,0,1;0rad)
  Solid = false
  Source = -> Face113
  Symmetric = false
FEATURE [Part::Feature] Face114
  shape: bbox 3.2 x 1.5 x 2e-07 mm, 1 faces, 0 solids (baked)
FEATURE [Part::Feature] Face115
  shape: bbox 3.2 x 1.5 x 2e-07 mm, 1 faces, 0 solids (baked)
FEATURE [Part::Feature] Face116
  shape: bbox 3.2 x 1.5 x 2e-07 mm, 1 faces, 0 solids (baked)
FEATURE [Part::Revolution] Revolve122  label="frontCaseScrewRetainer004"
  Angle = 360
  Axis = (0,1,0)
  Base = (0,0,0)
  FaceMakerClass = Part::FaceMakerBullseye
  Placement = pos=(89.5,3,68.5) rot=(0,0,1;0rad)
  Solid = false
  Source = -> Face115
  Symmetric = false
FEATURE [Part::Revolution] Revolve123  label="frontCaseScrewRetainer005"
  Angle = 360
  Axis = (0,1,0)
  Base = (0,0,0)
  FaceMakerClass = Part::FaceMakerBullseye
  Placement = pos=(89.5,3,3.5) rot=(0,0,1;0rad)
  Solid = false
  Source = -> Face116
  Symmetric = false
FEATURE [Part::Revolution] Revolve124  label="backCaseScrewRetainer003"
  Angle = 360
  Axis = (0,1,0)
  Base = (0,0,0)
  FaceMakerClass = Part::FaceMakerBullseye
  Placement = pos=(12.5,3,10) rot=(0,0,1;0rad)
  Solid = false
  Source = -> Face114
  Symmetric = false
FEATURE [Part::Feature] Face117
  shape: bbox 3.6 x 3.2 x 2e-07 mm, 1 faces, 0 solids (baked)
FEATURE [Part::Revolution] Revolve125  label="moreFrontCaseScrewRetainer004"
  Angle = 360
  Axis = (0,1,0)
  Base = (0,0,0)
  FaceMakerClass = Part::FaceMakerBullseye
  Placement = pos=(109.5,4.5,68.5) rot=(0,0,1;0rad)
  Solid = false
  Source = -> Face117
  Symmetric = false
FEATURE [Part::Feature] Face118
  shape: bbox 3.6 x 3.2 x 2e-07 mm, 1 faces, 0 solids (baked)
FEATURE [Part::Revolution] Revolve126  label="moreFrontCaseScrewRetainer005"
  Angle = 360
  Axis = (0,1,0)
  Base = (0,0,0)
  FaceMakerClass = Part::FaceMakerBullseye
  Placement = pos=(109.5,4.5,3.5) rot=(0,0,1;0rad)
  Solid = false
  Source = -> Face118
  Symmetric = false
FEATURE [Part::MultiFuse] Fusion096  label="screwRetainers001"
  Shapes = -> [Revolve126,Revolve125,Revolve124,Revolve123,Revolve122,Revolve121]
FEATURE [Part::Feature] Face119
  shape: bbox 10 x 16.5 x 2e-07 mm, 1 faces, 0 solids (baked)
FEATURE [Part::Revolution] Revolve130  label="plugHousing050"
  Angle = 360
  Axis = (0,1,0)
  Base = (0,0,0)
  FaceMakerClass = Part::FaceMakerBullseye
  Placement = pos=(0,0,36.15) rot=(0,0,1;0rad)
  Solid = false
  Source = -> Face119
  Symmetric = false
FEATURE [Part::Feature] Face120
  shape: bbox 10 x 16.5 x 2e-07 mm, 1 faces, 0 solids (baked)
FEATURE [Part::Feature] Face121
  shape: bbox 10 x 16.5 x 2e-07 mm, 1 faces, 0 solids (baked)
FEATURE [Part::Revolution] Revolve127  label="plugHousing047"
  Angle = 360
  Axis = (0,1,0)
  Base = (0,0,0)
  FaceMakerClass = Part::FaceMakerBullseye
  Placement = pos=(0,0,36.15) rot=(0,0,1;0rad)
  Solid = false
  Source = -> Face121
  Symmetric = false
FEATURE [Part::Feature] Face122
  shape: bbox 10 x 16.5 x 2e-07 mm, 1 faces, 0 solids (baked)
FEATURE [Part::Feature] Face123
  shape: bbox 10 x 16.5 x 2e-07 mm, 1 faces, 0 solids (baked)
FEATURE [Part::Revolution] Revolve128  label="plugHousing048"
  Angle = 360
  Axis = (0,1,0)
  Base = (0,0,0)
  FaceMakerClass = Part::FaceMakerBullseye
  Placement = pos=(0,0,36.15) rot=(0,0,1;0rad)
  Solid = false
  Source = -> Face123
  Symmetric = false
FEATURE [Part::MultiFuse] Fusion100  label="plugHousing054"
  Placement = pos=(0,0,0) rot=(0,0,1;1.5708rad)
  Shapes = -> [Revolve130,Revolve128]
FEATURE [Part::Feature] Face124
  shape: bbox 10 x 16.5 x 2e-07 mm, 1 faces, 0 solids (baked)
FEATURE [Part::Feature] Face125
  shape: bbox 10 x 16.5 x 2e-07 mm, 1 faces, 0 solids (baked)
FEATURE [Part::Revolution] Revolve129  label="plugHousing049"
  Angle = 360
  Axis = (0,1,0)
  Base = (0,0,0)
  FaceMakerClass = Part::FaceMakerBullseye
  Placement = pos=(0,0,36.15) rot=(0,0,1;0rad)
  Solid = false
  Source = -> Face125
  Symmetric = false
FEATURE [Part::Feature] Face126
  shape: bbox 10 x 16.5 x 2e-07 mm, 1 faces, 0 solids (baked)
FEATURE [Part::Revolution] Revolve131  label="plugHousing058"
  Angle = 360
  Axis = (0,1,0)
  Base = (0,0,0)
  FaceMakerClass = Part::FaceMakerBullseye
  Placement = pos=(0,0,36.15) rot=(0,0,1;0rad)
  Solid = false
  Source = -> Face120
  Symmetric = false
FEATURE [Part::MultiFuse] Fusion099  label="plugHousing053"
  Placement = pos=(0,0,0) rot=(0,0,1;1.5708rad)
  Shapes = -> [Revolve127,Revolve131]
FEATURE [Part::MultiFuse] Fusion102  label="plugHousing056"
  Placement = pos=(0,19,0) rot=(0,0,1;3.14159rad)
  Shapes = -> [Fusion100,Fusion099]
FEATURE [Part::Revolution] Revolve132  label="plugHousing059"
  Angle = 360
  Axis = (0,1,0)
  Base = (0,0,0)
  FaceMakerClass = Part::FaceMakerBullseye
  Placement = pos=(0,0,36.15) rot=(0,0,1;0rad)
  Solid = false
  Source = -> Face126
  Symmetric = false
FEATURE [Part::Revolution] Revolve133  label="plugHousing060"
  Angle = 360
  Axis = (0,1,0)
  Base = (0,0,0)
  FaceMakerClass = Part::FaceMakerBullseye
  Placement = pos=(0,0,36.15) rot=(0,0,1;0rad)
  Solid = false
  Source = -> Face122
  Symmetric = false
FEATURE [Part::MultiFuse] Fusion097  label="plugHousing051"
  Placement = pos=(0,0,0) rot=(0,0,1;1.5708rad)
  Shapes = -> [Revolve133,Revolve132]
FEATURE [Part::Revolution] Revolve134  label="plugHousing061"
  Angle = 360
  Axis = (0,1,0)
  Base = (0,0,0)
  FaceMakerClass = Part::FaceMakerBullseye
  Placement = pos=(0,0,36.15) rot=(0,0,1;0rad)
  Solid = false
  Source = -> Face124
  Symmetric = false
FEATURE [Part::MultiFuse] Fusion101  label="plugHousing055"
  Placement = pos=(0,0,0) rot=(0,0,1;1.5708rad)
  Shapes = -> [Revolve129,Revolve134]
FEATURE [Part::MultiFuse] Fusion098  label="plugHousing052"
  Placement = pos=(0,19,0) rot=(0,0,1;3.14159rad)
  Shapes = -> [Fusion097,Fusion101]
FEATURE [Part::MultiFuse] Fusion103  label="plugHousing057"
  Placement = pos=(122.621,0,-0.15) rot=(0,0,1;0rad)
  Shapes = -> [Fusion102,Fusion098]
FEATURE [Part::Box] Box028  label="Cube015"
  AttacherType = Attacher::AttachEngine3D
  Height = 28
  Length = 3
  Placement = pos=(110.7,19,22) rot=(0,0,1;0rad)
  Width = 15.7
FEATURE [Part::Cylinder] Cylinder044
  Angle = 360
  AttacherType = Attacher::AttachEngine3D
  Height = 20
  Placement = pos=(0,0,36.15) rot=(0,0,1;0rad)
  Radius = 10.3
FEATURE [Part::Cylinder] Cylinder045
  Angle = 360
  AttacherType = Attacher::AttachEngine3D
  Height = 10
  Placement = pos=(0,0,36.15) rot=(0,0,1;0rad)
  Radius = 4
FEATURE [Part::MultiFuse] Fusion104  label="removeToCreteHoleForPlugHousing040"
  Placement = pos=(70,19,36) rot=(0,1,0;1.5708rad)
  Shapes = -> [Cylinder044,Cylinder045]
FEATURE [Part::Cut] Cut046  label="plugHousingTab003"
  Base = -> Box028
  Tool = -> Fusion104
FEATURE [Part::MultiFuse] Fusion105  label="plugHousing062"
  Shapes = -> [Fusion103,Cut046]
FEATURE [Part::Fillet] Fillet042
  Base = -> Fusion105
  Edges = 1 edges r=2: [Edge25]
FEATURE [Part::Fillet] Fillet043  label="plugHousing063"
  Base = -> Fillet042
  Edges = 1 edges r=2: [Edge8]
  Placement = pos=(7,0,0) rot=(0,0,1;0rad)
FEATURE [Part::Feature] Face127
  shape: bbox 10 x 16.5 x 2e-07 mm, 1 faces, 0 solids (baked)
FEATURE [Part::Feature] Face128
  shape: bbox 10 x 16.5 x 2e-07 mm, 1 faces, 0 solids (baked)
FEATURE [Part::Revolution] Revolve137  label="plugHousing070"
  Angle = 360
  Axis = (0,1,0)
  Base = (0,0,0)
  FaceMakerClass = Part::FaceMakerBullseye
  Placement = pos=(0,0,36.15) rot=(0,0,1;0rad)
  Solid = false
  Source = -> Face127
  Symmetric = false
FEATURE [Part::Revolution] Revolve140  label="plugHousing073"
  Angle = 360
  Axis = (0,1,0)
  Base = (0,0,0)
  FaceMakerClass = Part::FaceMakerBullseye
  Placement = pos=(0,0,36.15) rot=(0,0,1;0rad)
  Solid = false
  Source = -> Face128
  Symmetric = false
FEATURE [Part::Feature] Face129
  shape: bbox 10 x 16.5 x 2e-07 mm, 1 faces, 0 solids (baked)
FEATURE [Part::Revolution] Revolve138  label="plugHousing071"
  Angle = 360
  Axis = (0,1,0)
  Base = (0,0,0)
  FaceMakerClass = Part::FaceMakerBullseye
  Placement = pos=(0,0,36.15) rot=(0,0,1;0rad)
  Solid = false
  Source = -> Face129
  Symmetric = false
FEATURE [Part::Feature] Face130
  shape: bbox 10 x 16.5 x 2e-07 mm, 1 faces, 0 solids (baked)
FEATURE [Part::Revolution] Revolve139  label="plugHousing072"
  Angle = 360
  Axis = (0,1,0)
  Base = (0,0,0)
  FaceMakerClass = Part::FaceMakerBullseye
  Placement = pos=(0,0,36.15) rot=(0,0,1;0rad)
  Solid = false
  Source = -> Face130
  Symmetric = false
FEATURE [Part::Feature] Face131
  shape: bbox 10 x 16.5 x 2e-07 mm, 1 faces, 0 solids (baked)
FEATURE [Part::Revolution] Revolve135  label="plugHousing068"
  Angle = 360
  Axis = (0,1,0)
  Base = (0,0,0)
  FaceMakerClass = Part::FaceMakerBullseye
  Placement = pos=(0,0,36.15) rot=(0,0,1;0rad)
  Solid = false
  Source = -> Face131
  Symmetric = false
FEATURE [Part::MultiFuse] Fusion112  label="plugHousing078"
  Placement = pos=(0,0,0) rot=(0,0,1;1.5708rad)
  Shapes = -> [Revolve135,Revolve139]
FEATURE [Part::Feature] Face132
  shape: bbox 10 x 16.5 x 2e-07 mm, 1 faces, 0 solids (baked)
FEATURE [Part::Revolution] Revolve141  label="plugHousing074"
  Angle = 360
  Axis = (0,1,0)
  Base = (0,0,0)
  FaceMakerClass = Part::FaceMakerBullseye
  Placement = pos=(0,0,36.15) rot=(0,0,1;0rad)
  Solid = false
  Source = -> Face132
  Symmetric = false
FEATURE [Part::MultiFuse] Fusion110  label="plugHousing076"
  Placement = pos=(0,0,0) rot=(0,0,1;1.5708rad)
  Shapes = -> [Revolve141,Revolve140]
FEATURE [Part::Feature] Face133
  shape: bbox 10 x 16.5 x 2e-07 mm, 1 faces, 0 solids (baked)
FEATURE [Part::Revolution] Revolve136  label="plugHousing069"
  Angle = 360
  Axis = (0,1,0)
  Base = (0,0,0)
  FaceMakerClass = Part::FaceMakerBullseye
  Placement = pos=(0,0,36.15) rot=(0,0,1;0rad)
  Solid = false
  Source = -> Face133
  Symmetric = false
FEATURE [Part::MultiFuse] Fusion106  label="plugHousing064"
  Placement = pos=(0,0,0) rot=(0,0,1;1.5708rad)
  Shapes = -> [Revolve138,Revolve136]
FEATURE [Part::MultiFuse] Fusion108  label="plugHousing066"
  Placement = pos=(0,19,0) rot=(0,0,1;3.14159rad)
  Shapes = -> [Fusion106,Fusion112]
FEATURE [Part::Feature] Face134
  shape: bbox 10 x 16.5 x 2e-07 mm, 1 faces, 0 solids (baked)
FEATURE [Part::Revolution] Revolve142  label="plugHousing075"
  Angle = 360
  Axis = (0,1,0)
  Base = (0,0,0)
  FaceMakerClass = Part::FaceMakerBullseye
  Placement = pos=(0,0,36.15) rot=(0,0,1;0rad)
  Solid = false
  Source = -> Face134
  Symmetric = false
FEATURE [Part::MultiFuse] Fusion107  label="plugHousing065"
  Placement = pos=(0,0,0) rot=(0,0,1;1.5708rad)
  Shapes = -> [Revolve137,Revolve142]
FEATURE [Part::MultiFuse] Fusion111  label="plugHousing077"
  Placement = pos=(0,19,0) rot=(0,0,1;3.14159rad)
  Shapes = -> [Fusion110,Fusion107]
FEATURE [Part::MultiFuse] Fusion109  label="plugHousing067"
  Placement = pos=(131.236,0,-0.15) rot=(0,0,1;0rad)
  Shapes = -> [Fusion108,Fusion111]
FEATURE [Part::MultiFuse] Fusion113  label="plugHousing079"
  Shapes = -> [Fillet043,Fusion109]
FEATURE [Part::Feature] Face135
  shape: bbox 3.5 x 17.8 x 2e-07 mm, 1 faces, 0 solids (baked)
FEATURE [Part::Revolution] Revolve143  label="removeToCreateScrewAndThreadedInsertHole049"
  Angle = 360
  Axis = (0,1,0)
  Base = (0,0,0)
  FaceMakerClass = Part::FaceMakerBullseye
  Placement = pos=(12.5,0,10) rot=(0,0,1;0rad)
  Solid = false
  Source = -> Face135
  Symmetric = false
FEATURE [Part::Feature] Face136
  shape: bbox 3.5 x 17.8 x 2e-07 mm, 1 faces, 0 solids (baked)
FEATURE [Part::Revolution] Revolve144  label="removeToCreateScrewAndThreadedInsertHole050"
  Angle = 360
  Axis = (0,1,0)
  Base = (0,0,0)
  FaceMakerClass = Part::FaceMakerBullseye
  Placement = pos=(12.5,0,62) rot=(0,0,1;0rad)
  Solid = false
  Source = -> Face136
  Symmetric = false
FEATURE [Part::Feature] Face137
  shape: bbox 3.5 x 17.8 x 2e-07 mm, 1 faces, 0 solids (baked)
FEATURE [Part::Revolution] Revolve145  label="removeToCreateScrewAndThreadedInsertHole051"
  Angle = 360
  Axis = (0,1,0)
  Base = (0,0,0)
  FaceMakerClass = Part::FaceMakerBullseye
  Placement = pos=(89.5,0,68.5) rot=(0,0,1;0rad)
  Solid = false
  Source = -> Face137
  Symmetric = false
FEATURE [Part::Feature] Face138
  shape: bbox 3.5 x 17.8 x 2e-07 mm, 1 faces, 0 solids (baked)
FEATURE [Part::Revolution] Revolve146  label="removeToCreateScrewAndThreadedInsertHole052"
  Angle = 360
  Axis = (0,1,0)
  Base = (0,0,0)
  FaceMakerClass = Part::FaceMakerBullseye
  Placement = pos=(89.5,0,3.5) rot=(0,0,1;0rad)
  Solid = false
  Source = -> Face138
  Symmetric = false
FEATURE [Part::Feature] Face139
  shape: bbox 3.5 x 17.8 x 2e-07 mm, 1 faces, 0 solids (baked)
FEATURE [Part::Revolution] Revolve147  label="removeToCreateScrewAndThreadedInsertHole053"
  Angle = 360
  Axis = (0,1,0)
  Base = (0,0,0)
  FaceMakerClass = Part::FaceMakerBullseye
  Placement = pos=(109.5,4.7,3.5) rot=(0,0,1;0rad)
  Solid = false
  Source = -> Face139
  Symmetric = false
FEATURE [Part::Feature] Face140
  shape: bbox 3.5 x 17.8 x 2e-07 mm, 1 faces, 0 solids (baked)
FEATURE [Part::Revolution] Revolve148  label="removeToCreateScrewAndThreadedInsertHole054"
  Angle = 360
  Axis = (0,1,0)
  Base = (0,0,0)
  FaceMakerClass = Part::FaceMakerBullseye
  Placement = pos=(109.5,4.7,68.5) rot=(0,0,1;0rad)
  Solid = false
  Source = -> Face140
  Symmetric = false
FEATURE [Part::MultiFuse] Fusion114  label="removeToCreateScrewAndThreadedInsertHole055"
  Shapes = -> [Revolve148,Revolve147,Revolve146,Revolve145,Revolve144,Revolve143]
FEATURE [Part::Cut] Cut047  label="casePillars004"
  Base = -> Cut037
  Tool = -> Fusion114
FEATURE [Part::Feature] Face141
  shape: bbox 3.5 x 17.8 x 2e-07 mm, 1 faces, 0 solids (baked)
FEATURE [Part::Feature] Face142
  shape: bbox 3.5 x 17.8 x 2e-07 mm, 1 faces, 0 solids (baked)
FEATURE [Part::Feature] Face143
  shape: bbox 3.5 x 17.8 x 2e-07 mm, 1 faces, 0 solids (baked)
FEATURE [Part::Revolution] Revolve149  label="removeToCreateScrewAndThreadedInsertHole057"
  Angle = 360
  Axis = (0,1,0)
  Base = (0,0,0)
  FaceMakerClass = Part::FaceMakerBullseye
  Placement = pos=(12.5,0,10) rot=(0,0,1;0rad)
  Solid = false
  Source = -> Face141
  Symmetric = false
FEATURE [Part::Feature] Face144
  shape: bbox 3.5 x 17.8 x 2e-07 mm, 1 faces, 0 solids (baked)
FEATURE [Part::Feature] Face145
  shape: bbox 3.5 x 17.8 x 2e-07 mm, 1 faces, 0 solids (baked)
FEATURE [Part::Feature] Face146
  shape: bbox 3.5 x 17.8 x 2e-07 mm, 1 faces, 0 solids (baked)
FEATURE [Part::Revolution] Revolve150  label="removeToCreateScrewAndThreadedInsertHole058"
  Angle = 360
  Axis = (0,1,0)
  Base = (0,0,0)
  FaceMakerClass = Part::FaceMakerBullseye
  Placement = pos=(12.5,0,62) rot=(0,0,1;0rad)
  Solid = false
  Source = -> Face146
  Symmetric = false
FEATURE [Part::Revolution] Revolve151  label="removeToCreateScrewAndThreadedInsertHole059"
  Angle = 360
  Axis = (0,1,0)
  Base = (0,0,0)
  FaceMakerClass = Part::FaceMakerBullseye
  Placement = pos=(89.5,0,68.5) rot=(0,0,1;0rad)
  Solid = false
  Source = -> Face143
  Symmetric = false
FEATURE [Part::Revolution] Revolve152  label="removeToCreateScrewAndThreadedInsertHole060"
  Angle = 360
  Axis = (0,1,0)
  Base = (0,0,0)
  FaceMakerClass = Part::FaceMakerBullseye
  Placement = pos=(89.5,0,3.5) rot=(0,0,1;0rad)
  Solid = false
  Source = -> Face142
  Symmetric = false
FEATURE [Part::Revolution] Revolve153  label="removeToCreateScrewAndThreadedInsertHole061"
  Angle = 360
  Axis = (0,1,0)
  Base = (0,0,0)
  FaceMakerClass = Part::FaceMakerBullseye
  Placement = pos=(109.5,4.7,3.5) rot=(0,0,1;0rad)
  Solid = false
  Source = -> Face145
  Symmetric = false
FEATURE [Part::Revolution] Revolve154  label="removeToCreateScrewAndThreadedInsertHole062"
  Angle = 360
  Axis = (0,1,0)
  Base = (0,0,0)
  FaceMakerClass = Part::FaceMakerBullseye
  Placement = pos=(109.5,4.7,68.5) rot=(0,0,1;0rad)
  Solid = false
  Source = -> Face144
  Symmetric = false
FEATURE [Part::MultiFuse] Fusion115  label="removeToCreateScrewAndThreadedInsertHole056"
  Shapes = -> [Revolve154,Revolve153,Revolve152,Revolve151,Revolve150,Revolve149]
FEATURE [Part::Feature] Face147
  shape: bbox 9.8 x 26.5 x 2e-07 mm, 1 faces, 0 solids (baked)
FEATURE [Part::Revolution] Revolve155
  Angle = 360
  Axis = (0,1,0)
  Base = (0,0,0)
  FaceMakerClass = Part::FaceMakerBullseye
  Placement = pos=(0,0,0) rot=(0,0,1;1.5708rad)
  Solid = false
  Source = -> Face147
  Symmetric = false
FEATURE [Part::Feature] Face148
  shape: bbox 9.8 x 26.5 x 2e-07 mm, 1 faces, 0 solids (baked)
FEATURE [Part::Revolution] Revolve156
  Angle = 360
  Axis = (0,1,0)
  Base = (0,0,0)
  FaceMakerClass = Part::FaceMakerBullseye
  Placement = pos=(0,0,0) rot=(0,0,1;1.5708rad)
  Solid = false
  Source = -> Face148
  Symmetric = false
FEATURE [Part::MultiFuse] Fusion116
  Placement = pos=(-18,19,36) rot=(0,0,1;0rad)
  Shapes = -> [Revolve156,Revolve155]
FEATURE [Part::Box] Box029  label="Cube016"
  AttacherType = Attacher::AttachEngine3D
  Height = 28
  Length = 3
  Placement = pos=(110.7,19,22) rot=(0,0,1;0rad)
  Width = 15.7
FEATURE [Part::Cylinder] Cylinder046
  Angle = 360
  AttacherType = Attacher::AttachEngine3D
  Height = 10
  Placement = pos=(0,0,36.15) rot=(0,0,1;0rad)
  Radius = 4
FEATURE [Part::Cylinder] Cylinder047
  Angle = 360
  AttacherType = Attacher::AttachEngine3D
  Height = 20
  Placement = pos=(0,0,36.15) rot=(0,0,1;0rad)
  Radius = 10.3
FEATURE [Part::MultiFuse] Fusion117  label="removeToCreteHoleForPlugHousing041"
  Placement = pos=(70,19,36) rot=(0,1,0;1.5708rad)
  Shapes = -> [Cylinder047,Cylinder046]
FEATURE [Part::Cut] Cut049  label="plugHousingTab004"
  Base = -> Box029
  Placement = pos=(-107.4,-14,0) rot=(0,0,1;0rad)
  Tool = -> Fusion117
FEATURE [Part::Box] Box030  label="Cube017"
  AttacherType = Attacher::AttachEngine3D
  Height = 28
  Length = 3
  Placement = pos=(110.7,19,22) rot=(0,0,1;0rad)
  Width = 15.7
FEATURE [Part::Cylinder] Cylinder048
  Angle = 360
  AttacherType = Attacher::AttachEngine3D
  Height = 10
  Placement = pos=(0,0,36.15) rot=(0,0,1;0rad)
  Radius = 4
FEATURE [Part::Cylinder] Cylinder049
  Angle = 360
  AttacherType = Attacher::AttachEngine3D
  Height = 20
  Placement = pos=(0,0,36.15) rot=(0,0,1;0rad)
  Radius = 10.3
FEATURE [Part::MultiFuse] Fusion118  label="removeToCreteHoleForPlugHousing042"
  Placement = pos=(70,19,36) rot=(0,1,0;1.5708rad)
  Shapes = -> [Cylinder049,Cylinder048]
FEATURE [Part::Cut] Cut050  label="plugHousingTab005"
  Base = -> Box030
  Placement = pos=(-107.4,-14,0) rot=(0,0,1;0rad)
  Tool = -> Fusion118
FEATURE [Part::MultiFuse] Fusion119
  Placement = pos=(9.6,23,0) rot=(0,0,1;3.14159rad)
  Shapes = -> [Cut049,Cut050]
FEATURE [Part::Box] Box031  label="Cube018"
  AttacherType = Attacher::AttachEngine3D
  Height = 10
  Length = 3
  Placement = pos=(3.3,4,12) rot=(0,0,1;0rad)
  Width = 10
FEATURE [Part::Fillet] Fillet044
  Base = -> Box031
  Edges = 1 edges r=2: [Edge11]
FEATURE [Part::Box] Box032  label="Cube019"
  AttacherType = Attacher::AttachEngine3D
  Height = 10
  Length = 3
  Placement = pos=(3.3,4,50) rot=(0,0,1;0rad)
  Width = 10
FEATURE [Part::Fillet] Fillet045
  Base = -> Box032
  Edges = 1 edges r=2: [Edge12]
FEATURE [Part::Box] Box033  label="Cube020"
  AttacherType = Attacher::AttachEngine3D
  Height = 28
  Length = 4
  Placement = pos=(5,0,22) rot=(0,0,1;0rad)
  Width = 10
FEATURE [Part::Fillet] Fillet046
  Base = -> Box033
  Edges = 1 edges r=1: [Edge7]
FEATURE [Part::Fillet] Fillet047
  Base = -> Fillet046
  Edges = 1 edges r=2: [Edge5]
FEATURE [Part::Fillet] Fillet048
  Base = -> Fillet047
  Edges = 1 edges r=2: [Edge2]
FEATURE [Part::Cylinder] Cylinder050
  Angle = 360
  AttacherType = Attacher::AttachEngine3D
  Height = 20
  Placement = pos=(0,0,36.15) rot=(0,0,1;0rad)
  Radius = 8.2
FEATURE [Part::Cylinder] Cylinder051
  Angle = 360
  AttacherType = Attacher::AttachEngine3D
  Height = 10
  Placement = pos=(0,0,36.15) rot=(0,0,1;0rad)
  Radius = 4
FEATURE [Part::MultiFuse] Fusion120  label="removeToCreteHoleForPlugHousing043"
  Placement = pos=(-42,19,36) rot=(0,1,0;1.5708rad)
  Shapes = -> [Cylinder050,Cylinder051]
FEATURE [Sketcher::SketchObject] Sketch067  label="topSketch018"
  FullyConstrained = true
  sketch-geometry (4):
    g0: LineSegment StartX=16.8446 StartY=31.512 StartZ=0 EndX=16.3251 EndY=34.4666 EndZ=0
    g1: ArcOfCircle CenterX=19 CenterY=19.2524 CenterZ=0 NormalX=0 NormalY=0 NormalZ=1 AngleXU=0 Radius=15.4476 StartAngle=1.74483 EndAngle=2.72717
    g2: ArcOfCircle CenterX=19 CenterY=19.2524 CenterZ=0 NormalX=0 NormalY=0 NormalZ=1 AngleXU=0 Radius=12.4476 StartAngle=1.74483 EndAngle=2.73189
    g3: LineSegment StartX=4.86004 StartY=25.4725 StartZ=0 EndX=7.58253 EndY=24.2107 EndZ=0
  constraints (7):
    c: Block(g0)
    c: Coincident(g1,g0)
    c: Coincident(g2,g0)
    c: Coincident(g3,g1)
    c: Coincident(g3,g2)
    c: Block(g1)
    c: Block(g2)
FEATURE [Part::Extrusion] Extrude058
  Base = -> Sketch067
  Dir = (0,0,1)
  DirMode = 2
  FaceMakerClass = Part::FaceMakerBullseye
  LengthFwd = 10
  LengthRev = 0
  Placement = pos=(0,0,31) rot=(0,0,1;0rad)
  Solid = true
  Symmetric = false
FEATURE [Part::Cut] Cut051
  Base = -> Extrude058
  Tool = -> Fusion120
FEATURE [Part::Fillet] Fillet049
  Base = -> Cut051
  Edges = 1 edges r=2: [Edge1]
FEATURE [Part::Fillet] Fillet050
  Base = -> Fillet049
  Edges = 1 edges r=2.5: [Edge1]
FEATURE [Part::Fillet] Fillet051
  Base = -> Fillet050
  Edges = 1 edges r=2.5: [Edge2]
FEATURE [Part::MultiFuse] Fusion121  label="wireHolder003"
  Shapes = -> [Fusion116,Fillet051]
FEATURE [Part::MultiFuse] Fusion122
  Shapes = -> [Fillet045,Fusion121]
FEATURE [Part::MultiFuse] Fusion123  label="wireHolder004"
  Shapes = -> [Fusion122,Fillet048]
FEATURE [Part::MultiFuse] Fusion124  label="wireHolder005"
  Shapes = -> [Fillet044,Fusion119,Fusion123]
FEATURE [Sketcher::SketchObject] Sketch068  label="topSketch019"
  FullyConstrained = true
  sketch-geometry (6):
    g0: LineSegment StartX=19 StartY=38 StartZ=0 EndX=117 EndY=38 EndZ=0
    g1: ArcOfCircle CenterX=19 CenterY=19 CenterZ=0 NormalX=0 NormalY=0 NormalZ=1 AngleXU=0 Radius=19 StartAngle=1.5708 EndAngle=3.14159
    g2: LineSegment StartX=117 StartY=38 StartZ=0 EndX=117 EndY=19 EndZ=0
    g3: LineSegment StartX=98 StartY=1.0161e-12 StartZ=0 EndX=5.22862e-06 EndY=1.0161e-12 EndZ=0
    g4: LineSegment StartX=5.22862e-06 StartY=19 StartZ=0 EndX=5.22862e-06 EndY=1.0161e-12 EndZ=0
    g5: ArcOfCircle CenterX=98 CenterY=19 CenterZ=0 NormalX=0 NormalY=0 NormalZ=1 AngleXU=0 Radius=19 StartAngle=4.71239 EndAngle=6.28319
  constraints (16):
    c: Horizontal(g0)
    c: Distance(g0) = 98
    c: Coincident(g1,g0)
    c: Block(g1)
    c: Coincident(g2,g0)
    c: Vertical(g2)
    c: Distance(g2) = 19
    c: Horizontal(g3)
    c: Coincident(g4,g1)
    c: Vertical(g4)
    c: Coincident(g3,g4)
    c: Block(g3)
    c: Coincident(g5,g2)
    c: Coincident(g5,g3)
    c: Block(g0)
    c: Block(g5)
FEATURE [Part::Extrusion] Extrude059  label="sideA002"
  Base = -> Sketch068
  Dir = (0,0,1)
  DirMode = 2
  FaceMakerClass = Part::FaceMakerBullseye
  LengthFwd = 3
  LengthRev = 0
  Placement = pos=(0,0,-2.7) rot=(0,0,1;0rad)
  Solid = true
  Symmetric = false
FEATURE [Sketcher::SketchObject] Sketch069  label="topSketch020"
  FullyConstrained = true
  sketch-geometry (6):
    g0: LineSegment StartX=19 StartY=38 StartZ=0 EndX=117 EndY=38 EndZ=0
    g1: ArcOfCircle CenterX=19 CenterY=19 CenterZ=0 NormalX=0 NormalY=0 NormalZ=1 AngleXU=0 Radius=19 StartAngle=1.5708 EndAngle=3.14159
    g2: LineSegment StartX=117 StartY=38 StartZ=0 EndX=117 EndY=19 EndZ=0
    g3: LineSegment StartX=98 StartY=1.0161e-12 StartZ=0 EndX=5.22862e-06 EndY=1.0161e-12 EndZ=0
    g4: LineSegment StartX=5.22862e-06 StartY=19 StartZ=0 EndX=5.22862e-06 EndY=1.0161e-12 EndZ=0
    g5: ArcOfCircle CenterX=98 CenterY=19 CenterZ=0 NormalX=0 NormalY=0 NormalZ=1 AngleXU=0 Radius=19 StartAngle=4.71239 EndAngle=6.28319
  constraints (16):
    c: Horizontal(g0)
    c: Distance(g0) = 98
    c: Coincident(g1,g0)
    c: Block(g1)
    c: Coincident(g2,g0)
    c: Vertical(g2)
    c: Distance(g2) = 19
    c: Horizontal(g3)
    c: Coincident(g4,g1)
    c: Vertical(g4)
    c: Coincident(g3,g4)
    c: Block(g3)
    c: Coincident(g5,g2)
    c: Coincident(g5,g3)
    c: Block(g0)
    c: Block(g5)
FEATURE [Part::Extrusion] Extrude060  label="sideB002"
  Base = -> Sketch069
  Dir = (0,0,1)
  DirMode = 2
  FaceMakerClass = Part::FaceMakerBullseye
  LengthFwd = 3
  LengthRev = 0
  Placement = pos=(0,0,71.7) rot=(0,0,1;0rad)
  Solid = true
  Symmetric = false
FEATURE [Part::MultiFuse] Fusion127  label="removeFromBottom001"
  Placement = pos=(2,0,0) rot=(0,0,1;0rad)
  Shapes = -> [Extrude059,Extrude060]
FEATURE [Part::Cylinder] Cylinder052
  Angle = 360
  AttacherType = Attacher::AttachEngine3D
  Height = 20
  Placement = pos=(0,0,36.15) rot=(0,0,1;0rad)
  Radius = 14
FEATURE [Part::Cylinder] Cylinder053
  Angle = 360
  AttacherType = Attacher::AttachEngine3D
  Height = 10
  Placement = pos=(0,0,36.15) rot=(0,0,1;0rad)
  Radius = 4
FEATURE [Part::MultiFuse] Fusion128  label="removeToCreteHoleForPlugHousing044"
  Placement = pos=(70,19,36) rot=(0,1,0;1.5708rad)
  Shapes = -> [Cylinder052,Cylinder053]
FEATURE [Part::Cut] Cut052  label="bottom011"
  Base = -> Extrude043
  Tool = -> Fusion128
FEATURE [Part::Cut] Cut054  label="bottom012"
  Base = -> Cut052
  Tool = -> Fusion115
FEATURE [Sketcher::SketchObject] Sketch070
  FullyConstrained = true
  Placement = pos=(117,19,0) rot=(0.57735,0.57735,0.57735;2.0944rad)
  sketch-geometry (48):
    g0: LineSegment StartX=-49.19 StartY=69.25 StartZ=0 EndX=-49.19 EndY=66.25 EndZ=0
    g1: LineSegment StartX=-49.19 StartY=63.5 StartZ=0 EndX=-49.19 EndY=60.5 EndZ=0
    g2: LineSegment StartX=-49.19 StartY=57.75 StartZ=0 EndX=-49.19 EndY=54.75 EndZ=0
    g3: LineSegment StartX=-49.19 StartY=52 StartZ=0 EndX=-49.19 EndY=49 EndZ=0
    g4: LineSegment StartX=-49.19 StartY=46.25 StartZ=0 EndX=-49.19 EndY=43.25 EndZ=0
    g5: LineSegment StartX=-49.19 StartY=40.5 StartZ=0 EndX=-49.19 EndY=37.5 EndZ=0
    g6: LineSegment StartX=-49.19 StartY=34.5 StartZ=0 EndX=-49.19 EndY=31.5 EndZ=0
    g7: LineSegment StartX=-49.19 StartY=28.75 StartZ=0 EndX=-49.19 EndY=25.75 EndZ=0
    g8: LineSegment StartX=-49.19 StartY=23 StartZ=0 EndX=-49.19 EndY=20 EndZ=0
    g9: LineSegment StartX=-49.19 StartY=17.25 StartZ=0 EndX=-49.19 EndY=14.25 EndZ=0
    g10: LineSegment StartX=-49.19 StartY=11.5 StartZ=0 EndX=-49.19 EndY=8.5 EndZ=0
    g11: LineSegment StartX=-49.19 StartY=5.75 StartZ=0 EndX=-49.19 EndY=2.75 EndZ=0
    g12: ArcOfCircle CenterX=-1.5 CenterY=67.75 CenterZ=0 NormalX=0 NormalY=0 NormalZ=1 AngleXU=0 Radius=1.5 StartAngle=4.71239 EndAngle=7.85398
    g13: ArcOfCircle CenterX=-1.5 CenterY=62 CenterZ=0 NormalX=0 NormalY=0 NormalZ=1 AngleXU=0 Radius=1.5 StartAngle=4.71239 EndAngle=7.85398
    g14: ArcOfCircle CenterX=-1.5 CenterY=56.25 CenterZ=0 NormalX=0 NormalY=0 NormalZ=1 AngleXU=0 Radius=1.5 StartAngle=4.71239 EndAngle=7.85398
    g15: ArcOfCircle CenterX=-11.49 CenterY=50.5 CenterZ=0 NormalX=0 NormalY=0 NormalZ=1 AngleXU=0 Radius=1.5 StartAngle=4.71239 EndAngle=7.85398
    g16: ArcOfCircle CenterX=-16.28 CenterY=44.75 CenterZ=0 NormalX=0 NormalY=0 NormalZ=1 AngleXU=0 Radius=1.5 StartAngle=4.71239 EndAngle=7.85398
    g17: ArcOfCircle CenterX=-18.2337 CenterY=39 CenterZ=0 NormalX=0 NormalY=0 NormalZ=1 AngleXU=0 Radius=1.5 StartAngle=4.71485 EndAngle=7.85398
    g18: ArcOfCircle CenterX=-16.2837 CenterY=27.25 CenterZ=0 NormalX=0 NormalY=0 NormalZ=1 AngleXU=0 Radius=1.5 StartAngle=4.71485 EndAngle=7.85398
    g19: ArcOfCircle CenterX=-18.2337 CenterY=33 CenterZ=0 NormalX=0 NormalY=0 NormalZ=1 AngleXU=0 Radius=1.5 StartAngle=4.71485 EndAngle=7.85398
    g20: ArcOfCircle CenterX=-11.49 CenterY=21.5 CenterZ=0 NormalX=0 NormalY=0 NormalZ=1 AngleXU=0 Radius=1.5 StartAngle=4.71239 EndAngle=7.85398
    g21: ArcOfCircle CenterX=-1.5 CenterY=4.25 CenterZ=0 NormalX=0 NormalY=0 NormalZ=1 AngleXU=0 Radius=1.5 StartAngle=4.71239 EndAngle=7.85398
    g22: ArcOfCircle CenterX=-1.5 CenterY=10 CenterZ=0 NormalX=0 NormalY=0 NormalZ=1 AngleXU=0 Radius=1.5 StartAngle=4.71239 EndAngle=7.85398
    g23: ArcOfCircle CenterX=-1.5 CenterY=15.75 CenterZ=0 NormalX=0 NormalY=0 NormalZ=1 AngleXU=0 Radius=1.5 StartAngle=4.71239 EndAngle=7.85398
    g24: LineSegment StartX=-49.19 StartY=69.25 StartZ=0 EndX=-1.5 EndY=69.25 EndZ=0
    g25: LineSegment StartX=-49.19 StartY=66.25 StartZ=0 EndX=-1.5 EndY=66.25 EndZ=0
    g26: LineSegment StartX=-49.19 StartY=63.5 StartZ=0 EndX=-1.5 EndY=63.5 EndZ=0
    g27: LineSegment StartX=-49.19 StartY=60.5 StartZ=0 EndX=-1.5 EndY=60.5 EndZ=0
    g28: LineSegment StartX=-49.19 StartY=57.75 StartZ=0 EndX=-1.5 EndY=57.75 EndZ=0
    g29: LineSegment StartX=-49.19 StartY=54.75 StartZ=0 EndX=-1.5 EndY=54.75 EndZ=0
    g30: LineSegment StartX=-49.19 StartY=52 StartZ=0 EndX=-11.49 EndY=52 EndZ=0
    g31: LineSegment StartX=-49.19 StartY=49 StartZ=0 EndX=-11.49 EndY=49 EndZ=0
    g32: LineSegment StartX=-49.19 StartY=46.25 StartZ=0 EndX=-16.28 EndY=46.25 EndZ=0
    g33: LineSegment StartX=-49.19 StartY=43.25 StartZ=0 EndX=-16.28 EndY=43.25 EndZ=0
    g34: LineSegment StartX=-49.19 StartY=40.5 StartZ=0 EndX=-18.2337 EndY=40.5 EndZ=0
    g35: LineSegment StartX=-49.19 StartY=37.5 StartZ=0 EndX=-18.23 EndY=37.5 EndZ=0
    g36: LineSegment StartX=-49.19 StartY=34.5 StartZ=0 EndX=-18.2337 EndY=34.5 EndZ=0
    g37: LineSegment StartX=-49.19 StartY=31.5 StartZ=0 EndX=-18.23 EndY=31.5 EndZ=0
    g38: LineSegment StartX=-49.19 StartY=28.75 StartZ=0 EndX=-16.2837 EndY=28.75 EndZ=0
    g39: LineSegment StartX=-49.19 StartY=25.75 StartZ=0 EndX=-16.28 EndY=25.75 EndZ=0
    g40: LineSegment StartX=-49.19 StartY=23 StartZ=0 EndX=-11.49 EndY=23 EndZ=0
    g41: LineSegment StartX=-49.19 StartY=20 StartZ=0 EndX=-11.49 EndY=20 EndZ=0
    g42: LineSegment StartX=-49.19 StartY=17.25 StartZ=0 EndX=-1.5 EndY=17.25 EndZ=0
    g43: LineSegment StartX=-49.19 StartY=14.25 StartZ=0 EndX=-1.5 EndY=14.25 EndZ=0
    g44: LineSegment StartX=-49.19 StartY=11.5 StartZ=0 EndX=-1.5 EndY=11.5 EndZ=0
    g45: LineSegment StartX=-49.19 StartY=8.5 StartZ=0 EndX=-1.5 EndY=8.5 EndZ=0
    g46: LineSegment StartX=-49.19 StartY=5.75 StartZ=0 EndX=-1.5 EndY=5.75 EndZ=0
    g47: LineSegment StartX=-49.19 StartY=2.75 StartZ=0 EndX=-1.5 EndY=2.75 EndZ=0
  constraints (120):
    c: Vertical(g0)
    c: Distance(g0) = 3
    c: Block(g0)
    c: Vertical(g1)
    c: Distance(g1) = 3
    c: Vertical(g2)
    c: Equal(g0,g2) = 3
    c: Block(g2)
    c: Vertical(g3)
    c: Equal(g1,g3) = 3
    c: Vertical(g4)
    c: Equal(g0,g4) = 3
    c: Block(g4)
    c: Vertical(g5)
    c: Equal(g1,g5) = 3
    c: Vertical(g6)
    c: Equal(g0,g6) = 3
    c: Block(g6)
    c: Vertical(g7)
    c: Equal(g1,g7) = 3
    c: Vertical(g8)
    c: Equal(g0,g8) = 3
    c: Block(g8)
    c: Vertical(g9)
    c: Equal(g1,g9) = 3
    c: Vertical(g10)
    c: Equal(g0,g10) = 3
    c: Block(g10)
    c: Vertical(g11)
    c: Equal(g1,g11) = 3
    c: Block(g12)
    c: Block(g13)
    c: Block(g14)
    c: Block(g15)
    c: Block(g16)
    c: Block(g17)
    c: Block(g18)
    c: Block(g19)
    c: Block(g20)
    c: Block(g21)
    c: Block(g22)
    c: Block(g23)
    c: Block(g11)
    c: Block(g9)
    c: Block(g7)
    c: Block(g5)
    c: Block(g3)
    c: Block(g1)
    c: Coincident(g24,g0)
    c: Coincident(g24,g12)
    c: Horizontal(g24)
    c: Coincident(g25,g0)
    c: Coincident(g25,g12)
    c: Horizontal(g25)
    c: Coincident(g26,g1)
    c: Coincident(g26,g13)
    c: Horizontal(g26)
    c: Coincident(g27,g1)
    c: Coincident(g27,g13)
    c: Horizontal(g27)
    c: Coincident(g28,g2)
    c: Coincident(g28,g14)
    c: Horizontal(g28)
    c: Coincident(g29,g2)
    c: Coincident(g29,g14)
    c: Horizontal(g29)
    c: Coincident(g30,g3)
    c: Coincident(g30,g15)
    c: Horizontal(g30)
    c: Coincident(g31,g3)
    c: Coincident(g31,g15)
    c: Horizontal(g31)
    c: Coincident(g32,g4)
    c: Coincident(g32,g16)
    c: Horizontal(g32)
    c: Coincident(g33,g4)
    c: Coincident(g33,g16)
    c: Horizontal(g33)
    c: Coincident(g34,g5)
    c: Coincident(g34,g17)
    c: Horizontal(g34)
    c: Coincident(g35,g5)
    c: Coincident(g35,g17)
    c: Horizontal(g35)
    c: Coincident(g36,g6)
    c: Coincident(g36,g19)
    c: Horizontal(g36)
    c: Coincident(g37,g6)
    c: Coincident(g37,g19)
    c: Horizontal(g37)
    c: Coincident(g38,g7)
    c: Coincident(g38,g18)
    c: Horizontal(g38)
    c: Coincident(g39,g7)
    c: Coincident(g39,g18)
    c: Horizontal(g39)
    c: Coincident(g40,g8)
    c: Coincident(g40,g20)
    c: Horizontal(g40)
    c: Coincident(g41,g8)
    c: Coincident(g41,g20)
    c: Horizontal(g41)
    c: Coincident(g42,g9)
    c: Coincident(g42,g23)
    c: Horizontal(g42)
    c: Coincident(g43,g9)
    c: Coincident(g43,g23)
    c: Horizontal(g43)
    c: Coincident(g44,g10)
    c: Coincident(g44,g22)
    c: Horizontal(g44)
    c: Coincident(g45,g10)
    c: Coincident(g45,g22)
    c: Horizontal(g45)
    c: Coincident(g46,g11)
    c: Coincident(g46,g21)
    c: Horizontal(g46)
    c: Coincident(g47,g11)
    c: Coincident(g47,g21)
    c: Horizontal(g47)
FEATURE [Part::Extrusion] Extrude061
  Base = -> Sketch070
  Dir = (1,0,0)
  DirMode = 2
  FaceMakerClass = Part::FaceMakerBullseye
  LengthFwd = 23
  LengthRev = 0
  Placement = pos=(-19,0,0) rot=(0,0,1;0rad)
  Solid = true
  Symmetric = false
FEATURE [Part::Fillet] Fillet052  label="removeToCreateVentalationHoles002"
  Base = -> Extrude061
  Edges = <same value as first occurrence — deduplicated (x6 in doc)>
  Placement = pos=(7,0.02,0) rot=(0,0,1;0rad)
FEATURE [Part::MultiFuse] Fusion130  label="bottom013"
  Shapes = -> [Cut054,Cut034]
FEATURE [Part::Cut] Cut055
  Base = -> Fusion130
  Tool = -> Fillet052
FEATURE [Part::Cylinder] Cylinder054
  Angle = 360
  AttacherType = Attacher::AttachEngine3D
  Height = 20
  Placement = pos=(0,0,36.15) rot=(0,0,1;0rad)
  Radius = 4
FEATURE [Sketcher::SketchObject] Sketch071  label="bottomSketch002"
  FullyConstrained = true
  sketch-geometry (32):
    g0: LineSegment StartX=3.3 StartY=-6.03275e-07 StartZ=0 EndX=98 EndY=-6.03275e-07 EndZ=0
    g1: ArcOfCircle CenterX=98 CenterY=19 CenterZ=0 NormalX=0 NormalY=0 NormalZ=1 AngleXU=0 Radius=19 StartAngle=4.71239 EndAngle=5.71103
    g2: LineSegment StartX=6.3 StartY=8 StartZ=0 EndX=3.3 EndY=8 EndZ=0
    g3: LineSegment StartX=3.3 StartY=8 StartZ=0 EndX=3.3 EndY=-6.03275e-07 EndZ=0
    g4: ArcOfCircle CenterX=8.3 CenterY=5 CenterZ=0 NormalX=0 NormalY=0 NormalZ=1 AngleXU=0 Radius=2 StartAngle=3.14159 EndAngle=4.71239
    g5: LineSegment StartX=6.3 StartY=8 StartZ=0 EndX=6.3 EndY=5 EndZ=0
    g6: ArcOfCircle CenterX=98 CenterY=19 CenterZ=0 NormalX=0 NormalY=0 NormalZ=1 AngleXU=0 Radius=12.7 StartAngle=4.71239 EndAngle=6.28319
    g7: LineSegment StartX=94.7 StartY=3 StartZ=0 EndX=8.3 EndY=3 EndZ=0
    g8-g12: Circle x5 (B-spline internal-alignment scaffolding for g13; pole/knot coordinates omitted)
    g13: BSplineCurve PolesCount=5 KnotsCount=3 Degree=3 IsPeriodic=0
    g14: GeomPoint X=98 Y=6.3 Z=0
    g15: GeomPoint X=96.3938 Y=4.71946 Z=0
    g16: GeomPoint X=94.7 Y=3 Z=0
    g17-g23: Circle x7 (B-spline internal-alignment scaffolding for g24; pole/knot coordinates omitted)
    g24: BSplineCurve PolesCount=7 KnotsCount=5 Degree=3 IsPeriodic=0
    g25-g29: GeomPoint x5 (B-spline internal-alignment scaffolding for g24; pole/knot coordinates omitted)
    g30: ArcOfCircle CenterX=98 CenterY=19 CenterZ=0 NormalX=0 NormalY=0 NormalZ=1 AngleXU=0 Radius=15.7 StartAngle=5.81226 EndAngle=6.28319
    g31: LineSegment StartX=110.7 StartY=19 StartZ=0 EndX=113.7 EndY=19 EndZ=0
  constraints (41):
    c: Horizontal(g0)
    c: Coincident(g1,g0)
    c: Block(g1)
    c: Horizontal(g2)
    c: Distance(g2) = 3
    c: Coincident(g3,g2)
    c: Vertical(g3)
    c: Coincident(g3,g0)
    c: Block(g4)
    c: Block(g2)
    c: Coincident(g5,g2)
    c: Coincident(g5,g4)
    c: Vertical(g5)
    c: Coincident(g6,g1)
    c: Block(g6)
    c: Coincident(g7,g4)
    c: Horizontal(g7)
    c: Block(g0)
    c: Block(g7)
    c: Block(g3)
    c: Coincident(g13,g6)
    c: Weight(g8) = 1
    c: Equal(g8, g9-g12) x4
    c: Coincident(g13,g7)
    c: InternalAlignment(g8-g12 -> g13) x5
    c: InternalAlignment(g14,g13)
    c: InternalAlignment(g15,g13)
    c: InternalAlignment(g16,g13)
    c: Block(g13)
    c: Weight(g17) = 1
    c: Equal(g17, g18-g23) x6
    c: Coincident(g24,g1)
    c: InternalAlignment(g17-g23 -> g24) x7
    c: InternalAlignment(g25-g29 -> g24) x5
    c: Block(g24)
    c: Coincident(g30,g24)
    c: Coincident(g31,g6)
    c: Coincident(g31,g30)
    c: Horizontal(g31)
    c: Block(g31)
    c: Block(g30)
FEATURE [Part::Extrusion] Extrude062  label="bottom014"
  Base = -> Sketch071
  Dir = (0,0,1)
  DirMode = 2
  FaceMakerClass = Part::FaceMakerBullseye
  LengthFwd = 71.4
  LengthRev = 0
  Placement = pos=(0,0,0.3) rot=(0,0,1;0rad)
  Solid = true
  Symmetric = false
FEATURE [Part::Fillet] Fillet054
  Base = -> Extrude062
  Edges = 1 edges r=2.4: [Edge17]
FEATURE [Part::Fillet] Fillet055  label="bottom015"
  Base = -> Fillet054
  Edges = 1 edges r=2.4: [Edge36]
FEATURE [Part::Cylinder] Cylinder055
  Angle = 360
  AttacherType = Attacher::AttachEngine3D
  Height = 10
  Placement = pos=(0,0,36.15) rot=(0,0,1;0rad)
  Radius = 4
FEATURE [Part::MultiFuse] Fusion131  label="removeToCreateHoleForPlugHousing002"
  Placement = pos=(70,19,36.15) rot=(0,1,0;1.5708rad)
  Shapes = -> [Cylinder054,Cylinder055]
FEATURE [Part::Cut] Cut056  label="Bottom001"
  Base = -> Fillet055
  Placement = pos=(9,0,0) rot=(0,0,1;0rad)
  Tool = -> Fusion131
FEATURE [Part::Cut] Cut057
  Base = -> Cut055
  Tool = -> Cut056
FEATURE [Sketcher::SketchObject] Sketch072  label="topSketch021"
  FullyConstrained = true
  sketch-geometry (4):
    g0: ArcOfCircle CenterX=105 CenterY=19 CenterZ=0 NormalX=0 NormalY=0 NormalZ=1 AngleXU=0 Radius=20.6155 StartAngle=5.54125 EndAngle=6.28319
    g1: ArcOfCircle CenterX=105 CenterY=19 CenterZ=0 NormalX=0 NormalY=0 NormalZ=1 AngleXU=0 Radius=13 StartAngle=5.54125 EndAngle=6.28319
    g2: LineSegment StartX=118 StartY=19 StartZ=0 EndX=125.616 EndY=19 EndZ=0
    g3: LineSegment StartX=114.583 StartY=10.2157 StartZ=0 EndX=120.197 EndY=5.06982 EndZ=0
  constraints (7):
    c: Block(g0)
    c: Block(g1)
    c: Coincident(g2,g1)
    c: Coincident(g2,g0)
    c: Horizontal(g2)
    c: Coincident(g3,g1)
    c: Coincident(g3,g0)
FEATURE [Part::Extrusion] Extrude063  label="bottomPlugHousingBit003"
  Base = -> Sketch072
  Dir = (0,0,1)
  DirMode = 2
  FaceMakerClass = Part::FaceMakerBullseye
  LengthFwd = 72
  LengthRev = 0
  Solid = true
  Symmetric = false
FEATURE [Part::Cylinder] Cylinder056
  Angle = 360
  AttacherType = Attacher::AttachEngine3D
  Height = 20
  Placement = pos=(0,0,36.15) rot=(0,0,1;0rad)
  Radius = 14.3
FEATURE [Part::Cylinder] Cylinder057
  Angle = 360
  AttacherType = Attacher::AttachEngine3D
  Height = 10
  Placement = pos=(0,0,36.15) rot=(0,0,1;0rad)
  Radius = 4
FEATURE [Part::Box] Box034  label="removeToCreteHoleForPlugHousing047"
  AttacherType = Attacher::AttachEngine3D
  Height = 28.6
  Length = 20
  Placement = pos=(106.15,0,21.7) rot=(0,0,1;0rad)
  Width = 19
FEATURE [Part::Cylinder] Cylinder058
  Angle = 360
  AttacherType = Attacher::AttachEngine3D
  Height = 20
  Placement = pos=(0,0,36.15) rot=(0,0,1;0rad)
  Radius = 14.3
FEATURE [Part::Cylinder] Cylinder059
  Angle = 360
  AttacherType = Attacher::AttachEngine3D
  Height = 10
  Placement = pos=(0,0,36.15) rot=(0,0,1;0rad)
  Radius = 4
FEATURE [Part::MultiFuse] Fusion134  label="removeToCreteHoleForPlugHousing046"
  Placement = pos=(70,19,36) rot=(0,1,0;1.5708rad)
  Shapes = -> [Cylinder058,Cylinder059]
FEATURE [Part::Cylinder] Cylinder060
  Angle = 360
  AttacherType = Attacher::AttachEngine3D
  Height = 20
  Placement = pos=(0,0,36.15) rot=(0,0,1;0rad)
  Radius = 14
FEATURE [Part::Cylinder] Cylinder061
  Angle = 360
  AttacherType = Attacher::AttachEngine3D
  Height = 10
  Placement = pos=(0,0,36.15) rot=(0,0,1;0rad)
  Radius = 4
FEATURE [Part::MultiFuse] Fusion135  label="removeToCreteHoleForPlugHousing048"
  Placement = pos=(70,19,36) rot=(0,1,0;1.5708rad)
  Shapes = -> [Cylinder060,Cylinder061]
FEATURE [Part::Box] Box035  label="removeToCreteHoleForPlugHousing049"
  AttacherType = Attacher::AttachEngine3D
  Height = 28.6
  Length = 20
  Placement = pos=(106.15,0,21.7) rot=(0,0,1;0rad)
  Width = 19
FEATURE [Part::MultiFuse] Fusion133  label="removeToCreteHoleForPlugHousing045"
  Placement = pos=(0,0,-28.3) rot=(0,0,1;0rad)
  Shapes = -> [Box035,Fusion134]
FEATURE [Part::MultiFuse] Fusion138  label="removeToCreteHoleForPlugHousing051"
  Placement = pos=(70,19,36) rot=(0,1,0;1.5708rad)
  Shapes = -> [Cylinder056,Cylinder057]
FEATURE [Part::MultiFuse] Fusion137  label="removeToCreteHoleForPlugHousing050"
  Placement = pos=(0,0,28.3) rot=(0,0,1;0rad)
  Shapes = -> [Box034,Fusion138]
FEATURE [Part::MultiFuse] Fusion132  label="removeToCreatePlugHousingBottomBit002"
  Shapes = -> [Fusion133,Fusion137]
FEATURE [Part::MultiFuse] Fusion136  label="removeToCreatePlugHousingBottomBit003"
  Shapes = -> [Fusion135,Fusion132]
FEATURE [Part::Cut] Cut058  label="bottomPlugHousingBit002"
  Base = -> Extrude063
  Placement = pos=(-0.09,0,0) rot=(0,0,1;0rad)
  Tool = -> Fusion136
FEATURE [Sketcher::SketchObject] Sketch073  label="bottomSketch003"
  FullyConstrained = true
  sketch-geometry (45):
    g0: LineSegment StartX=6.29999 StartY=8 StartZ=0 EndX=3.29999 EndY=8 EndZ=0
    g1: LineSegment StartX=3.29999 StartY=8 StartZ=0 EndX=3.29999 EndY=-6.03275e-07 EndZ=0
    g2: ArcOfCircle CenterX=8.29999 CenterY=5 CenterZ=0 NormalX=0 NormalY=0 NormalZ=1 AngleXU=0 Radius=2 StartAngle=3.14159 EndAngle=4.71239
    g3: LineSegment StartX=6.29999 StartY=8 StartZ=0 EndX=6.29999 EndY=5 EndZ=0
    g4: ArcOfCircle CenterX=105 CenterY=19 CenterZ=0 NormalX=0 NormalY=0 NormalZ=1 AngleXU=0 Radius=12.7 StartAngle=4.71239 EndAngle=5.94289
    g5-g11: Circle x7 (B-spline internal-alignment scaffolding for g12; pole/knot coordinates omitted)
    g12: BSplineCurve PolesCount=7 KnotsCount=5 Degree=3 IsPeriodic=0
    g13-g17: GeomPoint x5 (B-spline internal-alignment scaffolding for g12; pole/knot coordinates omitted)
    g18: ArcOfCircle CenterX=105 CenterY=19 CenterZ=0 NormalX=0 NormalY=0 NormalZ=1 AngleXU=0 Radius=15.7 StartAngle=5.81226 EndAngle=6.28319
    g19: BSplineCurve PolesCount=5 KnotsCount=3 Degree=3 IsPeriodic=0
    g20: LineSegment StartX=8.29999 StartY=3 StartZ=0 EndX=101.7 EndY=3 EndZ=0
    g21: LineSegment StartX=3.29999 StartY=-6.03275e-07 StartZ=0 EndX=105 EndY=-6.03275e-07 EndZ=0
    g22: LineSegment StartX=120.974 StartY=8.71251 StartZ=0 EndX=122.332 EndY=7.83778 EndZ=0
    g23: LineSegment StartX=105 StartY=-6.03274e-07 StartZ=0 EndX=113 EndY=-6.03274e-07 EndZ=0
    g24: ArcOfCircle CenterX=105 CenterY=19 CenterZ=0 NormalX=0 NormalY=0 NormalZ=1 AngleXU=0 Radius=20.6155 StartAngle=5.11091 EndAngle=5.71103
    g25: ArcOfCircle CenterX=117.7 CenterY=19 CenterZ=0 NormalX=0 NormalY=0 NormalZ=1 AngleXU=0 Radius=3 StartAngle=1.2e-15 EndAngle=2.10468
    g26: Circle CenterX=116.345 CenterY=16.3232 CenterZ=0 NormalX=0 NormalY=0 NormalZ=1 AngleXU=0 Radius=1
    g27: Circle CenterX=117.24 CenterY=15.7584 CenterZ=0 NormalX=0 NormalY=0 NormalZ=1 AngleXU=0 Radius=1
    g28: Circle CenterX=116.972 CenterY=14.7612 CenterZ=0 NormalX=0 NormalY=0 NormalZ=1 AngleXU=0 Radius=1
    g29: BSplineCurve PolesCount=3 KnotsCount=2 Degree=2 IsPeriodic=0
    g30: GeomPoint X=116.345 Y=16.3232 Z=0
    g31: GeomPoint X=116.972 Y=14.7612 Z=0
    g32: Circle CenterX=115.828 CenterY=17.157 CenterZ=0 NormalX=0 NormalY=0 NormalZ=1 AngleXU=0 Radius=1
    g33: Circle CenterX=115.841 CenterY=16.639 CenterZ=0 NormalX=0 NormalY=0 NormalZ=1 AngleXU=0 Radius=1
    g34: Circle CenterX=116.345 CenterY=16.3232 CenterZ=0 NormalX=0 NormalY=0 NormalZ=1 AngleXU=0 Radius=1
    g35: BSplineCurve PolesCount=3 KnotsCount=2 Degree=2 IsPeriodic=0
    g36: GeomPoint X=115.828 Y=17.157 Z=0
    g37: GeomPoint X=116.345 Y=16.3232 Z=0
    g38: LineSegment StartX=115.828 StartY=17.157 StartZ=0 EndX=115.828 EndY=20.8307 EndZ=0
    g39: Circle CenterX=115.828 CenterY=20.8307 CenterZ=0 NormalX=0 NormalY=0 NormalZ=1 AngleXU=0 Radius=1
    g40: Circle CenterX=115.831 CenterY=21.3396 CenterZ=0 NormalX=0 NormalY=0 NormalZ=1 AngleXU=0 Radius=1
    g41: Circle CenterX=116.173 CenterY=21.5825 CenterZ=0 NormalX=0 NormalY=0 NormalZ=1 AngleXU=0 Radius=1
    g42: BSplineCurve PolesCount=3 KnotsCount=2 Degree=2 IsPeriodic=0
    g43: GeomPoint X=115.828 Y=20.8307 Z=0
    g44: GeomPoint X=116.173 Y=21.5825 Z=0
  constraints (70):
    c: Horizontal(g0)
    c: Distance(g0) = 3
    c: Coincident(g1,g0)
    c: Vertical(g1)
    c: Block(g2)
    c: Block(g0)
    c: Coincident(g3,g0)
    c: Coincident(g3,g2)
    c: Vertical(g3)
    c: Block(g1)
    c: Block(g4)
    c: Coincident(g19,g4)
    c: Block(g19)
    c: Equal(g5, g6-g11) x6
    c: InternalAlignment(g5-g11 -> g12) x7
    c: InternalAlignment(g13-g17 -> g12) x5
    c: Block(g12)
    c: Coincident(g18,g12)
    c: Block(g18)
    c: Coincident(g20,g2)
    c: Coincident(g20,g19)
    c: Horizontal(g20)
    c: Distance(g20) = 93.4
    c: Coincident(g21,g1)
    c: Horizontal(g21)
    c: Distance(g21) = 101.7
    c: Horizontal(g23)
    c: Distance(g23) = 8
    c: Coincident(g24,g23)
    c: Block(g23)
    c: Coincident(g22,g24)
    c: Block(g24)
    c: Block(g22)
    c: Distance(g22) = 1.61553
    c: Coincident(g25,g18)
    c: Block(g25)
    c: Weight(g26) = 1
    c: Equal(g26,g27)
    c: Equal(g26,g28)
    c: Coincident(g29,g4)
    c: InternalAlignment(g26,g29)
    c: InternalAlignment(g27,g29)
    c: InternalAlignment(g28,g29)
    c: InternalAlignment(g30,g29)
    c: InternalAlignment(g31,g29)
    c: Block(g29)
    c: Weight(g32) = 1
    c: Equal(g32,g33)
    c: Equal(g32,g34)
    c: Coincident(g35,g29)
    c: InternalAlignment(g32,g35)
    c: InternalAlignment(g33,g35)
    c: InternalAlignment(g34,g35)
    c: InternalAlignment(g36,g35)
    c: InternalAlignment(g37,g35)
    c: Block(g35)
    c: Coincident(g38,g35)
    c: Vertical(g38)
    c: Block(g38)
    c: Coincident(g42,g38)
    c: Weight(g39) = 1
    c: Equal(g39,g40)
    c: Equal(g39,g41)
    c: Coincident(g42,g25)
    c: InternalAlignment(g39,g42)
    c: InternalAlignment(g40,g42)
    c: InternalAlignment(g41,g42)
    c: InternalAlignment(g43,g42)
    c: InternalAlignment(g44,g42)
    c: Block(g42)
FEATURE [Part::Extrusion] Extrude064  label="bottom016"
  Base = -> Sketch073
  Dir = (0,0,1)
  DirMode = 2
  FaceMakerClass = Part::FaceMakerBullseye
  LengthFwd = 71.4
  LengthRev = 0
  Placement = pos=(0,0,0.3) rot=(0,0,1;0rad)
  Solid = true
  Symmetric = false
FEATURE [Part::Revolution] Revolve157  label="removeToCreateScrewAndThreadedInsertHole063"
  Angle = 360
  Axis = (0,1,0)
  Base = (0,0,0)
  FaceMakerClass = Part::FaceMakerBullseye
  Placement = pos=(12.5,0,10) rot=(0,0,1;0rad)
  Solid = false
  Source = -> Face141
  Symmetric = false
FEATURE [Sketcher::SketchObject] Sketch074
  FullyConstrained = true
  Placement = pos=(117,19,0) rot=(0.57735,0.57735,0.57735;2.0944rad)
  sketch-geometry (48):
    g0: LineSegment StartX=-49.19 StartY=69.25 StartZ=0 EndX=-49.19 EndY=66.25 EndZ=0
    g1: LineSegment StartX=-49.19 StartY=63.5 StartZ=0 EndX=-49.19 EndY=60.5 EndZ=0
    g2: LineSegment StartX=-49.19 StartY=57.75 StartZ=0 EndX=-49.19 EndY=54.75 EndZ=0
    g3: LineSegment StartX=-49.19 StartY=52 StartZ=0 EndX=-49.19 EndY=49 EndZ=0
    g4: LineSegment StartX=-49.19 StartY=46.25 StartZ=0 EndX=-49.19 EndY=43.25 EndZ=0
    g5: LineSegment StartX=-49.19 StartY=40.5 StartZ=0 EndX=-49.19 EndY=37.5 EndZ=0
    g6: LineSegment StartX=-49.19 StartY=34.5 StartZ=0 EndX=-49.19 EndY=31.5 EndZ=0
    g7: LineSegment StartX=-49.19 StartY=28.75 StartZ=0 EndX=-49.19 EndY=25.75 EndZ=0
    g8: LineSegment StartX=-49.19 StartY=23 StartZ=0 EndX=-49.19 EndY=20 EndZ=0
    g9: LineSegment StartX=-49.19 StartY=17.25 StartZ=0 EndX=-49.19 EndY=14.25 EndZ=0
    g10: LineSegment StartX=-49.19 StartY=11.5 StartZ=0 EndX=-49.19 EndY=8.5 EndZ=0
    g11: LineSegment StartX=-49.19 StartY=5.75 StartZ=0 EndX=-49.19 EndY=2.75 EndZ=0
    g12: ArcOfCircle CenterX=-1.5 CenterY=67.75 CenterZ=0 NormalX=0 NormalY=0 NormalZ=1 AngleXU=0 Radius=1.5 StartAngle=4.71239 EndAngle=7.85398
    g13: ArcOfCircle CenterX=-1.5 CenterY=62 CenterZ=0 NormalX=0 NormalY=0 NormalZ=1 AngleXU=0 Radius=1.5 StartAngle=4.71239 EndAngle=7.85398
    g14: ArcOfCircle CenterX=-1.5 CenterY=56.25 CenterZ=0 NormalX=0 NormalY=0 NormalZ=1 AngleXU=0 Radius=1.5 StartAngle=4.71239 EndAngle=7.85398
    g15: ArcOfCircle CenterX=-11.49 CenterY=50.5 CenterZ=0 NormalX=0 NormalY=0 NormalZ=1 AngleXU=0 Radius=1.5 StartAngle=4.71239 EndAngle=7.85398
    g16: ArcOfCircle CenterX=-16.28 CenterY=44.75 CenterZ=0 NormalX=0 NormalY=0 NormalZ=1 AngleXU=0 Radius=1.5 StartAngle=4.71239 EndAngle=7.85398
    g17: ArcOfCircle CenterX=-18.2337 CenterY=39 CenterZ=0 NormalX=0 NormalY=0 NormalZ=1 AngleXU=0 Radius=1.5 StartAngle=4.71485 EndAngle=7.85398
    g18: ArcOfCircle CenterX=-16.2837 CenterY=27.25 CenterZ=0 NormalX=0 NormalY=0 NormalZ=1 AngleXU=0 Radius=1.5 StartAngle=4.71485 EndAngle=7.85398
    g19: ArcOfCircle CenterX=-18.2337 CenterY=33 CenterZ=0 NormalX=0 NormalY=0 NormalZ=1 AngleXU=0 Radius=1.5 StartAngle=4.71485 EndAngle=7.85398
    g20: ArcOfCircle CenterX=-11.49 CenterY=21.5 CenterZ=0 NormalX=0 NormalY=0 NormalZ=1 AngleXU=0 Radius=1.5 StartAngle=4.71239 EndAngle=7.85398
    g21: ArcOfCircle CenterX=-1.5 CenterY=4.25 CenterZ=0 NormalX=0 NormalY=0 NormalZ=1 AngleXU=0 Radius=1.5 StartAngle=4.71239 EndAngle=7.85398
    g22: ArcOfCircle CenterX=-1.5 CenterY=10 CenterZ=0 NormalX=0 NormalY=0 NormalZ=1 AngleXU=0 Radius=1.5 StartAngle=4.71239 EndAngle=7.85398
    g23: ArcOfCircle CenterX=-1.5 CenterY=15.75 CenterZ=0 NormalX=0 NormalY=0 NormalZ=1 AngleXU=0 Radius=1.5 StartAngle=4.71239 EndAngle=7.85398
    g24: LineSegment StartX=-49.19 StartY=69.25 StartZ=0 EndX=-1.5 EndY=69.25 EndZ=0
    g25: LineSegment StartX=-49.19 StartY=66.25 StartZ=0 EndX=-1.5 EndY=66.25 EndZ=0
    g26: LineSegment StartX=-49.19 StartY=63.5 StartZ=0 EndX=-1.5 EndY=63.5 EndZ=0
    g27: LineSegment StartX=-49.19 StartY=60.5 StartZ=0 EndX=-1.5 EndY=60.5 EndZ=0
    g28: LineSegment StartX=-49.19 StartY=57.75 StartZ=0 EndX=-1.5 EndY=57.75 EndZ=0
    g29: LineSegment StartX=-49.19 StartY=54.75 StartZ=0 EndX=-1.5 EndY=54.75 EndZ=0
    g30: LineSegment StartX=-49.19 StartY=52 StartZ=0 EndX=-11.49 EndY=52 EndZ=0
    g31: LineSegment StartX=-49.19 StartY=49 StartZ=0 EndX=-11.49 EndY=49 EndZ=0
    g32: LineSegment StartX=-49.19 StartY=46.25 StartZ=0 EndX=-16.28 EndY=46.25 EndZ=0
    g33: LineSegment StartX=-49.19 StartY=43.25 StartZ=0 EndX=-16.28 EndY=43.25 EndZ=0
    g34: LineSegment StartX=-49.19 StartY=40.5 StartZ=0 EndX=-18.2337 EndY=40.5 EndZ=0
    g35: LineSegment StartX=-49.19 StartY=37.5 StartZ=0 EndX=-18.23 EndY=37.5 EndZ=0
    g36: LineSegment StartX=-49.19 StartY=34.5 StartZ=0 EndX=-18.2337 EndY=34.5 EndZ=0
    g37: LineSegment StartX=-49.19 StartY=31.5 StartZ=0 EndX=-18.23 EndY=31.5 EndZ=0
    g38: LineSegment StartX=-49.19 StartY=28.75 StartZ=0 EndX=-16.2837 EndY=28.75 EndZ=0
    g39: LineSegment StartX=-49.19 StartY=25.75 StartZ=0 EndX=-16.28 EndY=25.75 EndZ=0
    g40: LineSegment StartX=-49.19 StartY=23 StartZ=0 EndX=-11.49 EndY=23 EndZ=0
    g41: LineSegment StartX=-49.19 StartY=20 StartZ=0 EndX=-11.49 EndY=20 EndZ=0
    g42: LineSegment StartX=-49.19 StartY=17.25 StartZ=0 EndX=-1.5 EndY=17.25 EndZ=0
    g43: LineSegment StartX=-49.19 StartY=14.25 StartZ=0 EndX=-1.5 EndY=14.25 EndZ=0
    g44: LineSegment StartX=-49.19 StartY=11.5 StartZ=0 EndX=-1.5 EndY=11.5 EndZ=0
    g45: LineSegment StartX=-49.19 StartY=8.5 StartZ=0 EndX=-1.5 EndY=8.5 EndZ=0
    g46: LineSegment StartX=-49.19 StartY=5.75 StartZ=0 EndX=-1.5 EndY=5.75 EndZ=0
    g47: LineSegment StartX=-49.19 StartY=2.75 StartZ=0 EndX=-1.5 EndY=2.75 EndZ=0
  constraints (120):
    c: Vertical(g0)
    c: Distance(g0) = 3
    c: Block(g0)
    c: Vertical(g1)
    c: Distance(g1) = 3
    c: Vertical(g2)
    c: Equal(g0,g2) = 3
    c: Block(g2)
    c: Vertical(g3)
    c: Equal(g1,g3) = 3
    c: Vertical(g4)
    c: Equal(g0,g4) = 3
    c: Block(g4)
    c: Vertical(g5)
    c: Equal(g1,g5) = 3
    c: Vertical(g6)
    c: Equal(g0,g6) = 3
    c: Block(g6)
    c: Vertical(g7)
    c: Equal(g1,g7) = 3
    c: Vertical(g8)
    c: Equal(g0,g8) = 3
    c: Block(g8)
    c: Vertical(g9)
    c: Equal(g1,g9) = 3
    c: Vertical(g10)
    c: Equal(g0,g10) = 3
    c: Block(g10)
    c: Vertical(g11)
    c: Equal(g1,g11) = 3
    c: Block(g12)
    c: Block(g13)
    c: Block(g14)
    c: Block(g15)
    c: Block(g16)
    c: Block(g17)
    c: Block(g18)
    c: Block(g19)
    c: Block(g20)
    c: Block(g21)
    c: Block(g22)
    c: Block(g23)
    c: Block(g11)
    c: Block(g9)
    c: Block(g7)
    c: Block(g5)
    c: Block(g3)
    c: Block(g1)
    c: Coincident(g24,g0)
    c: Coincident(g24,g12)
    c: Horizontal(g24)
    c: Coincident(g25,g0)
    c: Coincident(g25,g12)
    c: Horizontal(g25)
    c: Coincident(g26,g1)
    c: Coincident(g26,g13)
    c: Horizontal(g26)
    c: Coincident(g27,g1)
    c: Coincident(g27,g13)
    c: Horizontal(g27)
    c: Coincident(g28,g2)
    c: Coincident(g28,g14)
    c: Horizontal(g28)
    c: Coincident(g29,g2)
    c: Coincident(g29,g14)
    c: Horizontal(g29)
    c: Coincident(g30,g3)
    c: Coincident(g30,g15)
    c: Horizontal(g30)
    c: Coincident(g31,g3)
    c: Coincident(g31,g15)
    c: Horizontal(g31)
    c: Coincident(g32,g4)
    c: Coincident(g32,g16)
    c: Horizontal(g32)
    c: Coincident(g33,g4)
    c: Coincident(g33,g16)
    c: Horizontal(g33)
    c: Coincident(g34,g5)
    c: Coincident(g34,g17)
    c: Horizontal(g34)
    c: Coincident(g35,g5)
    c: Coincident(g35,g17)
    c: Horizontal(g35)
    c: Coincident(g36,g6)
    c: Coincident(g36,g19)
    c: Horizontal(g36)
    c: Coincident(g37,g6)
    c: Coincident(g37,g19)
    c: Horizontal(g37)
    c: Coincident(g38,g7)
    c: Coincident(g38,g18)
    c: Horizontal(g38)
    c: Coincident(g39,g7)
    c: Coincident(g39,g18)
    c: Horizontal(g39)
    c: Coincident(g40,g8)
    c: Coincident(g40,g20)
    c: Horizontal(g40)
    c: Coincident(g41,g8)
    c: Coincident(g41,g20)
    c: Horizontal(g41)
    c: Coincident(g42,g9)
    c: Coincident(g42,g23)
    c: Horizontal(g42)
    c: Coincident(g43,g9)
    c: Coincident(g43,g23)
    c: Horizontal(g43)
    c: Coincident(g44,g10)
    c: Coincident(g44,g22)
    c: Horizontal(g44)
    c: Coincident(g45,g10)
    c: Coincident(g45,g22)
    c: Horizontal(g45)
    c: Coincident(g46,g11)
    c: Coincident(g46,g21)
    c: Horizontal(g46)
    c: Coincident(g47,g11)
    c: Coincident(g47,g21)
    c: Horizontal(g47)
FEATURE [Part::Extrusion] Extrude065
  Base = -> Sketch074
  Dir = (1,0,0)
  DirMode = 2
  FaceMakerClass = Part::FaceMakerBullseye
  LengthFwd = 23
  LengthRev = 0
  Placement = pos=(-19,0,0) rot=(0,0,1;0rad)
  Solid = true
  Symmetric = false
FEATURE [Part::Fillet] Fillet056  label="removeToCreateVentalationHoles003"
  Base = -> Extrude065
  Edges = <same value as first occurrence — deduplicated (x6 in doc)>
  Placement = pos=(7,0.02,0) rot=(0,0,1;0rad)
FEATURE [Part::Revolution] Revolve158  label="removeToCreateScrewAndThreadedInsertHole065"
  Angle = 360
  Axis = (0,1,0)
  Base = (0,0,0)
  FaceMakerClass = Part::FaceMakerBullseye
  Placement = pos=(12.5,0,62) rot=(0,0,1;0rad)
  Solid = false
  Source = -> Face146
  Symmetric = false
FEATURE [Part::Revolution] Revolve159  label="removeToCreateScrewAndThreadedInsertHole066"
  Angle = 360
  Axis = (0,1,0)
  Base = (0,0,0)
  FaceMakerClass = Part::FaceMakerBullseye
  Placement = pos=(89.5,0,68.5) rot=(0,0,1;0rad)
  Solid = false
  Source = -> Face143
  Symmetric = false
FEATURE [Part::Revolution] Revolve160  label="removeToCreateScrewAndThreadedInsertHole067"
  Angle = 360
  Axis = (0,1,0)
  Base = (0,0,0)
  FaceMakerClass = Part::FaceMakerBullseye
  Placement = pos=(89.5,0,3.5) rot=(0,0,1;0rad)
  Solid = false
  Source = -> Face142
  Symmetric = false
FEATURE [Part::Revolution] Revolve161  label="removeToCreateScrewAndThreadedInsertHole068"
  Angle = 360
  Axis = (0,1,0)
  Base = (0,0,0)
  FaceMakerClass = Part::FaceMakerBullseye
  Placement = pos=(109.5,4.7,3.5) rot=(0,0,1;0rad)
  Solid = false
  Source = -> Face145
  Symmetric = false
FEATURE [Part::Revolution] Revolve162  label="removeToCreateScrewAndThreadedInsertHole069"
  Angle = 360
  Axis = (0,1,0)
  Base = (0,0,0)
  FaceMakerClass = Part::FaceMakerBullseye
  Placement = pos=(109.5,4.7,68.5) rot=(0,0,1;0rad)
  Solid = false
  Source = -> Face144
  Symmetric = false
FEATURE [Part::MultiFuse] Fusion141  label="removeToCreateScrewAndThreadedInsertHole064"
  Shapes = -> [Revolve162,Revolve161,Revolve160,Revolve159,Revolve158,Revolve157]
FEATURE [Part::Cylinder] Cylinder062
  Angle = 360
  AttacherType = Attacher::AttachEngine3D
  Height = 20
  Placement = pos=(0,0,36.15) rot=(0,0,1;0rad)
  Radius = 14
FEATURE [Part::Cylinder] Cylinder063
  Angle = 360
  AttacherType = Attacher::AttachEngine3D
  Height = 10
  Placement = pos=(0,0,36.15) rot=(0,0,1;0rad)
  Radius = 4
FEATURE [Part::MultiFuse] Fusion139  label="removeToCreteHoleForPlugHousing052"
  Placement = pos=(70,19,36) rot=(0,1,0;1.5708rad)
  Shapes = -> [Cylinder062,Cylinder063]
FEATURE [Part::Cut] Cut060  label="bottom017"
  Base = -> Extrude064
  Tool = -> Fusion139
FEATURE [Part::Cut] Cut061  label="bottom019"
  Base = -> Cut060
  Tool = -> Fusion141
FEATURE [Part::MultiFuse] Fusion140  label="bottom018"
  Shapes = -> [Cut061,Cut058]
FEATURE [Part::Cut] Cut059  label="bottom020"
  Base = -> Fusion140
  Tool = -> Fillet056
FEATURE [Part::Box] Box036  label="Cube021"
  AttacherType = Attacher::AttachEngine3D
  Height = 80
  Length = 26
  Placement = pos=(0,-1,-5) rot=(0,0,1;0rad)
  Width = 11
FEATURE [Part::Cut] Cut062  label="removeFromBottom002"
  Base = -> Cut057
  Tool = -> Box036
FEATURE [Part::Cut] Cut063
  Base = -> Cut059
  Tool = -> Cut062
FEATURE [Part::Cut] Cut064  label="pcbStands"
  Base = -> Fusion095
  Tool = -> Fusion127
FEATURE [Sketcher::SketchObject] Sketch075  label="topSketch022"
  FullyConstrained = true
  sketch-geometry (6):
    g0: LineSegment StartX=19 StartY=38 StartZ=0 EndX=117 EndY=38 EndZ=0
    g1: ArcOfCircle CenterX=19 CenterY=19 CenterZ=0 NormalX=0 NormalY=0 NormalZ=1 AngleXU=0 Radius=19 StartAngle=1.5708 EndAngle=3.14159
    g2: LineSegment StartX=117 StartY=38 StartZ=0 EndX=117 EndY=19 EndZ=0
    g3: LineSegment StartX=98 StartY=1.0161e-12 StartZ=0 EndX=5.22862e-06 EndY=1.0161e-12 EndZ=0
    g4: LineSegment StartX=5.22862e-06 StartY=19 StartZ=0 EndX=5.22862e-06 EndY=1.0161e-12 EndZ=0
    g5: ArcOfCircle CenterX=98 CenterY=19 CenterZ=0 NormalX=0 NormalY=0 NormalZ=1 AngleXU=0 Radius=19 StartAngle=4.71239 EndAngle=6.28319
  constraints (16):
    c: Horizontal(g0)
    c: Distance(g0) = 98
    c: Coincident(g1,g0)
    c: Block(g1)
    c: Coincident(g2,g0)
    c: Vertical(g2)
    c: Distance(g2) = 19
    c: Horizontal(g3)
    c: Coincident(g4,g1)
    c: Vertical(g4)
    c: Coincident(g3,g4)
    c: Block(g3)
    c: Coincident(g5,g2)
    c: Coincident(g5,g3)
    c: Block(g0)
    c: Block(g5)
FEATURE [Part::Extrusion] Extrude067  label="sideB003"
  Base = -> Sketch075
  Dir = (0,0,1)
  DirMode = 2
  FaceMakerClass = Part::FaceMakerBullseye
  LengthFwd = 3
  LengthRev = 0
  Placement = pos=(0,0,71.7) rot=(0,0,1;0rad)
  Solid = true
  Symmetric = false
FEATURE [Sketcher::SketchObject] Sketch076  label="topSketch023"
  FullyConstrained = true
  sketch-geometry (6):
    g0: LineSegment StartX=19 StartY=38 StartZ=0 EndX=117 EndY=38 EndZ=0
    g1: ArcOfCircle CenterX=19 CenterY=19 CenterZ=0 NormalX=0 NormalY=0 NormalZ=1 AngleXU=0 Radius=19 StartAngle=1.5708 EndAngle=3.14159
    g2: LineSegment StartX=117 StartY=38 StartZ=0 EndX=117 EndY=19 EndZ=0
    g3: LineSegment StartX=98 StartY=1.0161e-12 StartZ=0 EndX=5.22862e-06 EndY=1.0161e-12 EndZ=0
    g4: LineSegment StartX=5.22862e-06 StartY=19 StartZ=0 EndX=5.22862e-06 EndY=1.0161e-12 EndZ=0
    g5: ArcOfCircle CenterX=98 CenterY=19 CenterZ=0 NormalX=0 NormalY=0 NormalZ=1 AngleXU=0 Radius=19 StartAngle=4.71239 EndAngle=6.28319
  constraints (16):
    c: Horizontal(g0)
    c: Distance(g0) = 98
    c: Coincident(g1,g0)
    c: Block(g1)
    c: Coincident(g2,g0)
    c: Vertical(g2)
    c: Distance(g2) = 19
    c: Horizontal(g3)
    c: Coincident(g4,g1)
    c: Vertical(g4)
    c: Coincident(g3,g4)
    c: Block(g3)
    c: Coincident(g5,g2)
    c: Coincident(g5,g3)
    c: Block(g0)
    c: Block(g5)
FEATURE [Part::Extrusion] Extrude066  label="sideA003"
  Base = -> Sketch076
  Dir = (0,0,1)
  DirMode = 2
  FaceMakerClass = Part::FaceMakerBullseye
  LengthFwd = 3
  LengthRev = 0
  Placement = pos=(0,0,-2.7) rot=(0,0,1;0rad)
  Solid = true
  Symmetric = false
FEATURE [Part::MultiFuse] Fusion142  label="removeFromBottom003"
  Placement = pos=(2,0,0) rot=(0,0,1;0rad)
  Shapes = -> [Extrude066,Extrude067]
FEATURE [Part::Cut] Cut065  label="screwRetainers002"
  Base = -> Fusion096
  Tool = -> Fusion142
FEATURE [Sketcher::SketchObject] Sketch077
  FullyConstrained = true
  Placement = pos=(117,19,0) rot=(0.57735,0.57735,0.57735;2.0944rad)
  sketch-geometry (8):
    g0: LineSegment StartX=-49.19 StartY=63.5 StartZ=0 EndX=-49.19 EndY=60.5 EndZ=0
    g1: LineSegment StartX=-49.19 StartY=11.5 StartZ=0 EndX=-49.19 EndY=8.5 EndZ=0
    g2: ArcOfCircle CenterX=-1.5 CenterY=62 CenterZ=0 NormalX=0 NormalY=0 NormalZ=1 AngleXU=0 Radius=1.5 StartAngle=4.71239 EndAngle=7.85398
    g3: ArcOfCircle CenterX=-1.5 CenterY=10 CenterZ=0 NormalX=0 NormalY=0 NormalZ=1 AngleXU=0 Radius=1.5 StartAngle=4.71239 EndAngle=7.85398
    g4: LineSegment StartX=-49.19 StartY=63.5 StartZ=0 EndX=-1.5 EndY=63.5 EndZ=0
    g5: LineSegment StartX=-49.19 StartY=60.5 StartZ=0 EndX=-1.5 EndY=60.5 EndZ=0
    g6: LineSegment StartX=-49.19 StartY=11.5 StartZ=0 EndX=-1.5 EndY=11.5 EndZ=0
    g7: LineSegment StartX=-49.19 StartY=8.5 StartZ=0 EndX=-1.5 EndY=8.5 EndZ=0
  constraints (19):
    c: Vertical(g0)
    c: Distance(g0) = 3
    c: Vertical(g1)
    c: Block(g1)
    c: Block(g2)
    c: Block(g3)
    c: Block(g0)
    c: Coincident(g4,g0)
    c: Coincident(g4,g2)
    c: Horizontal(g4)
    c: Coincident(g5,g0)
    c: Coincident(g5,g2)
    c: Horizontal(g5)
    c: Coincident(g6,g1)
    c: Coincident(g6,g3)
    c: Horizontal(g6)
    c: Coincident(g7,g1)
    c: Coincident(g7,g3)
    c: Horizontal(g7)
FEATURE [Part::Extrusion] Extrude068
  Base = -> Sketch077
  Dir = (1,0,0)
  DirMode = 2
  FaceMakerClass = Part::FaceMakerBullseye
  LengthFwd = 10
  LengthRev = 0
  Solid = true
  Symmetric = false
FEATURE [Part::Fillet] Fillet057  label="removeFromtMoreFrontCaseScrewRetainers002"
  Base = -> Extrude068
  Edges = 4 edges r=1.49: [Edge6,Edge11,Edge18,Edge23]
  Placement = pos=(-12,0,0) rot=(0,0,1;0rad)
FEATURE [Sketcher::SketchObject] Sketch078
  FullyConstrained = true
  Placement = pos=(117,19,0) rot=(0.57735,0.57735,0.57735;2.0944rad)
  sketch-geometry (8):
    g0: LineSegment StartX=-49.19 StartY=69.25 StartZ=0 EndX=-49.19 EndY=66.25 EndZ=0
    g1: LineSegment StartX=-49.19 StartY=5.75 StartZ=0 EndX=-49.19 EndY=2.75 EndZ=0
    g2: ArcOfCircle CenterX=-1.5 CenterY=67.75 CenterZ=0 NormalX=0 NormalY=0 NormalZ=1 AngleXU=0 Radius=1.5 StartAngle=4.71239 EndAngle=7.85398
    g3: ArcOfCircle CenterX=-1.5 CenterY=4.25 CenterZ=0 NormalX=0 NormalY=0 NormalZ=1 AngleXU=0 Radius=1.5 StartAngle=4.71239 EndAngle=7.85398
    g4: LineSegment StartX=-49.19 StartY=69.25 StartZ=0 EndX=-1.5 EndY=69.25 EndZ=0
    g5: LineSegment StartX=-49.19 StartY=66.25 StartZ=0 EndX=-1.5 EndY=66.25 EndZ=0
    g6: LineSegment StartX=-49.19 StartY=5.75 StartZ=0 EndX=-1.5 EndY=5.75 EndZ=0
    g7: LineSegment StartX=-49.19 StartY=2.75 StartZ=0 EndX=-1.5 EndY=2.75 EndZ=0
  constraints (19):
    c: Vertical(g0)
    c: Distance(g0) = 3
    c: Block(g0)
    c: Vertical(g1)
    c: Block(g2)
    c: Block(g3)
    c: Block(g1)
    c: Coincident(g4,g0)
    c: Coincident(g4,g2)
    c: Horizontal(g4)
    c: Coincident(g5,g0)
    c: Coincident(g5,g2)
    c: Horizontal(g5)
    c: Coincident(g6,g1)
    c: Coincident(g6,g3)
    c: Horizontal(g6)
    c: Coincident(g7,g1)
    c: Coincident(g7,g3)
    c: Horizontal(g7)
FEATURE [Part::Extrusion] Extrude069
  Base = -> Sketch078
  Dir = (1,0,0)
  DirMode = 2
  FaceMakerClass = Part::FaceMakerBullseye
  LengthFwd = 10
  LengthRev = 0
  Solid = true
  Symmetric = false
FEATURE [Part::Fillet] Fillet058  label="removeFromtMoreFrontCaseScrewRetainers003"
  Base = -> Extrude069
  Edges = 4 edges r=1.49: [Edge6,Edge11,Edge18,Edge23]
  Placement = pos=(-4,0,0) rot=(0,0,1;0rad)
FEATURE [Part::Cut] Cut066
  Base = -> Cut065
  Tool = -> Fillet058
FEATURE [Part::Cut] Cut067  label="screwPillars"
  Base = -> Cut066
  Tool = -> Fillet057
FEATURE [Part::MultiFuse] Fusion143  label="bottom021"
  Shapes = -> [Cut031,Cut063]
FEATURE [Part::Cylinder] Cylinder
  Angle = 360
  AttacherType = Attacher::AttachEngine3D
  Height = 10
  Placement = pos=(20.65,12,4.68) rot=(1,0,0;1.5708rad)
  Radius = 2
FEATURE [Part::Cylinder] Cylinder064
  Angle = 360
  AttacherType = Attacher::AttachEngine3D
  Height = 10
  Placement = pos=(20.65,12,67.38) rot=(1,0,0;1.5708rad)
  Radius = 2
FEATURE [Part::Cylinder] Cylinder065
  Angle = 360
  AttacherType = Attacher::AttachEngine3D
  Height = 10
  Placement = pos=(77.15,12,67.38) rot=(1,0,0;1.5708rad)
  Radius = 2
FEATURE [Part::Cylinder] Cylinder066
  Angle = 360
  AttacherType = Attacher::AttachEngine3D
  Height = 10
  Placement = pos=(77.15,12,4.68) rot=(1,0,0;1.5708rad)
  Radius = 2
FEATURE [Part::MultiFuse] Fusion144  label="removeFromThreadedInsertHousing"
  Shapes = -> [Cylinder065,Cylinder064,Cylinder,Cylinder066]
FEATURE [Part::Cut] Cut068  label="pcbStands001"
  Base = -> Cut064
  Tool = -> Fusion144
FEATURE [Part::MultiFuse] Fusion145
  Shapes = -> [Cut068,Fusion143]
FEATURE [Part::MultiFuse] Fusion146
  Shapes = -> [Fusion145]
FEATURE [Part::MultiFuse] Fusion147  label="bottom022"
  Shapes = -> [Cut067,Fusion146]
FEATURE [Part::MultiFuse] Fusion148  label="casePillars005"
  Shapes = -> [Cut047,Fusion092]
FEATURE [Part::MultiFuse] Fusion149  label="bottom023"
  Shapes = -> [Fusion124,Fusion113,Fusion147]
FEATURE [Part::MultiFuse] Fusion150  label="topBits"
  Shapes = -> [Cut025,Fusion148,Cut030,Fillet034]
FEATURE [Part::Feature] Face149 .. Face152  x4 (patterned run collapsed; names and placements below)
  shape: bbox 3.2 x 1.5 x 2e-07 mm, 1 faces, 0 solids (baked)
FEATURE [Part::Feature] Face153
  shape: bbox 3.6 x 3.2 x 2e-07 mm, 1 faces, 0 solids (baked)
FEATURE [Part::Feature] Face154
  shape: bbox 3.6 x 3.2 x 2e-07 mm, 1 faces, 0 solids (baked)
FEATURE [Sketcher::SketchObject] Sketch079  label="topSketch024"
  FullyConstrained = true
  sketch-geometry (6):
    g0: LineSegment StartX=19 StartY=38 StartZ=0 EndX=117 EndY=38 EndZ=0
    g1: ArcOfCircle CenterX=19 CenterY=19 CenterZ=0 NormalX=0 NormalY=0 NormalZ=1 AngleXU=0 Radius=19 StartAngle=1.5708 EndAngle=3.14159
    g2: LineSegment StartX=117 StartY=38 StartZ=0 EndX=117 EndY=19 EndZ=0
    g3: LineSegment StartX=98 StartY=1.0161e-12 StartZ=0 EndX=5.22862e-06 EndY=1.0161e-12 EndZ=0
    g4: LineSegment StartX=5.22862e-06 StartY=19 StartZ=0 EndX=5.22862e-06 EndY=1.0161e-12 EndZ=0
    g5: ArcOfCircle CenterX=98 CenterY=19 CenterZ=0 NormalX=0 NormalY=0 NormalZ=1 AngleXU=0 Radius=19 StartAngle=4.71239 EndAngle=6.28319
  constraints (16):
    c: Horizontal(g0)
    c: Distance(g0) = 98
    c: Coincident(g1,g0)
    c: Block(g1)
    c: Coincident(g2,g0)
    c: Vertical(g2)
    c: Distance(g2) = 19
    c: Horizontal(g3)
    c: Coincident(g4,g1)
    c: Vertical(g4)
    c: Coincident(g3,g4)
    c: Block(g3)
    c: Coincident(g5,g2)
    c: Coincident(g5,g3)
    c: Block(g0)
    c: Block(g5)
FEATURE [Sketcher::SketchObject] Sketch080  label="topSketch025"
  FullyConstrained = true
  sketch-geometry (6):
    g0: LineSegment StartX=19 StartY=38 StartZ=0 EndX=117 EndY=38 EndZ=0
    g1: ArcOfCircle CenterX=19 CenterY=19 CenterZ=0 NormalX=0 NormalY=0 NormalZ=1 AngleXU=0 Radius=19 StartAngle=1.5708 EndAngle=3.14159
    g2: LineSegment StartX=117 StartY=38 StartZ=0 EndX=117 EndY=19 EndZ=0
    g3: LineSegment StartX=98 StartY=1.0161e-12 StartZ=0 EndX=5.22862e-06 EndY=1.0161e-12 EndZ=0
    g4: LineSegment StartX=5.22862e-06 StartY=19 StartZ=0 EndX=5.22862e-06 EndY=1.0161e-12 EndZ=0
    g5: ArcOfCircle CenterX=98 CenterY=19 CenterZ=0 NormalX=0 NormalY=0 NormalZ=1 AngleXU=0 Radius=19 StartAngle=4.71239 EndAngle=6.28319
  constraints (16):
    c: Horizontal(g0)
    c: Distance(g0) = 98
    c: Coincident(g1,g0)
    c: Block(g1)
    c: Coincident(g2,g0)
    c: Vertical(g2)
    c: Distance(g2) = 19
    c: Horizontal(g3)
    c: Coincident(g4,g1)
    c: Vertical(g4)
    c: Coincident(g3,g4)
    c: Block(g3)
    c: Coincident(g5,g2)
    c: Coincident(g5,g3)
    c: Block(g0)
    c: Block(g5)
FEATURE [Part::Extrusion] Extrude070  label="sideA004"
  Base = -> Sketch080
  Dir = (0,0,1)
  DirMode = 2
  FaceMakerClass = Part::FaceMakerBullseye
  LengthFwd = 3
  LengthRev = 0
  Placement = pos=(0,0,-2.7) rot=(0,0,1;0rad)
  Solid = true
  Symmetric = false
FEATURE [Sketcher::SketchObject] Sketch081
  FullyConstrained = true
  Placement = pos=(117,19,0) rot=(0.57735,0.57735,0.57735;2.0944rad)
  sketch-geometry (8):
    g0: LineSegment StartX=-49.19 StartY=63.5 StartZ=0 EndX=-49.19 EndY=60.5 EndZ=0
    g1: LineSegment StartX=-49.19 StartY=11.5 StartZ=0 EndX=-49.19 EndY=8.5 EndZ=0
    g2: ArcOfCircle CenterX=-1.5 CenterY=62 CenterZ=0 NormalX=0 NormalY=0 NormalZ=1 AngleXU=0 Radius=1.5 StartAngle=4.71239 EndAngle=7.85398
    g3: ArcOfCircle CenterX=-1.5 CenterY=10 CenterZ=0 NormalX=0 NormalY=0 NormalZ=1 AngleXU=0 Radius=1.5 StartAngle=4.71239 EndAngle=7.85398
    g4: LineSegment StartX=-49.19 StartY=63.5 StartZ=0 EndX=-1.5 EndY=63.5 EndZ=0
    g5: LineSegment StartX=-49.19 StartY=60.5 StartZ=0 EndX=-1.5 EndY=60.5 EndZ=0
    g6: LineSegment StartX=-49.19 StartY=11.5 StartZ=0 EndX=-1.5 EndY=11.5 EndZ=0
    g7: LineSegment StartX=-49.19 StartY=8.5 StartZ=0 EndX=-1.5 EndY=8.5 EndZ=0
  constraints (19):
    c: Vertical(g0)
    c: Distance(g0) = 3
    c: Vertical(g1)
    c: Block(g1)
    c: Block(g2)
    c: Block(g3)
    c: Block(g0)
    c: Coincident(g4,g0)
    c: Coincident(g4,g2)
    c: Horizontal(g4)
    c: Coincident(g5,g0)
    c: Coincident(g5,g2)
    c: Horizontal(g5)
    c: Coincident(g6,g1)
    c: Coincident(g6,g3)
    c: Horizontal(g6)
    c: Coincident(g7,g1)
    c: Coincident(g7,g3)
    c: Horizontal(g7)
FEATURE [Part::Extrusion] Extrude071  label="sideB004"
  Base = -> Sketch079
  Dir = (0,0,1)
  DirMode = 2
  FaceMakerClass = Part::FaceMakerBullseye
  LengthFwd = 3
  LengthRev = 0
  Placement = pos=(0,0,71.7) rot=(0,0,1;0rad)
  Solid = true
  Symmetric = false
FEATURE [Part::MultiFuse] Fusion152  label="removeFromBottom004"
  Placement = pos=(2,0,0) rot=(0,0,1;0rad)
  Shapes = -> [Extrude070,Extrude071]
FEATURE [Part::Extrusion] Extrude072
  Base = -> Sketch081
  Dir = (1,0,0)
  DirMode = 2
  FaceMakerClass = Part::FaceMakerBullseye
  LengthFwd = 10
  LengthRev = 0
  Solid = true
  Symmetric = false
FEATURE [Part::Fillet] Fillet059  label="removeFromtMoreFrontCaseScrewRetainers004"
  Base = -> Extrude072
  Edges = 4 edges r=1.49: [Edge6,Edge11,Edge18,Edge23]
  Placement = pos=(-12,0,0) rot=(0,0,1;0rad)
FEATURE [Sketcher::SketchObject] Sketch082
  FullyConstrained = true
  Placement = pos=(117,19,0) rot=(0.57735,0.57735,0.57735;2.0944rad)
  sketch-geometry (8):
    g0: LineSegment StartX=-49.19 StartY=69.25 StartZ=0 EndX=-49.19 EndY=66.25 EndZ=0
    g1: LineSegment StartX=-49.19 StartY=5.75 StartZ=0 EndX=-49.19 EndY=2.75 EndZ=0
    g2: ArcOfCircle CenterX=-1.5 CenterY=67.75 CenterZ=0 NormalX=0 NormalY=0 NormalZ=1 AngleXU=0 Radius=1.5 StartAngle=4.71239 EndAngle=7.85398
    g3: ArcOfCircle CenterX=-1.5 CenterY=4.25 CenterZ=0 NormalX=0 NormalY=0 NormalZ=1 AngleXU=0 Radius=1.5 StartAngle=4.71239 EndAngle=7.85398
    g4: LineSegment StartX=-49.19 StartY=69.25 StartZ=0 EndX=-1.5 EndY=69.25 EndZ=0
    g5: LineSegment StartX=-49.19 StartY=66.25 StartZ=0 EndX=-1.5 EndY=66.25 EndZ=0
    g6: LineSegment StartX=-49.19 StartY=5.75 StartZ=0 EndX=-1.5 EndY=5.75 EndZ=0
    g7: LineSegment StartX=-49.19 StartY=2.75 StartZ=0 EndX=-1.5 EndY=2.75 EndZ=0
  constraints (19):
    c: Vertical(g0)
    c: Distance(g0) = 3
    c: Block(g0)
    c: Vertical(g1)
    c: Block(g2)
    c: Block(g3)
    c: Block(g1)
    c: Coincident(g4,g0)
    c: Coincident(g4,g2)
    c: Horizontal(g4)
    c: Coincident(g5,g0)
    c: Coincident(g5,g2)
    c: Horizontal(g5)
    c: Coincident(g6,g1)
    c: Coincident(g6,g3)
    c: Horizontal(g6)
    c: Coincident(g7,g1)
    c: Coincident(g7,g3)
    c: Horizontal(g7)
FEATURE [Part::Extrusion] Extrude073
  Base = -> Sketch082
  Dir = (1,0,0)
  DirMode = 2
  FaceMakerClass = Part::FaceMakerBullseye
  LengthFwd = 10
  LengthRev = 0
  Solid = true
  Symmetric = false
FEATURE [Part::Fillet] Fillet060  label="removeFromtMoreFrontCaseScrewRetainers005"
  Base = -> Extrude073
  Edges = 4 edges r=1.49: [Edge6,Edge11,Edge18,Edge23]
  Placement = pos=(-4,0,0) rot=(0,0,1;0rad)
FEATURE [Part::Revolution] Revolve163  label="backCaseScrewRetainer004"
  Angle = 360
  Axis = (0,1,0)
  Base = (0,0,0)
  FaceMakerClass = Part::FaceMakerBullseye
  Placement = pos=(12.5,3,62) rot=(0,0,1;0rad)
  Solid = false
  Source = -> Face149
  Symmetric = false
FEATURE [Part::Revolution] Revolve164  label="frontCaseScrewRetainer006"
  Angle = 360
  Axis = (0,1,0)
  Base = (0,0,0)
  FaceMakerClass = Part::FaceMakerBullseye
  Placement = pos=(89.5,3,68.5) rot=(0,0,1;0rad)
  Solid = false
  Source = -> Face151
  Symmetric = false
FEATURE [Part::Revolution] Revolve165  label="frontCaseScrewRetainer007"
  Angle = 360
  Axis = (0,1,0)
  Base = (0,0,0)
  FaceMakerClass = Part::FaceMakerBullseye
  Placement = pos=(89.5,3,3.5) rot=(0,0,1;0rad)
  Solid = false
  Source = -> Face152
  Symmetric = false
FEATURE [Part::Revolution] Revolve166  label="backCaseScrewRetainer005"
  Angle = 360
  Axis = (0,1,0)
  Base = (0,0,0)
  FaceMakerClass = Part::FaceMakerBullseye
  Placement = pos=(12.5,3,10) rot=(0,0,1;0rad)
  Solid = false
  Source = -> Face150
  Symmetric = false
FEATURE [Part::Revolution] Revolve167  label="moreFrontCaseScrewRetainer006"
  Angle = 360
  Axis = (0,1,0)
  Base = (0,0,0)
  FaceMakerClass = Part::FaceMakerBullseye
  Placement = pos=(109.5,4.5,68.5) rot=(0,0,1;0rad)
  Solid = false
  Source = -> Face153
  Symmetric = false
FEATURE [Part::Revolution] Revolve168  label="moreFrontCaseScrewRetainer007"
  Angle = 360
  Axis = (0,1,0)
  Base = (0,0,0)
  FaceMakerClass = Part::FaceMakerBullseye
  Placement = pos=(109.5,4.5,3.5) rot=(0,0,1;0rad)
  Solid = false
  Source = -> Face154
  Symmetric = false
FEATURE [Part::MultiFuse] Fusion151  label="screwRetainers003"
  Shapes = -> [Revolve168,Revolve167,Revolve166,Revolve165,Revolve164,Revolve163]
FEATURE [Part::Cut] Cut069  label="screwRetainers004"
  Base = -> Fusion151
  Tool = -> Fusion152
FEATURE [Part::Cut] Cut070
  Base = -> Cut069
  Tool = -> Fillet060
FEATURE [Part::Cut] Cut071  label="screwPillars001"
  Base = -> Cut070
  Tool = -> Fillet059
FEATURE [Part::MultiFuse] Fusion153  label="bottom024"
  Shapes = -> [Fusion149,Cut071]
FEATURE [Part::Cylinder] Cylinder067
  Angle = 360
  AttacherType = Attacher::AttachEngine3D
  Height = 10
  Placement = pos=(20.65,12,4.68) rot=(1,0,0;1.5708rad)
  Radius = 2
FEATURE [Part::Cylinder] Cylinder068
  Angle = 360
  AttacherType = Attacher::AttachEngine3D
  Height = 10
  Placement = pos=(20.65,12,67.38) rot=(1,0,0;1.5708rad)
  Radius = 2
FEATURE [Part::Cylinder] Cylinder069
  Angle = 360
  AttacherType = Attacher::AttachEngine3D
  Height = 10
  Placement = pos=(77.15,12,67.38) rot=(1,0,0;1.5708rad)
  Radius = 2
FEATURE [Part::Cylinder] Cylinder070
  Angle = 360
  AttacherType = Attacher::AttachEngine3D
  Height = 10
  Placement = pos=(77.15,12,4.68) rot=(1,0,0;1.5708rad)
  Radius = 2
FEATURE [Part::MultiFuse] Fusion154  label="removeFromThreadedInsertHousing001"
  Shapes = -> [Cylinder069,Cylinder068,Cylinder067,Cylinder070]
FEATURE [Part::Cut] Cut072  label="bottom025"
  Base = -> Fusion153
  Tool = -> Fusion154
FEATURE [Image::ImagePlane] ImagePlane
  XSize = 339
  YSize = 72
FEATURE [Sketcher::SketchObject] Sketch083
  FullyConstrained = true
  MapMode = 5
  Support = -> [XY_Plane]
  sketch-geometry (245):
    g0: LineSegment StartX=-151.619 StartY=28.8932 StartZ=0 EndX=-140.819 EndY=28.8932 EndZ=0
    g1: LineSegment StartX=-151.619 StartY=24.0313 StartZ=0 EndX=-151.619 EndY=28.8932 EndZ=0
    g2: LineSegment StartX=-140.819 StartY=17.7713 StartZ=0 EndX=-151.619 EndY=17.7713 EndZ=0
    g3: LineSegment StartX=-151.619 StartY=17.7713 StartZ=0 EndX=-151.619 EndY=22.6313 EndZ=0
    g4: LineSegment StartX=-151.619 StartY=22.6313 StartZ=0 EndX=-145.128 EndY=22.6313 EndZ=0
    g5: LineSegment StartX=-145.128 StartY=24.0313 StartZ=0 EndX=-140.819 EndY=28.8932 EndZ=0
    g6: LineSegment StartX=-145.128 StartY=22.6313 StartZ=0 EndX=-140.819 EndY=17.7713 EndZ=0
    g7: ArcOfCircle CenterX=-155.157 CenterY=23.3323 CenterZ=0 NormalX=0 NormalY=0 NormalZ=1 AngleXU=0 Radius=6.92354 StartAngle=1.03434 EndAngle=5.24885
    g8: ArcOfCircle CenterX=-155.157 CenterY=23.3323 CenterZ=0 NormalX=0 NormalY=0 NormalZ=1 AngleXU=0 Radius=12.6269 StartAngle=1.28675 EndAngle=4.99643
    g9: LineSegment StartX=-151.619 StartY=35.4532 StartZ=0 EndX=-151.619 EndY=29.2832 EndZ=0
    g10: LineSegment StartX=-151.619 StartY=17.3813 StartZ=0 EndX=-151.619 EndY=11.2113 EndZ=0
    g11-g21: Circle x11 (B-spline internal-alignment scaffolding for g22; pole/knot coordinates omitted)
    g22: BSplineCurve PolesCount=11 KnotsCount=9 Degree=3 IsPeriodic=0
    g23-g31: GeomPoint x9 (B-spline internal-alignment scaffolding for g22; pole/knot coordinates omitted)
    g32-g49: Circle x18 (B-spline internal-alignment scaffolding for g50; pole/knot coordinates omitted)
    g50: BSplineCurve PolesCount=18 KnotsCount=16 Degree=3 IsPeriodic=0
    g51-g66: GeomPoint x16 (B-spline internal-alignment scaffolding for g50; pole/knot coordinates omitted)
    g67: LineSegment StartX=-117.124 StartY=30.093 StartZ=0 EndX=-117.603 EndY=26.5272 EndZ=0
    g68: LineSegment StartX=-117.603 StartY=17.8472 StartZ=0 EndX=-117.124 EndY=14.2659 EndZ=0
    g69: Ellipse CenterX=-109.671 CenterY=20.025 CenterZ=0 NormalX=0 NormalY=0 NormalZ=1 MajorRadius=3.34798 MinorRadius=2.71052 AngleXU=-1.56793
    g70: GeomPoint X=-109.666 Y=18.0598 Z=0
    g71: GeomPoint X=-109.677 Y=21.9902 Z=0
    g72: Ellipse CenterX=-109.671 CenterY=20.0123 CenterZ=0 NormalX=0 NormalY=0 NormalZ=1 MajorRadius=6.93002 MinorRadius=6.36273 AngleXU=-3.13976
    g73: GeomPoint X=-112.417 Y=20.0073 Z=0
    g74: GeomPoint X=-106.925 Y=20.0173 Z=0
    g75: Ellipse CenterX=-51.7682 CenterY=20.1463 CenterZ=0 NormalX=0 NormalY=0 NormalZ=1 MajorRadius=3.19279 MinorRadius=2.71052 AngleXU=-1.52774
    g76: GeomPoint X=-51.6955 Y=18.4606 Z=0
    g77: GeomPoint X=-51.8408 Y=21.832 Z=0
    g78: GeomPoint X=-54.5142 Y=20.1413 Z=0
    g79: GeomPoint X=-49.0221 Y=20.1513 Z=0
    g80: Ellipse CenterX=-51.7682 CenterY=20.1463 CenterZ=0 NormalX=0 NormalY=0 NormalZ=1 MajorRadius=6.93002 MinorRadius=6.36273 AngleXU=-3.13976
    g81: Ellipse CenterX=-22.8436 CenterY=20.1783 CenterZ=0 NormalX=0 NormalY=0 NormalZ=1 MajorRadius=3.31512 MinorRadius=2.71052 AngleXU=-1.60214
    g82: GeomPoint X=-22.9034 Y=18.2706 Z=0
    g83: GeomPoint X=-22.7838 Y=22.0861 Z=0
    g84: GeomPoint X=-25.5897 Y=20.1733 Z=0
    g85: GeomPoint X=-20.0976 Y=20.1833 Z=0
    g86: Ellipse CenterX=-22.8436 CenterY=20.1783 CenterZ=0 NormalX=0 NormalY=0 NormalZ=1 MajorRadius=6.93002 MinorRadius=6.36273 AngleXU=-3.13976
    g87: LineSegment StartX=-101.889 StartY=14.1107 StartZ=0 EndX=-97.7455 EndY=14.1107 EndZ=0
    g88: LineSegment StartX=-93.8155 StartY=14.1107 StartZ=0 EndX=-89.6755 EndY=14.1107 EndZ=0
    g89: LineSegment StartX=-85.7455 StartY=14.1107 StartZ=0 EndX=-81.6055 EndY=14.1107 EndZ=0
    g90: LineSegment StartX=-101.889 StartY=14.1107 StartZ=0 EndX=-101.889 EndY=25.9907 EndZ=0
    g91: LineSegment StartX=-101.889 StartY=25.9907 StartZ=0 EndX=-97.8594 EndY=25.9907 EndZ=0
    g92: LineSegment StartX=-97.8594 StartY=25.9907 StartZ=0 EndX=-97.8594 EndY=24.0907 EndZ=0
    g93: LineSegment StartX=-97.7455 StartY=14.1107 StartZ=0 EndX=-97.7455 EndY=19.9107 EndZ=0
    g94: LineSegment StartX=-89.6755 StartY=14.1107 StartZ=0 EndX=-89.6755 EndY=19.9107 EndZ=0
    g95: LineSegment StartX=-93.8155 StartY=14.1107 StartZ=0 EndX=-93.8155 EndY=21.0107 EndZ=0
    g96-g106: Circle x11 (B-spline internal-alignment scaffolding for g107; pole/knot coordinates omitted)
    g107: BSplineCurve PolesCount=11 KnotsCount=9 Degree=3 IsPeriodic=0
    g108-g116: GeomPoint x9 (B-spline internal-alignment scaffolding for g107; pole/knot coordinates omitted)
    g117: BSplineCurve PolesCount=11 KnotsCount=9 Degree=3 IsPeriodic=0
    g118-g125: Circle x8 (B-spline internal-alignment scaffolding for g126; pole/knot coordinates omitted)
    g126: BSplineCurve PolesCount=8 KnotsCount=6 Degree=3 IsPeriodic=0
    g127-g132: GeomPoint x6 (B-spline internal-alignment scaffolding for g126; pole/knot coordinates omitted)
    g133: BSplineCurve PolesCount=8 KnotsCount=6 Degree=3 IsPeriodic=0
    g134: LineSegment StartX=-85.7455 StartY=21.0107 StartZ=0 EndX=-85.7455 EndY=14.1107 EndZ=0
    g135: LineSegment StartX=-80.0879 StartY=14.1107 StartZ=0 EndX=-75.944 EndY=14.1107 EndZ=0
    g136: LineSegment StartX=-72.014 StartY=14.1107 StartZ=0 EndX=-67.874 EndY=14.1107 EndZ=0
    g137: LineSegment StartX=-63.944 StartY=14.1107 StartZ=0 EndX=-59.804 EndY=14.1107 EndZ=0
    g138: LineSegment StartX=-80.0879 StartY=14.1107 StartZ=0 EndX=-80.0879 EndY=25.9907 EndZ=0
    g139: LineSegment StartX=-80.0879 StartY=25.9907 StartZ=0 EndX=-76.0579 EndY=25.9907 EndZ=0
    g140: LineSegment StartX=-76.0579 StartY=25.9907 StartZ=0 EndX=-76.0579 EndY=24.0907 EndZ=0
    g141: LineSegment StartX=-75.944 StartY=14.1107 StartZ=0 EndX=-75.944 EndY=19.9107 EndZ=0
    g142: LineSegment StartX=-67.874 StartY=14.1107 StartZ=0 EndX=-67.874 EndY=19.9107 EndZ=0
    g143: LineSegment StartX=-72.014 StartY=14.1107 StartZ=0 EndX=-72.014 EndY=21.0107 EndZ=0
    g144-g148: Circle x5 (B-spline internal-alignment scaffolding for g149; pole/knot coordinates omitted)
    g149: BSplineCurve PolesCount=11 KnotsCount=9 Degree=3 IsPeriodic=0
    g150-g158: GeomPoint x9 (B-spline internal-alignment scaffolding for g149; pole/knot coordinates omitted)
    g159: BSplineCurve PolesCount=11 KnotsCount=9 Degree=3 IsPeriodic=0
    g160-g167: Circle x8 (B-spline internal-alignment scaffolding for g168; pole/knot coordinates omitted)
    g168: BSplineCurve PolesCount=8 KnotsCount=6 Degree=3 IsPeriodic=0
    g169-g174: GeomPoint x6 (B-spline internal-alignment scaffolding for g168; pole/knot coordinates omitted)
    g175: BSplineCurve PolesCount=8 KnotsCount=6 Degree=3 IsPeriodic=0
    g176: LineSegment StartX=-63.944 StartY=21.0107 StartZ=0 EndX=-63.944 EndY=14.1107 EndZ=0
    g177: LineSegment StartX=-59.804 StartY=14.1107 StartZ=0 EndX=-59.804 EndY=21.5868 EndZ=0
    g178: BSplineCurve PolesCount=4 KnotsCount=2 Degree=3 IsPeriodic=0
    g179: GeomPoint X=-59.804 Y=21.5868 Z=0
    g180: GeomPoint X=-60.2379 Y=24.0907 Z=0
    g181: LineSegment StartX=-81.6055 StartY=14.1107 StartZ=0 EndX=-81.6055 EndY=21.5868 EndZ=0
    g182: LineSegment StartX=-151.619 StartY=24.0313 StartZ=0 EndX=-145.128 EndY=24.0313 EndZ=0
    g183: Circle CenterX=-82.0394 CenterY=24.0907 CenterZ=0 NormalX=0 NormalY=0 NormalZ=1 AngleXU=0 Radius=1
    g184: Circle CenterX=-81.7131 CenterY=23.2736 CenterZ=0 NormalX=0 NormalY=0 NormalZ=1 AngleXU=0 Radius=1
    g185: Circle CenterX=-81.6055 CenterY=21.5868 CenterZ=0 NormalX=0 NormalY=0 NormalZ=1 AngleXU=0 Radius=1
    g186: BSplineCurve PolesCount=3 KnotsCount=2 Degree=2 IsPeriodic=0
    g187: GeomPoint X=-82.0394 Y=24.0907 Z=0
    g188: GeomPoint X=-81.6055 Y=21.5868 Z=0
    g189: Ellipse CenterX=-37.3522 CenterY=19.9515 CenterZ=0 NormalX=0 NormalY=0 NormalZ=1 MajorRadius=2.99755 MinorRadius=2.49 AngleXU=1.5708
    g190: GeomPoint X=-37.3522 Y=21.6203 Z=0
    g191: GeomPoint X=-37.3522 Y=18.2826 Z=0
    g192: ArcOfEllipse CenterX=-38.7647 CenterY=20.06 CenterZ=0 NormalX=0 NormalY=0 NormalZ=1 MajorRadius=6.30025 MinorRadius=5.3849 AngleXU=1.57276 StartAngle=5.50632 EndAngle=10.3035
    g193: GeomPoint X=-38.7711 Y=23.3304 Z=0
    g194: GeomPoint X=-38.7583 Y=16.7895 Z=0
    g195: LineSegment StartX=-34.6109 StartY=14.1107 StartZ=0 EndX=-30.8984 EndY=14.1107 EndZ=0
    g196: LineSegment StartX=-30.8984 StartY=14.1107 StartZ=0 EndX=-30.8984 EndY=31.1784 EndZ=0
    g197: LineSegment StartX=-30.8984 StartY=31.1784 StartZ=0 EndX=-34.9984 EndY=31.1784 EndZ=0
    g198: LineSegment StartX=-34.9984 StartY=24.5602 StartZ=0 EndX=-34.9984 EndY=31.1784 EndZ=0
    g199: LineSegment StartX=-34.6109 StartY=16.0476 StartZ=0 EndX=-34.6109 EndY=14.1107 EndZ=0
    g200: LineSegment StartX=-14.8781 StartY=14.1107 StartZ=0 EndX=-10.5106 EndY=14.1107 EndZ=0
    g201: LineSegment StartX=-14.8781 StartY=14.1107 StartZ=0 EndX=-14.8781 EndY=25.8504 EndZ=0
    g202: LineSegment StartX=-14.8781 StartY=25.8504 StartZ=0 EndX=-10.8534 EndY=25.8504 EndZ=0
    g203: LineSegment StartX=-10.8534 StartY=25.8504 StartZ=0 EndX=-10.8534 EndY=24.0923 EndZ=0
    g204: LineSegment StartX=-10.5106 StartY=14.1107 StartZ=0 EndX=-10.5106 EndY=19.7752 EndZ=0
    g205: LineSegment StartX=-5.96397 StartY=25.9304 StartZ=0 EndX=-5.96397 EndY=22.574 EndZ=0
    g206-g214: Circle x9 (B-spline internal-alignment scaffolding for g215; pole/knot coordinates omitted)
    g215: BSplineCurve PolesCount=9 KnotsCount=7 Degree=3 IsPeriodic=0
    g216-g222: GeomPoint x7 (B-spline internal-alignment scaffolding for g215; pole/knot coordinates omitted)
    g223-g232: Circle x10 (B-spline internal-alignment scaffolding for g233; pole/knot coordinates omitted)
    g233: BSplineCurve PolesCount=10 KnotsCount=8 Degree=3 IsPeriodic=0
    g234-g241: GeomPoint x8 (B-spline internal-alignment scaffolding for g233; pole/knot coordinates omitted)
    g242: LineSegment StartX=-1.58923 StartY=21.0696 StartZ=0 EndX=2.62034 EndY=21.0696 EndZ=0
    g243: LineSegment StartX=-1.55856 StartY=18.7342 StartZ=0 EndX=6.45946 EndY=18.7342 EndZ=0
    g244: LineSegment StartX=5.29231 StartY=17.386 StartZ=0 EndX=5.29231 EndY=14.3674 EndZ=0
  constraints (231):
    c: Coincident(g1,g0)
    c: Horizontal(g0)
    c: Vertical(g1)
    c: Coincident(g2,g3)
    c: Coincident(g3,g4)
    c: Horizontal(g4)
    c: Horizontal(g2)
    c: Vertical(g3)
    c: Block(g1)
    c: Distance(g3) = 4.86
    c: Block(g4)
    c: Distance(g0) = 10.8
    c: Distance(g2) = 10.8
    c: Coincident(g5,g0)
    c: Coincident(g6,g4)
    c: Coincident(g6,g2)
    c: Block(g8)
    c: Block(g7)
    c: Coincident(g9,g8)
    c: Coincident(g9,g7)
    c: Vertical(g9)
    c: Coincident(g10,g7)
    c: Coincident(g10,g8)
    c: Vertical(g10)
    c: Weight(g11) = 1
    c: Equal(g11, g12-g21) x10
    c: InternalAlignment(g11-g21 -> g22) x11
    c: InternalAlignment(g23-g31 -> g22) x9
    c: Block(g22)
    c: Weight(g32) = 1
    c: Equal(g32, g33-g49) x17
    c: InternalAlignment(g32-g49 -> g50) x18
    c: InternalAlignment(g51-g66 -> g50) x16
    c: Block(g50)
    c: Coincident(g67,g50)
    c: Coincident(g67,g22)
    c: Coincident(g68,g22)
    c: Coincident(g68,g50)
    c: InternalAlignment(g70,g69)
    c: InternalAlignment(g71,g69)
    c: Block(g69)
    c: InternalAlignment(g73,g72)
    c: InternalAlignment(g74,g72)
    c: Block(g72)
    c: InternalAlignment(g76,g75)
    c: InternalAlignment(g77,g75)
    c: InternalAlignment(g78,g80)
    c: InternalAlignment(g79,g80)
    c: Block(g80)
    c: Coincident(g75,g80)
    c: Block(g75)
    c: InternalAlignment(g82,g81)
    c: InternalAlignment(g83,g81)
    c: InternalAlignment(g84,g86)
    c: InternalAlignment(g85,g86)
    c: Block(g86)
    c: Coincident(g81,g86)
    c: Block(g81)
    c: Horizontal(g87)
    c: Block(g87)
    c: Horizontal(g88)
    c: Distance(g88) = 4.14
    c: Horizontal(g89)
    c: Equal(g88,g89) = 4.14
    c: Block(g89)
    c: Block(g88)
    c: Coincident(g90,g87)
    c: Vertical(g90)
    c: Distance(g90) = 11.88
    c: Coincident(g91,g90)
    c: Horizontal(g91)
    c: Coincident(g92,g91)
    c: Vertical(g92)
    c: Distance(g91) = 4.03
    c: Distance(g92) = 1.9
    c: Coincident(g93,g87)
    c: Vertical(g93)
    c: Vertical(g94)
    c: Coincident(g94,g88)
    c: Distance(g93) = 5.8
    c: Distance(g94) = 5.8
    c: Vertical(g95)
    c: Coincident(g95,g88)
    c: Distance(g95) = 6.9
    c: Coincident(g107,g92)
    c: Weight(g96) = 1
    c: Equal(g96, g97-g106) x10
    c: InternalAlignment(g96-g106 -> g107) x11
    c: InternalAlignment(g108-g116 -> g107) x9
    c: Block(g107)
    c: Block(g117)
    c: Coincident(g126,g93)
    c: Weight(g118) = 1
    c: Equal(g118, g119-g125) x7
    c: Coincident(g126,g95)
    c: InternalAlignment(g118-g125 -> g126) x8
    c: InternalAlignment(g127-g132 -> g126) x6
    c: Coincident(g133,g94)
    c: Block(g126)
    c: Block(g133)
    c: Coincident(g134,g133)
    c: Coincident(g134,g89)
    c: Vertical(g134)
    c: Horizontal(g135)
    c: Block(g135)
    c: Horizontal(g136)
    c: Equal(g88,g136) = 4.14
    c: Horizontal(g137)
    c: Equal(g136,g137) = 4.14
    c: Block(g137)
    c: Block(g136)
    c: Coincident(g138,g135)
    c: Vertical(g138)
    c: Equal(g90,g138) = 11.88
    c: Coincident(g139,g138)
    c: Horizontal(g139)
    c: Coincident(g140,g139)
    c: Vertical(g140)
    c: Equal(g91,g139) = 4.03
    c: Equal(g92,g140) = 1.9
    c: Coincident(g141,g135)
    c: Vertical(g141)
    c: Vertical(g142)
    c: Coincident(g142,g136)
    c: Equal(g93,g141) = 5.8
    c: Equal(g94,g142) = 5.8
    c: Vertical(g143)
    c: Coincident(g143,g136)
    c: Equal(g95,g143) = 6.9
    c: Coincident(g149,g140)
    c: Equal(g96,g144) = 1
    c: Equal(g144, g145-g148) x4
    c: InternalAlignment(g144-g148 -> g149) x5
    c: InternalAlignment(g150-g158 -> g149) x9
    c: Block(g149)
    c: Block(g159)
    c: Coincident(g168,g141)
    c: Equal(g118,g160) = 1
    c: Equal(g160, g161-g167) x7
    c: Coincident(g168,g143)
    c: InternalAlignment(g160-g167 -> g168) x8
    c: InternalAlignment(g169-g174 -> g168) x6
    c: Coincident(g175,g142)
    c: Block(g168)
    c: Block(g175)
    c: Coincident(g176,g175)
    c: Coincident(g176,g137)
    c: Vertical(g176)
    c: Coincident(g177,g137)
    c: Vertical(g177)
    c: Coincident(g178,g177)
    c: Coincident(g178,g159)
    c: InternalAlignment(g179,g178)
    c: InternalAlignment(g180,g178)
    c: Block(g178)
    c: Vertical(g181)
    c: Coincident(g181,g89)
    c: Block(g5)
    c: Coincident(g182,g1)
    c: Coincident(g182,g5)
    c: Horizontal(g182)
    c: Coincident(g186,g117)
    c: Weight(g183) = 1
    c: Equal(g183,g184)
    c: Equal(g183,g185)
    c: Coincident(g186,g181)
    c: InternalAlignment(g183,g186)
    c: InternalAlignment(g184,g186)
    c: InternalAlignment(g185,g186)
    c: InternalAlignment(g187,g186)
    c: InternalAlignment(g188,g186)
    c: Block(g186)
    c: InternalAlignment(g190,g189)
    c: InternalAlignment(g191,g189)
    c: Block(g189)
    c: InternalAlignment(g193,g192)
    c: InternalAlignment(g194,g192)
    c: Block(g192)
    c: Horizontal(g195)
    c: Block(g195)
    c: Coincident(g196,g195)
    c: Vertical(g196)
    c: Block(g196)
    c: Distance(g195) = 3.71244
    c: Coincident(g197,g196)
    c: Horizontal(g197)
    c: Distance(g197) = 4.1
    c: Coincident(g198,g192)
    c: Coincident(g198,g197)
    c: Vertical(g198)
    c: Block(g198)
    c: Coincident(g199,g192)
    c: Coincident(g199,g195)
    c: Vertical(g199)
    c: Block(g199)
    c: Horizontal(g200)
    c: Block(g200)
    c: Coincident(g201,g200)
    c: Vertical(g201)
    c: Block(g201)
    c: Coincident(g202,g201)
    c: Horizontal(g202)
    c: Block(g202)
    c: Coincident(g203,g202)
    c: Vertical(g203)
    c: Block(g203)
    c: Coincident(g204,g200)
    c: Vertical(g204)
    c: Block(g204)
    c: Coincident(g215,g203)
    c: Weight(g206) = 1
    c: Equal(g206, g207-g214) x8
    c: Coincident(g215,g205)
    c: InternalAlignment(g206-g214 -> g215) x9
    c: InternalAlignment(g216-g222 -> g215) x7
    c: Coincident(g233,g204)
    c: Weight(g223) = 1
    c: Equal(g223, g224-g232) x9
    c: Coincident(g233,g205)
    c: InternalAlignment(g223-g232 -> g233) x10
    c: InternalAlignment(g234-g241 -> g233) x8
    c: Vertical(g205)
    c: Block(g205)
    c: Block(g215)
    c: Block(g233)
    c: Horizontal(g242)
    c: Horizontal(g243)
    c: Block(g242)
    c: Block(g243)
    c: Vertical(g244)
    c: Block(g244)
FEATURE [PartDesign::Body] Body
  Group = -> [Sketch083]
  Origin = -> Origin
FEATURE [Sketcher::SketchObject] Sketch084
  FullyConstrained = true
  MapMode = 5
  Support = -> [XY_Plane001]
FEATURE [PartDesign::Body] Body001
  Group = -> [Sketch084]
  Origin = -> Origin001
